FCSTD DOCUMENT  (FreeCAD 0.19R24276 (Git))
Label: bazovina_058
License: All rights reserved
LicenseURL: http://en.wikipedia.org/wiki/All_rights_reserved
objects: Part::Cylinder×904, Part::Compound×379, Part::Cut×288, Part::Box×199, Part::FeaturePython×44, Part::Chamfer×22, Part::Torus×6, Part::Fillet×6, Sketcher::SketchObject×6, Part::Mirroring×5, Part::MultiFuse×4, PartDesign::Pad×3, PartDesign::Body×3, Part::Extrusion×3, Mesh::Feature×2
note: 1875 computed .brp shape members not serialized (recipe doc carries the construction recipe); baked Part::Feature solids carry a one-line shape summary decoded from their .brp

FEATURE [Part::Cylinder] Cylinder074  label="Válec074"
  Angle = 360
  AttacherType = Attacher::AttachEngine3D
  Height = 100
  Placement = pos=(2,3,3) rot=(0,1,0;1.5708rad)
  Radius = 1.5
FEATURE [Part::Cylinder] Cylinder075  label="Válec075"
  Angle = 360
  AttacherType = Attacher::AttachEngine3D
  Height = 100
  Placement = pos=(2,3,3) rot=(0,1,0;1.5708rad)
  Radius = 1.5
FEATURE [Part::Box] Box029  label="Krychle029"
  AttacherType = Attacher::AttachEngine3D
  Height = 6
  Length = 2
  Width = 6
FEATURE [Part::Compound] Compound127
  Links = -> [Box029,Cylinder074]
  Placement = pos=(1536,-22,-8) rot=(0,0,1;0rad)
FEATURE [Part::Box] Box030  label="Krychle030"
  AttacherType = Attacher::AttachEngine3D
  Height = 6
  Length = 2
  Width = 6
FEATURE [Part::Box] Box031  label="Krychle031"
  AttacherType = Attacher::AttachEngine3D
  Height = 6
  Length = 2
  Width = 6
FEATURE [Part::Cylinder] Cylinder076  label="Válec076"
  Angle = 360
  AttacherType = Attacher::AttachEngine3D
  Height = 100
  Placement = pos=(2,3,3) rot=(0,1,0;1.5708rad)
  Radius = 1.5
FEATURE [Part::Compound] Compound125
  Links = -> [Box030,Cylinder076]
  Placement = pos=(1532,-54,4) rot=(0,0,1;0rad)
FEATURE [Part::Cylinder] Cylinder077  label="Válec077"
  Angle = 360
  AttacherType = Attacher::AttachEngine3D
  Height = 100
  Placement = pos=(2,3,3) rot=(0,1,0;1.5708rad)
  Radius = 1.5
FEATURE [Part::Compound] Compound128
  Links = -> [Box031,Cylinder077]
  Placement = pos=(1536,16,-8) rot=(0,0,1;0rad)
FEATURE [Part::Box] Box032  label="Krychle032"
  AttacherType = Attacher::AttachEngine3D
  Height = 6
  Length = 2
  Width = 6
FEATURE [Part::Compound] Compound129
  Links = -> [Box032,Cylinder075]
  Placement = pos=(1532,48,4) rot=(0,0,1;0rad)
FEATURE [Part::Compound] Compound126
  Links = -> [Compound129,Compound128,Compound127,Compound125,Box032,Cylinder075,Box031,Cylinder077,Box029,Cylinder074]
  Placement = pos=(0,-1300,0) rot=(0,0,1;1.5708rad)
FEATURE [Part::Cylinder] Cylinder078  label="Válec078"
  Angle = 360
  AttacherType = Attacher::AttachEngine3D
  Height = 4
  Placement = pos=(-4,3,3) rot=(0,1,0;1.5708rad)
  Radius = 1.5
FEATURE [Part::Compound] Compound130
  Links = -> [Cylinder078]
  Placement = pos=(1532,48,4) rot=(0,0,1;0rad)
FEATURE [Part::Cylinder] Cylinder080  label="Válec080"
  Angle = 360
  AttacherType = Attacher::AttachEngine3D
  Height = 4
  Placement = pos=(-4,3,3) rot=(0,1,0;1.5708rad)
  Radius = 1.5
FEATURE [Part::Compound] Compound133
  Links = -> [Cylinder080]
  Placement = pos=(1532,-54,4) rot=(0,0,1;0rad)
FEATURE [Part::Cylinder] Cylinder081  label="Válec081"
  Angle = 360
  AttacherType = Attacher::AttachEngine3D
  Height = 4
  Placement = pos=(-4,3,3) rot=(0,1,0;1.5708rad)
  Radius = 1.5
FEATURE [Part::Compound] Compound132
  Links = -> [Cylinder081]
  Placement = pos=(1536,16,-8) rot=(0,0,1;0rad)
FEATURE [Part::Cylinder] Cylinder052  label="Válec052"
  Angle = 360
  AttacherType = Attacher::AttachEngine3D
  Height = 50
  Placement = pos=(250,0,-15) rot=(0,0,1;0rad)
  Radius = 1.5
FEATURE [Part::Cylinder] Cylinder053  label="Válec053"
  Angle = 360
  AttacherType = Attacher::AttachEngine3D
  Height = 50
  Placement = pos=(200,50,-15) rot=(0,0,1;1.5708rad)
  Radius = 1.5
FEATURE [Part::Cylinder] Cylinder054  label="Válec054"
  Angle = 360
  AttacherType = Attacher::AttachEngine3D
  Height = 50
  Placement = pos=(235.36,35.36,-16) rot=(0,0,1;0.785398rad)
  Radius = 1.5
FEATURE [Part::Cylinder] Cylinder055  label="Válec055"
  Angle = 360
  AttacherType = Attacher::AttachEngine3D
  Height = 40
  Placement = pos=(202,50,-30) rot=(0,0,1;0rad)
  Radius = 12
FEATURE [Part::Cylinder] Cylinder056  label="Válec056"
  Angle = 360
  AttacherType = Attacher::AttachEngine3D
  Height = 50
  Placement = pos=(235.36,35.36,-40) rot=(0,0,1;0.785398rad)
  Radius = 4
FEATURE [Part::Compound] Compound082
  Links = -> [Cylinder052,Cylinder054,Cylinder053,Cylinder056]
FEATURE [Part::Mirroring] mirror005  label="Compound075 (mirrored)001"
  Base = (0,0,0)
  Normal = (1e-16,-1,0)
  Placement = pos=(500,0,0) rot=(0,0,1;0rad)
  Source = -> Compound082
FEATURE [Part::Cylinder] Cylinder057  label="Válec057"
  Angle = 360
  AttacherType = Attacher::AttachEngine3D
  Height = 40
  Placement = pos=(214,56,-30) rot=(0,0,1;0rad)
  Radius = 12
FEATURE [Part::Box] Box020  label="Krychle020"
  AttacherType = Attacher::AttachEngine3D
  Height = 28
  Length = 46
  Placement = pos=(200,32,-8) rot=(0,0,1;0rad)
  Width = 22
FEATURE [Part::Box] Box021  label="Krychle021"
  AttacherType = Attacher::AttachEngine3D
  Height = 28
  Length = 14
  Placement = pos=(232,0,-8) rot=(0,0,1;0rad)
  Width = 32
FEATURE [Part::Compound] Compound080
  Links = -> [Box021,Box020]
FEATURE [Part::FeaturePython] mirror003_child004  label="Compound075 (mirrored).004"  # WARN: FeaturePython — macro-defined, semantics opaque (R4)
  Base = -> mirror005
  FilterType = 1
  Invert = false
  OverrideMaxVal = 0
  WindowFrom = 80
  WindowTo = 100
  items = 1
FEATURE [Part::FeaturePython] mirror003_child005  label="Compound075 (mirrored).005"  # WARN: FeaturePython — macro-defined, semantics opaque (R4)
  Base = -> mirror005
  FilterType = 1
  Invert = false
  OverrideMaxVal = 0
  WindowFrom = 80
  WindowTo = 100
  items = 0
FEATURE [Part::FeaturePython] mirror003_child006  label="Compound075 (mirrored).006"  # WARN: FeaturePython — macro-defined, semantics opaque (R4)
  Base = -> mirror005
  FilterType = 1
  Invert = false
  OverrideMaxVal = 0
  WindowFrom = 80
  WindowTo = 100
  items = 2
FEATURE [Part::Compound] Compound083
  Links = -> [mirror003_child004,mirror003_child005,mirror003_child006]
FEATURE [Part::FeaturePython] mirror003_child007  label="Compound075 (mirrored).007"  # WARN: FeaturePython — macro-defined, semantics opaque (R4)
  Base = -> mirror005
  FilterType = 1
  Invert = false
  OverrideMaxVal = 0
  WindowFrom = 80
  WindowTo = 100
  items = 3
FEATURE [Part::Cylinder] Cylinder058  label="Válec058"
  Angle = 360
  AttacherType = Attacher::AttachEngine3D
  Height = 40
  Placement = pos=(256,0,-30) rot=(0,0,1;0rad)
  Radius = 10
FEATURE [Part::Compound] Compound081
  Links = -> [Cylinder058,Cylinder057]
FEATURE [Part::Cut] Cut034
  Base = -> Compound080
  Tool = -> Compound081
FEATURE [Part::Cut] Cut035
  Base = -> Cut034
  Tool = -> Cylinder055
FEATURE [Part::Mirroring] mirror004  label="Cut (mirrored)002"
  Base = (40,0,0)
  Normal = (1e-16,-1,0)
  Placement = pos=(500,0,0) rot=(0,0,1;0rad)
  Source = -> Cut035
FEATURE [Part::Cut] Cut036
  Base = -> mirror004
  Tool = -> mirror003_child007
FEATURE [Part::Cut] Cut037
  Base = -> Cut036
  Placement = pos=(800,0,0) rot=(0,0,1;0rad)
  Tool = -> Compound083
FEATURE [Part::Cylinder] Cylinder059  label="Válec059"
  Angle = 360
  AttacherType = Attacher::AttachEngine3D
  Height = 50
  Placement = pos=(235.36,35.36,-16) rot=(0,0,1;0.785398rad)
  Radius = 1.5
FEATURE [Part::Cylinder] Cylinder060  label="Válec060"
  Angle = 360
  AttacherType = Attacher::AttachEngine3D
  Height = 40
  Placement = pos=(202,50,-30) rot=(0,0,1;0rad)
  Radius = 12
FEATURE [Part::Box] Box022  label="Krychle022"
  AttacherType = Attacher::AttachEngine3D
  Height = 28
  Length = 32
  Placement = pos=(200,32,-8) rot=(0,0,1;0rad)
  Width = 22
FEATURE [Part::Box] Box023  label="Krychle023"
  AttacherType = Attacher::AttachEngine3D
  Height = 28
  Length = 14
  Placement = pos=(232,0,-8) rot=(0,0,1;0rad)
  Width = 54
FEATURE [Part::Cylinder] Cylinder061  label="Válec061"
  Angle = 360
  AttacherType = Attacher::AttachEngine3D
  Height = 50
  Placement = pos=(250,0,-15) rot=(0,0,1;0rad)
  Radius = 1.5
FEATURE [Part::Cylinder] Cylinder062  label="Válec062"
  Angle = 360
  AttacherType = Attacher::AttachEngine3D
  Height = 40
  Placement = pos=(256,0,-30) rot=(0,0,1;0rad)
  Radius = 10
FEATURE [Part::Cylinder] Cylinder063  label="Válec063"
  Angle = 360
  AttacherType = Attacher::AttachEngine3D
  Height = 50
  Placement = pos=(200,50,-15) rot=(0,0,1;1.5708rad)
  Radius = 1.5
FEATURE [Part::Cylinder] Cylinder064  label="Válec064"
  Angle = 360
  AttacherType = Attacher::AttachEngine3D
  Height = 50
  Placement = pos=(235.36,35.36,-40) rot=(0,0,1;0.785398rad)
  Radius = 4
FEATURE [Part::Cylinder] Cylinder065  label="Válec065"
  Angle = 360
  AttacherType = Attacher::AttachEngine3D
  Height = 40
  Placement = pos=(214,56,-30) rot=(0,0,1;0rad)
  Radius = 12
FEATURE [Part::Box] Box024  label="Krychle024"
  AttacherType = Attacher::AttachEngine3D
  Height = 2.5
  Length = 8
  Placement = pos=(55,-3,22) rot=(0,0,1;0rad)
  Width = 6
FEATURE [Part::Cylinder] Cylinder066  label="Válec066"
  Angle = 360
  AttacherType = Attacher::AttachEngine3D
  Height = 10
  Radius = 54
FEATURE [Part::Compound] Compound084
  Links = -> [Box023,Box022]
FEATURE [Part::Compound] Compound085
  Links = -> [Cylinder062,Cylinder065]
FEATURE [Part::Cut] Cut038
  Base = -> Compound084
  Tool = -> Compound085
FEATURE [Part::Cut] Cut039
  Base = -> Cut038
  Tool = -> Cylinder060
FEATURE [Part::Mirroring] mirror006  label="Cut (mirrored)003"
  Base = (40,0,0)
  Normal = (1e-16,-1,0)
  Source = -> Cut039
FEATURE [Part::Compound] Compound086
  Links = -> [Cylinder061,Cylinder059,Cylinder063,Cylinder064]
  Placement = pos=(500,0,0) rot=(0,0,1;0rad)
FEATURE [Part::FeaturePython] Compound078_child004  label="Compound078.004"  # WARN: FeaturePython — macro-defined, semantics opaque (R4)
  Base = -> Compound086
  FilterType = 1
  Invert = false
  OverrideMaxVal = 0
  WindowFrom = 80
  WindowTo = 100
  items = 3
FEATURE [Part::FeaturePython] Compound078_child005  label="Compound078.005"  # WARN: FeaturePython — macro-defined, semantics opaque (R4)
  Base = -> Compound086
  FilterType = 1
  Invert = false
  OverrideMaxVal = 0
  WindowFrom = 80
  WindowTo = 100
  items = 1
FEATURE [Part::FeaturePython] Compound078_child006  label="Compound078.006"  # WARN: FeaturePython — macro-defined, semantics opaque (R4)
  Base = -> Compound086
  FilterType = 1
  Invert = false
  OverrideMaxVal = 0
  WindowFrom = 80
  WindowTo = 100
  items = 2
FEATURE [Part::Mirroring] mirror007  label="Cut (mirrored)001 (mirrored)001"
  Base = (0,0,0)
  Normal = (1e-16,-1,0)
  Placement = pos=(500,0,0) rot=(0,0,1;0rad)
  Source = -> mirror006
FEATURE [Part::Cut] Cut040
  Base = -> mirror007
  Tool = -> Compound078_child004
FEATURE [Part::FeaturePython] Compound078_child007  label="Compound078.007"  # WARN: FeaturePython — macro-defined, semantics opaque (R4)
  Base = -> Compound086
  FilterType = 1
  Invert = false
  OverrideMaxVal = 0
  WindowFrom = 80
  WindowTo = 100
  items = 0
FEATURE [Part::FeaturePython] wormgear020  # WARN: FeaturePython — macro-defined, semantics opaque (R4)
  AttacherType = Attacher::AttachEngine3D
  beta = 28.8108
  clearance = 0.25
  diameter = 60
  head = 0
  height = 20
  module = 1
  pressure_angle = 20
  reverse_pitch = false
  teeth = 33
  version = 0.0.3
FEATURE [Part::FeaturePython] Tube007  # WARN: FeaturePython — macro-defined, semantics opaque (R4)
  AttacherType = Attacher::AttachEngine3D
  Height = 8
  InnerRadius = 32
  OuterRadius = 46
  Placement = pos=(200,0,-8) rot=(0,0,1;0rad)
FEATURE [Part::Compound] Compound087
  Links = -> [Compound078_child006,Compound078_child007,Compound078_child005]
FEATURE [Part::Cut] Cut041
  Base = -> Cut040
  Placement = pos=(800,0,0) rot=(0,0,1;0rad)
  Tool = -> Compound087
FEATURE [Part::Cylinder] Cylinder067  label="Válec067"
  Angle = 360
  AttacherType = Attacher::AttachEngine3D
  Height = 23
  Placement = pos=(59,0,0) rot=(0,0,1;0rad)
  Radius = 1.5
FEATURE [Part::Compound] Compound088
  Links = -> [Box024,Cylinder067]
  Placement = pos=(-6.36396,-6.36396,0) rot=(0,0,1;0.785398rad)
FEATURE [Part::Compound] Compound089
  Links = -> [Box024,Cylinder067]
  Placement = pos=(-9,0,0) rot=(0,0,1;0rad)
FEATURE [Part::Compound] Compound090
  Links = -> [Box024,Cylinder067]
  Placement = pos=(6.36396,6.36396,0) rot=(0,0,1;3.92699rad)
FEATURE [Part::Cylinder] Cylinder068  label="Válec068"
  Angle = 360
  AttacherType = Attacher::AttachEngine3D
  Height = 10
  Radius = 46
FEATURE [Part::Box] Box025  label="Krychle025"
  AttacherType = Attacher::AttachEngine3D
  Height = 6
  Length = 2
  Width = 6
FEATURE [Part::Cylinder] Cylinder069  label="Válec069"
  Angle = 360
  AttacherType = Attacher::AttachEngine3D
  Height = 100
  Placement = pos=(2,3,3) rot=(0,1,0;1.5708rad)
  Radius = 1.5
FEATURE [Part::Compound] Compound094
  Links = -> [Box024,Cylinder067]
  Placement = pos=(1e-15,-9,0) rot=(0,0,1;1.5708rad)
FEATURE [Part::Compound] Compound095
  Links = -> [Box024,Cylinder067]
  Placement = pos=(6.36396,-6.36396,0) rot=(0,0,1;2.35619rad)
FEATURE [Part::Compound] Compound096
  Links = -> [Box024,Cylinder067]
  Placement = pos=(-3e-15,9,0) rot=(0,0,-1;1.5708rad)
FEATURE [Part::Compound] Compound097
  Links = -> [Box024,Cylinder067]
  Placement = pos=(-6.36396,6.36396,0) rot=(0,0,-1;0.785398rad)
FEATURE [Part::Compound] Compound098
  Links = -> [Box024,Cylinder067]
  Placement = pos=(9,3e-15,0) rot=(0,0,1;3.14159rad)
FEATURE [Part::Compound] Compound092
  Links = -> [Compound089,Compound088,Compound094,Compound095,Compound098,Compound090,Compound096,Compound097]
  Placement = pos=(200,0,0) rot=(0,0,1;0rad)
FEATURE [Part::Compound] Compound101
  Links = -> [Box025,Cylinder069]
  Placement = pos=(1532,48,4) rot=(0,0,1;0rad)
FEATURE [Part::FeaturePython] wormgear021  # WARN: FeaturePython — macro-defined, semantics opaque (R4)
  AttacherType = Attacher::AttachEngine3D
  beta = 28.8108
  clearance = 0.25
  diameter = 60
  head = 0
  height = 20
  module = 1
  pressure_angle = 20
  reverse_pitch = true
  teeth = 33
  version = 0.0.3
FEATURE [Part::Cut] Cut042
  Base = -> Cylinder066
  Placement = pos=(0,0,10) rot=(0,0,1;0.034907rad)
  Tool = -> wormgear021
FEATURE [Part::Cut] Cut043
  Base = -> Cylinder068
  Tool = -> wormgear020
FEATURE [Part::Compound] Compound091
  Links = -> [Cut042,Cut043]
  Placement = pos=(200,0,0) rot=(0,0,1;0rad)
FEATURE [Part::Cut] Cut044
  Base = -> Compound091
  Tool = -> Compound092
FEATURE [Part::Compound] Compound093
  Links = -> [Cut044,Tube007]
  Placement = pos=(1300,0,0) rot=(0,0,1;0rad)
FEATURE [Part::Compound] Compound099
  Links = -> [Cut037,Cut041,Compound093]
FEATURE [Part::Box] Box026  label="Krychle026"
  AttacherType = Attacher::AttachEngine3D
  Height = 6
  Length = 2
  Width = 6
FEATURE [Part::Cylinder] Cylinder070  label="Válec070"
  Angle = 360
  AttacherType = Attacher::AttachEngine3D
  Height = 100
  Placement = pos=(2,3,3) rot=(0,1,0;1.5708rad)
  Radius = 1.5
FEATURE [Part::Compound] Compound102
  Links = -> [Box026,Cylinder070]
  Placement = pos=(1536,16,-8) rot=(0,0,1;0rad)
FEATURE [Part::Box] Box027  label="Krychle027"
  AttacherType = Attacher::AttachEngine3D
  Height = 6
  Length = 2
  Width = 6
FEATURE [Part::Cylinder] Cylinder071  label="Válec071"
  Angle = 360
  AttacherType = Attacher::AttachEngine3D
  Height = 100
  Placement = pos=(2,3,3) rot=(0,1,0;1.5708rad)
  Radius = 1.5
FEATURE [Part::Compound] Compound103
  Links = -> [Box027,Cylinder071]
  Placement = pos=(1536,-22,-8) rot=(0,0,1;0rad)
FEATURE [Part::Box] Box028  label="Krychle028"
  AttacherType = Attacher::AttachEngine3D
  Height = 6
  Length = 2
  Width = 6
FEATURE [Part::Cylinder] Cylinder072  label="Válec072"
  Angle = 360
  AttacherType = Attacher::AttachEngine3D
  Height = 100
  Placement = pos=(2,3,3) rot=(0,1,0;1.5708rad)
  Radius = 1.5
FEATURE [Part::Compound] Compound104
  Links = -> [Box028,Cylinder072]
  Placement = pos=(1532,-54,4) rot=(0,0,1;0rad)
FEATURE [Part::Box] Box  label="Krychle"
  AttacherType = Attacher::AttachEngine3D
  Height = 2
  Length = 8
  Placement = pos=(1496,-3,0) rot=(0,0,1;0rad)
  Width = 6
FEATURE [Part::Cylinder] Cylinder  label="Válec"
  Angle = 360
  AttacherType = Attacher::AttachEngine3D
  Height = 60
  Placement = pos=(1500,0,2) rot=(0,0,1;0rad)
  Radius = 1.5
FEATURE [Part::Compound] Compound105
  Links = -> [Box,Cylinder]
  Placement = pos=(146.516,-560.631,-2) rot=(0.980785,0.19509,0;3.14159rad)
FEATURE [Part::Compound] Compound106
  Links = -> [Box,Cylinder]
  Placement = pos=(939.369,-1353.48,-2) rot=(0.83147,0.55557,0;3.14159rad)
FEATURE [Part::Compound] Compound107
  Links = -> [Box,Cylinder]
  Placement = pos=(2060.63,-1353.48,-2) rot=(0.55557,0.83147,0;3.14159rad)
FEATURE [Part::Compound] Compound108
  Links = -> [Box,Cylinder]
  Placement = pos=(2853.48,-560.631,-2) rot=(0.19509,0.980785,0;3.14159rad)
FEATURE [Part::Compound] Compound109
  Links = -> [Box,Cylinder]
  Placement = pos=(2853.48,560.631,-2) rot=(-0.19509,0.980785,0;3.14159rad)
FEATURE [Part::Compound] Compound110
  Links = -> [Box,Cylinder]
  Placement = pos=(2060.63,1353.48,-2) rot=(-0.55557,0.83147,0;3.14159rad)
FEATURE [Part::Compound] Compound111
  Links = -> [Box,Cylinder]
  Placement = pos=(939.369,1353.48,-2) rot=(0.83147,-0.55557,0;3.14159rad)
FEATURE [Part::Compound] Compound112
  Links = -> [Box,Cylinder]
  Placement = pos=(146.516,560.631,-2) rot=(0.980785,-0.19509,0;3.14159rad)
FEATURE [Part::Compound] Compound113
  Links = -> [Compound105,Compound106,Compound107,Compound108,Compound109,Compound110,Compound111,Compound112]
  Placement = pos=(300,0,0) rot=(0,0,1;0rad)
FEATURE [Part::Compound] Compound114
  Links = -> [Compound101,Compound102,Compound103,Compound104,Box025,Cylinder069,Box026,Cylinder070,Box027,Cylinder071]
FEATURE [Part::Cut] Cut045
  Base = -> Compound099
  Tool = -> Compound114
FEATURE [Part::MultiFuse] Fusion
  Placement = pos=(200,0,0) rot=(0,0,1;0rad)
  Shapes = -> [Cut045]
FEATURE [Part::Cylinder] Cylinder073  label="Válec073"
  Angle = 360
  AttacherType = Attacher::AttachEngine3D
  Height = 4
  Placement = pos=(1500,0,-4) rot=(0,0,1;0rad)
  Radius = 1.5
FEATURE [Part::Compound] Compound115
  Links = -> [Cylinder073]
  Placement = pos=(939.369,-1353.48,-2) rot=(0.83147,0.55557,0;3.14159rad)
FEATURE [Part::Compound] Compound116
  Links = -> [Cylinder073]
  Placement = pos=(2060.63,-1353.48,-2) rot=(0.55557,0.83147,0;3.14159rad)
FEATURE [Part::Compound] Compound117
  Links = -> [Cylinder073]
  Placement = pos=(146.516,-560.631,-2) rot=(0.980785,0.19509,0;3.14159rad)
FEATURE [Part::Cylinder] Cylinder082  label="Válec082"
  Angle = 360
  AttacherType = Attacher::AttachEngine3D
  Height = 100
  Placement = pos=(2,3,3) rot=(0,1,0;1.5708rad)
  Radius = 1.5
FEATURE [Part::Cylinder] Cylinder083  label="Válec083"
  Angle = 360
  AttacherType = Attacher::AttachEngine3D
  Height = 100
  Placement = pos=(2,3,3) rot=(0,1,0;1.5708rad)
  Radius = 1.5
FEATURE [Part::Box] Box033  label="Krychle033"
  AttacherType = Attacher::AttachEngine3D
  Height = 6
  Length = 2
  Width = 6
FEATURE [Part::Compound] Compound118
  Links = -> [Cylinder073]
  Placement = pos=(2853.48,-560.631,-2) rot=(0.19509,0.980785,0;3.14159rad)
FEATURE [Part::Compound] Compound119
  Links = -> [Cylinder073]
  Placement = pos=(146.516,560.631,-2) rot=(0.980785,-0.19509,0;3.14159rad)
FEATURE [Part::Compound] Compound120
  Links = -> [Cylinder073]
  Placement = pos=(2060.63,1353.48,-2) rot=(-0.55557,0.83147,0;3.14159rad)
FEATURE [Part::Compound] Compound121
  Links = -> [Cylinder073]
  Placement = pos=(939.369,1353.48,-2) rot=(0.83147,-0.55557,0;3.14159rad)
FEATURE [Part::Compound] Compound122
  Links = -> [Cylinder073]
  Placement = pos=(2853.48,560.631,-2) rot=(-0.19509,0.980785,0;3.14159rad)
FEATURE [Part::Compound] Compound123
  Links = -> [Compound117,Compound115,Compound116,Compound118,Compound122,Compound120,Compound121,Compound119]
  Placement = pos=(300,0,0) rot=(0,0,1;0rad)
FEATURE [Part::Compound] Compound124
  Links = -> [Compound123,Compound113]
  Placement = pos=(-100,0,0) rot=(0,0,1;0rad)
FEATURE [Part::Compound] Compound138
  Links = -> [Box033,Cylinder082]
  Placement = pos=(1536,-22,-8) rot=(0,0,1;0rad)
FEATURE [Part::MultiFuse] Fusion001
  Shapes = -> [Compound124]
FEATURE [Part::Cut] Cut046
  Base = -> Fusion
  Tool = -> Fusion001
FEATURE [Part::Box] Box034  label="Krychle034"
  AttacherType = Attacher::AttachEngine3D
  Height = 6
  Length = 2
  Width = 6
FEATURE [Part::Box] Box035  label="Krychle035"
  AttacherType = Attacher::AttachEngine3D
  Height = 6
  Length = 2
  Width = 6
FEATURE [Part::Cylinder] Cylinder084  label="Válec084"
  Angle = 360
  AttacherType = Attacher::AttachEngine3D
  Height = 100
  Placement = pos=(2,3,3) rot=(0,1,0;1.5708rad)
  Radius = 1.5
FEATURE [Part::Compound] Compound136
  Links = -> [Box034,Cylinder084]
  Placement = pos=(1532,-54,4) rot=(0,0,1;0rad)
FEATURE [Part::Cylinder] Cylinder085  label="Válec085"
  Angle = 360
  AttacherType = Attacher::AttachEngine3D
  Height = 100
  Placement = pos=(2,3,3) rot=(0,1,0;1.5708rad)
  Radius = 1.5
FEATURE [Part::Compound] Compound139
  Links = -> [Box035,Cylinder085]
  Placement = pos=(1536,16,-8) rot=(0,0,1;0rad)
FEATURE [Part::Box] Box036  label="Krychle036"
  AttacherType = Attacher::AttachEngine3D
  Height = 6
  Length = 2
  Width = 6
FEATURE [Part::Compound] Compound140
  Links = -> [Box036,Cylinder083]
  Placement = pos=(1532,48,4) rot=(0,0,1;0rad)
FEATURE [Part::Compound] Compound137
  Links = -> [Compound140,Compound139,Compound138,Compound136,Box036,Cylinder083,Box035,Cylinder085,Box033,Cylinder082]
  Placement = pos=(300,0,0) rot=(0,0,1;0rad)
FEATURE [Part::Cylinder] Cylinder086  label="Válec086"
  Angle = 360
  AttacherType = Attacher::AttachEngine3D
  Height = 4
  Placement = pos=(-4,3,3) rot=(0,1,0;1.5708rad)
  Radius = 1.5
FEATURE [Part::Compound] Compound141
  Links = -> [Cylinder086]
  Placement = pos=(1532,48,4) rot=(0,0,1;0rad)
FEATURE [Part::Cylinder] Cylinder087  label="Válec087"
  Angle = 360
  AttacherType = Attacher::AttachEngine3D
  Height = 4
  Placement = pos=(-4,3,3) rot=(0,1,0;1.5708rad)
  Radius = 1.5
FEATURE [Part::Compound] Compound142
  Links = -> [Cylinder087]
  Placement = pos=(1536,-22,-8) rot=(0,0,1;0rad)
FEATURE [Part::Cylinder] Cylinder088  label="Válec088"
  Angle = 360
  AttacherType = Attacher::AttachEngine3D
  Height = 4
  Placement = pos=(-4,3,3) rot=(0,1,0;1.5708rad)
  Radius = 1.5
FEATURE [Part::Compound] Compound144
  Links = -> [Cylinder088]
  Placement = pos=(1532,-54,4) rot=(0,0,1;0rad)
FEATURE [Part::Cylinder] Cylinder089  label="Válec089"
  Angle = 360
  AttacherType = Attacher::AttachEngine3D
  Height = 4
  Placement = pos=(-4,3,3) rot=(0,1,0;1.5708rad)
  Radius = 1.5
FEATURE [Part::Compound] Compound143
  Links = -> [Cylinder089]
  Placement = pos=(1536,16,-8) rot=(0,0,1;0rad)
FEATURE [Part::Compound] Compound145
  Links = -> [Compound141,Compound142,Compound143,Compound144,Cylinder086,Cylinder087,Cylinder089]
  Placement = pos=(300,0,0) rot=(0,0,1;0rad)
FEATURE [Part::Compound] Compound146
  Links = -> [Compound145,Compound137]
  Placement = pos=(-100,0,0) rot=(0,0,1;0rad)
FEATURE [Part::MultiFuse] Fusion003
  Shapes = -> [Compound146]
FEATURE [Part::Cut] Cut047  label="finalo_nefiletovane"
  Base = -> Cut046
  Placement = pos=(0,-1500,0) rot=(0,0,1;1.5708rad)
  Tool = -> Fusion003
FEATURE [Part::FeaturePython] Tube002  # WARN: FeaturePython — macro-defined, semantics opaque (R4)
  AttacherType = Attacher::AttachEngine3D
  Height = 17
  InnerRadius = 47
  OuterRadius = 54
  Placement = pos=(0,0,20) rot=(0,0,1;0rad)
FEATURE [Part::Cylinder] Cylinder006  label="Válec006"
  Angle = 360
  AttacherType = Attacher::AttachEngine3D
  Height = 10
  Placement = pos=(-47,0,30) rot=(0,0,1;0rad)
  Radius = 3.5
FEATURE [Part::Cylinder] Cylinder016  label="Válec016"
  Angle = 360
  AttacherType = Attacher::AttachEngine3D
  Height = 23
  Placement = pos=(59,0,-1) rot=(0,0,1;0rad)
  Radius = 1.5
FEATURE [Part::Box] Box007  label="Krychle007"
  AttacherType = Attacher::AttachEngine3D
  Height = 2
  Length = 8
  Placement = pos=(55,-2.8,22) rot=(0,0,1;0rad)
  Width = 5.6
FEATURE [Part::Cylinder] Cylinder113  label="Válec113"
  Angle = 360
  AttacherType = Attacher::AttachEngine3D
  Height = 17
  Placement = pos=(0,0,20) rot=(0,0,1;0rad)
  Radius = 54
FEATURE [Part::Box] Box037  label="Krychle037"
  AttacherType = Attacher::AttachEngine3D
  Height = 17
  Length = 108
  Placement = pos=(-54,-46,20) rot=(0,0,1;0rad)
  Width = 46
FEATURE [Part::Box] Box038  label="Krychle038"
  AttacherType = Attacher::AttachEngine3D
  Height = 6
  Length = 2
  Width = 6
FEATURE [Part::Cylinder] Cylinder114  label="Válec114"
  Angle = 360
  AttacherType = Attacher::AttachEngine3D
  Height = 4
  Placement = pos=(-4,3,3) rot=(0,1,0;1.5708rad)
  Radius = 1.5
FEATURE [Part::Cylinder] Cylinder115  label="Válec115"
  Angle = 360
  AttacherType = Attacher::AttachEngine3D
  Height = 100
  Placement = pos=(2,3,3) rot=(0,1,0;1.5708rad)
  Radius = 1.5
FEATURE [Part::Cylinder] Cylinder116  label="Válec116"
  Angle = 360
  AttacherType = Attacher::AttachEngine3D
  Height = 100
  Placement = pos=(2,3,3) rot=(0,1,0;1.5708rad)
  Radius = 1.5
FEATURE [Part::Box] Box039  label="Krychle039"
  AttacherType = Attacher::AttachEngine3D
  Height = 6
  Length = 2
  Width = 6
FEATURE [Part::Torus] Torus001  label="Anuloid001"
  Angle1 = -180
  Angle2 = 180
  Angle3 = 360
  AttacherType = Attacher::AttachEngine3D
  Placement = pos=(0,0,29) rot=(0,0,1;0rad)
  Radius1 = 46
  Radius2 = 3.1
FEATURE [Part::Cut] Cut009
  Base = -> Tube002
  Tool = -> Torus001
FEATURE [Part::Cut] Cut010
  Base = -> Cut009
  Placement = pos=(0,200,0) rot=(0,0,1;0rad)
  Tool = -> Cylinder006
FEATURE [Part::Compound] Compound026
  Links = -> [Box007,Cylinder016]
  Placement = pos=(6.36396,-6.36396,0) rot=(0,0,1;2.35619rad)
FEATURE [Part::Compound] Compound023
  Links = -> [Box007,Cylinder016]
  Placement = pos=(-9,0,0) rot=(0,0,1;0rad)
FEATURE [Part::Compound] Compound024
  Links = -> [Box007,Cylinder016]
  Placement = pos=(-6.36396,-6.36396,0) rot=(0,0,1;0.785398rad)
FEATURE [Part::Compound] Compound025
  Links = -> [Box007,Cylinder016]
  Placement = pos=(1e-15,-9,0) rot=(0,0,1;1.5708rad)
FEATURE [Part::Compound] Compound027
  Links = -> [Box007,Cylinder016]
  Placement = pos=(9,3e-15,0) rot=(0,0,1;3.14159rad)
FEATURE [Part::Compound] Compound030
  Links = -> [Box007,Cylinder016]
  Placement = pos=(-6.36396,6.36396,0) rot=(0,0,-1;0.785398rad)
FEATURE [Part::Compound] Compound029
  Links = -> [Box007,Cylinder016]
  Placement = pos=(-3e-15,9,0) rot=(0,0,-1;1.5708rad)
FEATURE [Part::Compound] Compound028
  Links = -> [Box007,Cylinder016]
  Placement = pos=(6.36396,6.36396,0) rot=(0,0,1;3.92699rad)
FEATURE [Part::Compound] Compound031
  Links = -> [Compound023,Compound024,Compound025,Compound026,Compound027,Compound028,Compound029,Compound030]
  Placement = pos=(0,200,0) rot=(0,0,1;0rad)
FEATURE [Part::Cut] Cut015
  Base = -> Cut010
  Tool = -> Compound031
FEATURE [Part::Cut] Cut
  Base = -> Box037
  Placement = pos=(0,200,0) rot=(0,0,1;0rad)
  Tool = -> Cylinder113
FEATURE [Part::Compound] Compound
  Links = -> [Box038,Cylinder114,Cylinder115]
  Placement = pos=(48,166,27) rot=(0,0,-1;1.5708rad)
FEATURE [Part::Cylinder] Cylinder117  label="Válec117"
  Angle = 360
  AttacherType = Attacher::AttachEngine3D
  Height = 4
  Placement = pos=(-4,3,3) rot=(0,1,0;1.5708rad)
  Radius = 1.5
FEATURE [Part::Compound] Compound032
  Links = -> [Box039,Cylinder117,Cylinder116]
  Placement = pos=(-54,166,27) rot=(0,0,-1;1.5708rad)
FEATURE [Part::MultiFuse] Fusion004
  Shapes = -> [Compound,Compound032]
FEATURE [Part::Cut] Cut016
  Base = -> Cut
  Tool = -> Fusion004
FEATURE [Part::Compound] Compound033  label="lozo_harmo"
  Links = -> [Cut016,Cut015]
  Placement = pos=(0,400,0) rot=(0,0,1;3.14159rad)
FEATURE [Part::Compound] Compound147
  Links = -> [Compound033,Cut047]
FEATURE [Part::Cylinder] Cylinder079  label="Válec079"
  Angle = 360
  AttacherType = Attacher::AttachEngine3D
  Height = 4
  Placement = pos=(-4,3,3) rot=(0,1,0;1.5708rad)
  Radius = 1.5
FEATURE [Part::Compound] Compound131
  Links = -> [Cylinder079]
  Placement = pos=(1536,-22,-8) rot=(0,0,1;0rad)
FEATURE [Part::Compound] Compound134
  Links = -> [Compound130,Compound131,Compound132,Compound133,Cylinder078,Cylinder079,Cylinder081]
  Placement = pos=(300,0,0) rot=(0,0,1;0rad)
FEATURE [Part::FeaturePython] Tube  # WARN: FeaturePython — macro-defined, semantics opaque (R4)
  AttacherType = Attacher::AttachEngine3D
  Height = 10
  InnerRadius = 40
  OuterRadius = 59
FEATURE [Part::Compound] Compound148
  Links = -> [Compound126,Compound134,Compound147]
  Placement = pos=(0,14,-246) rot=(1,0,0;1.5708rad)
FEATURE [Part::FeaturePython] Tube008  # WARN: FeaturePython — macro-defined, semantics opaque (R4)
  AttacherType = Attacher::AttachEngine3D
  Height = 3
  InnerRadius = 32
  OuterRadius = 46
  Placement = pos=(0,0,-18) rot=(0,0,1;0rad)
FEATURE [Part::Cylinder] Cylinder134  label="Válec134"
  Angle = 360
  AttacherType = Attacher::AttachEngine3D
  Height = 20
  Placement = pos=(-13.3939,32.3358,-22) rot=(0,0,1;1.96349rad)
  Radius = 1.5
FEATURE [Part::Cylinder] Cylinder135  label="Válec135"
  Angle = 360
  AttacherType = Attacher::AttachEngine3D
  Height = 20
  Placement = pos=(32.3358,-13.3939,-22) rot=(0,0,-1;0.392699rad)
  Radius = 1.5
FEATURE [Part::Cylinder] Cylinder136  label="Válec136"
  Angle = 360
  AttacherType = Attacher::AttachEngine3D
  Height = 20
  Placement = pos=(-32.3358,13.3939,-22) rot=(0,0,1;2.74889rad)
  Radius = 1.5
FEATURE [Part::Cylinder] Cylinder137  label="Válec137"
  Angle = 360
  AttacherType = Attacher::AttachEngine3D
  Height = 20
  Placement = pos=(-13.3939,-32.3358,-22) rot=(0,0,-1;1.96349rad)
  Radius = 1.5
FEATURE [Part::Cylinder] Cylinder138  label="Válec138"
  Angle = 360
  AttacherType = Attacher::AttachEngine3D
  Height = 20
  Placement = pos=(13.3939,-32.3358,-22) rot=(0,0,-1;1.1781rad)
  Radius = 1.5
FEATURE [Part::Cylinder] Cylinder139  label="Válec139"
  Angle = 360
  AttacherType = Attacher::AttachEngine3D
  Height = 20
  Placement = pos=(-32.3358,-13.3939,-22) rot=(0,0,1;3.53429rad)
  Radius = 1.5
FEATURE [Part::Cylinder] Cylinder140  label="Válec140"
  Angle = 360
  AttacherType = Attacher::AttachEngine3D
  Height = 20
  Placement = pos=(32.3358,13.3939,-22) rot=(0,0,1;0.392699rad)
  Radius = 1.5
FEATURE [Part::Cylinder] Cylinder141  label="Válec141"
  Angle = 360
  AttacherType = Attacher::AttachEngine3D
  Height = 20
  Placement = pos=(13.3939,32.3358,-22) rot=(0,0,1;1.1781rad)
  Radius = 1.5
FEATURE [Part::Compound] Compound205
  Links = -> [Cylinder140,Cylinder141,Cylinder134,Cylinder136,Cylinder139,Cylinder137,Cylinder138,Cylinder135]
  Placement = pos=(0,0,2) rot=(0,0,1;0rad)
FEATURE [Part::Cut] Cut065  label="dilatacka_podmotorni"
  Base = -> Tube008
  Placement = pos=(0,7,-46) rot=(0.57735,0.57735,-0.57735;2.0944rad)
  Tool = -> Compound205
FEATURE [Part::Cylinder] Cylinder142  label="Válec142"
  Angle = 360
  AttacherType = Attacher::AttachEngine3D
  Height = 20
  Placement = pos=(32.3358,13.3939,-22) rot=(0,0,1;0.392699rad)
  Radius = 1.5
FEATURE [Part::Cylinder] Cylinder143  label="Válec143"
  Angle = 360
  AttacherType = Attacher::AttachEngine3D
  Height = 20
  Placement = pos=(13.3939,32.3358,-22) rot=(0,0,1;1.1781rad)
  Radius = 1.5
FEATURE [Part::Cylinder] Cylinder144  label="Válec144"
  Angle = 360
  AttacherType = Attacher::AttachEngine3D
  Height = 20
  Placement = pos=(-13.3939,32.3358,-22) rot=(0,0,1;1.96349rad)
  Radius = 1.5
FEATURE [Part::Cylinder] Cylinder145  label="Válec145"
  Angle = 360
  AttacherType = Attacher::AttachEngine3D
  Height = 20
  Placement = pos=(-32.3358,13.3939,-22) rot=(0,0,1;2.74889rad)
  Radius = 1.5
FEATURE [Part::Cylinder] Cylinder118  label="Válec118"
  Angle = 360
  AttacherType = Attacher::AttachEngine3D
  Height = 20
  Placement = pos=(-32.3358,-13.3939,-22) rot=(0,0,1;3.53429rad)
  Radius = 1.5
FEATURE [Part::Cylinder] Cylinder119  label="Válec119"
  Angle = 360
  AttacherType = Attacher::AttachEngine3D
  Height = 20
  Placement = pos=(-13.3939,-32.3358,-22) rot=(0,0,-1;1.96349rad)
  Radius = 1.5
FEATURE [Part::Cylinder] Cylinder120  label="Válec120"
  Angle = 360
  AttacherType = Attacher::AttachEngine3D
  Height = 20
  Placement = pos=(13.3939,-32.3358,-22) rot=(0,0,-1;1.1781rad)
  Radius = 1.5
FEATURE [Part::Cylinder] Cylinder121  label="Válec121"
  Angle = 360
  AttacherType = Attacher::AttachEngine3D
  Height = 20
  Placement = pos=(32.3358,-13.3939,-22) rot=(0,0,-1;0.392699rad)
  Radius = 1.5
FEATURE [Part::Compound] Compound206
  Links = -> [Cylinder142,Cylinder143,Cylinder144,Cylinder145,Cylinder118,Cylinder119,Cylinder120,Cylinder121]
  Placement = pos=(0,0,8) rot=(0,0,1;0rad)
FEATURE [Part::Cylinder] Cylinder122  label="Válec122"
  Angle = 360
  AttacherType = Attacher::AttachEngine3D
  Height = 3
  Placement = pos=(-13.3939,32.3358,-22) rot=(0,0,1;1.96349rad)
  Radius = 3
FEATURE [Part::Cylinder] Cylinder123  label="Válec123"
  Angle = 360
  AttacherType = Attacher::AttachEngine3D
  Height = 3
  Placement = pos=(32.3358,-13.3939,-22) rot=(0,0,-1;0.392699rad)
  Radius = 3
FEATURE [Part::Cylinder] Cylinder124  label="Válec124"
  Angle = 360
  AttacherType = Attacher::AttachEngine3D
  Height = 3
  Placement = pos=(-32.3358,13.3939,-22) rot=(0,0,1;2.74889rad)
  Radius = 3
FEATURE [Part::Cylinder] Cylinder125  label="Válec125"
  Angle = 360
  AttacherType = Attacher::AttachEngine3D
  Height = 3
  Placement = pos=(-13.3939,-32.3358,-22) rot=(0,0,-1;1.96349rad)
  Radius = 3
FEATURE [Part::FeaturePython] Tube009  # WARN: FeaturePython — macro-defined, semantics opaque (R4)
  AttacherType = Attacher::AttachEngine3D
  Height = 5
  InnerRadius = 12
  OuterRadius = 46
FEATURE [Part::FeaturePython] Tube010  # WARN: FeaturePython — macro-defined, semantics opaque (R4)
  AttacherType = Attacher::AttachEngine3D
  Height = 11
  InnerRadius = 12
  OuterRadius = 20
  Placement = pos=(0,0,5) rot=(0,0,1;0rad)
FEATURE [Part::FeaturePython] Tube011  # WARN: FeaturePython — macro-defined, semantics opaque (R4)
  AttacherType = Attacher::AttachEngine3D
  Height = 3
  InnerRadius = 19
  OuterRadius = 24.8
  Placement = pos=(0,0,5) rot=(0,0,1;0rad)
FEATURE [Part::Cylinder] Cylinder126  label="Válec126"
  Angle = 360
  AttacherType = Attacher::AttachEngine3D
  Height = 3
  Placement = pos=(13.3939,-32.3358,-22) rot=(0,0,-1;1.1781rad)
  Radius = 3
FEATURE [Part::Cylinder] Cylinder127  label="Válec127"
  Angle = 360
  AttacherType = Attacher::AttachEngine3D
  Height = 3
  Placement = pos=(-32.3358,-13.3939,-22) rot=(0,0,1;3.53429rad)
  Radius = 3
FEATURE [Part::Cylinder] Cylinder128  label="Válec128"
  Angle = 360
  AttacherType = Attacher::AttachEngine3D
  Height = 3
  Placement = pos=(32.3358,13.3939,-22) rot=(0,0,1;0.392699rad)
  Radius = 3
FEATURE [Part::Cylinder] Cylinder129  label="Válec129"
  Angle = 360
  AttacherType = Attacher::AttachEngine3D
  Height = 3
  Placement = pos=(13.3939,32.3358,-22) rot=(0,0,1;1.1781rad)
  Radius = 3
FEATURE [Part::Compound] Compound200
  Links = -> [Cylinder128,Cylinder129,Cylinder122,Cylinder124,Cylinder127,Cylinder125,Cylinder126,Cylinder123]
  Placement = pos=(0,0,24) rot=(0,0,1;0rad)
FEATURE [Part::Box] Box040  label="Krychle040"
  AttacherType = Attacher::AttachEngine3D
  Height = 2
  Length = 10
  Placement = pos=(11,-3,6) rot=(0,0,1;0rad)
  Width = 6
FEATURE [Part::Box] Box048  label="Krychle048"
  AttacherType = Attacher::AttachEngine3D
  Height = 2
  Length = 10
  Placement = pos=(3,11,6) rot=(0,0,1;1.5708rad)
  Width = 6
FEATURE [Part::Box] Box049  label="Krychle049"
  AttacherType = Attacher::AttachEngine3D
  Height = 2
  Length = 10
  Placement = pos=(-11,3,6) rot=(0,0,1;3.14159rad)
  Width = 6
FEATURE [Part::Box] Box050  label="Krychle050"
  AttacherType = Attacher::AttachEngine3D
  Height = 2
  Length = 10
  Placement = pos=(-3,-11,6) rot=(0,0,-1;1.5708rad)
  Width = 6
FEATURE [Part::Compound] Compound202
  Links = -> [Box040,Box048,Box049,Box050]
  Placement = pos=(0,0,2) rot=(0,0,1;0rad)
FEATURE [Part::Cut] Cut066
  Base = -> Tube010
  Tool = -> Compound202
FEATURE [Part::Compound] Compound204
  Links = -> [Tube009,Cut066]
FEATURE [Part::Cylinder] Cylinder130  label="Válec130"
  Angle = 360
  AttacherType = Attacher::AttachEngine3D
  Height = 16
  Placement = pos=(16,0,2) rot=(0,0,1;3.53429rad)
  Radius = 1.5
FEATURE [Part::Cylinder] Cylinder131  label="Válec131"
  Angle = 360
  AttacherType = Attacher::AttachEngine3D
  Height = 16
  Placement = pos=(2e-15,16,2) rot=(0,0,-1;1.1781rad)
  Radius = 1.5
FEATURE [Part::Cylinder] Cylinder132  label="Válec132"
  Angle = 360
  AttacherType = Attacher::AttachEngine3D
  Height = 16
  Placement = pos=(-16,7e-15,2) rot=(0,0,1;0.392699rad)
  Radius = 1.5
FEATURE [Part::Cylinder] Cylinder133  label="Válec133"
  Angle = 360
  AttacherType = Attacher::AttachEngine3D
  Height = 16
  Placement = pos=(-1.2e-14,-16,2) rot=(0,0,1;1.96349rad)
  Radius = 1.5
FEATURE [Part::Compound] Compound203
  Links = -> [Cylinder130,Cylinder131,Cylinder132,Cylinder133]
FEATURE [Part::Cut] Cut062
  Base = -> Compound204
  Tool = -> Compound203
FEATURE [Part::Cut] Cut063
  Base = -> Cut062
  Tool = -> Compound200
FEATURE [Part::Cut] Cut064
  Base = -> Cut063
  Tool = -> Compound206
FEATURE [Part::Chamfer] Chamfer
  Base = -> Cut064
  Edges = 1 edges r=1: [Edge76]
FEATURE [Part::Compound] Compound207
  Links = -> [Tube011,Chamfer]
FEATURE [Part::Chamfer] Chamfer001  label="podmotoro"
  Base = -> Compound207
  Edges = 1 edges r=1: [Edge93]
  Placement = pos=(0,25,-46) rot=(0,0.707107,0.707107;3.14159rad)
FEATURE [Part::Cylinder] Cylinder146  label="Válec146"
  Angle = 360
  AttacherType = Attacher::AttachEngine3D
  Height = 30
  Placement = pos=(16,0,2) rot=(0,0,1;3.53429rad)
  Radius = 1.5
FEATURE [Part::Cylinder] Cylinder147  label="Válec147"
  Angle = 360
  AttacherType = Attacher::AttachEngine3D
  Height = 30
  Placement = pos=(2e-15,16,2) rot=(0,0,-1;1.1781rad)
  Radius = 1.5
FEATURE [Part::FeaturePython] Tube012  # WARN: FeaturePython — macro-defined, semantics opaque (R4)
  AttacherType = Attacher::AttachEngine3D
  Height = 16
  InnerRadius = 12
  OuterRadius = 20
  Placement = pos=(0,0,16) rot=(0,0,1;0rad)
FEATURE [Part::FeaturePython] Tube015  # WARN: FeaturePython — macro-defined, semantics opaque (R4)
  AttacherType = Attacher::AttachEngine3D
  Height = 9
  InnerRadius = 19.5
  OuterRadius = 24.8
  Placement = pos=(0,0,23) rot=(0,0,1;0rad)
FEATURE [Part::Cylinder] Cylinder148  label="Válec148"
  Angle = 360
  AttacherType = Attacher::AttachEngine3D
  Height = 30
  Placement = pos=(-16,7e-15,2) rot=(0,0,1;0.392699rad)
  Radius = 1.5
FEATURE [Part::Cylinder] Cylinder149  label="Válec149"
  Angle = 360
  AttacherType = Attacher::AttachEngine3D
  Height = 30
  Placement = pos=(-1.2e-14,-16,2) rot=(0,0,1;1.96349rad)
  Radius = 1.5
FEATURE [Part::Compound] Compound208
  Links = -> [Cylinder149,Cylinder148,Cylinder147,Cylinder146]
  Placement = pos=(0,0,-2) rot=(0,0,1;0rad)
FEATURE [Part::Cylinder] Cylinder150  label="Válec150"
  Angle = 360
  AttacherType = Attacher::AttachEngine3D
  Height = 3
  Placement = pos=(-1.2e-14,-16,2) rot=(0,0,1;1.96349rad)
  Radius = 3
FEATURE [Part::Cylinder] Cylinder151  label="Válec151"
  Angle = 360
  AttacherType = Attacher::AttachEngine3D
  Height = 3
  Placement = pos=(16,0,2) rot=(0,0,1;3.53429rad)
  Radius = 3
FEATURE [Part::Cylinder] Cylinder152  label="Válec152"
  Angle = 360
  AttacherType = Attacher::AttachEngine3D
  Height = 3
  Placement = pos=(2e-15,16,2) rot=(0,0,-1;1.1781rad)
  Radius = 3
FEATURE [Part::Cylinder] Cylinder153  label="Válec153"
  Angle = 360
  AttacherType = Attacher::AttachEngine3D
  Height = 3
  Placement = pos=(-16,7e-15,2) rot=(0,0,1;0.392699rad)
  Radius = 3
FEATURE [Part::Compound] Compound209
  Links = -> [Cylinder150,Cylinder153,Cylinder152,Cylinder151]
  Placement = pos=(0,0,27) rot=(0,0,1;0rad)
FEATURE [Part::Cut] Cut067
  Base = -> Tube012
  Tool = -> Compound209
FEATURE [Part::Cut] Cut068
  Base = -> Cut067
  Tool = -> Compound208
FEATURE [Part::Cylinder] Cylinder157  label="Válec157"
  Angle = 360
  AttacherType = Attacher::AttachEngine3D
  Height = 30
  Placement = pos=(-1.2e-14,-16,2) rot=(0,0,1;1.96349rad)
  Radius = 1.5
FEATURE [Part::Cylinder] Cylinder158  label="Válec158"
  Angle = 360
  AttacherType = Attacher::AttachEngine3D
  Height = 30
  Placement = pos=(16,0,2) rot=(0,0,1;3.53429rad)
  Radius = 1.5
FEATURE [Part::Cylinder] Cylinder159  label="Válec159"
  Angle = 360
  AttacherType = Attacher::AttachEngine3D
  Height = 30
  Placement = pos=(2e-15,16,2) rot=(0,0,-1;1.1781rad)
  Radius = 1.5
FEATURE [Part::Cylinder] Cylinder160  label="Válec160"
  Angle = 360
  AttacherType = Attacher::AttachEngine3D
  Height = 30
  Placement = pos=(-16,7e-15,2) rot=(0,0,1;0.392699rad)
  Radius = 1.5
FEATURE [Part::Compound] Compound216
  Links = -> [Cylinder157,Cylinder160,Cylinder159,Cylinder158]
  Placement = pos=(0,0,5) rot=(0,0,1;0.785398rad)
FEATURE [Part::Box] Box068  label="Krychle068"
  AttacherType = Attacher::AttachEngine3D
  Height = 2
  Length = 10
  Placement = pos=(-11,3,6) rot=(0,0,1;3.14159rad)
  Width = 6
FEATURE [Part::Box] Box069  label="Krychle069"
  AttacherType = Attacher::AttachEngine3D
  Height = 2
  Length = 10
  Placement = pos=(3,11,6) rot=(0,0,1;1.5708rad)
  Width = 6
FEATURE [Part::Box] Box070  label="Krychle070"
  AttacherType = Attacher::AttachEngine3D
  Height = 2
  Length = 10
  Placement = pos=(11,-3,6) rot=(0,0,1;0rad)
  Width = 6
FEATURE [Part::Box] Box071  label="Krychle071"
  AttacherType = Attacher::AttachEngine3D
  Height = 2
  Length = 10
  Placement = pos=(-3,-11,6) rot=(0,0,-1;1.5708rad)
  Width = 6
FEATURE [Part::Compound] Compound217
  Links = -> [Box070,Box069,Box068,Box071]
  Placement = pos=(0,0,15) rot=(0,0,1;0.785398rad)
FEATURE [Part::Cut] Cut073
  Base = -> Cut068
  Tool = -> Compound217
FEATURE [Part::Cut] Cut074
  Base = -> Cut073
  Tool = -> Compound216
FEATURE [Part::Compound] Compound219
  Links = -> [Tube015,Cut074]
FEATURE [Part::Chamfer] Chamfer006  label="nadmotor"
  Base = -> Compound219
  Edges = 1 edges r=1: [Edge8]
  Placement = pos=(0,25,-46) rot=(0,0.707107,0.707107;3.14159rad)
FEATURE [Part::Cylinder] Cylinder252  label="Válec252"
  Angle = 360
  AttacherType = Attacher::AttachEngine3D
  Height = 12
  Placement = pos=(0,-32.55,100) rot=(0.57735,-0.57735,-0.57735;4.18879rad)
  Radius = 5
FEATURE [Part::Box] Box113  label="Krychle113"
  AttacherType = Attacher::AttachEngine3D
  Height = 58
  Length = 34
  Placement = pos=(-17,-36,26) rot=(0,0,1;0rad)
  Width = 8
FEATURE [Part::Box] Box114  label="Krychle114"
  AttacherType = Attacher::AttachEngine3D
  Height = 40
  Length = 56.5
  Placement = pos=(-28.25,-28.25,34) rot=(0,0,1;0rad)
  Width = 56.5
FEATURE [Part::Box] Box115  label="Krychle115"
  AttacherType = Attacher::AttachEngine3D
  Height = 8
  Length = 64
  Placement = pos=(-32,-32,26) rot=(0,0,1;0rad)
  Width = 64
FEATURE [Part::Cylinder] Cylinder253  label="Válec253"
  Angle = 360
  AttacherType = Attacher::AttachEngine3D
  Height = 20
  Placement = pos=(0,0,15) rot=(0,0,1;0rad)
  Radius = 12
FEATURE [Part::Cylinder] Cylinder254  label="Válec254"
  Angle = 360
  AttacherType = Attacher::AttachEngine3D
  Height = 3
  Placement = pos=(2e-15,16,2) rot=(0,0,-1;1.1781rad)
  Radius = 3
FEATURE [Part::Cylinder] Cylinder255  label="Válec255"
  Angle = 360
  AttacherType = Attacher::AttachEngine3D
  Height = 3
  Placement = pos=(-1.2e-14,-16,2) rot=(0,0,1;1.96349rad)
  Radius = 3
FEATURE [Part::Cylinder] Cylinder256  label="Válec256"
  Angle = 360
  AttacherType = Attacher::AttachEngine3D
  Height = 3
  Placement = pos=(-16,7e-15,2) rot=(0,0,1;0.392699rad)
  Radius = 3
FEATURE [Part::Cylinder] Cylinder257  label="Válec257"
  Angle = 360
  AttacherType = Attacher::AttachEngine3D
  Height = 3
  Placement = pos=(16,0,2) rot=(0,0,1;3.53429rad)
  Radius = 3
FEATURE [Part::Cylinder] Cylinder258  label="Válec258"
  Angle = 360
  AttacherType = Attacher::AttachEngine3D
  Height = 12
  Placement = pos=(0,-32.55,100) rot=(0,1,0;1.5708rad)
  Radius = 5
FEATURE [Part::Cylinder] Cylinder259  label="Válec259"
  Angle = 360
  AttacherType = Attacher::AttachEngine3D
  Height = 50
  Placement = pos=(0,100,66) rot=(0,1,0;1.5708rad)
  Radius = 2.5
FEATURE [Part::Box] Box116  label="Krychle116"
  AttacherType = Attacher::AttachEngine3D
  Height = 58
  Length = 20
  Placement = pos=(-10,-46.25,26) rot=(0,0,1;0rad)
  Width = 10
FEATURE [Part::Cylinder] Cylinder260  label="Válec260"
  Angle = 360
  AttacherType = Attacher::AttachEngine3D
  Height = 20
  Placement = pos=(23.55,-23.55,20) rot=(0,0,1;0rad)
  Radius = 2.5
FEATURE [Part::Cylinder] Cylinder261  label="Válec261"
  Angle = 360
  AttacherType = Attacher::AttachEngine3D
  Height = 4
  Placement = pos=(-23.55,-23.55,26) rot=(0,0,1;0rad)
  Radius = 5
FEATURE [Part::Cylinder] Cylinder262  label="Válec262"
  Angle = 360
  AttacherType = Attacher::AttachEngine3D
  Height = 4
  Placement = pos=(23.55,-23.55,26) rot=(0,0,1;0rad)
  Radius = 5
FEATURE [Part::Cylinder] Cylinder263  label="Válec263"
  Angle = 360
  AttacherType = Attacher::AttachEngine3D
  Height = 30
  Placement = pos=(-1.2e-14,-16,2) rot=(0,0,1;1.96349rad)
  Radius = 1.5
FEATURE [Part::Cylinder] Cylinder264  label="Válec264"
  Angle = 360
  AttacherType = Attacher::AttachEngine3D
  Height = 30
  Placement = pos=(2e-15,16,2) rot=(0,0,-1;1.1781rad)
  Radius = 1.5
FEATURE [Part::Cylinder] Cylinder265  label="Válec265"
  Angle = 360
  AttacherType = Attacher::AttachEngine3D
  Height = 30
  Placement = pos=(-16,7e-15,2) rot=(0,0,1;0.392699rad)
  Radius = 1.5
FEATURE [Part::Cylinder] Cylinder266  label="Válec266"
  Angle = 360
  AttacherType = Attacher::AttachEngine3D
  Height = 4
  Placement = pos=(23.55,23.55,26) rot=(0,0,1;0rad)
  Radius = 5
FEATURE [Part::Cylinder] Cylinder267  label="Válec267"
  Angle = 360
  AttacherType = Attacher::AttachEngine3D
  Height = 20
  Placement = pos=(23.55,23.55,20) rot=(0,0,1;0rad)
  Radius = 2.5
FEATURE [Part::Compound] Compound263
  Links = -> [Cylinder252,Cylinder258]
FEATURE [Part::Compound] Compound264
  Links = -> [Cylinder255,Cylinder256,Cylinder254,Cylinder257]
  Placement = pos=(0,0,29) rot=(0,0,1;0.785398rad)
FEATURE [Part::Compound] Compound265
  Links = -> [Cylinder259]
  Placement = pos=(0,0,100) rot=(0,0,1;0rad)
FEATURE [Part::Cut] Cut115
  Base = -> Box113
  Tool = -> Compound265
FEATURE [Part::Cut] Cut124
  Base = -> Cut115
  Tool = -> Compound263
FEATURE [Part::Cylinder] Cylinder268  label="Válec268"
  Angle = 360
  AttacherType = Attacher::AttachEngine3D
  Height = 20
  Placement = pos=(-23.55,-23.55,20) rot=(0,0,1;0rad)
  Radius = 2.5
FEATURE [Part::Cylinder] Cylinder269  label="Válec269"
  Angle = 360
  AttacherType = Attacher::AttachEngine3D
  Height = 30
  Placement = pos=(16,0,2) rot=(0,0,1;3.53429rad)
  Radius = 1.5
FEATURE [Part::Compound] Compound268
  Links = -> [Cylinder263,Cylinder265,Cylinder264,Cylinder269]
  Placement = pos=(0,0,14) rot=(0,0,1;0.785398rad)
FEATURE [Part::Cut] Cut121
  Base = -> Box115
  Tool = -> Compound268
FEATURE [Part::Cut] Cut123
  Base = -> Cut121
  Tool = -> Compound264
FEATURE [Part::Cylinder] Cylinder270  label="Válec270"
  Angle = 360
  AttacherType = Attacher::AttachEngine3D
  Height = 4
  Placement = pos=(-23.55,23.55,26) rot=(0,0,1;0rad)
  Radius = 5
FEATURE [Part::Compound] Compound266
  Links = -> [Cylinder261,Cylinder266,Cylinder262,Cylinder270]
FEATURE [Part::Box] Box117  label="Krychle117"
  AttacherType = Attacher::AttachEngine3D
  Height = 16
  Length = 64
  Placement = pos=(-32,-32,34) rot=(0,0,1;0rad)
  Width = 64
FEATURE [Part::Cut] Cut122
  Base = -> Box117
  Tool = -> Box114
FEATURE [Part::Cylinder] Cylinder271  label="Válec271"
  Angle = 360
  AttacherType = Attacher::AttachEngine3D
  Height = 20
  Placement = pos=(-23.55,23.55,20) rot=(0,0,1;0rad)
  Radius = 2.5
FEATURE [Part::Compound] Compound269
  Links = -> [Cylinder267,Cylinder271,Cylinder268,Cylinder260]
FEATURE [Part::Cut] Cut120
  Base = -> Cut123
  Tool = -> Compound269
FEATURE [Part::Cut] Cut114
  Base = -> Cut120
  Tool = -> Compound266
FEATURE [Part::Cut] Cut116
  Base = -> Cut114
  Tool = -> Cylinder253
FEATURE [Part::Compound] Compound261  label="hrubo_holder007"
  Links = -> [Cut116,Cut124,Cut122]
FEATURE [Part::Box] Box118  label="Krychle118"
  AttacherType = Attacher::AttachEngine3D
  Height = 42
  Length = 34
  Placement = pos=(36.25,-17,26) rot=(0,0,1;1.5708rad)
  Width = 8
FEATURE [Part::Box] Box119  label="Krychle119"
  AttacherType = Attacher::AttachEngine3D
  Height = 42
  Length = 34
  Placement = pos=(-36.25,17,26) rot=(0,0,-1;1.5708rad)
  Width = 8
FEATURE [Part::Box] Box120  label="Krychle120"
  AttacherType = Attacher::AttachEngine3D
  Height = 6
  Length = 8
  Placement = pos=(-11,-48,34) rot=(0,0,1;0rad)
  Width = 2
FEATURE [Part::Cylinder] Cylinder272  label="Válec272"
  Angle = 360
  AttacherType = Attacher::AttachEngine3D
  Height = 20
  Placement = pos=(-7,-34,37) rot=(1,0,0;1.5708rad)
  Radius = 1.5
FEATURE [Part::Box] Box121  label="Krychle121"
  AttacherType = Attacher::AttachEngine3D
  Height = 6
  Length = 8
  Placement = pos=(3,-48,34) rot=(0,0,1;0rad)
  Width = 2
FEATURE [Part::Box] Box122  label="Krychle122"
  AttacherType = Attacher::AttachEngine3D
  Height = 6
  Length = 8
  Placement = pos=(3,-48,70) rot=(0,0,1;0rad)
  Width = 2
FEATURE [Part::Box] Box123  label="Krychle123"
  AttacherType = Attacher::AttachEngine3D
  Height = 6
  Length = 8
  Placement = pos=(-11,-48,70) rot=(0,0,1;0rad)
  Width = 2
FEATURE [Part::Compound] Compound262
  Links = -> [Box121,Box120,Box122,Box123]
  Placement = pos=(0,9.75,0) rot=(0,0,1;0rad)
FEATURE [Part::Cylinder] Cylinder273  label="Válec273"
  Angle = 360
  AttacherType = Attacher::AttachEngine3D
  Height = 20
  Placement = pos=(7,-34,37) rot=(1,0,0;1.5708rad)
  Radius = 1.5
FEATURE [Part::Cylinder] Cylinder274  label="Válec274"
  Angle = 360
  AttacherType = Attacher::AttachEngine3D
  Height = 20
  Placement = pos=(7,-34,73) rot=(1,0,0;1.5708rad)
  Radius = 1.5
FEATURE [Part::Cylinder] Cylinder275  label="Válec275"
  Angle = 360
  AttacherType = Attacher::AttachEngine3D
  Height = 20
  Placement = pos=(-7,-34,73) rot=(1,0,0;1.5708rad)
  Radius = 1.5
FEATURE [Part::Compound] Compound273
  Links = -> [Cylinder273,Cylinder272,Cylinder274,Cylinder275]
FEATURE [Part::Box] Box126  label="Krychle126"
  AttacherType = Attacher::AttachEngine3D
  Height = 20
  Length = 28.77
  Placement = pos=(-14.38,-8,34) rot=(0,0,1;0rad)
  Width = 43.38
FEATURE [Part::Compound] Compound275  label="hrubo_holder009"
  Links = -> [Box116,Compound261]
FEATURE [Part::Cut] Cut117
  Base = -> Compound275
  Placement = pos=(-29,18,30) rot=(0,0,1;0rad)
  Tool = -> Box126
FEATURE [Part::Compound] Compound267
  Links = -> [Cut117]
  Placement = pos=(29,-18,-30) rot=(0,0,1;0rad)
FEATURE [Part::Compound] Compound270  label="hrubo_holder_nuovo002"
  Links = -> [Compound267]
FEATURE [Part::Compound] Compound274  label="hrubo_holder008"
  Links = -> [Box118,Box119,Compound270]
FEATURE [Part::Cut] Cut118
  Base = -> Compound274
  Tool = -> Compound273
FEATURE [Part::Cut] Cut119  label="motor_holder"
  Base = -> Cut118
  Tool = -> Compound262
FEATURE [Part::Box] Box130  label="Krychle130"
  AttacherType = Attacher::AttachEngine3D
  Height = 9
  Length = 10
  Placement = pos=(-58,-10,63) rot=(0,0,1;0rad)
  Width = 48
FEATURE [Part::Box] Box131  label="Krychle131"
  AttacherType = Attacher::AttachEngine3D
  Height = 9
  Length = 14.62
  Placement = pos=(-58,38,63) rot=(0,0,1;0rad)
  Width = 10
FEATURE [Part::Cylinder] Cylinder280  label="Válec280"
  Angle = 360
  AttacherType = Attacher::AttachEngine3D
  Height = 50
  Placement = pos=(-23.55,-23.55,20) rot=(0,0,1;0rad)
  Radius = 2.5
FEATURE [Part::Box] Box132  label="Krychle132"
  AttacherType = Attacher::AttachEngine3D
  Height = 9
  Length = 38
  Placement = pos=(-48,-10,63) rot=(0,0,1;0rad)
  Width = 10
FEATURE [Part::Cylinder] Cylinder281  label="Válec281"
  Angle = 360
  AttacherType = Attacher::AttachEngine3D
  Height = 50
  Placement = pos=(23.55,23.55,20) rot=(0,0,1;0rad)
  Radius = 2.5
FEATURE [Part::Box] Box133  label="Krychle133"
  AttacherType = Attacher::AttachEngine3D
  Height = 9
  Length = 14.62
  Placement = pos=(-14.615,38,63) rot=(0,0,1;0rad)
  Width = 10
FEATURE [Part::Cylinder] Cylinder282  label="Válec282"
  Angle = 360
  AttacherType = Attacher::AttachEngine3D
  Height = 50
  Placement = pos=(-23.55,23.55,20) rot=(0,0,1;0rad)
  Radius = 2.5
FEATURE [Part::Box] Box134  label="Krychle134"
  AttacherType = Attacher::AttachEngine3D
  Height = 9
  Length = 10
  Placement = pos=(-10,-10,63) rot=(0,0,1;0rad)
  Width = 48
FEATURE [Part::Compound] Compound277
  Links = -> [Box131,Box134,Box130,Box133,Box132]
  Placement = pos=(29,-19,-4) rot=(0,0,1;0rad)
FEATURE [Part::Cylinder] Cylinder283  label="Válec283"
  Angle = 360
  AttacherType = Attacher::AttachEngine3D
  Height = 50
  Placement = pos=(23.55,-23.55,20) rot=(0,0,1;0rad)
  Radius = 2.5
FEATURE [Part::Compound] Compound276
  Links = -> [Cylinder281,Cylinder283,Cylinder280,Cylinder282]
FEATURE [Part::Cut] Cut125
  Base = -> Compound277
  Placement = pos=(0,0,-25) rot=(0,0,1;0rad)
  Tool = -> Compound276
FEATURE [Part::Chamfer] Chamfer031
  Base = -> Cut125
  Edges = 1 edges r=2: [Edge46]
FEATURE [Part::Chamfer] Chamfer032  label="podlo_AMT"
  Base = -> Chamfer031
  Edges = 1 edges r=2: [Edge24]
FEATURE [Part::Fillet] Fillet
  Base = -> Cut119
  Edges = 2 edges r=8: [Edge25,Edge38]
FEATURE [Part::Chamfer] Chamfer024
  Base = -> Fillet
  Edges = 2 edges r=3: [Edge175,Edge200]
FEATURE [Part::Chamfer] Chamfer025
  Base = -> Chamfer024
  Edges = 2 edges r=3: [Edge1,Edge5]
FEATURE [Part::Chamfer] Chamfer026
  Base = -> Chamfer025
  Edges = 4 edges r=3: [Edge149,Edge154,Edge222,Edge227]
FEATURE [Part::Chamfer] Chamfer027
  Base = -> Chamfer026
  Edges = 4 edges r=3: [Edge4,Edge28,Edge83,Edge111]
FEATURE [Part::Chamfer] Chamfer028
  Base = -> Chamfer027
  Edges = 4 edges r=3: [Edge257,Edge261,Edge269,Edge273]
FEATURE [Part::Chamfer] Chamfer029
  Base = -> Chamfer028
  Edges = 2 edges r=3: [Edge19,Edge23]
FEATURE [Part::Chamfer] Chamfer030  label="motor_holdo_noAMT"
  Base = -> Chamfer029
  Edges = 2 edges r=3: [Edge23,Edge27]
FEATURE [Part::Chamfer] Chamfer033
  Base = -> Chamfer030
  Edges = 2 edges r=2: [Edge130,Edge134]
FEATURE [Part::Chamfer] Chamfer034
  Base = -> Chamfer033
  Edges = 1 edges r=2: [Edge37]
FEATURE [Part::Chamfer] Chamfer035  label="moto_holder_noAMT"
  Base = -> Chamfer034
  Edges = 2 edges r=2: [Edge33,Edge41]
FEATURE [Part::Compound] Compound278  label="moto_holder_AMT"
  Links = -> [Chamfer035,Chamfer032]
  Placement = pos=(0,31,-46) rot=(-1,0,0;1.5708rad)
FEATURE [Part::Cylinder] Cylinder284  label="Válec284"
  Angle = 360
  AttacherType = Attacher::AttachEngine3D
  Height = 10
  Placement = pos=(0,106,0) rot=(0,0,1;0rad)
  Radius = 10
FEATURE [Sketcher::SketchObject] Sketch
  FullyConstrained = false
  MapMode = 5
  Support = -> [XY_Plane]
  sketch-geometry (5):
    g0: LineSegment StartX=-51.8839 StartY=28.0157 StartZ=0 EndX=-8.82571 EndY=110.528 EndZ=0
    g1: LineSegment StartX=-8.82571 StartY=110.528 StartZ=0 EndX=8.88346 EndY=110.528 EndZ=0
    g2: LineSegment StartX=8.88346 StartY=110.528 StartZ=0 EndX=51.7746 EndY=28.1985 EndZ=0
    g3: LineSegment StartX=51.7746 StartY=28.1985 StartZ=0 EndX=0 EndY=55.1408 EndZ=0
    g4: LineSegment StartX=0 StartY=55.1408 StartZ=0 EndX=-51.8839 EndY=28.0157 EndZ=0
  constraints (7):
    c: Coincident(g0,g1)
    c: Horizontal(g1)
    c: Coincident(g1,g2)
    c: Coincident(g2,g3)
    c: PointOnObject(g3,g-2)
    c: Coincident(g3,g4)
    c: Coincident(g4,g0)
FEATURE [PartDesign::Pad] Pad
  Direction = (1,1,1)
  Length = 10
  Length2 = 100
  Profile = -> Sketch
  Type = 0
FEATURE [PartDesign::Body] Body
  Group = -> [Sketch,Pad]
  Origin = -> Origin
  Tip = -> Pad
FEATURE [Part::FeaturePython] Tube016  # WARN: FeaturePython — macro-defined, semantics opaque (R4)
  AttacherType = Attacher::AttachEngine3D
  Height = 19
  InnerRadius = 38
  OuterRadius = 50
  Placement = pos=(0,0,52) rot=(0,0,1;0rad)
FEATURE [Part::FeaturePython] Tube017  # WARN: FeaturePython — macro-defined, semantics opaque (R4)
  AttacherType = Attacher::AttachEngine3D
  Height = 1
  InnerRadius = 35
  OuterRadius = 50
  Placement = pos=(0,0,47) rot=(0,0,1;0rad)
FEATURE [Part::Cylinder] Cylinder285  label="Válec285"
  Angle = 360
  AttacherType = Attacher::AttachEngine3D
  Height = 24
  Placement = pos=(0,-24,-46) rot=(1,0,0;1.5708rad)
  Radius = 54
FEATURE [Part::Cylinder] Cylinder286  label="Válec286"
  Angle = 360
  AttacherType = Attacher::AttachEngine3D
  Height = 4
  Placement = pos=(0,-50,-46) rot=(1,0,0;1.5708rad)
  Radius = 54
FEATURE [Part::Box] Box135  label="Krychle135"
  AttacherType = Attacher::AttachEngine3D
  Height = 32
  Length = 200
  Placement = pos=(-100,-124,0) rot=(0,0,1;0rad)
  Width = 100
FEATURE [Part::FeaturePython] Tube018  # WARN: FeaturePython — macro-defined, semantics opaque (R4)
  AttacherType = Attacher::AttachEngine3D
  Height = 6
  InnerRadius = 40
  OuterRadius = 59
  Placement = pos=(0,0,12) rot=(0,0,1;0rad)
FEATURE [Part::Box] Box136  label="Krychle136"
  AttacherType = Attacher::AttachEngine3D
  Height = 10
  Length = 10
  Placement = pos=(32,-24,0) rot=(0,0,1;0rad)
  Width = 52
FEATURE [Part::Box] Box137  label="Krychle137"
  AttacherType = Attacher::AttachEngine3D
  Height = 10
  Length = 10
  Placement = pos=(-42,-24,0) rot=(0,0,1;0rad)
  Width = 52
FEATURE [Part::Box] Box138  label="Krychle138"
  AttacherType = Attacher::AttachEngine3D
  Height = 10
  Length = 72
  Placement = pos=(-36,10,0) rot=(0,0,1;0rad)
  Width = 34
FEATURE [Part::FeaturePython] Tube019  # WARN: FeaturePython — macro-defined, semantics opaque (R4)
  AttacherType = Attacher::AttachEngine3D
  Height = 13
  InnerRadius = 38
  OuterRadius = 64
  Placement = pos=(0,0,18) rot=(0,0,1;0rad)
FEATURE [Part::Torus] Torus  label="Anuloid"
  Angle1 = -180
  Angle2 = 180
  Angle3 = 360
  AttacherType = Attacher::AttachEngine3D
  Placement = pos=(0,0,24.5) rot=(0,0,1;0rad)
  Radius1 = 64
  Radius2 = 3.5
FEATURE [Part::Torus] Torus002  label="Anuloid002"
  Angle1 = -180
  Angle2 = 180
  Angle3 = 360
  AttacherType = Attacher::AttachEngine3D
  Placement = pos=(0,0,30.5) rot=(0,0,1;0rad)
  Radius1 = 64
  Radius2 = 3.5
FEATURE [Part::Cylinder] Cylinder287  label="Válec287"
  Angle = 360
  AttacherType = Attacher::AttachEngine3D
  Height = 2
  Placement = pos=(0,0,10) rot=(0,0,1;0rad)
  Radius = 59
FEATURE [Part::Cylinder] Cylinder288  label="Válec288"
  Angle = 360
  AttacherType = Attacher::AttachEngine3D
  Height = 20
  Placement = pos=(0,-64,4.5) rot=(0,0,1;0rad)
  Radius = 3.5
FEATURE [Part::FeaturePython] Tube020  # WARN: FeaturePython — macro-defined, semantics opaque (R4)
  AttacherType = Attacher::AttachEngine3D
  Height = 1
  InnerRadius = 38
  OuterRadius = 58
  Placement = pos=(0,0,31) rot=(0,0,1;0rad)
FEATURE [Part::FeaturePython] wormgear022  # WARN: FeaturePython — macro-defined, semantics opaque (R4)
  AttacherType = Attacher::AttachEngine3D
  Placement = pos=(0,0,100) rot=(0,0,1;0rad)
  beta = 33.6901
  clearance = 0.25
  diameter = 120
  head = 0
  height = 5
  module = 1
  pressure_angle = 20
  reverse_pitch = true
  teeth = 80
  version = 0.0.3
FEATURE [Part::FeaturePython] wormgear023  # WARN: FeaturePython — macro-defined, semantics opaque (R4)
  AttacherType = Attacher::AttachEngine3D
  Placement = pos=(0,0,95) rot=(0,0,1;0.032289rad)
  beta = 33.6901
  clearance = 0.25
  diameter = 120
  head = 0
  height = 5
  module = 1
  pressure_angle = 20
  reverse_pitch = false
  teeth = 80
  version = 0.0.3
FEATURE [Part::Cylinder] Cylinder289  label="Válec289"
  Angle = 360
  AttacherType = Attacher::AttachEngine3D
  Height = 20
  Placement = pos=(0,0,91) rot=(0,0,1;0rad)
  Radius = 38
FEATURE [Part::Cylinder] Cylinder290  label="Válec290"
  Angle = 360
  AttacherType = Attacher::AttachEngine3D
  Height = 20
  Placement = pos=(0,0,91) rot=(0,0,1;0rad)
  Radius = 38
FEATURE [Part::Cut] Cut127
  Base = -> wormgear023
  Placement = pos=(0,0,-63) rot=(0,0,1;0rad)
  Tool = -> Cylinder290
FEATURE [Part::Cut] Cut128
  Base = -> wormgear022
  Placement = pos=(0,0,-63) rot=(0,0,1;0rad)
  Tool = -> Cylinder289
FEATURE [Part::FeaturePython] Tube022  # WARN: FeaturePython — macro-defined, semantics opaque (R4)
  AttacherType = Attacher::AttachEngine3D
  Height = 4
  InnerRadius = 30
  OuterRadius = 58
  Placement = pos=(0,0,42) rot=(0,0,1;0rad)
FEATURE [Part::Cut] Cut129
  Base = -> Tube019
  Tool = -> Torus
FEATURE [Part::Cut] Cut130
  Base = -> Cut129
  Tool = -> Cylinder288
FEATURE [Part::Cylinder] Cylinder291  label="Válec291"
  Angle = 360
  AttacherType = Attacher::AttachEngine3D
  Height = 100
  Placement = pos=(-51,-16,0) rot=(0,0,1;0rad)
  Radius = 1.5
FEATURE [Part::Cylinder] Cylinder292  label="Válec292"
  Angle = 360
  AttacherType = Attacher::AttachEngine3D
  Height = 100
  Placement = pos=(51,-16,0) rot=(0,0,1;0rad)
  Radius = 1.5
FEATURE [Part::Cylinder] Cylinder295  label="Válec295"
  Angle = 360
  AttacherType = Attacher::AttachEngine3D
  Height = 4
  Placement = pos=(34,36,-1) rot=(0,0,1;0rad)
  Radius = 3
FEATURE [Part::Cylinder] Cylinder296  label="Válec296"
  Angle = 360
  AttacherType = Attacher::AttachEngine3D
  Height = 4
  Placement = pos=(-34,36,-1) rot=(0,0,1;0rad)
  Radius = 3
FEATURE [Part::Compound] Compound281
  Links = -> [Cylinder295,Cylinder296]
FEATURE [Part::Cylinder] Cylinder299  label="Válec299"
  Angle = 360
  AttacherType = Attacher::AttachEngine3D
  Height = 4
  Placement = pos=(34,36,-1) rot=(0,0,1;0rad)
  Radius = 3
FEATURE [Part::Cylinder] Cylinder300  label="Válec300"
  Angle = 360
  AttacherType = Attacher::AttachEngine3D
  Height = 4
  Placement = pos=(-34,36,-1) rot=(0,0,1;0rad)
  Radius = 3
FEATURE [Part::Compound] Compound283
  Links = -> [Cylinder299,Cylinder300]
FEATURE [Part::Cylinder] Cylinder301  label="Válec301"
  Angle = 360
  AttacherType = Attacher::AttachEngine3D
  Height = 50
  Placement = pos=(34,36,0) rot=(0,0,1;0rad)
  Radius = 1.5
FEATURE [Part::Cylinder] Cylinder302  label="Válec302"
  Angle = 360
  AttacherType = Attacher::AttachEngine3D
  Height = 50
  Placement = pos=(-34,36,0) rot=(0,0,1;0rad)
  Radius = 1.5
FEATURE [Part::Compound] Compound285
  Links = -> [Cylinder302,Cylinder301]
FEATURE [Part::Cylinder] Cylinder303  label="Válec303"
  Angle = 360
  AttacherType = Attacher::AttachEngine3D
  Height = 50
  Placement = pos=(34,36,0) rot=(0,0,1;0rad)
  Radius = 1.5
FEATURE [Part::Cylinder] Cylinder304  label="Válec304"
  Angle = 360
  AttacherType = Attacher::AttachEngine3D
  Height = 50
  Placement = pos=(-34,36,0) rot=(0,0,1;0rad)
  Radius = 1.5
FEATURE [Part::Compound] Compound286
  Links = -> [Cylinder304,Cylinder303]
FEATURE [Part::Cut] Cut133
  Base = -> Tube018
  Tool = -> Compound285
FEATURE [Part::Cylinder] Cylinder305  label="Válec305"
  Angle = 360
  AttacherType = Attacher::AttachEngine3D
  Height = 4
  Placement = pos=(34,36,-1) rot=(0,0,1;0rad)
  Radius = 3
FEATURE [Part::Cylinder] Cylinder306  label="Válec306"
  Angle = 360
  AttacherType = Attacher::AttachEngine3D
  Height = 4
  Placement = pos=(-34,36,-1) rot=(0,0,1;0rad)
  Radius = 3
FEATURE [Part::Compound] Compound287
  Links = -> [Cylinder305,Cylinder306]
FEATURE [Part::Cylinder] Cylinder307  label="Válec307"
  Angle = 360
  AttacherType = Attacher::AttachEngine3D
  Height = 4
  Placement = pos=(-34,36,-1) rot=(0,0,1;0rad)
  Radius = 3
FEATURE [Part::Cylinder] Cylinder308  label="Válec308"
  Angle = 360
  AttacherType = Attacher::AttachEngine3D
  Height = 4
  Placement = pos=(34,36,-1) rot=(0,0,1;0rad)
  Radius = 3
FEATURE [Part::Compound] Compound288
  Links = -> [Cylinder308,Cylinder307]
FEATURE [Part::Cut] Cut134
  Base = -> Body
  Tool = -> Compound288
FEATURE [Part::Cylinder] Cylinder309  label="Válec309"
  Angle = 360
  AttacherType = Attacher::AttachEngine3D
  Height = 50
  Placement = pos=(34,36,0) rot=(0,0,1;0rad)
  Radius = 1.5
FEATURE [Part::Cylinder] Cylinder310  label="Válec310"
  Angle = 360
  AttacherType = Attacher::AttachEngine3D
  Height = 50
  Placement = pos=(-34,36,0) rot=(0,0,1;0rad)
  Radius = 1.5
FEATURE [Part::Compound] Compound289
  Links = -> [Cylinder310,Cylinder309]
FEATURE [Part::Cut] Cut135
  Base = -> Cut134
  Tool = -> Compound289
FEATURE [Part::Cylinder] Cylinder311  label="Válec311"
  Angle = 360
  AttacherType = Attacher::AttachEngine3D
  Height = 4
  Placement = pos=(-34,36,-1) rot=(0,0,1;0rad)
  Radius = 3
FEATURE [Part::Cylinder] Cylinder312  label="Válec312"
  Angle = 360
  AttacherType = Attacher::AttachEngine3D
  Height = 4
  Placement = pos=(34,36,-1) rot=(0,0,1;0rad)
  Radius = 3
FEATURE [Part::Compound] Compound290
  Links = -> [Cylinder312,Cylinder311]
FEATURE [Part::Cut] Cut136
  Base = -> Tube
  Tool = -> Compound290
FEATURE [Part::Cylinder] Cylinder313  label="Válec313"
  Angle = 360
  AttacherType = Attacher::AttachEngine3D
  Height = 50
  Placement = pos=(34,36,0) rot=(0,0,1;0rad)
  Radius = 1.5
FEATURE [Part::Cylinder] Cylinder314  label="Válec314"
  Angle = 360
  AttacherType = Attacher::AttachEngine3D
  Height = 50
  Placement = pos=(-34,36,0) rot=(0,0,1;0rad)
  Radius = 1.5
FEATURE [Part::Compound] Compound291
  Links = -> [Cylinder314,Cylinder313]
FEATURE [Part::Cut] Cut137
  Base = -> Cut136
  Tool = -> Compound291
FEATURE [Part::Compound] Compound292
  Links = -> [Cylinder291,Cylinder292]
FEATURE [Part::Cylinder] Cylinder315  label="Válec315"
  Angle = 360
  AttacherType = Attacher::AttachEngine3D
  Height = 4
  Placement = pos=(-51,-16,0) rot=(0,0,1;0rad)
  Radius = 3
FEATURE [Part::Cylinder] Cylinder316  label="Válec316"
  Angle = 360
  AttacherType = Attacher::AttachEngine3D
  Height = 4
  Placement = pos=(51,-16,0) rot=(0,0,1;0rad)
  Radius = 3
FEATURE [Part::Cylinder] Cylinder317  label="Válec317"
  Angle = 360
  AttacherType = Attacher::AttachEngine3D
  Height = 100
  Placement = pos=(-51,-16,0) rot=(0,0,1;0rad)
  Radius = 1.5
FEATURE [Part::Cylinder] Cylinder318  label="Válec318"
  Angle = 360
  AttacherType = Attacher::AttachEngine3D
  Height = 100
  Placement = pos=(51,-16,0) rot=(0,0,1;0rad)
  Radius = 1.5
FEATURE [Part::Compound] Compound294
  Links = -> [Cylinder317,Cylinder318]
FEATURE [Part::Cylinder] Cylinder319  label="Válec319"
  Angle = 360
  AttacherType = Attacher::AttachEngine3D
  Height = 50
  Placement = pos=(51,6,0) rot=(0,0,1;0rad)
  Radius = 1.5
FEATURE [Part::Cylinder] Cylinder320  label="Válec320"
  Angle = 360
  AttacherType = Attacher::AttachEngine3D
  Height = 50
  Placement = pos=(-51,6,0) rot=(0,0,1;0rad)
  Radius = 1.5
FEATURE [Part::Cylinder] Cylinder321  label="Válec321"
  Angle = 360
  AttacherType = Attacher::AttachEngine3D
  Height = 50
  Placement = pos=(-24,18,0) rot=(0,0,1;0rad)
  Radius = 1.5
FEATURE [Part::Cylinder] Cylinder322  label="Válec322"
  Angle = 360
  AttacherType = Attacher::AttachEngine3D
  Height = 50
  Placement = pos=(24,18,0) rot=(0,0,1;0rad)
  Radius = 1.5
FEATURE [Part::Compound] Compound295
  Links = -> [Cylinder319,Cylinder320,Cylinder321,Cylinder322]
FEATURE [Part::Cylinder] Cylinder323  label="Válec323"
  Angle = 360
  AttacherType = Attacher::AttachEngine3D
  Height = 4
  Placement = pos=(-51,6,0) rot=(0,0,1;0rad)
  Radius = 3
FEATURE [Part::Cylinder] Cylinder324  label="Válec324"
  Angle = 360
  AttacherType = Attacher::AttachEngine3D
  Height = 4
  Placement = pos=(51,6,0) rot=(0,0,1;0rad)
  Radius = 3
FEATURE [Part::Cylinder] Cylinder325  label="Válec325"
  Angle = 360
  AttacherType = Attacher::AttachEngine3D
  Height = 4
  Placement = pos=(-24,18,0) rot=(0,0,1;0rad)
  Radius = 3
FEATURE [Part::Cylinder] Cylinder326  label="Válec326"
  Angle = 360
  AttacherType = Attacher::AttachEngine3D
  Height = 4
  Placement = pos=(24,18,0) rot=(0,0,1;0rad)
  Radius = 3
FEATURE [Part::Compound] Compound296
  Links = -> [Cylinder324,Cylinder323,Cylinder325,Cylinder326]
  Placement = pos=(0,0,8) rot=(0,0,1;0rad)
FEATURE [Part::Cylinder] Cylinder327  label="Válec327"
  Angle = 360
  AttacherType = Attacher::AttachEngine3D
  Height = 4
  Placement = pos=(-19,19,0) rot=(0,0,1;0rad)
  Radius = 3
FEATURE [Part::Cylinder] Cylinder328  label="Válec328"
  Angle = 360
  AttacherType = Attacher::AttachEngine3D
  Height = 50
  Placement = pos=(-51,7,0) rot=(0,0,1;0rad)
  Radius = 1.5
FEATURE [Part::Cylinder] Cylinder329  label="Válec329"
  Angle = 360
  AttacherType = Attacher::AttachEngine3D
  Height = 50
  Placement = pos=(51,7,0) rot=(0,0,1;0rad)
  Radius = 1.5
FEATURE [Part::Cylinder] Cylinder330  label="Válec330"
  Angle = 360
  AttacherType = Attacher::AttachEngine3D
  Height = 50
  Placement = pos=(-19,19,0) rot=(0,0,1;0rad)
  Radius = 1.5
FEATURE [Part::Cylinder] Cylinder331  label="Válec331"
  Angle = 360
  AttacherType = Attacher::AttachEngine3D
  Height = 50
  Placement = pos=(19,19,0) rot=(0,0,1;0rad)
  Radius = 1.5
FEATURE [Part::Cylinder] Cylinder334  label="Válec334"
  Angle = 360
  AttacherType = Attacher::AttachEngine3D
  Height = 4
  Placement = pos=(19,19,0) rot=(0,0,1;0rad)
  Radius = 3
FEATURE [Part::Compound] Compound297
  Links = -> [Cylinder329,Cylinder328,Cylinder330,Cylinder331]
FEATURE [Part::Compound] Compound298
  Links = -> [Cylinder327,Cylinder334]
  Placement = pos=(0,0,7) rot=(0,0,1;0rad)
FEATURE [Part::Cylinder] Cylinder333  label="Válec333"
  Angle = 360
  AttacherType = Attacher::AttachEngine3D
  Height = 4
  Placement = pos=(51,7,17) rot=(0,0,1;0rad)
  Radius = 3
FEATURE [Part::Cylinder] Cylinder332  label="Válec332"
  Angle = 360
  AttacherType = Attacher::AttachEngine3D
  Height = 4
  Placement = pos=(-51,7,17) rot=(0,0,1;0rad)
  Radius = 3
FEATURE [Part::Cylinder] Cylinder335  label="Válec335"
  Angle = 360
  AttacherType = Attacher::AttachEngine3D
  Height = 4
  Placement = pos=(-51,-16,0) rot=(0,0,1;0rad)
  Radius = 3
FEATURE [Part::Cylinder] Cylinder336  label="Válec336"
  Angle = 360
  AttacherType = Attacher::AttachEngine3D
  Height = 4
  Placement = pos=(51,-16,0) rot=(0,0,1;0rad)
  Radius = 3
FEATURE [Part::Compound] Compound299
  Links = -> [Cylinder335,Cylinder336]
  Placement = pos=(0,0,33) rot=(0,0,1;0rad)
FEATURE [Part::Compound] Compound300
  Links = -> [Cylinder333,Cylinder332]
  Placement = pos=(0,0,-2) rot=(0,0,1;0rad)
FEATURE [Part::Cylinder] Cylinder337  label="Válec337"
  Angle = 360
  AttacherType = Attacher::AttachEngine3D
  Height = 100
  Placement = pos=(-51,-16,0) rot=(0,0,1;0rad)
  Radius = 1.5
FEATURE [Part::Cylinder] Cylinder338  label="Válec338"
  Angle = 360
  AttacherType = Attacher::AttachEngine3D
  Height = 100
  Placement = pos=(51,-16,0) rot=(0,0,1;0rad)
  Radius = 1.5
FEATURE [Part::Cylinder] Cylinder339  label="Válec339"
  Angle = 360
  AttacherType = Attacher::AttachEngine3D
  Height = 50
  Placement = pos=(-51,7,0) rot=(0,0,1;0rad)
  Radius = 1.5
FEATURE [Part::Cylinder] Cylinder340  label="Válec340"
  Angle = 360
  AttacherType = Attacher::AttachEngine3D
  Height = 50
  Placement = pos=(51,7,0) rot=(0,0,1;0rad)
  Radius = 1.5
FEATURE [Part::Cylinder] Cylinder343  label="Válec343"
  Angle = 360
  AttacherType = Attacher::AttachEngine3D
  Height = 50
  Placement = pos=(34,36,0) rot=(0,0,1;0rad)
  Radius = 1.5
FEATURE [Part::Cylinder] Cylinder344  label="Válec344"
  Angle = 360
  AttacherType = Attacher::AttachEngine3D
  Height = 50
  Placement = pos=(-34,36,0) rot=(0,0,1;0rad)
  Radius = 1.5
FEATURE [Part::Compound] Compound301
  Links = -> [Cylinder337,Cylinder344,Cylinder343,Cylinder340,Cylinder339,Cylinder338]
FEATURE [Part::Cut] Cut145
  Base = -> Cut133
  Tool = -> Compound301
FEATURE [Part::Cylinder] Cylinder345  label="Válec345"
  Angle = 360
  AttacherType = Attacher::AttachEngine3D
  Height = 100
  Placement = pos=(-51,-16,0) rot=(0,0,1;0rad)
  Radius = 1.5
FEATURE [Part::Cylinder] Cylinder346  label="Válec346"
  Angle = 360
  AttacherType = Attacher::AttachEngine3D
  Height = 100
  Placement = pos=(51,-16,0) rot=(0,0,1;0rad)
  Radius = 1.5
FEATURE [Part::Cylinder] Cylinder347  label="Válec347"
  Angle = 360
  AttacherType = Attacher::AttachEngine3D
  Height = 50
  Placement = pos=(51,7,0) rot=(0,0,1;0rad)
  Radius = 1.5
FEATURE [Part::Cylinder] Cylinder348  label="Válec348"
  Angle = 360
  AttacherType = Attacher::AttachEngine3D
  Height = 50
  Placement = pos=(-51,7,0) rot=(0,0,1;0rad)
  Radius = 1.5
FEATURE [Part::Cylinder] Cylinder349  label="Válec349"
  Angle = 360
  AttacherType = Attacher::AttachEngine3D
  Height = 50
  Placement = pos=(34,36,0) rot=(0,0,1;0rad)
  Radius = 1.5
FEATURE [Part::Cylinder] Cylinder350  label="Válec350"
  Angle = 360
  AttacherType = Attacher::AttachEngine3D
  Height = 50
  Placement = pos=(-34,36,0) rot=(0,0,1;0rad)
  Radius = 1.5
FEATURE [Part::Compound] Compound302
  Links = -> [Cylinder345,Cylinder350,Cylinder349,Cylinder347,Cylinder348,Cylinder346]
FEATURE [Part::Cylinder] Cylinder351  label="Válec351"
  Angle = 360
  AttacherType = Attacher::AttachEngine3D
  Height = 4
  Placement = pos=(-51,-16,0) rot=(0,0,1;0rad)
  Radius = 3
FEATURE [Part::Cylinder] Cylinder352  label="Válec352"
  Angle = 360
  AttacherType = Attacher::AttachEngine3D
  Height = 4
  Placement = pos=(51,-16,0) rot=(0,0,1;0rad)
  Radius = 3
FEATURE [Part::Compound] Compound303
  Links = -> [Cylinder351,Cylinder352]
  Placement = pos=(0,0,15) rot=(0,0,1;0rad)
FEATURE [Part::Cut] Cut146
  Base = -> Cut145
  Tool = -> Compound303
FEATURE [Part::Cut] Cut147
  Base = -> Cut146
  Tool = -> Compound300
FEATURE [Part::Compound] Compound293
  Links = -> [Cylinder315,Cylinder316]
  Placement = pos=(0,0,25) rot=(0,0,1;0rad)
FEATURE [Part::Cut] Cut138
  Base = -> Cut137
  Tool = -> Compound293
FEATURE [Part::Cut] Cut139
  Base = -> Cut138
  Tool = -> Compound292
FEATURE [Part::Cut] Cut142
  Base = -> Cut139
  Tool = -> Compound298
FEATURE [Part::Cut] Cut143
  Base = -> Cut142
  Tool = -> Compound297
FEATURE [Part::Cut] Cut144
  Base = -> Cut143
  Tool = -> Box135
FEATURE [Part::Cut] Cut148
  Base = -> Cylinder287
  Tool = -> Compound302
FEATURE [Part::Cylinder] Cylinder353  label="Válec353"
  Angle = 360
  AttacherType = Attacher::AttachEngine3D
  Height = 4
  Placement = pos=(-19,19,0) rot=(0,0,1;0rad)
  Radius = 3
FEATURE [Part::Cylinder] Cylinder356  label="Válec356"
  Angle = 360
  AttacherType = Attacher::AttachEngine3D
  Height = 4
  Placement = pos=(19,19,0) rot=(0,0,1;0rad)
  Radius = 3
FEATURE [Part::Compound] Compound304
  Links = -> [Cylinder353,Cylinder356]
  Placement = pos=(0,0,10) rot=(0,0,1;0rad)
FEATURE [Part::Cut] Cut149
  Base = -> Cut148
  Tool = -> Compound304
FEATURE [Part::Cylinder] Cylinder357  label="Válec357"
  Angle = 360
  AttacherType = Attacher::AttachEngine3D
  Height = 50
  Placement = pos=(34,-36,0) rot=(0,0,1;0rad)
  Radius = 1.5
FEATURE [Part::Cylinder] Cylinder358  label="Válec358"
  Angle = 360
  AttacherType = Attacher::AttachEngine3D
  Height = 50
  Placement = pos=(-34,-36,0) rot=(0,0,1;0rad)
  Radius = 1.5
FEATURE [Part::Cylinder] Cylinder359  label="Válec359"
  Angle = 360
  AttacherType = Attacher::AttachEngine3D
  Height = 4
  Placement = pos=(34,-36,0) rot=(0,0,1;0rad)
  Radius = 3
FEATURE [Part::Cylinder] Cylinder360  label="Válec360"
  Angle = 360
  AttacherType = Attacher::AttachEngine3D
  Height = 4
  Placement = pos=(-34,-36,0) rot=(0,0,1;0rad)
  Radius = 3
FEATURE [Part::Compound] Compound305
  Links = -> [Cylinder359,Cylinder360]
  Placement = pos=(0,0,9) rot=(0,0,1;0rad)
FEATURE [Part::Compound] Compound306
  Links = -> [Cylinder357,Cylinder358]
FEATURE [Part::Cylinder] Cylinder361  label="Válec361"
  Angle = 360
  AttacherType = Attacher::AttachEngine3D
  Height = 4
  Placement = pos=(-34,-36,0) rot=(0,0,1;0rad)
  Radius = 3
FEATURE [Part::Cylinder] Cylinder362  label="Válec362"
  Angle = 360
  AttacherType = Attacher::AttachEngine3D
  Height = 4
  Placement = pos=(34,-36,0) rot=(0,0,1;0rad)
  Radius = 3
FEATURE [Part::Compound] Compound307
  Links = -> [Cylinder362,Cylinder361]
  Placement = pos=(0,0,9) rot=(0,0,1;0rad)
FEATURE [Part::Cut] Cut150
  Base = -> Cut149
  Tool = -> Compound305
FEATURE [Part::Cut] Cut151
  Base = -> Cut147
  Tool = -> Compound307
FEATURE [Part::Cut] Cut152
  Base = -> Cut151
  Tool = -> Compound306
FEATURE [Part::Cylinder] Cylinder363  label="Válec363"
  Angle = 360
  AttacherType = Attacher::AttachEngine3D
  Height = 4
  Placement = pos=(0,50,-1) rot=(0,0,1;0rad)
  Radius = 3
FEATURE [Part::Cylinder] Cylinder364  label="Válec364"
  Angle = 360
  AttacherType = Attacher::AttachEngine3D
  Height = 50
  Placement = pos=(0,50,0) rot=(0,0,1;0rad)
  Radius = 1.5
FEATURE [Part::Cut] Cut153
  Base = -> Cut144
  Tool = -> Cylinder363
FEATURE [Part::Cylinder] Cylinder365  label="Válec365"
  Angle = 360
  AttacherType = Attacher::AttachEngine3D
  Height = 50
  Placement = pos=(0,50,0) rot=(0,0,1;0rad)
  Radius = 1.5
FEATURE [Part::Cut] Cut154
  Base = -> Cut153
  Tool = -> Cylinder364
FEATURE [Part::Cylinder] Cylinder366  label="Válec366"
  Angle = 360
  AttacherType = Attacher::AttachEngine3D
  Height = 50
  Placement = pos=(0,50,0) rot=(0,0,1;0rad)
  Radius = 1.5
FEATURE [Part::Cut] Cut155
  Base = -> Cut150
  Tool = -> Cylinder365
FEATURE [Part::Cut] Cut156
  Base = -> Cut152
  Tool = -> Cylinder366
FEATURE [Part::Cylinder] Cylinder298  label="Válec298"
  Angle = 360
  AttacherType = Attacher::AttachEngine3D
  Height = 4
  Placement = pos=(-34,36,-1) rot=(0,0,1;0rad)
  Radius = 3
FEATURE [Part::Cylinder] Cylinder297  label="Válec297"
  Angle = 360
  AttacherType = Attacher::AttachEngine3D
  Height = 4
  Placement = pos=(34,36,-1) rot=(0,0,1;0rad)
  Radius = 3
FEATURE [Part::Compound] Compound282
  Links = -> [Cylinder298,Cylinder297]
FEATURE [Part::Cut] Cut131
  Base = -> Box138
  Tool = -> Compound282
FEATURE [Part::Cylinder] Cylinder294  label="Válec294"
  Angle = 360
  AttacherType = Attacher::AttachEngine3D
  Height = 50
  Placement = pos=(-34,36,0) rot=(0,0,1;0rad)
  Radius = 1.5
FEATURE [Part::Cylinder] Cylinder293  label="Válec293"
  Angle = 360
  AttacherType = Attacher::AttachEngine3D
  Height = 50
  Placement = pos=(34,36,0) rot=(0,0,1;0rad)
  Radius = 1.5
FEATURE [Part::Compound] Compound284
  Links = -> [Cylinder294,Cylinder293]
FEATURE [Part::Cut] Cut132
  Base = -> Cut131
  Tool = -> Compound284
FEATURE [Part::Cut] Cut140
  Base = -> Cut132
  Tool = -> Compound296
FEATURE [Part::Cut] Cut141
  Base = -> Cut140
  Tool = -> Compound295
FEATURE [Part::Cylinder] Cylinder367  label="Válec367"
  Angle = 360
  AttacherType = Attacher::AttachEngine3D
  Height = 4
  Placement = pos=(0,-50,9) rot=(0,0,1;0rad)
  Radius = 3
FEATURE [Part::Cylinder] Cylinder368  label="Válec368"
  Angle = 360
  AttacherType = Attacher::AttachEngine3D
  Height = 50
  Placement = pos=(0,-50,0) rot=(0,0,1;0rad)
  Radius = 1.5
FEATURE [Part::Cylinder] Cylinder369  label="Válec369"
  Angle = 360
  AttacherType = Attacher::AttachEngine3D
  Height = 4
  Placement = pos=(0,-50,9) rot=(0,0,1;0rad)
  Radius = 3
FEATURE [Part::Cut] Cut157
  Base = -> Cut155
  Tool = -> Cylinder367
FEATURE [Part::Cut] Cut158
  Base = -> Cut156
  Tool = -> Cylinder369
FEATURE [Part::Cut] Cut159
  Base = -> Cut158
  Tool = -> Cylinder368
FEATURE [Part::Cylinder] Cylinder370  label="Válec370"
  Angle = 360
  AttacherType = Attacher::AttachEngine3D
  Height = 50
  Placement = pos=(-34,36,0) rot=(0,0,1;0rad)
  Radius = 1.5
FEATURE [Part::Cylinder] Cylinder371  label="Válec371"
  Angle = 360
  AttacherType = Attacher::AttachEngine3D
  Height = 50
  Placement = pos=(34,36,0) rot=(0,0,1;0rad)
  Radius = 1.5
FEATURE [Part::Cylinder] Cylinder372  label="Válec372"
  Angle = 360
  AttacherType = Attacher::AttachEngine3D
  Height = 50
  Placement = pos=(-34,-36,0) rot=(0,0,1;0rad)
  Radius = 1.5
FEATURE [Part::Cylinder] Cylinder373  label="Válec373"
  Angle = 360
  AttacherType = Attacher::AttachEngine3D
  Height = 50
  Placement = pos=(34,-36,0) rot=(0,0,1;0rad)
  Radius = 1.5
FEATURE [Part::Cylinder] Cylinder374  label="Válec374"
  Angle = 360
  AttacherType = Attacher::AttachEngine3D
  Height = 50
  Placement = pos=(0,50,0) rot=(0,0,1;0rad)
  Radius = 1.5
FEATURE [Part::Cylinder] Cylinder375  label="Válec375"
  Angle = 360
  AttacherType = Attacher::AttachEngine3D
  Height = 50
  Placement = pos=(0,-50,0) rot=(0,0,1;0rad)
  Radius = 1.5
FEATURE [Part::Cylinder] Cylinder376  label="Válec376"
  Angle = 360
  AttacherType = Attacher::AttachEngine3D
  Height = 100
  Placement = pos=(-51,-12,0) rot=(0,0,1;0rad)
  Radius = 1.5
FEATURE [Part::Cylinder] Cylinder377  label="Válec377"
  Angle = 360
  AttacherType = Attacher::AttachEngine3D
  Height = 50
  Placement = pos=(51,6,0) rot=(0,0,1;0rad)
  Radius = 1.5
FEATURE [Part::Cylinder] Cylinder378  label="Válec378"
  Angle = 360
  AttacherType = Attacher::AttachEngine3D
  Height = 50
  Placement = pos=(-51,6,0) rot=(0,0,1;0rad)
  Radius = 1.5
FEATURE [Part::Cylinder] Cylinder379  label="Válec379"
  Angle = 360
  AttacherType = Attacher::AttachEngine3D
  Height = 100
  Placement = pos=(51,-12,0) rot=(0,0,1;0rad)
  Radius = 1.5
FEATURE [Part::Compound] Compound308
  Links = -> [Cylinder370,Cylinder371,Cylinder372,Cylinder373,Cylinder374,Cylinder375,Cylinder376,Cylinder377,Cylinder378,Cylinder379]
FEATURE [Part::Cylinder] Cylinder380  label="Válec380"
  Angle = 360
  AttacherType = Attacher::AttachEngine3D
  Height = 50
  Placement = pos=(0,-50,0) rot=(0,0,1;0rad)
  Radius = 1.5
FEATURE [Part::Cylinder] Cylinder381  label="Válec381"
  Angle = 360
  AttacherType = Attacher::AttachEngine3D
  Height = 50
  Placement = pos=(-34,-36,0) rot=(0,0,1;0rad)
  Radius = 1.5
FEATURE [Part::Cylinder] Cylinder382  label="Válec382"
  Angle = 360
  AttacherType = Attacher::AttachEngine3D
  Height = 50
  Placement = pos=(-34,36,0) rot=(0,0,1;0rad)
  Radius = 1.5
FEATURE [Part::Cylinder] Cylinder383  label="Válec383"
  Angle = 360
  AttacherType = Attacher::AttachEngine3D
  Height = 50
  Placement = pos=(34,36,0) rot=(0,0,1;0rad)
  Radius = 1.5
FEATURE [Part::Cylinder] Cylinder384  label="Válec384"
  Angle = 360
  AttacherType = Attacher::AttachEngine3D
  Height = 50
  Placement = pos=(51,7,0) rot=(0,0,1;0rad)
  Radius = 1.5
FEATURE [Part::Cylinder] Cylinder385  label="Válec385"
  Angle = 360
  AttacherType = Attacher::AttachEngine3D
  Height = 100
  Placement = pos=(51,-16,0) rot=(0,0,1;0rad)
  Radius = 1.5
FEATURE [Part::Cylinder] Cylinder386  label="Válec386"
  Angle = 360
  AttacherType = Attacher::AttachEngine3D
  Height = 100
  Placement = pos=(-51,-16,0) rot=(0,0,1;0rad)
  Radius = 1.5
FEATURE [Part::Cylinder] Cylinder387  label="Válec387"
  Angle = 360
  AttacherType = Attacher::AttachEngine3D
  Height = 50
  Placement = pos=(0,50,0) rot=(0,0,1;0rad)
  Radius = 1.5
FEATURE [Part::Cylinder] Cylinder388  label="Válec388"
  Angle = 360
  AttacherType = Attacher::AttachEngine3D
  Height = 50
  Placement = pos=(-51,7,0) rot=(0,0,1;0rad)
  Radius = 1.5
FEATURE [Part::Cylinder] Cylinder389  label="Válec389"
  Angle = 360
  AttacherType = Attacher::AttachEngine3D
  Height = 50
  Placement = pos=(34,-36,0) rot=(0,0,1;0rad)
  Radius = 1.5
FEATURE [Part::Compound] Compound309
  Links = -> [Cylinder382,Cylinder383,Cylinder381,Cylinder389,Cylinder387,Cylinder380,Cylinder386,Cylinder384,Cylinder388,Cylinder385]
FEATURE [Part::Cut] Cut160
  Base = -> Cut130
  Tool = -> Compound308
FEATURE [Part::Cylinder] Cylinder394  label="Válec394"
  Angle = 360
  AttacherType = Attacher::AttachEngine3D
  Height = 100
  Placement = pos=(-51,-16,0) rot=(0,0,1;0rad)
  Radius = 1.5
FEATURE [Part::Cylinder] Cylinder395  label="Válec395"
  Angle = 360
  AttacherType = Attacher::AttachEngine3D
  Height = 50
  Placement = pos=(0,-50,0) rot=(0,0,1;0rad)
  Radius = 1.5
FEATURE [Part::Cylinder] Cylinder396  label="Válec396"
  Angle = 360
  AttacherType = Attacher::AttachEngine3D
  Height = 50
  Placement = pos=(-34,-36,0) rot=(0,0,1;0rad)
  Radius = 1.5
FEATURE [Part::Cylinder] Cylinder397  label="Válec397"
  Angle = 360
  AttacherType = Attacher::AttachEngine3D
  Height = 50
  Placement = pos=(-34,36,0) rot=(0,0,1;0rad)
  Radius = 1.5
FEATURE [Part::Cylinder] Cylinder398  label="Válec398"
  Angle = 360
  AttacherType = Attacher::AttachEngine3D
  Height = 50
  Placement = pos=(34,36,0) rot=(0,0,1;0rad)
  Radius = 1.5
FEATURE [Part::Cylinder] Cylinder399  label="Válec399"
  Angle = 360
  AttacherType = Attacher::AttachEngine3D
  Height = 50
  Placement = pos=(51,7,0) rot=(0,0,1;0rad)
  Radius = 1.5
FEATURE [Part::Cylinder] Cylinder400  label="Válec400"
  Angle = 360
  AttacherType = Attacher::AttachEngine3D
  Height = 100
  Placement = pos=(51,-16,0) rot=(0,0,1;0rad)
  Radius = 1.5
FEATURE [Part::Cylinder] Cylinder401  label="Válec401"
  Angle = 360
  AttacherType = Attacher::AttachEngine3D
  Height = 50
  Placement = pos=(-51,7,0) rot=(0,0,1;0rad)
  Radius = 1.5
FEATURE [Part::Cylinder] Cylinder402  label="Válec402"
  Angle = 360
  AttacherType = Attacher::AttachEngine3D
  Height = 50
  Placement = pos=(0,50,0) rot=(0,0,1;0rad)
  Radius = 1.5
FEATURE [Part::Cylinder] Cylinder403  label="Válec403"
  Angle = 360
  AttacherType = Attacher::AttachEngine3D
  Height = 50
  Placement = pos=(34,-36,0) rot=(0,0,1;0rad)
  Radius = 1.5
FEATURE [Part::Compound] Compound311
  Links = -> [Cylinder397,Cylinder398,Cylinder396,Cylinder403,Cylinder402,Cylinder395,Cylinder394,Cylinder399,Cylinder401,Cylinder400]
FEATURE [Part::Cylinder] Cylinder404  label="Válec404"
  Angle = 360
  AttacherType = Attacher::AttachEngine3D
  Height = 7
  Placement = pos=(-51,6,50) rot=(0,0,1;0rad)
  Radius = 3
FEATURE [Part::Cylinder] Cylinder405  label="Válec405"
  Angle = 360
  AttacherType = Attacher::AttachEngine3D
  Height = 7
  Placement = pos=(51,6,50) rot=(0,0,1;0rad)
  Radius = 3
FEATURE [Part::Cylinder] Cylinder406  label="Válec406"
  Angle = 360
  AttacherType = Attacher::AttachEngine3D
  Height = 7
  Placement = pos=(-51,-12,50) rot=(0,0,1;0rad)
  Radius = 3
FEATURE [Part::Cylinder] Cylinder407  label="Válec407"
  Angle = 360
  AttacherType = Attacher::AttachEngine3D
  Height = 7
  Placement = pos=(51,-12,50) rot=(0,0,1;0rad)
  Radius = 3
FEATURE [Part::Compound] Compound312
  Links = -> [Cylinder406,Cylinder407,Cylinder405,Cylinder404]
  Placement = pos=(0,0,-25) rot=(0,0,1;0rad)
FEATURE [Part::Cylinder] Cylinder408  label="Válec408"
  Angle = 360
  AttacherType = Attacher::AttachEngine3D
  Height = 7
  Placement = pos=(-51,-12,50) rot=(0,0,1;0rad)
  Radius = 3
FEATURE [Part::Cylinder] Cylinder409  label="Válec409"
  Angle = 360
  AttacherType = Attacher::AttachEngine3D
  Height = 7
  Placement = pos=(51,6,50) rot=(0,0,1;0rad)
  Radius = 3
FEATURE [Part::Cylinder] Cylinder410  label="Válec410"
  Angle = 360
  AttacherType = Attacher::AttachEngine3D
  Height = 7
  Placement = pos=(-51,6,50) rot=(0,0,1;0rad)
  Radius = 3
FEATURE [Part::Cylinder] Cylinder411  label="Válec411"
  Angle = 360
  AttacherType = Attacher::AttachEngine3D
  Height = 7
  Placement = pos=(51,-12,50) rot=(0,0,1;0rad)
  Radius = 3
FEATURE [Part::Compound] Compound313
  Links = -> [Cylinder408,Cylinder411,Cylinder409,Cylinder410]
  Placement = pos=(0,0,-25) rot=(0,0,1;0rad)
FEATURE [Part::Cut] Cut161
  Base = -> Tube020
  Tool = -> Compound312
FEATURE [Part::Cut] Cut162
  Base = -> Cut160
  Tool = -> Compound313
FEATURE [Part::Box] Box145  label="Krychle145"
  AttacherType = Attacher::AttachEngine3D
  Height = 10
  Length = 6
  Placement = pos=(-3,47,40) rot=(0,0,1;0rad)
  Width = 6
FEATURE [Part::Box] Box146  label="Krychle146"
  AttacherType = Attacher::AttachEngine3D
  Height = 10
  Length = 6
  Placement = pos=(-3,-53,40) rot=(0,0,1;0rad)
  Width = 6
FEATURE [Part::Box] Box147  label="Krychle147"
  AttacherType = Attacher::AttachEngine3D
  Height = 10
  Length = 6
  Placement = pos=(-37,-39,40) rot=(0,0,1;0rad)
  Width = 6
FEATURE [Part::Box] Box148  label="Krychle148"
  AttacherType = Attacher::AttachEngine3D
  Height = 10
  Length = 6
  Placement = pos=(31,33,40) rot=(0,0,1;0rad)
  Width = 6
FEATURE [Part::Box] Box149  label="Krychle149"
  AttacherType = Attacher::AttachEngine3D
  Height = 10
  Length = 6
  Placement = pos=(-37,33,40) rot=(0,0,1;0rad)
  Width = 6
FEATURE [Part::Box] Box150  label="Krychle150"
  AttacherType = Attacher::AttachEngine3D
  Height = 10
  Length = 6
  Placement = pos=(31,-39,40) rot=(0,0,1;0rad)
  Width = 6
FEATURE [Part::Compound] Compound315
  Links = -> [Box145,Box147,Box146,Box148,Box149,Box150]
  Placement = pos=(0,0,-18) rot=(0,0,1;0rad)
FEATURE [Part::Box] Box151  label="Krychle151"
  AttacherType = Attacher::AttachEngine3D
  Height = 10
  Length = 6
  Placement = pos=(-3,-53,40) rot=(0,0,1;0rad)
  Width = 6
FEATURE [Part::Box] Box152  label="Krychle152"
  AttacherType = Attacher::AttachEngine3D
  Height = 10
  Length = 6
  Placement = pos=(-3,47,40) rot=(0,0,1;0rad)
  Width = 6
FEATURE [Part::Box] Box153  label="Krychle153"
  AttacherType = Attacher::AttachEngine3D
  Height = 10
  Length = 6
  Placement = pos=(-37,33,40) rot=(0,0,1;0rad)
  Width = 6
FEATURE [Part::Box] Box154  label="Krychle154"
  AttacherType = Attacher::AttachEngine3D
  Height = 10
  Length = 6
  Placement = pos=(-37,-39,40) rot=(0,0,1;0rad)
  Width = 6
FEATURE [Part::Box] Box155  label="Krychle155"
  AttacherType = Attacher::AttachEngine3D
  Height = 10
  Length = 6
  Placement = pos=(31,33,40) rot=(0,0,1;0rad)
  Width = 6
FEATURE [Part::Box] Box156  label="Krychle156"
  AttacherType = Attacher::AttachEngine3D
  Height = 10
  Length = 6
  Placement = pos=(31,-39,40) rot=(0,0,1;0rad)
  Width = 6
FEATURE [Part::Compound] Compound316
  Links = -> [Box152,Box154,Box151,Box155,Box153,Box156]
  Placement = pos=(0,0,-18) rot=(0,0,1;0rad)
FEATURE [Part::Cut] Cut163
  Base = -> Cut161
  Tool = -> Compound316
FEATURE [Part::Cut] Cut164
  Base = -> Cut162
  Tool = -> Compound315
FEATURE [Part::Cylinder] Cylinder412  label="Válec412"
  Angle = 360
  AttacherType = Attacher::AttachEngine3D
  Height = 20
  Placement = pos=(-7,-34,73) rot=(1,0,0;1.5708rad)
  Radius = 1.5
FEATURE [Part::Cylinder] Cylinder413  label="Válec413"
  Angle = 360
  AttacherType = Attacher::AttachEngine3D
  Height = 20
  Placement = pos=(7,-34,37) rot=(1,0,0;1.5708rad)
  Radius = 1.5
FEATURE [Part::Cylinder] Cylinder414  label="Válec414"
  Angle = 360
  AttacherType = Attacher::AttachEngine3D
  Height = 20
  Placement = pos=(7,-34,73) rot=(1,0,0;1.5708rad)
  Radius = 1.5
FEATURE [Part::Cylinder] Cylinder415  label="Válec415"
  Angle = 360
  AttacherType = Attacher::AttachEngine3D
  Height = 20
  Placement = pos=(-7,-34,37) rot=(1,0,0;1.5708rad)
  Radius = 1.5
FEATURE [Part::Compound] Compound317
  Links = -> [Cylinder413,Cylinder415,Cylinder414,Cylinder412]
  Placement = pos=(0,141,45) rot=(1,0,0;1.5708rad)
FEATURE [Part::Cylinder] Cylinder416  label="Válec416"
  Angle = 360
  AttacherType = Attacher::AttachEngine3D
  Height = 20
  Placement = pos=(-7,-34,73) rot=(1,0,0;1.5708rad)
  Radius = 1.5
FEATURE [Part::Cylinder] Cylinder417  label="Válec417"
  Angle = 360
  AttacherType = Attacher::AttachEngine3D
  Height = 20
  Placement = pos=(7,-34,37) rot=(1,0,0;1.5708rad)
  Radius = 1.5
FEATURE [Part::Cylinder] Cylinder418  label="Válec418"
  Angle = 360
  AttacherType = Attacher::AttachEngine3D
  Height = 20
  Placement = pos=(7,-34,73) rot=(1,0,0;1.5708rad)
  Radius = 1.5
FEATURE [Part::Cylinder] Cylinder419  label="Válec419"
  Angle = 360
  AttacherType = Attacher::AttachEngine3D
  Height = 20
  Placement = pos=(-7,-34,37) rot=(1,0,0;1.5708rad)
  Radius = 1.5
FEATURE [Part::Compound] Compound318
  Links = -> [Cylinder417,Cylinder419,Cylinder418,Cylinder416]
  Placement = pos=(0,141,45) rot=(1,0,0;1.5708rad)
FEATURE [Part::Cut] Cut165
  Base = -> Cut135
  Tool = -> Compound318
FEATURE [Part::Cut] Cut166
  Base = -> Cylinder284
  Tool = -> Compound317
FEATURE [Part::Cylinder] Cylinder420  label="Válec420"
  Angle = 360
  AttacherType = Attacher::AttachEngine3D
  Height = 4
  Placement = pos=(-7,-34,73) rot=(1,0,0;1.5708rad)
  Radius = 3
FEATURE [Part::Cylinder] Cylinder421  label="Válec421"
  Angle = 360
  AttacherType = Attacher::AttachEngine3D
  Height = 4
  Placement = pos=(7,-34,37) rot=(1,0,0;1.5708rad)
  Radius = 3
FEATURE [Part::Cylinder] Cylinder422  label="Válec422"
  Angle = 360
  AttacherType = Attacher::AttachEngine3D
  Height = 4
  Placement = pos=(7,-34,73) rot=(1,0,0;1.5708rad)
  Radius = 3
FEATURE [Part::Cylinder] Cylinder423  label="Válec423"
  Angle = 360
  AttacherType = Attacher::AttachEngine3D
  Height = 4
  Placement = pos=(-7,-34,37) rot=(1,0,0;1.5708rad)
  Radius = 3
FEATURE [Part::Compound] Compound319
  Links = -> [Cylinder421,Cylinder423,Cylinder422,Cylinder420]
  Placement = pos=(0,141,45) rot=(1,0,0;1.5708rad)
FEATURE [Part::Cylinder] Cylinder424  label="Válec424"
  Angle = 360
  AttacherType = Attacher::AttachEngine3D
  Height = 4
  Placement = pos=(-7,-34,73) rot=(1,0,0;1.5708rad)
  Radius = 3
FEATURE [Part::Cylinder] Cylinder425  label="Válec425"
  Angle = 360
  AttacherType = Attacher::AttachEngine3D
  Height = 4
  Placement = pos=(7,-34,37) rot=(1,0,0;1.5708rad)
  Radius = 3
FEATURE [Part::Cylinder] Cylinder426  label="Válec426"
  Angle = 360
  AttacherType = Attacher::AttachEngine3D
  Height = 4
  Placement = pos=(7,-34,73) rot=(1,0,0;1.5708rad)
  Radius = 3
FEATURE [Part::Cylinder] Cylinder427  label="Válec427"
  Angle = 360
  AttacherType = Attacher::AttachEngine3D
  Height = 4
  Placement = pos=(-7,-34,37) rot=(1,0,0;1.5708rad)
  Radius = 3
FEATURE [Part::Compound] Compound320
  Links = -> [Cylinder425,Cylinder427,Cylinder426,Cylinder424]
  Placement = pos=(0,141,45) rot=(1,0,0;1.5708rad)
FEATURE [Part::Cut] Cut167
  Base = -> Cut165
  Tool = -> Compound319
FEATURE [Part::Cut] Cut168
  Base = -> Cut166
  Tool = -> Compound320
FEATURE [Part::FeaturePython] Tube023  # WARN: FeaturePython — macro-defined, semantics opaque (R4)
  AttacherType = Attacher::AttachEngine3D
  Height = 4
  InnerRadius = 30
  OuterRadius = 37
  Placement = pos=(0,0,46) rot=(0,0,1;0rad)
FEATURE [Part::Cylinder] Cylinder428  label="Válec428"
  Angle = 360
  AttacherType = Attacher::AttachEngine3D
  Height = 100
  Placement = pos=(16.0727,-38.8029,0) rot=(0,0,1;0.785398rad)
  Radius = 1.5
FEATURE [Part::Box] Box157  label="Krychle157"
  AttacherType = Attacher::AttachEngine3D
  Height = 2
  Length = 6
  Placement = pos=(14.4491,-42.7226,25) rot=(0,0,1;0.392699rad)
  Width = 8
FEATURE [Part::Cylinder] Cylinder429  label="Válec429"
  Angle = 360
  AttacherType = Attacher::AttachEngine3D
  Height = 4
  Placement = pos=(16.07,-38.8,43) rot=(0,0,1;0.785398rad)
  Radius = 3
FEATURE [Part::Cylinder] Cylinder430  label="Válec430"
  Angle = 360
  AttacherType = Attacher::AttachEngine3D
  Height = 100
  Placement = pos=(38.8029,-16.0727,0) rot=(0,0,1;1.5708rad)
  Radius = 1.5
FEATURE [Part::Box] Box158  label="Krychle158"
  AttacherType = Attacher::AttachEngine3D
  Height = 2
  Length = 6
  Placement = pos=(40.4265,-19.9924,25) rot=(0,0,1;1.1781rad)
  Width = 8
FEATURE [Part::Cylinder] Cylinder431  label="Válec431"
  Angle = 360
  AttacherType = Attacher::AttachEngine3D
  Height = 4
  Placement = pos=(38.7989,-16.0725,43) rot=(0,0,1;1.5708rad)
  Radius = 3
FEATURE [Part::Cylinder] Cylinder432  label="Válec432"
  Angle = 360
  AttacherType = Attacher::AttachEngine3D
  Height = 100
  Placement = pos=(38.8029,16.0727,0) rot=(0,0,1;2.35619rad)
  Radius = 1.5
FEATURE [Part::Box] Box159  label="Krychle159"
  AttacherType = Attacher::AttachEngine3D
  Height = 2
  Length = 6
  Placement = pos=(42.7226,14.4491,25) rot=(0,0,1;1.96349rad)
  Width = 8
FEATURE [Part::Cylinder] Cylinder433  label="Válec433"
  Angle = 360
  AttacherType = Attacher::AttachEngine3D
  Height = 4
  Placement = pos=(38.8,16.07,43) rot=(0,0,1;2.35619rad)
  Radius = 3
FEATURE [Part::Cylinder] Cylinder434  label="Válec434"
  Angle = 360
  AttacherType = Attacher::AttachEngine3D
  Height = 100
  Placement = pos=(16.0727,38.8029,0) rot=(0,0,1;3.14159rad)
  Radius = 1.5
FEATURE [Part::Box] Box160  label="Krychle160"
  AttacherType = Attacher::AttachEngine3D
  Height = 2
  Length = 6
  Placement = pos=(19.9924,40.4265,25) rot=(0,0,1;2.74889rad)
  Width = 8
FEATURE [Part::Cylinder] Cylinder435  label="Válec435"
  Angle = 360
  AttacherType = Attacher::AttachEngine3D
  Height = 4
  Placement = pos=(16.0725,38.7989,43) rot=(0,0,1;3.14159rad)
  Radius = 3
FEATURE [Part::Cylinder] Cylinder436  label="Válec436"
  Angle = 360
  AttacherType = Attacher::AttachEngine3D
  Height = 100
  Placement = pos=(-16.0727,38.8029,0) rot=(0,0,1;3.92699rad)
  Radius = 1.5
FEATURE [Part::Cylinder] Cylinder437  label="Válec437"
  Angle = 360
  AttacherType = Attacher::AttachEngine3D
  Height = 4
  Placement = pos=(-16.07,38.8,43) rot=(0,0,1;3.92699rad)
  Radius = 3
FEATURE [Part::Box] Box161  label="Krychle161"
  AttacherType = Attacher::AttachEngine3D
  Height = 2
  Length = 6
  Placement = pos=(-14.4491,42.7226,25) rot=(0,0,1;3.53429rad)
  Width = 8
FEATURE [Part::Cylinder] Cylinder438  label="Válec438"
  Angle = 360
  AttacherType = Attacher::AttachEngine3D
  Height = 100
  Placement = pos=(-38.8029,16.0727,0) rot=(0,0,-1;1.5708rad)
  Radius = 1.5
FEATURE [Part::Cylinder] Cylinder439  label="Válec439"
  Angle = 360
  AttacherType = Attacher::AttachEngine3D
  Height = 4
  Placement = pos=(-38.7989,16.0725,43) rot=(0,0,-1;1.5708rad)
  Radius = 3
FEATURE [Part::Box] Box162  label="Krychle162"
  AttacherType = Attacher::AttachEngine3D
  Height = 2
  Length = 6
  Placement = pos=(-40.4265,19.9924,25) rot=(0,0,-1;1.96349rad)
  Width = 8
FEATURE [Part::Cylinder] Cylinder440  label="Válec440"
  Angle = 360
  AttacherType = Attacher::AttachEngine3D
  Height = 100
  Placement = pos=(-38.8029,-16.0727,0) rot=(0,0,-1;0.785398rad)
  Radius = 1.5
FEATURE [Part::Cylinder] Cylinder441  label="Válec441"
  Angle = 360
  AttacherType = Attacher::AttachEngine3D
  Height = 4
  Placement = pos=(-38.8,-16.07,43) rot=(0,0,-1;0.785398rad)
  Radius = 3
FEATURE [Part::Box] Box163  label="Krychle163"
  AttacherType = Attacher::AttachEngine3D
  Height = 2
  Length = 6
  Placement = pos=(-42.7226,-14.4491,25) rot=(0,0,-1;1.1781rad)
  Width = 8
FEATURE [Part::Cylinder] Cylinder442  label="Válec442"
  Angle = 360
  AttacherType = Attacher::AttachEngine3D
  Height = 100
  Placement = pos=(-16.0727,-38.8029,0) rot=(0,0,1;0rad)
  Radius = 1.5
FEATURE [Part::Cylinder] Cylinder443  label="Válec443"
  Angle = 360
  AttacherType = Attacher::AttachEngine3D
  Height = 4
  Placement = pos=(-16.0725,-38.7989,43) rot=(0,0,1;0rad)
  Radius = 3
FEATURE [Part::Box] Box164  label="Krychle164"
  AttacherType = Attacher::AttachEngine3D
  Height = 2
  Length = 6
  Placement = pos=(-19.9924,-40.4265,25) rot=(0,0,-1;0.392699rad)
  Width = 8
FEATURE [Part::Compound] Compound321
  Links = -> [Cylinder428,Cylinder430,Cylinder432,Cylinder434,Cylinder436,Cylinder438,Cylinder440,Cylinder442]
FEATURE [Part::Compound] Compound322
  Links = -> [Box157,Box158,Box159,Box160,Box161,Box162,Box163,Box164]
FEATURE [Part::Compound] Compound323
  Links = -> [Cylinder441,Cylinder439,Cylinder437,Cylinder435,Cylinder433,Cylinder431,Cylinder429,Cylinder443]
FEATURE [Part::Cut] Cut169
  Base = -> Tube022
  Tool = -> Compound323
FEATURE [Part::Compound] Compound324
  Links = -> [Tube023,Cut169]
FEATURE [Part::Cylinder] Cylinder444  label="Válec444"
  Angle = 360
  AttacherType = Attacher::AttachEngine3D
  Height = 100
  Placement = pos=(16.0727,-38.8029,0) rot=(0,0,1;0.785398rad)
  Radius = 1.5
FEATURE [Part::Cylinder] Cylinder445  label="Válec445"
  Angle = 360
  AttacherType = Attacher::AttachEngine3D
  Height = 100
  Placement = pos=(41.0011,-9.08831,0) rot=(0,0,1;0.174533rad)
  Radius = 1.5
FEATURE [Part::Cylinder] Cylinder446  label="Válec446"
  Angle = 360
  AttacherType = Attacher::AttachEngine3D
  Height = 100
  Placement = pos=(38.8029,16.0727,0) rot=(0,0,1;2.35619rad)
  Radius = 1.5
FEATURE [Part::Cylinder] Cylinder447  label="Válec447"
  Angle = 360
  AttacherType = Attacher::AttachEngine3D
  Height = 100
  Placement = pos=(16.0727,38.8029,0) rot=(0,0,1;3.14159rad)
  Radius = 1.5
FEATURE [Part::Cylinder] Cylinder448  label="Válec448"
  Angle = 360
  AttacherType = Attacher::AttachEngine3D
  Height = 100
  Placement = pos=(-16.0727,38.8029,0) rot=(0,0,1;3.92699rad)
  Radius = 1.5
FEATURE [Part::Cylinder] Cylinder449  label="Válec449"
  Angle = 360
  AttacherType = Attacher::AttachEngine3D
  Height = 100
  Placement = pos=(-38.8029,16.0727,0) rot=(0,0,-1;1.5708rad)
  Radius = 1.5
FEATURE [Part::Cylinder] Cylinder450  label="Válec450"
  Angle = 360
  AttacherType = Attacher::AttachEngine3D
  Height = 100
  Placement = pos=(-38.8029,-16.0727,0) rot=(0,0,-1;0.785398rad)
  Radius = 1.5
FEATURE [Part::Cylinder] Cylinder451  label="Válec451"
  Angle = 360
  AttacherType = Attacher::AttachEngine3D
  Height = 100
  Placement = pos=(-16.0727,-38.8029,0) rot=(0,0,1;0rad)
  Radius = 1.5
FEATURE [Part::Compound] Compound325
  Links = -> [Cylinder444,Cylinder445,Cylinder446,Cylinder447,Cylinder448,Cylinder449,Cylinder450,Cylinder451]
FEATURE [Part::Cut] Cut170
  Base = -> Compound324
  Tool = -> Compound321
FEATURE [Part::Cylinder] Cylinder452  label="Válec452"
  Angle = 360
  AttacherType = Attacher::AttachEngine3D
  Height = 100
  Placement = pos=(16.0727,-38.8029,0) rot=(0,0,1;0.785398rad)
  Radius = 1.5
FEATURE [Part::Cylinder] Cylinder453  label="Válec453"
  Angle = 360
  AttacherType = Attacher::AttachEngine3D
  Height = 100
  Placement = pos=(38.8029,-16.0727,0) rot=(0,0,1;1.5708rad)
  Radius = 1.5
FEATURE [Part::Cylinder] Cylinder454  label="Válec454"
  Angle = 360
  AttacherType = Attacher::AttachEngine3D
  Height = 100
  Placement = pos=(38.8029,16.0727,0) rot=(0,0,1;2.35619rad)
  Radius = 1.5
FEATURE [Part::Cylinder] Cylinder455  label="Válec455"
  Angle = 360
  AttacherType = Attacher::AttachEngine3D
  Height = 100
  Placement = pos=(16.0727,38.8029,0) rot=(0,0,1;3.14159rad)
  Radius = 1.5
FEATURE [Part::Cylinder] Cylinder456  label="Válec456"
  Angle = 360
  AttacherType = Attacher::AttachEngine3D
  Height = 100
  Placement = pos=(-16.0727,38.8029,0) rot=(0,0,1;3.92699rad)
  Radius = 1.5
FEATURE [Part::Cylinder] Cylinder457  label="Válec457"
  Angle = 360
  AttacherType = Attacher::AttachEngine3D
  Height = 100
  Placement = pos=(-38.8029,16.0727,0) rot=(0,0,-1;1.5708rad)
  Radius = 1.5
FEATURE [Part::Cylinder] Cylinder458  label="Válec458"
  Angle = 360
  AttacherType = Attacher::AttachEngine3D
  Height = 100
  Placement = pos=(-38.8029,-16.0727,0) rot=(0,0,-1;0.785398rad)
  Radius = 1.5
FEATURE [Part::Cylinder] Cylinder459  label="Válec459"
  Angle = 360
  AttacherType = Attacher::AttachEngine3D
  Height = 100
  Placement = pos=(-16.0727,-38.8029,0) rot=(0,0,1;0rad)
  Radius = 1.5
FEATURE [Part::Compound] Compound326
  Links = -> [Cylinder452,Cylinder453,Cylinder454,Cylinder455,Cylinder456,Cylinder457,Cylinder458,Cylinder459]
FEATURE [Part::Cut] Cut171
  Base = -> Cut128
  Tool = -> Compound326
FEATURE [Part::Cylinder] Cylinder460  label="Válec460"
  Angle = 360
  AttacherType = Attacher::AttachEngine3D
  Height = 100
  Placement = pos=(16.0727,-38.8029,0) rot=(0,0,1;0.785398rad)
  Radius = 1.5
FEATURE [Part::Cylinder] Cylinder461  label="Válec461"
  Angle = 360
  AttacherType = Attacher::AttachEngine3D
  Height = 100
  Placement = pos=(38.8029,-16.0727,0) rot=(0,0,1;1.5708rad)
  Radius = 1.5
FEATURE [Part::Cylinder] Cylinder462  label="Válec462"
  Angle = 360
  AttacherType = Attacher::AttachEngine3D
  Height = 100
  Placement = pos=(38.8029,16.0727,0) rot=(0,0,1;2.35619rad)
  Radius = 1.5
FEATURE [Part::Cylinder] Cylinder463  label="Válec463"
  Angle = 360
  AttacherType = Attacher::AttachEngine3D
  Height = 100
  Placement = pos=(16.0727,38.8029,0) rot=(0,0,1;3.14159rad)
  Radius = 1.5
FEATURE [Part::Cylinder] Cylinder464  label="Válec464"
  Angle = 360
  AttacherType = Attacher::AttachEngine3D
  Height = 100
  Placement = pos=(-16.0727,38.8029,0) rot=(0,0,1;3.92699rad)
  Radius = 1.5
FEATURE [Part::Cylinder] Cylinder465  label="Válec465"
  Angle = 360
  AttacherType = Attacher::AttachEngine3D
  Height = 100
  Placement = pos=(-38.8029,16.0727,0) rot=(0,0,-1;1.5708rad)
  Radius = 1.5
FEATURE [Part::Cylinder] Cylinder466  label="Válec466"
  Angle = 360
  AttacherType = Attacher::AttachEngine3D
  Height = 100
  Placement = pos=(-38.8029,-16.0727,0) rot=(0,0,-1;0.785398rad)
  Radius = 1.5
FEATURE [Part::Cylinder] Cylinder467  label="Válec467"
  Angle = 360
  AttacherType = Attacher::AttachEngine3D
  Height = 100
  Placement = pos=(-16.0727,-38.8029,0) rot=(0,0,1;0rad)
  Radius = 1.5
FEATURE [Part::Compound] Compound327
  Links = -> [Cylinder460,Cylinder461,Cylinder462,Cylinder463,Cylinder464,Cylinder465,Cylinder466,Cylinder467]
FEATURE [Part::Cut] Cut172
  Base = -> Cut127
  Tool = -> Compound327
FEATURE [Part::Cylinder] Cylinder468  label="Válec468"
  Angle = 360
  AttacherType = Attacher::AttachEngine3D
  Height = 100
  Placement = pos=(16.0727,-38.8029,0) rot=(0,0,1;0.785398rad)
  Radius = 1.5
FEATURE [Part::Cylinder] Cylinder469  label="Válec469"
  Angle = 360
  AttacherType = Attacher::AttachEngine3D
  Height = 100
  Placement = pos=(38.8029,-16.0727,0) rot=(0,0,1;1.5708rad)
  Radius = 1.5
FEATURE [Part::Cylinder] Cylinder470  label="Válec470"
  Angle = 360
  AttacherType = Attacher::AttachEngine3D
  Height = 100
  Placement = pos=(38.8029,16.0727,0) rot=(0,0,1;2.35619rad)
  Radius = 1.5
FEATURE [Part::Cylinder] Cylinder471  label="Válec471"
  Angle = 360
  AttacherType = Attacher::AttachEngine3D
  Height = 100
  Placement = pos=(16.0727,38.8029,0) rot=(0,0,1;3.14159rad)
  Radius = 1.5
FEATURE [Part::Cylinder] Cylinder472  label="Válec472"
  Angle = 360
  AttacherType = Attacher::AttachEngine3D
  Height = 100
  Placement = pos=(-16.0727,38.8029,0) rot=(0,0,1;3.92699rad)
  Radius = 1.5
FEATURE [Part::Cylinder] Cylinder473  label="Válec473"
  Angle = 360
  AttacherType = Attacher::AttachEngine3D
  Height = 100
  Placement = pos=(-38.8029,16.0727,0) rot=(0,0,-1;1.5708rad)
  Radius = 1.5
FEATURE [Part::Cylinder] Cylinder474  label="Válec474"
  Angle = 360
  AttacherType = Attacher::AttachEngine3D
  Height = 100
  Placement = pos=(-38.8029,-16.0727,0) rot=(0,0,-1;0.785398rad)
  Radius = 1.5
FEATURE [Part::Cylinder] Cylinder475  label="Válec475"
  Angle = 360
  AttacherType = Attacher::AttachEngine3D
  Height = 100
  Placement = pos=(-16.0727,-38.8029,0) rot=(0,0,1;0rad)
  Radius = 1.5
FEATURE [Part::Compound] Compound328
  Links = -> [Cylinder468,Cylinder469,Cylinder470,Cylinder471,Cylinder472,Cylinder473,Cylinder474,Cylinder475]
  Placement = pos=(0,0,20) rot=(0,0,-1;0.20944rad)
FEATURE [Part::Cut] Cut173
  Base = -> Cut163
  Tool = -> Compound325
FEATURE [Part::Cut] Cut174
  Base = -> Cut164
  Tool = -> Compound328
FEATURE [Part::Cut] Cut175  label="bazovina-loziskovina_stara"
  Base = -> Cut174
  Placement = pos=(0,0,0) rot=(0,0,-1;1.5708rad)
  Tool = -> Compound322
FEATURE [Part::FeaturePython] Tube024  # WARN: FeaturePython — macro-defined, semantics opaque (R4)
  AttacherType = Attacher::AttachEngine3D
  Height = 17
  InnerRadius = 53
  OuterRadius = 60
  Placement = pos=(0,0,20) rot=(0,0,1;0rad)
FEATURE [Part::Cylinder] Cylinder476  label="Válec476"
  Angle = 360
  AttacherType = Attacher::AttachEngine3D
  Height = 10
  Placement = pos=(-47,0,30) rot=(0,0,1;0rad)
  Radius = 3.5
FEATURE [Part::Cylinder] Cylinder197  label="Válec197"
  Angle = 360
  AttacherType = Attacher::AttachEngine3D
  Height = 20
  Placement = pos=(39.598,-39.598,2) rot=(0,0,1;0.785398rad)
  Radius = 1.5
FEATURE [Part::Cylinder] Cylinder187  label="Válec187"
  Angle = 360
  AttacherType = Attacher::AttachEngine3D
  Height = 20
  Placement = pos=(-52.3,0,29) rot=(0,0,1;0rad)
  Radius = 3.5
FEATURE [Part::Cylinder] Cylinder196  label="Válec196"
  Angle = 360
  AttacherType = Attacher::AttachEngine3D
  Height = 20
  Placement = pos=(0,-56,2) rot=(0,0,1;0rad)
  Radius = 1.5
FEATURE [Part::Cylinder] Cylinder198  label="Válec198"
  Angle = 360
  AttacherType = Attacher::AttachEngine3D
  Height = 20
  Placement = pos=(56,0,2) rot=(0,0,1;1.5708rad)
  Radius = 1.5
FEATURE [Part::Cylinder] Cylinder200  label="Válec200"
  Angle = 360
  AttacherType = Attacher::AttachEngine3D
  Height = 20
  Placement = pos=(-1.2e-14,56,2) rot=(0,0,1;3.14159rad)
  Radius = 1.5
FEATURE [Part::Cylinder] Cylinder202  label="Válec202"
  Angle = 360
  AttacherType = Attacher::AttachEngine3D
  Height = 20
  Placement = pos=(-56,-1.3e-14,2) rot=(0,0,-1;1.5708rad)
  Radius = 1.5
FEATURE [Part::Cylinder] Cylinder201  label="Válec201"
  Angle = 360
  AttacherType = Attacher::AttachEngine3D
  Height = 20
  Placement = pos=(-39.598,39.598,2) rot=(0,0,1;3.92699rad)
  Radius = 1.5
FEATURE [Part::Cylinder] Cylinder203  label="Válec203"
  Angle = 360
  AttacherType = Attacher::AttachEngine3D
  Height = 20
  Placement = pos=(-39.598,-39.598,2) rot=(0,0,-1;0.785398rad)
  Radius = 1.5
FEATURE [Part::Box] Box079  label="Krychle079"
  AttacherType = Attacher::AttachEngine3D
  Height = 2
  Length = 6
  Placement = pos=(60,-3,23) rot=(0,0,1;1.5708rad)
  Width = 8
FEATURE [Part::Box] Box078  label="Krychle078"
  AttacherType = Attacher::AttachEngine3D
  Height = 2
  Length = 6
  Placement = pos=(40.3051,-44.5477,23) rot=(0,0,1;0.785398rad)
  Width = 8
FEATURE [Part::Box] Box080  label="Krychle080"
  AttacherType = Attacher::AttachEngine3D
  Height = 2
  Length = 6
  Placement = pos=(44.5477,40.3051,23) rot=(0,0,1;2.35619rad)
  Width = 8
FEATURE [Part::Box] Box081  label="Krychle081"
  AttacherType = Attacher::AttachEngine3D
  Height = 2
  Length = 6
  Placement = pos=(3,60,23) rot=(0,0,1;3.14159rad)
  Width = 8
FEATURE [Part::Box] Box082  label="Krychle082"
  AttacherType = Attacher::AttachEngine3D
  Height = 2
  Length = 6
  Placement = pos=(-40.3051,44.5477,23) rot=(0,0,1;3.92699rad)
  Width = 8
FEATURE [Part::Cylinder] Cylinder199  label="Válec199"
  Angle = 360
  AttacherType = Attacher::AttachEngine3D
  Height = 20
  Placement = pos=(39.598,39.598,2) rot=(0,0,1;2.35619rad)
  Radius = 1.5
FEATURE [Part::Compound] Compound186
  Links = -> [Cylinder196,Cylinder197,Cylinder198,Cylinder199,Cylinder200,Cylinder201,Cylinder202,Cylinder203]
  Placement = pos=(0,0,5) rot=(0,0,1;0rad)
FEATURE [Part::Box] Box077  label="Krychle077"
  AttacherType = Attacher::AttachEngine3D
  Height = 2
  Length = 6
  Placement = pos=(-3,-60,23) rot=(0,0,1;0rad)
  Width = 8
FEATURE [Part::Cylinder] Cylinder207  label="Válec207"
  Angle = 360
  AttacherType = Attacher::AttachEngine3D
  Height = 20
  Placement = pos=(-39,-40,34) rot=(1,0,0;1.5708rad)
  Radius = 1.5
FEATURE [Part::Box] Box085  label="Krychle085"
  AttacherType = Attacher::AttachEngine3D
  Height = 17
  Length = 108
  Placement = pos=(-54,-53,20) rot=(0,0,1;0rad)
  Width = 46
FEATURE [Part::Box] Box090  label="Krychle090"
  AttacherType = Attacher::AttachEngine3D
  Height = 6
  Length = 6
  Placement = pos=(36,-45,31) rot=(0,0,1;0rad)
  Width = 2
FEATURE [Part::Box] Box089  label="Krychle089"
  AttacherType = Attacher::AttachEngine3D
  Height = 6
  Length = 6
  Placement = pos=(-42,-45,31) rot=(0,0,1;0rad)
  Width = 2
FEATURE [Part::Box] Box091  label="Krychle091"
  AttacherType = Attacher::AttachEngine3D
  Height = 6
  Length = 6
  Placement = pos=(-42,-45,31) rot=(0,0,1;0rad)
  Width = 2
FEATURE [Part::Compound] Compound192
  Links = -> [Box090,Box091]
FEATURE [Part::Cylinder] Cylinder210  label="Válec210"
  Angle = 360
  AttacherType = Attacher::AttachEngine3D
  Height = 20
  Placement = pos=(39,-40,34) rot=(1,0,0;1.5708rad)
  Radius = 1.5
FEATURE [Part::Box] Box084  label="Krychle084"
  AttacherType = Attacher::AttachEngine3D
  Height = 2
  Length = 6
  Placement = pos=(-44.5477,-40.3051,23) rot=(0,0,-1;0.785398rad)
  Width = 8
FEATURE [Part::Cylinder] Cylinder204  label="Válec204"
  Angle = 360
  AttacherType = Attacher::AttachEngine3D
  Height = 17
  Placement = pos=(0,0,20) rot=(0,0,1;0rad)
  Radius = 60
FEATURE [Part::Cut] Cut089
  Base = -> Box085
  Tool = -> Cylinder204
FEATURE [Part::Box] Box087  label="Krychle087"
  AttacherType = Attacher::AttachEngine3D
  Height = 6
  Length = 6
  Placement = pos=(-54,-45,22) rot=(0,0,1;0rad)
  Width = 2
FEATURE [Part::Box] Box083  label="Krychle083"
  AttacherType = Attacher::AttachEngine3D
  Height = 2
  Length = 6
  Placement = pos=(-60,3,23) rot=(0,0,-1;1.5708rad)
  Width = 8
FEATURE [Part::Compound] Compound187
  Links = -> [Box077,Box078,Box079,Box080,Box081,Box082,Box083,Box084]
FEATURE [Part::Cylinder] Cylinder205  label="Válec205"
  Angle = 360
  AttacherType = Attacher::AttachEngine3D
  Height = 20
  Placement = pos=(-51,-40,25) rot=(1,0,0;1.5708rad)
  Radius = 1.5
FEATURE [Part::Cylinder] Cylinder206  label="Válec206"
  Angle = 360
  AttacherType = Attacher::AttachEngine3D
  Height = 20
  Placement = pos=(51,-40,25) rot=(1,0,0;1.5708rad)
  Radius = 1.5
FEATURE [Part::Compound] Compound190
  Links = -> [Cylinder205,Cylinder206]
  Placement = pos=(0,2,0) rot=(0,0,1;0rad)
FEATURE [Part::Box] Box088  label="Krychle088"
  AttacherType = Attacher::AttachEngine3D
  Height = 6
  Length = 6
  Placement = pos=(36,-45,31) rot=(0,0,1;0rad)
  Width = 2
FEATURE [Part::Compound] Compound191
  Links = -> [Box088,Box089]
FEATURE [Part::Box] Box086  label="Krychle086"
  AttacherType = Attacher::AttachEngine3D
  Height = 6
  Length = 6
  Placement = pos=(48,-45,22) rot=(0,0,1;0rad)
  Width = 2
FEATURE [Part::Compound] Compound189
  Links = -> [Box086,Box087]
FEATURE [Part::Cut] Cut090
  Base = -> Cut089
  Tool = -> Compound189
FEATURE [Part::Cut] Cut091
  Base = -> Cut090
  Tool = -> Compound190
FEATURE [Part::Cut] Cut094
  Base = -> Cut091
  Tool = -> Compound192
FEATURE [Part::Cylinder] Cylinder208  label="Válec208"
  Angle = 360
  AttacherType = Attacher::AttachEngine3D
  Height = 20
  Placement = pos=(39,-40,34) rot=(1,0,0;1.5708rad)
  Radius = 1.5
FEATURE [Part::Compound] Compound193
  Links = -> [Cylinder207,Cylinder208]
FEATURE [Part::Cylinder] Cylinder209  label="Válec209"
  Angle = 360
  AttacherType = Attacher::AttachEngine3D
  Height = 20
  Placement = pos=(-39,-40,34) rot=(1,0,0;1.5708rad)
  Radius = 1.5
FEATURE [Part::Compound] Compound194
  Links = -> [Cylinder209,Cylinder210]
FEATURE [Part::Cut] Cut095
  Base = -> Cut094
  Tool = -> Compound194
FEATURE [Part::Cylinder] Cylinder477  label="Válec477"
  Angle = 360
  AttacherType = Attacher::AttachEngine3D
  Height = 17
  Placement = pos=(-60,-43,10) rot=(0,0,1;0rad)
  Radius = 6
FEATURE [Part::Box] Box111  label="Krychle111"
  AttacherType = Attacher::AttachEngine3D
  Height = 2
  Length = 6
  Placement = pos=(-41.7193,45.9619,23) rot=(0,0,1;3.92699rad)
  Width = 10
FEATURE [Part::Box] Box112  label="Krychle112"
  AttacherType = Attacher::AttachEngine3D
  Height = 2
  Length = 6
  Placement = pos=(-62,3,23) rot=(0,0,-1;1.5708rad)
  Width = 10
FEATURE [Part::Box] Box165  label="Krychle165"
  AttacherType = Attacher::AttachEngine3D
  Height = 2
  Length = 6
  Placement = pos=(-45.9619,-41.7193,23) rot=(0,0,-1;0.785398rad)
  Width = 10
FEATURE [Part::Box] Box166  label="Krychle166"
  AttacherType = Attacher::AttachEngine3D
  Height = 2
  Length = 6
  Placement = pos=(41.7193,-45.9619,23) rot=(0,0,1;0.785398rad)
  Width = 10
FEATURE [Part::Box] Box167  label="Krychle167"
  AttacherType = Attacher::AttachEngine3D
  Height = 2
  Length = 6
  Placement = pos=(-3,-62,23) rot=(0,0,1;0rad)
  Width = 10
FEATURE [Part::Box] Box168  label="Krychle168"
  AttacherType = Attacher::AttachEngine3D
  Height = 2
  Length = 6
  Placement = pos=(62,-3,23) rot=(0,0,1;1.5708rad)
  Width = 10
FEATURE [Part::Box] Box169  label="Krychle169"
  AttacherType = Attacher::AttachEngine3D
  Height = 2
  Length = 6
  Placement = pos=(45.9619,41.7193,23) rot=(0,0,1;2.35619rad)
  Width = 10
FEATURE [Part::Box] Box170  label="Krychle170"
  AttacherType = Attacher::AttachEngine3D
  Height = 17
  Length = 10
  Placement = pos=(50,-43,10) rot=(0,0,1;0rad)
  Width = 43
FEATURE [Part::Box] Box110  label="Krychle110"
  AttacherType = Attacher::AttachEngine3D
  Height = 2
  Length = 6
  Placement = pos=(3,62,23) rot=(0,0,1;3.14159rad)
  Width = 10
FEATURE [Part::Cylinder] Cylinder478  label="Válec478"
  Angle = 360
  AttacherType = Attacher::AttachEngine3D
  Height = 17
  Placement = pos=(60,-43,10) rot=(0,0,1;0rad)
  Radius = 6
FEATURE [Part::Box] Box171  label="Krychle171"
  AttacherType = Attacher::AttachEngine3D
  Height = 17
  Length = 10
  Placement = pos=(-60,-43,10) rot=(0,0,1;0rad)
  Width = 43
FEATURE [Part::Cylinder] Cylinder479  label="Válec479"
  Angle = 360
  AttacherType = Attacher::AttachEngine3D
  Height = 20
  Placement = pos=(39.598,39.598,2) rot=(0,0,1;2.35619rad)
  Radius = 1.5
FEATURE [Part::Cylinder] Cylinder480  label="Válec480"
  Angle = 360
  AttacherType = Attacher::AttachEngine3D
  Height = 20
  Placement = pos=(56,0,2) rot=(0,0,1;1.5708rad)
  Radius = 1.5
FEATURE [Part::Cylinder] Cylinder481  label="Válec481"
  Angle = 360
  AttacherType = Attacher::AttachEngine3D
  Height = 20
  Placement = pos=(-1.2e-14,56,2) rot=(0,0,1;3.14159rad)
  Radius = 1.5
FEATURE [Part::Cylinder] Cylinder482  label="Válec482"
  Angle = 360
  AttacherType = Attacher::AttachEngine3D
  Height = 20
  Placement = pos=(-39.598,39.598,2) rot=(0,0,1;3.92699rad)
  Radius = 1.5
FEATURE [Part::Cylinder] Cylinder483  label="Válec483"
  Angle = 360
  AttacherType = Attacher::AttachEngine3D
  Height = 20
  Placement = pos=(-56,-1.3e-14,2) rot=(0,0,-1;1.5708rad)
  Radius = 1.5
FEATURE [Part::Cylinder] Cylinder484  label="Válec484"
  Angle = 360
  AttacherType = Attacher::AttachEngine3D
  Height = 20
  Placement = pos=(0,-56,2) rot=(0,0,1;0rad)
  Radius = 1.5
FEATURE [Part::Cylinder] Cylinder485  label="Válec485"
  Angle = 360
  AttacherType = Attacher::AttachEngine3D
  Height = 20
  Placement = pos=(39.598,-39.598,2) rot=(0,0,1;0.785398rad)
  Radius = 1.5
FEATURE [Part::Cylinder] Cylinder486  label="Válec486"
  Angle = 360
  AttacherType = Attacher::AttachEngine3D
  Height = 20
  Placement = pos=(-39.598,-39.598,2) rot=(0,0,-1;0.785398rad)
  Radius = 1.5
FEATURE [Part::Cylinder] Cylinder487  label="Válec487"
  Angle = 360
  AttacherType = Attacher::AttachEngine3D
  Height = 17
  Placement = pos=(0,0,20) rot=(0,0,1;0rad)
  Radius = 60
FEATURE [Part::Cylinder] Cylinder488  label="Válec488"
  Angle = 360
  AttacherType = Attacher::AttachEngine3D
  Height = 22
  Placement = pos=(-51,-40,25) rot=(1,0,0;1.5708rad)
  Radius = 1.5
FEATURE [Part::Cylinder] Cylinder489  label="Válec489"
  Angle = 360
  AttacherType = Attacher::AttachEngine3D
  Height = 20
  Placement = pos=(51,-40,25) rot=(1,0,0;1.5708rad)
  Radius = 1.5
FEATURE [Part::Compound] Compound247
  Links = -> [Cylinder488,Cylinder489]
  Placement = pos=(0,2,0) rot=(0,0,1;0rad)
FEATURE [Part::Compound] Compound243
  Links = -> [Box110,Box111,Box112,Box165,Box167,Box166,Box168,Box169]
FEATURE [Part::Compound] Compound244
  Links = -> [Box171,Box170]
FEATURE [Part::Compound] Compound245
  Links = -> [Cylinder484,Cylinder485,Cylinder480,Cylinder479,Cylinder481,Cylinder482,Cylinder483,Cylinder486]
FEATURE [Part::Cut] Cut179
  Base = -> Compound244
  Tool = -> Compound245
FEATURE [Part::Compound] Compound246
  Links = -> [Cylinder478,Cylinder477]
FEATURE [Part::Cut] Cut178
  Base = -> Cut179
  Placement = pos=(0,0,10) rot=(0,0,1;0rad)
  Tool = -> Compound246
FEATURE [Part::Cut] Cut180
  Base = -> Cut178
  Tool = -> Cylinder487
FEATURE [Part::Cut] Cut176
  Base = -> Cut180
  Tool = -> Compound243
FEATURE [Part::Cut] Cut177
  Base = -> Cut176
  Tool = -> Compound247
FEATURE [Part::Fillet] Fillet003
  Base = -> Cut177
  Edges = 2 edges r=4: [Edge8,Edge61]
FEATURE [Part::Torus] Torus003  label="Anuloid003"
  Angle1 = -180
  Angle2 = 180
  Angle3 = 360
  AttacherType = Attacher::AttachEngine3D
  Placement = pos=(0,0,29) rot=(0,0,1;0rad)
  Radius1 = 51.9
  Radius2 = 3.1
FEATURE [Part::Cut] Cut054
  Base = -> Tube024
  Tool = -> Torus003
FEATURE [Part::Cut] Cut055
  Base = -> Cut054
  Tool = -> Cylinder476
FEATURE [Part::Cut] Cut084  label="J-max_lozo-harmo1"
  Base = -> Cut055
  Tool = -> Cylinder187
FEATURE [Part::Cut] Cut087
  Base = -> Cut084
  Tool = -> Compound186
FEATURE [Part::Cut] Cut088  label="J-max_lozo-harmo2"
  Base = -> Cut087
  Tool = -> Compound187
FEATURE [Part::Cut] Cut092
  Base = -> Cut088
  Tool = -> Compound193
FEATURE [Part::Cut] Cut093
  Base = -> Cut092
  Tool = -> Compound191
FEATURE [Part::Compound] Compound195  label="J-max_lozo-harmo4"
  Links = -> [Cut093,Cut095]
FEATURE [Part::Compound] Compound248  label="J-max_lozo-harmo"
  Links = -> [Compound195,Fillet003]
  Placement = pos=(52,13,-89) rot=(0,0.707107,-0.707107;3.14159rad)
FEATURE [Part::Cylinder] Cylinder490  label="Válec490"
  Angle = 360
  AttacherType = Attacher::AttachEngine3D
  Height = 10
  Radius = 60
FEATURE [Part::Cylinder] Cylinder491  label="Válec491"
  Angle = 360
  AttacherType = Attacher::AttachEngine3D
  Height = 10
  Radius = 52
FEATURE [Part::FeaturePython] wormgear027  # WARN: FeaturePython — macro-defined, semantics opaque (R4)
  AttacherType = Attacher::AttachEngine3D
  Placement = pos=(0,0,0) rot=(0,0,1;0.009355rad)
  beta = 29.4806
  clearance = 0.25
  diameter = 79.6
  head = 0
  height = 20
  module = 1
  pressure_angle = 20
  reverse_pitch = false
  teeth = 45
  version = 0.0.3
FEATURE [Part::Cut] Cut056
  Base = -> Cylinder491
  Tool = -> wormgear027
FEATURE [Part::FeaturePython] wormgear026  # WARN: FeaturePython — macro-defined, semantics opaque (R4)
  AttacherType = Attacher::AttachEngine3D
  beta = 29.4806
  clearance = 0.25
  diameter = 79.6
  head = 0
  height = 20
  module = 1
  pressure_angle = 20
  reverse_pitch = true
  teeth = 45
  version = 0.0.3
FEATURE [Part::Cut] Cut057
  Base = -> Cylinder490
  Placement = pos=(0,0,10) rot=(0,0,1;0.034907rad)
  Tool = -> wormgear026
FEATURE [Part::Compound] Compound157
  Links = -> [Cut057,Cut056]
FEATURE [Part::Cylinder] Cylinder492  label="Válec492"
  Angle = 360
  AttacherType = Attacher::AttachEngine3D
  Height = 20
  Placement = pos=(24,-40,-5) rot=(1,0,0;1.5708rad)
  Radius = 1.5
FEATURE [Part::Box] Box047  label="Krychle047"
  AttacherType = Attacher::AttachEngine3D
  Height = 6
  Length = 6
  Placement = pos=(-27,-47,-8) rot=(0,0,1;0rad)
  Width = 2
FEATURE [Part::Box] Box172  label="Krychle172"
  AttacherType = Attacher::AttachEngine3D
  Height = 6
  Length = 6
  Placement = pos=(48,-45,4) rot=(0,0,1;0rad)
  Width = 2
FEATURE [Part::Cylinder] Cylinder493  label="Válec493"
  Angle = 360
  AttacherType = Attacher::AttachEngine3D
  Height = 10
  Placement = pos=(0,0,20) rot=(0,0,1;0rad)
  Radius = 52
FEATURE [Part::Cylinder] Cylinder494  label="Válec494"
  Angle = 360
  AttacherType = Attacher::AttachEngine3D
  Height = 40
  Placement = pos=(59,-17,0) rot=(0,0,1;0rad)
  Radius = 10
FEATURE [Part::Box] Box173  label="Krychle173"
  AttacherType = Attacher::AttachEngine3D
  Height = 6
  Length = 6
  Placement = pos=(21,-47,-8) rot=(0,0,1;0rad)
  Width = 2
FEATURE [Part::Box] Box045  label="Krychle045"
  AttacherType = Attacher::AttachEngine3D
  Height = 10
  Length = 108
  Placement = pos=(-54,-53,20) rot=(0,0,1;0rad)
  Width = 36
FEATURE [Part::Cut] Cut184
  Base = -> Box045
  Placement = pos=(0,0,-20) rot=(0,0,1;0rad)
  Tool = -> Cylinder493
FEATURE [Part::Cylinder] Cylinder495  label="Válec495"
  Angle = 360
  AttacherType = Attacher::AttachEngine3D
  Height = 40
  Placement = pos=(-59,-17,0) rot=(0,0,1;0rad)
  Radius = 10
FEATURE [Part::Compound] Compound163
  Links = -> [Cylinder494,Cylinder495]
FEATURE [Part::Cylinder] Cylinder496  label="Válec496"
  Angle = 360
  AttacherType = Attacher::AttachEngine3D
  Height = 8
  Placement = pos=(0,0,20) rot=(0,0,1;0rad)
  Radius = 52
FEATURE [Part::Box] Box174  label="Krychle174"
  AttacherType = Attacher::AttachEngine3D
  Height = 8
  Length = 108
  Placement = pos=(-54,-53,20) rot=(0,0,1;0rad)
  Width = 36
FEATURE [Part::Cut] Cut183
  Base = -> Box174
  Placement = pos=(0,0,-20) rot=(0,0,1;0rad)
  Tool = -> Cylinder496
FEATURE [Part::Cut] Cut185
  Base = -> Cut183
  Placement = pos=(0,0,-8) rot=(0,0,1;0rad)
  Tool = -> Compound163
FEATURE [Part::Cylinder] Cylinder497  label="Válec497"
  Angle = 360
  AttacherType = Attacher::AttachEngine3D
  Height = 40
  Placement = pos=(-59,-17,0) rot=(0,0,1;0rad)
  Radius = 10
FEATURE [Part::Box] Box046  label="Krychle046"
  AttacherType = Attacher::AttachEngine3D
  Height = 10
  Length = 108
  Placement = pos=(-54,-53,20) rot=(0,0,1;0rad)
  Width = 36
FEATURE [Part::Cylinder] Cylinder498  label="Válec498"
  Angle = 360
  AttacherType = Attacher::AttachEngine3D
  Height = 20
  Placement = pos=(-24,-40,-5) rot=(1,0,0;1.5708rad)
  Radius = 1.5
FEATURE [Part::Cylinder] Cylinder499  label="Válec499"
  Angle = 360
  AttacherType = Attacher::AttachEngine3D
  Height = 40
  Placement = pos=(59,-17,0) rot=(0,0,1;0rad)
  Radius = 10
FEATURE [Part::Compound] Compound162
  Links = -> [Cylinder499,Cylinder497]
FEATURE [Part::Cut] Cut188
  Base = -> Cut184
  Tool = -> Compound162
FEATURE [Part::Cylinder] Cylinder500  label="Válec500"
  Angle = 360
  AttacherType = Attacher::AttachEngine3D
  Height = 10
  Placement = pos=(0,0,20) rot=(0,0,1;0rad)
  Radius = 52
FEATURE [Part::Cut] Cut189
  Base = -> Box046
  Placement = pos=(0,0,-10) rot=(0,0,1;0rad)
  Tool = -> Cylinder500
FEATURE [Part::FeaturePython] Tube025  # WARN: FeaturePython — macro-defined, semantics opaque (R4)
  AttacherType = Attacher::AttachEngine3D
  Height = 8
  InnerRadius = 42
  OuterRadius = 52
  Placement = pos=(0,0,-8) rot=(0,0,1;0rad)
FEATURE [Part::Cylinder] Cylinder501  label="Válec501"
  Angle = 360
  AttacherType = Attacher::AttachEngine3D
  Height = 20
  Placement = pos=(-51,-40,7) rot=(1,0,0;1.5708rad)
  Radius = 1.5
FEATURE [Part::Cylinder] Cylinder502  label="Válec502"
  Angle = 360
  AttacherType = Attacher::AttachEngine3D
  Height = 20
  Placement = pos=(-39.598,39.598,2) rot=(0,0,1;3.92699rad)
  Radius = 1.5
FEATURE [Part::Cylinder] Cylinder503  label="Válec503"
  Angle = 360
  AttacherType = Attacher::AttachEngine3D
  Height = 20
  Placement = pos=(-39.598,-39.598,2) rot=(0,0,-1;0.785398rad)
  Radius = 1.5
FEATURE [Part::Box] Box051  label="Krychle051"
  AttacherType = Attacher::AttachEngine3D
  Height = 6
  Length = 6
  Placement = pos=(-54,-45,4) rot=(0,0,1;0rad)
  Width = 2
FEATURE [Part::Compound] Compound169
  Links = -> [Box047,Box173,Box172,Box051]
FEATURE [Part::Cylinder] Cylinder504  label="Válec504"
  Angle = 360
  AttacherType = Attacher::AttachEngine3D
  Height = 20
  Placement = pos=(39.598,39.598,2) rot=(0,0,1;2.35619rad)
  Radius = 1.5
FEATURE [Part::Cylinder] Cylinder505  label="Válec505"
  Angle = 360
  AttacherType = Attacher::AttachEngine3D
  Height = 20
  Placement = pos=(56,0,2) rot=(0,0,1;1.5708rad)
  Radius = 1.5
FEATURE [Part::Cylinder] Cylinder154  label="Válec154"
  Angle = 360
  AttacherType = Attacher::AttachEngine3D
  Height = 20
  Placement = pos=(-1.2e-14,56,2) rot=(0,0,1;3.14159rad)
  Radius = 1.5
FEATURE [Part::Cylinder] Cylinder155  label="Válec155"
  Angle = 360
  AttacherType = Attacher::AttachEngine3D
  Height = 20
  Placement = pos=(0,-56,2) rot=(0,0,1;0rad)
  Radius = 1.5
FEATURE [Part::Cylinder] Cylinder506  label="Válec506"
  Angle = 360
  AttacherType = Attacher::AttachEngine3D
  Height = 20
  Placement = pos=(56,0,2) rot=(0,0,1;1.5708rad)
  Radius = 1.5
FEATURE [Part::Cylinder] Cylinder507  label="Válec507"
  Angle = 360
  AttacherType = Attacher::AttachEngine3D
  Height = 20
  Placement = pos=(51,-40,7) rot=(1,0,0;1.5708rad)
  Radius = 1.5
FEATURE [Part::Compound] Compound172
  Links = -> [Cylinder498,Cylinder492,Cylinder507,Cylinder501]
FEATURE [Part::Cylinder] Cylinder508  label="Válec508"
  Angle = 360
  AttacherType = Attacher::AttachEngine3D
  Height = 20
  Placement = pos=(0,-56,2) rot=(0,0,1;0rad)
  Radius = 1.5
FEATURE [Part::Cylinder] Cylinder509  label="Válec509"
  Angle = 360
  AttacherType = Attacher::AttachEngine3D
  Height = 20
  Placement = pos=(-56,-1.3e-14,2) rot=(0,0,-1;1.5708rad)
  Radius = 1.5
FEATURE [Part::Cylinder] Cylinder510  label="Válec510"
  Angle = 360
  AttacherType = Attacher::AttachEngine3D
  Height = 20
  Placement = pos=(-1.2e-14,56,2) rot=(0,0,1;3.14159rad)
  Radius = 1.5
FEATURE [Part::Cylinder] Cylinder511  label="Válec511"
  Angle = 360
  AttacherType = Attacher::AttachEngine3D
  Height = 20
  Placement = pos=(-39.598,39.598,2) rot=(0,0,1;3.92699rad)
  Radius = 1.5
FEATURE [Part::Cylinder] Cylinder512  label="Válec512"
  Angle = 360
  AttacherType = Attacher::AttachEngine3D
  Height = 20
  Placement = pos=(39.598,-39.598,2) rot=(0,0,1;0.785398rad)
  Radius = 1.5
FEATURE [Part::Cylinder] Cylinder513  label="Válec513"
  Angle = 360
  AttacherType = Attacher::AttachEngine3D
  Height = 20
  Placement = pos=(-39.598,-39.598,2) rot=(0,0,-1;0.785398rad)
  Radius = 1.5
FEATURE [Part::Compound] Compound164
  Links = -> [Cylinder508,Cylinder512,Cylinder506,Cylinder504,Cylinder510,Cylinder502,Cylinder509,Cylinder513]
FEATURE [Part::Cut] Cut187
  Base = -> Compound157
  Tool = -> Compound164
FEATURE [Part::Cylinder] Cylinder514  label="Válec514"
  Angle = 360
  AttacherType = Attacher::AttachEngine3D
  Height = 20
  Placement = pos=(-39.6,-39.6,-10) rot=(0,0,-1;0.785398rad)
  Radius = 4
FEATURE [Part::Box] Box057  label="Krychle057"
  AttacherType = Attacher::AttachEngine3D
  Height = 6
  Length = 6
  Placement = pos=(21,-47,-8) rot=(0,0,1;0rad)
  Width = 2
FEATURE [Part::Box] Box058  label="Krychle058"
  AttacherType = Attacher::AttachEngine3D
  Height = 6
  Length = 6
  Placement = pos=(-27,-47,-8) rot=(0,0,1;0rad)
  Width = 2
FEATURE [Part::Cylinder] Cylinder156  label="Válec156"
  Angle = 360
  AttacherType = Attacher::AttachEngine3D
  Height = 20
  Placement = pos=(39.598,39.598,2) rot=(0,0,1;2.35619rad)
  Radius = 1.5
FEATURE [Part::Cylinder] Cylinder515  label="Válec515"
  Angle = 360
  AttacherType = Attacher::AttachEngine3D
  Height = 20
  Placement = pos=(39.6,-39.6,-10) rot=(0,0,1;0.785398rad)
  Radius = 4
FEATURE [Part::Compound] Compound166
  Links = -> [Cylinder514,Cylinder515]
FEATURE [Part::Cut] Cut069
  Base = -> Cut187
  Tool = -> Compound166
FEATURE [Part::Cylinder] Cylinder164  label="Válec164"
  Angle = 360
  AttacherType = Attacher::AttachEngine3D
  Height = 20
  Placement = pos=(-39.6,-39.6,-10) rot=(0,0,-1;0.785398rad)
  Radius = 4
FEATURE [Part::Cylinder] Cylinder162  label="Válec162"
  Angle = 360
  AttacherType = Attacher::AttachEngine3D
  Height = 20
  Placement = pos=(-39.6,-39.6,-10) rot=(0,0,-1;0.785398rad)
  Radius = 4
FEATURE [Part::Cylinder] Cylinder163  label="Válec163"
  Angle = 360
  AttacherType = Attacher::AttachEngine3D
  Height = 20
  Placement = pos=(39.6,-39.6,-10) rot=(0,0,1;0.785398rad)
  Radius = 4
FEATURE [Part::Compound] Compound168
  Links = -> [Cylinder164,Cylinder163]
FEATURE [Part::Cut] Cut071
  Base = -> Cut188
  Tool = -> Compound168
FEATURE [Part::Box] Box052  label="Krychle052"
  AttacherType = Attacher::AttachEngine3D
  Height = 6
  Length = 6
  Placement = pos=(48,-45,4) rot=(0,0,1;0rad)
  Width = 2
FEATURE [Part::Box] Box053  label="Krychle053"
  AttacherType = Attacher::AttachEngine3D
  Height = 6
  Length = 6
  Placement = pos=(17,-47,-8) rot=(0,0,1;0rad)
  Width = 2
FEATURE [Part::Box] Box054  label="Krychle054"
  AttacherType = Attacher::AttachEngine3D
  Height = 6
  Length = 6
  Placement = pos=(-23,-47,-8) rot=(0,0,1;0rad)
  Width = 2
FEATURE [Part::Cylinder] Cylinder161  label="Válec161"
  Angle = 360
  AttacherType = Attacher::AttachEngine3D
  Height = 20
  Placement = pos=(39.6,-39.6,-10) rot=(0,0,1;0.785398rad)
  Radius = 4
FEATURE [Part::Compound] Compound167
  Links = -> [Cylinder162,Cylinder161]
FEATURE [Part::Cut] Cut070
  Base = -> Cut185
  Tool = -> Compound167
FEATURE [Part::Cut] Cut072
  Base = -> Cut070
  Tool = -> Compound169
FEATURE [Part::Box] Box055  label="Krychle055"
  AttacherType = Attacher::AttachEngine3D
  Height = 6
  Length = 6
  Placement = pos=(-54,-45,4) rot=(0,0,1;0rad)
  Width = 2
FEATURE [Part::Compound] Compound170
  Links = -> [Box054,Box053,Box052,Box055]
FEATURE [Part::Cut] Cut186
  Base = -> Cut071
  Tool = -> Compound170
FEATURE [Part::Box] Box056  label="Krychle056"
  AttacherType = Attacher::AttachEngine3D
  Height = 6
  Length = 6
  Placement = pos=(48,-45,4) rot=(0,0,1;0rad)
  Width = 2
FEATURE [Part::Cylinder] Cylinder516  label="Válec516"
  Angle = 360
  AttacherType = Attacher::AttachEngine3D
  Height = 20
  Placement = pos=(-56,-1.3e-14,2) rot=(0,0,-1;1.5708rad)
  Radius = 1.5
FEATURE [Part::Cylinder] Cylinder517  label="Válec517"
  Angle = 360
  AttacherType = Attacher::AttachEngine3D
  Height = 20
  Placement = pos=(39.598,-39.598,2) rot=(0,0,1;0.785398rad)
  Radius = 1.5
FEATURE [Part::Compound] Compound165
  Links = -> [Cylinder155,Cylinder517,Cylinder505,Cylinder156,Cylinder154,Cylinder511,Cylinder516,Cylinder503]
FEATURE [Part::Cut] Cut181
  Base = -> Cut189
  Tool = -> Compound165
FEATURE [Part::Box] Box062  label="Krychle062"
  AttacherType = Attacher::AttachEngine3D
  Height = 2
  Length = 6
  Placement = pos=(-41,-3,-4) rot=(0,0,1;1.5708rad)
  Width = 8
FEATURE [Part::Cylinder] Cylinder166  label="Válec166"
  Angle = 360
  AttacherType = Attacher::AttachEngine3D
  Height = 20
  Placement = pos=(24,-40,-5) rot=(1,0,0;1.5708rad)
  Radius = 1.5
FEATURE [Part::Cylinder] Cylinder167  label="Válec167"
  Angle = 360
  AttacherType = Attacher::AttachEngine3D
  Height = 20
  Placement = pos=(51,-40,7) rot=(1,0,0;1.5708rad)
  Radius = 1.5
FEATURE [Part::Box] Box061  label="Krychle061"
  AttacherType = Attacher::AttachEngine3D
  Height = 2
  Length = 6
  Placement = pos=(-31.1127,26.8701,-4) rot=(0,0,1;0.785398rad)
  Width = 8
FEATURE [Part::Box] Box067  label="Krychle067"
  AttacherType = Attacher::AttachEngine3D
  Height = 2
  Length = 6
  Placement = pos=(26.8701,31.1127,-4) rot=(0,0,-1;0.785398rad)
  Width = 8
FEATURE [Part::Cylinder] Cylinder175  label="Válec175"
  Angle = 360
  AttacherType = Attacher::AttachEngine3D
  Height = 20
  Placement = pos=(-45,-6e-15,-18) rot=(0,0,1;1.5708rad)
  Radius = 1.5
FEATURE [Part::Cylinder] Cylinder177  label="Válec177"
  Angle = 360
  AttacherType = Attacher::AttachEngine3D
  Height = 20
  Placement = pos=(1.4e-14,-45,-18) rot=(0,0,1;3.14159rad)
  Radius = 1.5
FEATURE [Part::Box] Box059  label="Krychle059"
  AttacherType = Attacher::AttachEngine3D
  Height = 6
  Length = 6
  Placement = pos=(-54,-45,4) rot=(0,0,1;0rad)
  Width = 2
FEATURE [Part::Compound] Compound171
  Links = -> [Box058,Box057,Box056,Box059]
FEATURE [Part::Cut] Cut182
  Base = -> Tube025
  Tool = -> Compound171
FEATURE [Part::Cut] Cut075
  Base = -> Cut182
  Tool = -> Compound172
FEATURE [Part::Cylinder] Cylinder170  label="Válec170"
  Angle = 360
  AttacherType = Attacher::AttachEngine3D
  Height = 20
  Placement = pos=(20,-40,-5) rot=(1,0,0;1.5708rad)
  Radius = 1.5
FEATURE [Part::Cylinder] Cylinder172  label="Válec172"
  Angle = 360
  AttacherType = Attacher::AttachEngine3D
  Height = 20
  Placement = pos=(-51,-40,7) rot=(1,0,0;1.5708rad)
  Radius = 1.5
FEATURE [Part::Cylinder] Cylinder169  label="Válec169"
  Angle = 360
  AttacherType = Attacher::AttachEngine3D
  Height = 20
  Placement = pos=(-20,-40,-5) rot=(1,0,0;1.5708rad)
  Radius = 1.5
FEATURE [Part::Cylinder] Cylinder168  label="Válec168"
  Angle = 360
  AttacherType = Attacher::AttachEngine3D
  Height = 20
  Placement = pos=(-51,-40,7) rot=(1,0,0;1.5708rad)
  Radius = 1.5
FEATURE [Part::Cylinder] Cylinder171  label="Válec171"
  Angle = 360
  AttacherType = Attacher::AttachEngine3D
  Height = 20
  Placement = pos=(51,-40,7) rot=(1,0,0;1.5708rad)
  Radius = 1.5
FEATURE [Part::Compound] Compound174
  Links = -> [Cylinder169,Cylinder170,Cylinder171,Cylinder172]
FEATURE [Part::Cut] Cut077
  Base = -> Cut186
  Tool = -> Compound174
FEATURE [Part::Box] Box060  label="Krychle060"
  AttacherType = Attacher::AttachEngine3D
  Height = 2
  Length = 6
  Placement = pos=(-3,41,-4) rot=(0,0,1;0rad)
  Width = 8
FEATURE [Part::Cylinder] Cylinder173  label="Válec173"
  Angle = 360
  AttacherType = Attacher::AttachEngine3D
  Height = 20
  Placement = pos=(0,45,-18) rot=(0,0,1;0rad)
  Radius = 1.5
FEATURE [Part::Cylinder] Cylinder165  label="Válec165"
  Angle = 360
  AttacherType = Attacher::AttachEngine3D
  Height = 20
  Placement = pos=(-24,-40,-5) rot=(1,0,0;1.5708rad)
  Radius = 1.5
FEATURE [Part::Compound] Compound173
  Links = -> [Cylinder165,Cylinder166,Cylinder167,Cylinder168]
FEATURE [Part::Cut] Cut076
  Base = -> Cut072
  Tool = -> Compound173
FEATURE [Part::Box] Box063  label="Krychle063"
  AttacherType = Attacher::AttachEngine3D
  Height = 2
  Length = 6
  Placement = pos=(-26.8701,-31.1127,-4) rot=(0,0,1;2.35619rad)
  Width = 8
FEATURE [Part::Box] Box064  label="Krychle064"
  AttacherType = Attacher::AttachEngine3D
  Height = 2
  Length = 6
  Placement = pos=(3,-41,-4) rot=(0,0,1;3.14159rad)
  Width = 8
FEATURE [Part::Box] Box065  label="Krychle065"
  AttacherType = Attacher::AttachEngine3D
  Height = 2
  Length = 6
  Placement = pos=(31.1127,-26.8701,-4) rot=(0,0,1;3.92699rad)
  Width = 8
FEATURE [Part::Box] Box066  label="Krychle066"
  AttacherType = Attacher::AttachEngine3D
  Height = 2
  Length = 6
  Placement = pos=(41,3,-4) rot=(0,0,-1;1.5708rad)
  Width = 8
FEATURE [Part::Cylinder] Cylinder174  label="Válec174"
  Angle = 360
  AttacherType = Attacher::AttachEngine3D
  Height = 20
  Placement = pos=(-31.8198,31.8198,-18) rot=(0,0,1;0.785398rad)
  Radius = 1.5
FEATURE [Part::Cylinder] Cylinder176  label="Válec176"
  Angle = 360
  AttacherType = Attacher::AttachEngine3D
  Height = 20
  Placement = pos=(-31.8198,-31.8198,-18) rot=(0,0,1;2.35619rad)
  Radius = 1.5
FEATURE [Part::Cylinder] Cylinder178  label="Válec178"
  Angle = 360
  AttacherType = Attacher::AttachEngine3D
  Height = 20
  Placement = pos=(31.8198,-31.8198,-18) rot=(0,0,1;3.92699rad)
  Radius = 1.5
FEATURE [Part::Cylinder] Cylinder179  label="Válec179"
  Angle = 360
  AttacherType = Attacher::AttachEngine3D
  Height = 20
  Placement = pos=(45,1.9e-14,-18) rot=(0,0,-1;1.5708rad)
  Radius = 1.5
FEATURE [Part::Cylinder] Cylinder180  label="Válec180"
  Angle = 360
  AttacherType = Attacher::AttachEngine3D
  Height = 20
  Placement = pos=(31.8198,31.8198,-18) rot=(0,0,-1;0.785398rad)
  Radius = 1.5
FEATURE [Part::Compound] Compound175
  Links = -> [Box060,Box061,Box062,Box063,Box064,Box065,Box066,Box067]
  Placement = pos=(0,0,0) rot=(0,0,1;0.392699rad)
FEATURE [Part::Cut] Cut078
  Base = -> Cut075
  Tool = -> Compound175
FEATURE [Part::Compound] Compound176
  Links = -> [Cylinder173,Cylinder174,Cylinder175,Cylinder176,Cylinder177,Cylinder178,Cylinder179,Cylinder180]
  Placement = pos=(0,0,0) rot=(0,0,1;0.392699rad)
FEATURE [Part::Cut] Cut079
  Base = -> Cut078
  Tool = -> Compound176
FEATURE [Part::Compound] Compound177  label="joint_max_monoblok1"
  Links = -> [Cut077,Cut079,Cut076,Cut069,Cut181]
FEATURE [Part::Fillet] Fillet004
  Base = -> Compound177
  Edges = 2 edges r=9: [Edge42,Edge278]
FEATURE [Part::Fillet] Fillet001  label="J-max_monoblok2"
  Base = -> Fillet004
  Edges = 2 edges r=8: [Edge30,Edge90]
FEATURE [Part::Box] Box108  label="Krychle108"
  AttacherType = Attacher::AttachEngine3D
  Height = 10
  Length = 10
  Placement = pos=(50,-43,10) rot=(0,0,1;0rad)
  Width = 43
FEATURE [Part::Cylinder] Cylinder518  label="Válec518"
  Angle = 360
  AttacherType = Attacher::AttachEngine3D
  Height = 20
  Placement = pos=(-39.598,-39.598,2) rot=(0,0,-1;0.785398rad)
  Radius = 1.5
FEATURE [Part::Cylinder] Cylinder519  label="Válec519"
  Angle = 360
  AttacherType = Attacher::AttachEngine3D
  Height = 20
  Placement = pos=(0,-56,2) rot=(0,0,1;0rad)
  Radius = 1.5
FEATURE [Part::Cylinder] Cylinder520  label="Válec520"
  Angle = 360
  AttacherType = Attacher::AttachEngine3D
  Height = 20
  Placement = pos=(-39.598,39.598,2) rot=(0,0,1;3.92699rad)
  Radius = 1.5
FEATURE [Part::Cylinder] Cylinder521  label="Válec521"
  Angle = 360
  AttacherType = Attacher::AttachEngine3D
  Height = 20
  Placement = pos=(56,0,2) rot=(0,0,1;1.5708rad)
  Radius = 1.5
FEATURE [Part::Cylinder] Cylinder522  label="Válec522"
  Angle = 360
  AttacherType = Attacher::AttachEngine3D
  Height = 10
  Placement = pos=(60,-43,10) rot=(0,0,1;0rad)
  Radius = 6
FEATURE [Part::Box] Box109  label="Krychle109"
  AttacherType = Attacher::AttachEngine3D
  Height = 10
  Length = 10
  Placement = pos=(-60,-43,10) rot=(0,0,1;0rad)
  Width = 43
FEATURE [Part::Cylinder] Cylinder523  label="Válec523"
  Angle = 360
  AttacherType = Attacher::AttachEngine3D
  Height = 20
  Placement = pos=(39.598,39.598,2) rot=(0,0,1;2.35619rad)
  Radius = 1.5
FEATURE [Part::Cylinder] Cylinder524  label="Válec524"
  Angle = 360
  AttacherType = Attacher::AttachEngine3D
  Height = 20
  Placement = pos=(39.598,-39.598,2) rot=(0,0,1;0.785398rad)
  Radius = 1.5
FEATURE [Part::Cylinder] Cylinder525  label="Válec525"
  Angle = 360
  AttacherType = Attacher::AttachEngine3D
  Height = 20
  Placement = pos=(-56,-1.3e-14,2) rot=(0,0,-1;1.5708rad)
  Radius = 1.5
FEATURE [Part::Cylinder] Cylinder526  label="Válec526"
  Angle = 360
  AttacherType = Attacher::AttachEngine3D
  Height = 10
  Placement = pos=(-60,-43,10) rot=(0,0,1;0rad)
  Radius = 6
FEATURE [Part::Cylinder] Cylinder527  label="Válec527"
  Angle = 360
  AttacherType = Attacher::AttachEngine3D
  Height = 20
  Placement = pos=(-1.2e-14,56,2) rot=(0,0,1;3.14159rad)
  Radius = 1.5
FEATURE [Part::Compound] Compound240
  Links = -> [Cylinder519,Cylinder524,Cylinder521,Cylinder523,Cylinder527,Cylinder520,Cylinder525,Cylinder518]
FEATURE [Part::Compound] Compound239
  Links = -> [Box109,Box108]
FEATURE [Part::Cut] Cut190
  Base = -> Compound239
  Tool = -> Compound240
FEATURE [Part::Compound] Compound241
  Links = -> [Cylinder522,Cylinder526]
FEATURE [Part::Cut] Cut191
  Base = -> Cut190
  Tool = -> Compound241
FEATURE [Part::Fillet] Fillet002
  Base = -> Cut191
  Edges = 2 edges r=4: [Edge4,Edge43]
FEATURE [Part::Compound] Compound242  label="J-max_monoblok"
  Links = -> [Fillet002,Fillet001]
  Placement = pos=(52,13,-89) rot=(0,0.707107,-0.707107;3.14159rad)
FEATURE [Part::Cylinder] Cylinder528  label="Válec528"
  Angle = 360
  AttacherType = Attacher::AttachEngine3D
  Height = 100
  Placement = pos=(-39,-21,0) rot=(0,0,1;0rad)
  Radius = 1.5
FEATURE [Part::Cylinder] Cylinder529  label="Válec529"
  Angle = 360
  AttacherType = Attacher::AttachEngine3D
  Height = 100
  Placement = pos=(39,-21,0) rot=(0,0,1;0rad)
  Radius = 1.5
FEATURE [Part::Cylinder] Cylinder530  label="Válec530"
  Angle = 360
  AttacherType = Attacher::AttachEngine3D
  Height = 100
  Placement = pos=(38.8029,-16.0727,0) rot=(0,0,1;1.5708rad)
  Radius = 1.5
FEATURE [Part::Cylinder] Cylinder531  label="Válec531"
  Angle = 360
  AttacherType = Attacher::AttachEngine3D
  Height = 20
  Placement = pos=(0,0,91) rot=(0,0,1;0rad)
  Radius = 38
FEATURE [Part::Cylinder] Cylinder532  label="Válec532"
  Angle = 360
  AttacherType = Attacher::AttachEngine3D
  Height = 20
  Placement = pos=(0,0,91) rot=(0,0,1;0rad)
  Radius = 38
FEATURE [Part::FeaturePython] wormgear028  # WARN: FeaturePython — macro-defined, semantics opaque (R4)
  AttacherType = Attacher::AttachEngine3D
  Placement = pos=(0,0,100) rot=(0,0,1;0rad)
  beta = 33.6901
  clearance = 0.25
  diameter = 120
  head = 0
  height = 5
  module = 1
  pressure_angle = 20
  reverse_pitch = true
  teeth = 80
  version = 0.0.3
FEATURE [Part::Cut] Cut194
  Base = -> wormgear028
  Placement = pos=(0,0,-63) rot=(0,0,1;0rad)
  Tool = -> Cylinder531
FEATURE [Part::FeaturePython] wormgear029  # WARN: FeaturePython — macro-defined, semantics opaque (R4)
  AttacherType = Attacher::AttachEngine3D
  Placement = pos=(0,0,95) rot=(0,0,1;0.032289rad)
  beta = 33.6901
  clearance = 0.25
  diameter = 120
  head = 0
  height = 5
  module = 1
  pressure_angle = 20
  reverse_pitch = false
  teeth = 80
  version = 0.0.3
FEATURE [Part::Cut] Cut195
  Base = -> wormgear029
  Placement = pos=(0,0,-63) rot=(0,0,1;0rad)
  Tool = -> Cylinder532
FEATURE [Part::Cylinder] Cylinder533  label="Válec533"
  Angle = 360
  AttacherType = Attacher::AttachEngine3D
  Height = 100
  Placement = pos=(-16.0727,38.8029,0) rot=(0,0,1;3.92699rad)
  Radius = 1.5
FEATURE [Part::Cylinder] Cylinder534  label="Válec534"
  Angle = 360
  AttacherType = Attacher::AttachEngine3D
  Height = 100
  Placement = pos=(38.8029,-16.0727,0) rot=(0,0,1;1.5708rad)
  Radius = 1.5
FEATURE [Part::Cylinder] Cylinder535  label="Válec535"
  Angle = 360
  AttacherType = Attacher::AttachEngine3D
  Height = 100
  Placement = pos=(-38.8029,-16.0727,0) rot=(0,0,-1;0.785398rad)
  Radius = 1.5
FEATURE [Part::Cylinder] Cylinder536  label="Válec536"
  Angle = 360
  AttacherType = Attacher::AttachEngine3D
  Height = 100
  Placement = pos=(9.09046,-41.0044,0) rot=(0,0,1;0.610865rad)
  Radius = 1.5
FEATURE [Part::Cylinder] Cylinder537  label="Válec537"
  Angle = 360
  AttacherType = Attacher::AttachEngine3D
  Height = 100
  Placement = pos=(-38.8029,16.0727,0) rot=(0,0,-1;1.5708rad)
  Radius = 1.5
FEATURE [Part::Cylinder] Cylinder538  label="Válec538"
  Angle = 360
  AttacherType = Attacher::AttachEngine3D
  Height = 100
  Placement = pos=(38.8029,16.0727,0) rot=(0,0,1;2.35619rad)
  Radius = 1.5
FEATURE [Part::Cylinder] Cylinder539  label="Válec539"
  Angle = 360
  AttacherType = Attacher::AttachEngine3D
  Height = 100
  Placement = pos=(-16.0727,-38.8029,0) rot=(0,0,1;0rad)
  Radius = 1.5
FEATURE [Part::Cylinder] Cylinder540  label="Válec540"
  Angle = 360
  AttacherType = Attacher::AttachEngine3D
  Height = 100
  Placement = pos=(9.09046,41.0044,0) rot=(0,0,1;3.31613rad)
  Radius = 1.5
FEATURE [Part::Compound] Compound336
  Links = -> [Cylinder536,Cylinder534,Cylinder538,Cylinder540,Cylinder533,Cylinder537,Cylinder535,Cylinder539]
FEATURE [Part::Cut] Cut192
  Base = -> Cut194
  Tool = -> Compound336
FEATURE [Part::Cylinder] Cylinder541  label="Válec541"
  Angle = 360
  AttacherType = Attacher::AttachEngine3D
  Height = 100
  Placement = pos=(9.09046,-41.0044,0) rot=(0,0,1;0.610865rad)
  Radius = 1.5
FEATURE [Part::Cylinder] Cylinder542  label="Válec542"
  Angle = 360
  AttacherType = Attacher::AttachEngine3D
  Height = 100
  Placement = pos=(9.09046,41.0044,0) rot=(0,0,1;3.31613rad)
  Radius = 1.5
FEATURE [Part::Cylinder] Cylinder543  label="Válec543"
  Angle = 360
  AttacherType = Attacher::AttachEngine3D
  Height = 100
  Placement = pos=(-16.0727,38.8029,0) rot=(0,0,1;3.92699rad)
  Radius = 1.5
FEATURE [Part::Cylinder] Cylinder544  label="Válec544"
  Angle = 360
  AttacherType = Attacher::AttachEngine3D
  Height = 100
  Placement = pos=(-38.8029,16.0727,0) rot=(0,0,-1;1.5708rad)
  Radius = 1.5
FEATURE [Part::Cylinder] Cylinder545  label="Válec545"
  Angle = 360
  AttacherType = Attacher::AttachEngine3D
  Height = 100
  Placement = pos=(-38.8029,-16.0727,0) rot=(0,0,-1;0.785398rad)
  Radius = 1.5
FEATURE [Part::Cylinder] Cylinder546  label="Válec546"
  Angle = 360
  AttacherType = Attacher::AttachEngine3D
  Height = 100
  Placement = pos=(38.8029,16.0727,0) rot=(0,0,1;2.35619rad)
  Radius = 1.5
FEATURE [Part::Cylinder] Cylinder547  label="Válec547"
  Angle = 360
  AttacherType = Attacher::AttachEngine3D
  Height = 100
  Placement = pos=(-16.0727,-38.8029,0) rot=(0,0,1;0rad)
  Radius = 1.5
FEATURE [Part::Compound] Compound337
  Links = -> [Cylinder541,Cylinder530,Cylinder546,Cylinder542,Cylinder543,Cylinder544,Cylinder545,Cylinder547]
FEATURE [Part::Cut] Cut193
  Base = -> Cut195
  Tool = -> Compound337
FEATURE [Part::Compound] Compound335  label="bazovina-part-D_ozubo"
  Links = -> [Cut192,Cut193]
FEATURE [Mesh::Feature] Mesh  label="bazovina-prevod-B (Meshed)"
FEATURE [Part::Cylinder] Cylinder548  label="Válec548"
  Angle = 360
  AttacherType = Attacher::AttachEngine3D
  Height = 20
  Placement = pos=(0,-63.8,4.5) rot=(0,0,1;0rad)
  Radius = 3.5
FEATURE [Part::Box] Box176  label="Krychle176"
  AttacherType = Attacher::AttachEngine3D
  Height = 15
  Length = 148
  Placement = pos=(-74,0,16) rot=(0,0,1;0rad)
  Width = 48
FEATURE [Part::Cylinder] Cylinder549  label="Válec549"
  Angle = 360
  AttacherType = Attacher::AttachEngine3D
  Height = 15
  Placement = pos=(0,0,16) rot=(0,0,1;0rad)
  Radius = 74
FEATURE [Part::FeaturePython] Tube026  # WARN: FeaturePython — macro-defined, semantics opaque (R4)
  AttacherType = Attacher::AttachEngine3D
  Height = 15
  InnerRadius = 64.5
  OuterRadius = 74
  Placement = pos=(0,0,16) rot=(0,0,1;0rad)
FEATURE [Part::Torus] Torus004  label="Anuloid004"
  Angle1 = -180
  Angle2 = 180
  Angle3 = 360
  AttacherType = Attacher::AttachEngine3D
  Placement = pos=(0,0,24.5) rot=(0,0,1;0rad)
  Radius1 = 64.2
  Radius2 = 3.1
FEATURE [Part::Cut] Cut196
  Base = -> Box176
  Tool = -> Cylinder549
FEATURE [Part::Cut] Cut206
  Base = -> Tube026
  Tool = -> Torus004
FEATURE [Part::Cut] Cut202
  Base = -> Cut206
  Tool = -> Cylinder548
FEATURE [Part::Box] Box209  label="Krychle209"
  AttacherType = Attacher::AttachEngine3D
  Height = 6
  Length = 8
  Placement = pos=(-75,38,21) rot=(0,0,1;0rad)
  Width = 2
FEATURE [Part::Box] Box208  label="Krychle208"
  AttacherType = Attacher::AttachEngine3D
  Height = 6
  Length = 8
  Placement = pos=(67,38,21) rot=(0,0,1;0rad)
  Width = 2
FEATURE [Part::Compound] Compound338
  Links = -> [Box208,Box209]
FEATURE [Part::Cylinder] Cylinder550  label="Válec550"
  Angle = 360
  AttacherType = Attacher::AttachEngine3D
  Height = 15
  Placement = pos=(0,0,16) rot=(0,0,1;0rad)
  Radius = 74
FEATURE [Part::Cut] Cut207
  Base = -> Cut196
  Tool = -> Cylinder550
FEATURE [Part::Compound] Compound340
  Links = -> [Cut207,Cut202]
FEATURE [Part::Cut] Cut201
  Base = -> Compound340
  Tool = -> Compound338
FEATURE [Part::Cylinder] Cylinder551  label="Válec551"
  Angle = 360
  AttacherType = Attacher::AttachEngine3D
  Height = 50
  Placement = pos=(-71,80,24) rot=(1,0,0;1.5708rad)
  Radius = 1.5
FEATURE [Part::Cylinder] Cylinder552  label="Válec552"
  Angle = 360
  AttacherType = Attacher::AttachEngine3D
  Height = 50
  Placement = pos=(71,80,24) rot=(1,0,0;1.5708rad)
  Radius = 1.5
FEATURE [Part::Compound] Compound339
  Links = -> [Cylinder552,Cylinder551]
FEATURE [Part::Cut] Cut205
  Base = -> Cut201
  Tool = -> Compound339
FEATURE [Part::Box] Box179  label="Krychle179"
  AttacherType = Attacher::AttachEngine3D
  Height = 47
  Length = 56
  Placement = pos=(-28,0,29) rot=(0,0,1;0rad)
  Width = 200
FEATURE [Part::Cut] Cut203
  Base = -> Cut205
  Tool = -> Box179
FEATURE [Part::Cylinder] Cylinder976  label="Válec976"
  Angle = 360
  AttacherType = Attacher::AttachEngine3D
  Height = 60
  Placement = pos=(71,-1.8e-14,0) rot=(0,0,1;1.5708rad)
  Radius = 1.5
FEATURE [Part::Cylinder] Cylinder973  label="Válec973"
  Angle = 360
  AttacherType = Attacher::AttachEngine3D
  Height = 60
  Placement = pos=(0,-71,0) rot=(0,0,1;0rad)
  Radius = 1.5
FEATURE [Part::Cylinder] Cylinder975  label="Válec975"
  Angle = 360
  AttacherType = Attacher::AttachEngine3D
  Height = 60
  Placement = pos=(61.4878,-35.5,0) rot=(0,0,1;1.0472rad)
  Radius = 1.5
FEATURE [Part::Cylinder] Cylinder974  label="Válec974"
  Angle = 360
  AttacherType = Attacher::AttachEngine3D
  Height = 60
  Placement = pos=(35.5,-61.4878,0) rot=(0,0,1;0.523599rad)
  Radius = 1.5
FEATURE [Part::Cylinder] Cylinder977  label="Válec977"
  Angle = 360
  AttacherType = Attacher::AttachEngine3D
  Height = 60
  Placement = pos=(61.4878,35.5,0) rot=(0,0,1;2.0944rad)
  Radius = 1.5
FEATURE [Part::Cylinder] Cylinder978  label="Válec978"
  Angle = 360
  AttacherType = Attacher::AttachEngine3D
  Height = 60
  Placement = pos=(35.5,61.4878,0) rot=(0,0,1;2.61799rad)
  Radius = 1.5
FEATURE [Part::Cylinder] Cylinder982  label="Válec982"
  Angle = 360
  AttacherType = Attacher::AttachEngine3D
  Height = 60
  Placement = pos=(-71,2.7e-14,0) rot=(0,0,-1;1.5708rad)
  Radius = 1.5
FEATURE [Part::Cylinder] Cylinder980  label="Válec980"
  Angle = 360
  AttacherType = Attacher::AttachEngine3D
  Height = 60
  Placement = pos=(-35.5,61.4878,0) rot=(0,0,1;3.66519rad)
  Radius = 1.5
FEATURE [Part::Cylinder] Cylinder984  label="Válec984"
  Angle = 360
  AttacherType = Attacher::AttachEngine3D
  Height = 60
  Placement = pos=(-35.5,-61.4878,0) rot=(0,0,-1;0.523599rad)
  Radius = 1.5
FEATURE [Part::Cylinder] Cylinder983  label="Válec983"
  Angle = 360
  AttacherType = Attacher::AttachEngine3D
  Height = 60
  Placement = pos=(-61.4878,-35.5,0) rot=(0,0,-1;1.0472rad)
  Radius = 1.5
FEATURE [Part::Cylinder] Cylinder981  label="Válec981"
  Angle = 360
  AttacherType = Attacher::AttachEngine3D
  Height = 60
  Placement = pos=(-61.4878,35.5,0) rot=(0,0,1;4.18879rad)
  Radius = 1.5
FEATURE [Part::Compound] Compound525
  Links = -> [Cylinder973,Cylinder974,Cylinder975,Cylinder976,Cylinder977,Cylinder978,Cylinder980,Cylinder981,Cylinder982,Cylinder983,Cylinder984]
FEATURE [Part::Cut] Cut204  label="bazovina_part-E_lozo-okruh-novo"
  Base = -> Cut203
  Placement = pos=(0,0,0) rot=(0,0,1;1.5708rad)
  Tool = -> Compound525
FEATURE [Sketcher::SketchObject] Sketch001
  FullyConstrained = false
  MapMode = 5
  Support = -> [XY_Plane001]
  sketch-geometry (5):
    g0: LineSegment StartX=-51.8839 StartY=28.0157 StartZ=0 EndX=-8.82571 EndY=110.528 EndZ=0
    g1: LineSegment StartX=-8.82571 StartY=110.528 StartZ=0 EndX=8.88346 EndY=110.528 EndZ=0
    g2: LineSegment StartX=8.88346 StartY=110.528 StartZ=0 EndX=51.7746 EndY=28.1985 EndZ=0
    g3: LineSegment StartX=51.7746 StartY=28.1985 StartZ=0 EndX=0 EndY=55.1408 EndZ=0
    g4: LineSegment StartX=0 StartY=55.1408 StartZ=0 EndX=-51.8839 EndY=28.0157 EndZ=0
  constraints (7):
    c: Coincident(g0,g1)
    c: Horizontal(g1)
    c: Coincident(g1,g2)
    c: Coincident(g2,g3)
    c: PointOnObject(g3,g-2)
    c: Coincident(g3,g4)
    c: Coincident(g4,g0)
FEATURE [PartDesign::Pad] Pad001
  Direction = (1,1,1)
  Length = 10
  Length2 = 100
  Profile = -> Sketch001
  Type = 0
FEATURE [PartDesign::Body] Body001
  Group = -> [Sketch001,Pad001]
  Origin = -> Origin001
  Tip = -> Pad001
FEATURE [Part::Cylinder] Cylinder985  label="Válec985"
  Angle = 360
  AttacherType = Attacher::AttachEngine3D
  Height = 4
  Placement = pos=(-34,36,-1) rot=(0,0,1;0rad)
  Radius = 3
FEATURE [Part::Box] Box210  label="Krychle210"
  AttacherType = Attacher::AttachEngine3D
  Height = 10
  Length = 10
  Placement = pos=(-42,-24,0) rot=(0,0,1;0rad)
  Width = 52
FEATURE [Part::Cylinder] Cylinder986  label="Válec986"
  Angle = 360
  AttacherType = Attacher::AttachEngine3D
  Height = 4
  Placement = pos=(34,36,-1) rot=(0,0,1;0rad)
  Radius = 3
FEATURE [Part::Compound] Compound530
  Links = -> [Cylinder986,Cylinder985]
FEATURE [Part::Box] Box211  label="Krychle211"
  AttacherType = Attacher::AttachEngine3D
  Height = 32
  Length = 200
  Placement = pos=(-100,-124,0) rot=(0,0,1;0rad)
  Width = 100
FEATURE [Part::Cylinder] Cylinder987  label="Válec987"
  Angle = 360
  AttacherType = Attacher::AttachEngine3D
  Height = 10
  Placement = pos=(0,106,0) rot=(0,0,1;0rad)
  Radius = 10
FEATURE [Part::Box] Box212  label="Krychle212"
  AttacherType = Attacher::AttachEngine3D
  Height = 10
  Length = 10
  Placement = pos=(32,-24,0) rot=(0,0,1;0rad)
  Width = 52
FEATURE [Part::Cylinder] Cylinder988  label="Válec988"
  Angle = 360
  AttacherType = Attacher::AttachEngine3D
  Height = 100
  Placement = pos=(51,-12,0) rot=(0,0,1;0rad)
  Radius = 1.5
FEATURE [Part::Compound] Compound539
  Links = -> [Box212,Box210]
FEATURE [Part::FeaturePython] Tube027  # WARN: FeaturePython — macro-defined, semantics opaque (R4)
  AttacherType = Attacher::AttachEngine3D
  Height = 10
  InnerRadius = 40
  OuterRadius = 59
FEATURE [Part::Cut] Cut211
  Base = -> Tube027
  Tool = -> Compound530
FEATURE [Part::Cylinder] Cylinder989  label="Válec989"
  Angle = 360
  AttacherType = Attacher::AttachEngine3D
  Height = 50
  Placement = pos=(51,6,0) rot=(0,0,1;0rad)
  Radius = 1.5
FEATURE [Part::Cylinder] Cylinder990  label="Válec990"
  Angle = 360
  AttacherType = Attacher::AttachEngine3D
  Height = 50
  Placement = pos=(-34,36,0) rot=(0,0,1;0rad)
  Radius = 1.5
FEATURE [Part::Cylinder] Cylinder991  label="Válec991"
  Angle = 360
  AttacherType = Attacher::AttachEngine3D
  Height = 50
  Placement = pos=(-51,6,0) rot=(0,0,1;0rad)
  Radius = 1.5
FEATURE [Part::Cylinder] Cylinder992  label="Válec992"
  Angle = 360
  AttacherType = Attacher::AttachEngine3D
  Height = 4
  Placement = pos=(-24,18,0) rot=(0,0,1;0rad)
  Radius = 3
FEATURE [Part::Cylinder] Cylinder993  label="Válec993"
  Angle = 360
  AttacherType = Attacher::AttachEngine3D
  Height = 50
  Placement = pos=(51,6,0) rot=(0,0,1;0rad)
  Radius = 1.5
FEATURE [Part::Cylinder] Cylinder994  label="Válec994"
  Angle = 360
  AttacherType = Attacher::AttachEngine3D
  Height = 50
  Placement = pos=(34,36,0) rot=(0,0,1;0rad)
  Radius = 1.5
FEATURE [Part::Compound] Compound526
  Links = -> [Cylinder990,Cylinder994]
FEATURE [Part::Cut] Cut215
  Base = -> Cut211
  Tool = -> Compound526
FEATURE [Part::Cylinder] Cylinder995  label="Válec995"
  Angle = 360
  AttacherType = Attacher::AttachEngine3D
  Height = 4
  Placement = pos=(-51,7,0) rot=(0,0,1;0rad)
  Radius = 3
FEATURE [Part::Cylinder] Cylinder996  label="Válec996"
  Angle = 360
  AttacherType = Attacher::AttachEngine3D
  Height = 50
  Placement = pos=(-24,18,0) rot=(0,0,1;0rad)
  Radius = 1.5
FEATURE [Part::Cylinder] Cylinder997  label="Válec997"
  Angle = 360
  AttacherType = Attacher::AttachEngine3D
  Height = 4
  Placement = pos=(51,-16,0) rot=(0,0,1;0rad)
  Radius = 3
FEATURE [Part::Cylinder] Cylinder998  label="Válec998"
  Angle = 360
  AttacherType = Attacher::AttachEngine3D
  Height = 50
  Placement = pos=(-51,6,0) rot=(0,0,1;0rad)
  Radius = 1.5
FEATURE [Part::Box] Box213  label="Krychle213"
  AttacherType = Attacher::AttachEngine3D
  Height = 10
  Length = 72
  Placement = pos=(-36,10,0) rot=(0,0,1;0rad)
  Width = 34
FEATURE [Part::Cylinder] Cylinder999  label="Válec999"
  Angle = 360
  AttacherType = Attacher::AttachEngine3D
  Height = 4
  Placement = pos=(51,7,0) rot=(0,0,1;0rad)
  Radius = 3
FEATURE [Part::Cylinder] Cylinder1000  label="Válec1000"
  Angle = 360
  AttacherType = Attacher::AttachEngine3D
  Height = 4
  Placement = pos=(24,18,0) rot=(0,0,1;0rad)
  Radius = 3
FEATURE [Part::Cylinder] Cylinder1001  label="Válec1001"
  Angle = 360
  AttacherType = Attacher::AttachEngine3D
  Height = 100
  Placement = pos=(-51,-12,0) rot=(0,0,1;0rad)
  Radius = 1.5
FEATURE [Part::Compound] Compound528
  Links = -> [Cylinder1001,Cylinder988]
FEATURE [Part::Cylinder] Cylinder1002  label="Válec1002"
  Angle = 360
  AttacherType = Attacher::AttachEngine3D
  Height = 4
  Placement = pos=(-24,18,0) rot=(0,0,1;0rad)
  Radius = 3
FEATURE [Part::Compound] Compound531
  Links = -> [Cylinder999,Cylinder995,Cylinder1002,Cylinder1000]
  Placement = pos=(0,0,8) rot=(0,0,1;0rad)
FEATURE [Part::Cylinder] Cylinder1003  label="Válec1003"
  Angle = 360
  AttacherType = Attacher::AttachEngine3D
  Height = 4
  Placement = pos=(-51,-16,0) rot=(0,0,1;0rad)
  Radius = 3
FEATURE [Part::Compound] Compound529
  Links = -> [Cylinder1003,Cylinder997]
  Placement = pos=(0,0,25) rot=(0,0,1;0rad)
FEATURE [Part::Cylinder] Cylinder1004  label="Válec1004"
  Angle = 360
  AttacherType = Attacher::AttachEngine3D
  Height = 4
  Placement = pos=(0,50,-1) rot=(0,0,1;0rad)
  Radius = 3
FEATURE [Part::Cylinder] Cylinder1005  label="Válec1005"
  Angle = 360
  AttacherType = Attacher::AttachEngine3D
  Height = 4
  Placement = pos=(34,36,-1) rot=(0,0,1;0rad)
  Radius = 3
FEATURE [Part::Cylinder] Cylinder1006  label="Válec1006"
  Angle = 360
  AttacherType = Attacher::AttachEngine3D
  Height = 4
  Placement = pos=(-34,36,-1) rot=(0,0,1;0rad)
  Radius = 3
FEATURE [Part::Compound] Compound543
  Links = -> [Cylinder1006,Cylinder1005]
FEATURE [Part::Cut] Cut210
  Base = -> Box213
  Tool = -> Compound543
FEATURE [Part::Cylinder] Cylinder1007  label="Válec1007"
  Angle = 360
  AttacherType = Attacher::AttachEngine3D
  Height = 4
  Placement = pos=(24,18,0) rot=(0,0,1;0rad)
  Radius = 3
FEATURE [Part::Compound] Compound534
  Links = -> [Cylinder992,Cylinder1007]
  Placement = pos=(0,0,7) rot=(0,0,1;0rad)
FEATURE [Part::Cylinder] Cylinder1008  label="Válec1008"
  Angle = 360
  AttacherType = Attacher::AttachEngine3D
  Height = 50
  Placement = pos=(-34,36,0) rot=(0,0,1;0rad)
  Radius = 1.5
FEATURE [Part::Cylinder] Cylinder1009  label="Válec1009"
  Angle = 360
  AttacherType = Attacher::AttachEngine3D
  Height = 50
  Placement = pos=(34,36,0) rot=(0,0,1;0rad)
  Radius = 1.5
FEATURE [Part::Compound] Compound542
  Links = -> [Cylinder1008,Cylinder1009]
FEATURE [Part::Cut] Cut213
  Base = -> Cut210
  Tool = -> Compound542
FEATURE [Part::Cut] Cut212
  Base = -> Cut213
  Tool = -> Compound531
FEATURE [Part::Cylinder] Cylinder1010  label="Válec1010"
  Angle = 360
  AttacherType = Attacher::AttachEngine3D
  Height = 4
  Placement = pos=(-7,-34,73) rot=(1,0,0;1.5708rad)
  Radius = 3
FEATURE [Part::Cylinder] Cylinder1011  label="Válec1011"
  Angle = 360
  AttacherType = Attacher::AttachEngine3D
  Height = 20
  Placement = pos=(7,-34,37) rot=(1,0,0;1.5708rad)
  Radius = 1.5
FEATURE [Part::Cylinder] Cylinder1012  label="Válec1012"
  Angle = 360
  AttacherType = Attacher::AttachEngine3D
  Height = 20
  Placement = pos=(-7,-34,37) rot=(1,0,0;1.5708rad)
  Radius = 1.5
FEATURE [Part::Cylinder] Cylinder1013  label="Válec1013"
  Angle = 360
  AttacherType = Attacher::AttachEngine3D
  Height = 20
  Placement = pos=(-7,-34,73) rot=(1,0,0;1.5708rad)
  Radius = 1.5
FEATURE [Part::Cylinder] Cylinder1014  label="Válec1014"
  Angle = 360
  AttacherType = Attacher::AttachEngine3D
  Height = 4
  Placement = pos=(-7,-34,37) rot=(1,0,0;1.5708rad)
  Radius = 3
FEATURE [Part::Cylinder] Cylinder1015  label="Válec1015"
  Angle = 360
  AttacherType = Attacher::AttachEngine3D
  Height = 20
  Placement = pos=(7,-34,73) rot=(1,0,0;1.5708rad)
  Radius = 1.5
FEATURE [Part::Compound] Compound544
  Links = -> [Cylinder1011,Cylinder1012,Cylinder1015,Cylinder1013]
  Placement = pos=(0,141,45) rot=(1,0,0;1.5708rad)
FEATURE [Part::Cylinder] Cylinder1016  label="Válec1016"
  Angle = 360
  AttacherType = Attacher::AttachEngine3D
  Height = 50
  Placement = pos=(24,18,0) rot=(0,0,1;0rad)
  Radius = 1.5
FEATURE [Part::Cylinder] Cylinder1017  label="Válec1017"
  Angle = 360
  AttacherType = Attacher::AttachEngine3D
  Height = 50
  Placement = pos=(-24,18,0) rot=(0,0,1;0rad)
  Radius = 1.5
FEATURE [Part::Compound] Compound532
  Links = -> [Cylinder993,Cylinder998,Cylinder1017,Cylinder1016]
FEATURE [Part::Cut] Cut217
  Base = -> Cut212
  Tool = -> Compound532
FEATURE [Part::Cylinder] Cylinder1018  label="Válec1018"
  Angle = 360
  AttacherType = Attacher::AttachEngine3D
  Height = 50
  Placement = pos=(0,50,0) rot=(0,0,1;0rad)
  Radius = 1.5
FEATURE [Part::Cylinder] Cylinder1019  label="Válec1019"
  Angle = 360
  AttacherType = Attacher::AttachEngine3D
  Height = 50
  Placement = pos=(24,18,0) rot=(0,0,1;0rad)
  Radius = 1.5
FEATURE [Part::Compound] Compound527
  Links = -> [Cylinder989,Cylinder991,Cylinder996,Cylinder1019]
FEATURE [Part::Cut] Cut224
  Base = -> Cut215
  Tool = -> Compound529
FEATURE [Part::Cut] Cut225
  Base = -> Cylinder987
  Tool = -> Compound544
FEATURE [Part::Cut] Cut227
  Base = -> Cut224
  Tool = -> Compound528
FEATURE [Part::Cut] Cut218
  Base = -> Cut227
  Tool = -> Compound534
FEATURE [Part::Cut] Cut214
  Base = -> Cut218
  Tool = -> Compound527
FEATURE [Part::Cut] Cut209
  Base = -> Cut214
  Tool = -> Box211
FEATURE [Part::Cut] Cut208
  Base = -> Cut209
  Tool = -> Cylinder1004
FEATURE [Part::Cut] Cut216
  Base = -> Cut208
  Tool = -> Cylinder1018
FEATURE [Part::Cylinder] Cylinder1020  label="Válec1020"
  Angle = 360
  AttacherType = Attacher::AttachEngine3D
  Height = 4
  Placement = pos=(-7,-34,37) rot=(1,0,0;1.5708rad)
  Radius = 3
FEATURE [Part::Cylinder] Cylinder1021  label="Válec1021"
  Angle = 360
  AttacherType = Attacher::AttachEngine3D
  Height = 20
  Placement = pos=(7,-34,37) rot=(1,0,0;1.5708rad)
  Radius = 1.5
FEATURE [Part::Cylinder] Cylinder1022  label="Válec1022"
  Angle = 360
  AttacherType = Attacher::AttachEngine3D
  Height = 50
  Placement = pos=(34,36,0) rot=(0,0,1;0rad)
  Radius = 1.5
FEATURE [Part::Cylinder] Cylinder1023  label="Válec1023"
  Angle = 360
  AttacherType = Attacher::AttachEngine3D
  Height = 20
  Placement = pos=(-7,-34,73) rot=(1,0,0;1.5708rad)
  Radius = 1.5
FEATURE [Part::Cylinder] Cylinder1024  label="Válec1024"
  Angle = 360
  AttacherType = Attacher::AttachEngine3D
  Height = 4
  Placement = pos=(7,-34,73) rot=(1,0,0;1.5708rad)
  Radius = 3
FEATURE [Part::Cylinder] Cylinder1025  label="Válec1025"
  Angle = 360
  AttacherType = Attacher::AttachEngine3D
  Height = 20
  Placement = pos=(-7,-34,37) rot=(1,0,0;1.5708rad)
  Radius = 1.5
FEATURE [Part::Cylinder] Cylinder1026  label="Válec1026"
  Angle = 360
  AttacherType = Attacher::AttachEngine3D
  Height = 4
  Placement = pos=(7,-34,73) rot=(1,0,0;1.5708rad)
  Radius = 3
FEATURE [Part::Cylinder] Cylinder1027  label="Válec1027"
  Angle = 360
  AttacherType = Attacher::AttachEngine3D
  Height = 100
  Placement = pos=(39,-21,0) rot=(0,0,1;0rad)
  Radius = 1.5
FEATURE [Part::Cylinder] Cylinder1028  label="Válec1028"
  Angle = 360
  AttacherType = Attacher::AttachEngine3D
  Height = 100
  Placement = pos=(-39,-21,0) rot=(0,0,1;0rad)
  Radius = 1.5
FEATURE [Part::Compound] Compound535
  Links = -> [Cylinder1028,Cylinder1027]
FEATURE [Part::Cut] Cut226
  Base = -> Cut216
  Tool = -> Compound535
FEATURE [Part::Cylinder] Cylinder1029  label="Válec1029"
  Angle = 360
  AttacherType = Attacher::AttachEngine3D
  Height = 50
  Placement = pos=(-34,36,0) rot=(0,0,1;0rad)
  Radius = 1.5
FEATURE [Part::Compound] Compound533
  Links = -> [Cylinder1029,Cylinder1022]
FEATURE [Part::Cylinder] Cylinder1030  label="Válec1030"
  Angle = 360
  AttacherType = Attacher::AttachEngine3D
  Height = 4
  Placement = pos=(7,-34,37) rot=(1,0,0;1.5708rad)
  Radius = 3
FEATURE [Part::Compound] Compound545
  Links = -> [Cylinder1030,Cylinder1014,Cylinder1026,Cylinder1010]
  Placement = pos=(0,141,45) rot=(1,0,0;1.5708rad)
FEATURE [Part::Cut] Cut222
  Base = -> Cut225
  Tool = -> Compound545
FEATURE [Part::Cylinder] Cylinder1031  label="Válec1031"
  Angle = 360
  AttacherType = Attacher::AttachEngine3D
  Height = 4
  Placement = pos=(-34,36,-1) rot=(0,0,1;0rad)
  Radius = 3
FEATURE [Part::Cylinder] Cylinder1032  label="Válec1032"
  Angle = 360
  AttacherType = Attacher::AttachEngine3D
  Height = 4
  Placement = pos=(34,36,-1) rot=(0,0,1;0rad)
  Radius = 3
FEATURE [Part::Compound] Compound538
  Links = -> [Cylinder1032,Cylinder1031]
FEATURE [Part::Cut] Cut221
  Base = -> Body001
  Tool = -> Compound538
FEATURE [Part::Cut] Cut223
  Base = -> Cut221
  Tool = -> Compound533
FEATURE [Part::Cylinder] Cylinder1033  label="Válec1033"
  Angle = 360
  AttacherType = Attacher::AttachEngine3D
  Height = 4
  Placement = pos=(7,-34,37) rot=(1,0,0;1.5708rad)
  Radius = 3
FEATURE [Part::Cylinder] Cylinder1034  label="Válec1034"
  Angle = 360
  AttacherType = Attacher::AttachEngine3D
  Height = 20
  Placement = pos=(7,-34,73) rot=(1,0,0;1.5708rad)
  Radius = 1.5
FEATURE [Part::Compound] Compound540
  Links = -> [Cylinder1021,Cylinder1025,Cylinder1034,Cylinder1023]
  Placement = pos=(0,141,45) rot=(1,0,0;1.5708rad)
FEATURE [Part::Cut] Cut228
  Base = -> Cut223
  Tool = -> Compound540
FEATURE [Part::Cylinder] Cylinder1035  label="Válec1035"
  Angle = 360
  AttacherType = Attacher::AttachEngine3D
  Height = 4
  Placement = pos=(-7,-34,73) rot=(1,0,0;1.5708rad)
  Radius = 3
FEATURE [Part::Compound] Compound537
  Links = -> [Cylinder1033,Cylinder1020,Cylinder1024,Cylinder1035]
  Placement = pos=(0,141,45) rot=(1,0,0;1.5708rad)
FEATURE [Part::Cut] Cut220
  Base = -> Cut228
  Tool = -> Compound537
FEATURE [Part::Cylinder] Cylinder1036  label="Válec1036"
  Angle = 360
  AttacherType = Attacher::AttachEngine3D
  Height = 100
  Placement = pos=(-39,-21,0) rot=(0,0,1;0rad)
  Radius = 1.5
FEATURE [Part::Cylinder] Cylinder1037  label="Válec1037"
  Angle = 360
  AttacherType = Attacher::AttachEngine3D
  Height = 100
  Placement = pos=(39,-21,0) rot=(0,0,1;0rad)
  Radius = 1.5
FEATURE [Part::Compound] Compound536
  Links = -> [Cylinder1036,Cylinder1037]
FEATURE [Part::Cut] Cut219
  Base = -> Compound539
  Tool = -> Compound536
FEATURE [Part::Compound] Compound541  label="bazovina_part-A_trojuhelnikovina"
  Links = -> [Cut217,Cut222,Cut220,Cut219,Cut226]
  Placement = pos=(52,0,-36) rot=(0,0,1;0rad)
FEATURE [Part::FeaturePython] Tube028  # WARN: FeaturePython — macro-defined, semantics opaque (R4)
  AttacherType = Attacher::AttachEngine3D
  Height = 6
  InnerRadius = 40
  OuterRadius = 59
  Placement = pos=(0,0,12) rot=(0,0,1;0rad)
FEATURE [Part::Cylinder] Cylinder1038  label="Válec1038"
  Angle = 360
  AttacherType = Attacher::AttachEngine3D
  Height = 100
  Placement = pos=(51,-12,0) rot=(0,0,1;0rad)
  Radius = 1.5
FEATURE [Part::Cylinder] Cylinder1039  label="Válec1039"
  Angle = 360
  AttacherType = Attacher::AttachEngine3D
  Height = 50
  Placement = pos=(0,50,0) rot=(0,0,1;0rad)
  Radius = 1.5
FEATURE [Part::Cylinder] Cylinder1040  label="Válec1040"
  Angle = 360
  AttacherType = Attacher::AttachEngine3D
  Height = 50
  Placement = pos=(-34,36,0) rot=(0,0,1;0rad)
  Radius = 1.5
FEATURE [Part::Cylinder] Cylinder1041  label="Válec1041"
  Angle = 360
  AttacherType = Attacher::AttachEngine3D
  Height = 50
  Placement = pos=(-34,36,0) rot=(0,0,1;0rad)
  Radius = 1.5
FEATURE [Part::Cylinder] Cylinder1042  label="Válec1042"
  Angle = 360
  AttacherType = Attacher::AttachEngine3D
  Height = 4
  Placement = pos=(51,-12,0) rot=(0,0,1;0rad)
  Radius = 3
FEATURE [Part::Cylinder] Cylinder1043  label="Válec1043"
  Angle = 360
  AttacherType = Attacher::AttachEngine3D
  Height = 4
  Placement = pos=(51,6,17) rot=(0,0,1;0rad)
  Radius = 3
FEATURE [Part::Cylinder] Cylinder1044  label="Válec1044"
  Angle = 360
  AttacherType = Attacher::AttachEngine3D
  Height = 50
  Placement = pos=(34,36,0) rot=(0,0,1;0rad)
  Radius = 1.5
FEATURE [Part::Cylinder] Cylinder1045  label="Válec1045"
  Angle = 360
  AttacherType = Attacher::AttachEngine3D
  Height = 100
  Placement = pos=(51,-12,0) rot=(0,0,1;0rad)
  Radius = 1.5
FEATURE [Part::Cylinder] Cylinder1046  label="Válec1046"
  Angle = 360
  AttacherType = Attacher::AttachEngine3D
  Height = 100
  Placement = pos=(-51,-12,0) rot=(0,0,1;0rad)
  Radius = 1.5
FEATURE [Part::Cylinder] Cylinder1047  label="Válec1047"
  Angle = 360
  AttacherType = Attacher::AttachEngine3D
  Height = 50
  Placement = pos=(51,6,0) rot=(0,0,1;0rad)
  Radius = 1.5
FEATURE [Part::Cylinder] Cylinder1048  label="Válec1048"
  Angle = 360
  AttacherType = Attacher::AttachEngine3D
  Height = 50
  Placement = pos=(-51,6,0) rot=(0,0,1;0rad)
  Radius = 1.5
FEATURE [Part::Cylinder] Cylinder1049  label="Válec1049"
  Angle = 360
  AttacherType = Attacher::AttachEngine3D
  Height = 50
  Placement = pos=(51,6,0) rot=(0,0,1;0rad)
  Radius = 1.5
FEATURE [Part::Cylinder] Cylinder1050  label="Válec1050"
  Angle = 360
  AttacherType = Attacher::AttachEngine3D
  Height = 100
  Placement = pos=(-51,-12,0) rot=(0,0,1;0rad)
  Radius = 1.5
FEATURE [Part::Cylinder] Cylinder1051  label="Válec1051"
  Angle = 360
  AttacherType = Attacher::AttachEngine3D
  Height = 4
  Placement = pos=(34,-36,0) rot=(0,0,1;0rad)
  Radius = 3
FEATURE [Part::Cylinder] Cylinder1052  label="Válec1052"
  Angle = 360
  AttacherType = Attacher::AttachEngine3D
  Height = 4
  Placement = pos=(-51,6,17) rot=(0,0,1;0rad)
  Radius = 3
FEATURE [Part::Compound] Compound551
  Links = -> [Cylinder1043,Cylinder1052]
  Placement = pos=(0,0,-2) rot=(0,0,1;0rad)
FEATURE [Part::Cylinder] Cylinder1053  label="Válec1053"
  Angle = 360
  AttacherType = Attacher::AttachEngine3D
  Height = 50
  Placement = pos=(34,36,0) rot=(0,0,1;0rad)
  Radius = 1.5
FEATURE [Part::Compound] Compound556
  Links = -> [Cylinder1046,Cylinder1041,Cylinder1053,Cylinder1049,Cylinder1048,Cylinder1045]
FEATURE [Part::Cylinder] Cylinder1054  label="Válec1054"
  Angle = 360
  AttacherType = Attacher::AttachEngine3D
  Height = 50
  Placement = pos=(-34,-36,0) rot=(0,0,1;0rad)
  Radius = 1.5
FEATURE [Part::Cylinder] Cylinder1055  label="Válec1055"
  Angle = 360
  AttacherType = Attacher::AttachEngine3D
  Height = 50
  Placement = pos=(-51,6,0) rot=(0,0,1;0rad)
  Radius = 1.5
FEATURE [Part::Cylinder] Cylinder1056  label="Válec1056"
  Angle = 360
  AttacherType = Attacher::AttachEngine3D
  Height = 4
  Placement = pos=(34,-36,0) rot=(0,0,1;0rad)
  Radius = 3
FEATURE [Part::Cylinder] Cylinder1057  label="Válec1057"
  Angle = 360
  AttacherType = Attacher::AttachEngine3D
  Height = 4
  Placement = pos=(-34,-36,0) rot=(0,0,1;0rad)
  Radius = 3
FEATURE [Part::Compound] Compound553
  Links = -> [Cylinder1056,Cylinder1057]
  Placement = pos=(0,0,9) rot=(0,0,1;0rad)
FEATURE [Part::Cylinder] Cylinder1058  label="Válec1058"
  Angle = 360
  AttacherType = Attacher::AttachEngine3D
  Height = 4
  Placement = pos=(-24,18,0) rot=(0,0,1;0rad)
  Radius = 3
FEATURE [Part::Cylinder] Cylinder1059  label="Válec1059"
  Angle = 360
  AttacherType = Attacher::AttachEngine3D
  Height = 4
  Placement = pos=(-34,-36,0) rot=(0,0,1;0rad)
  Radius = 3
FEATURE [Part::Compound] Compound557
  Links = -> [Cylinder1051,Cylinder1059]
  Placement = pos=(0,0,9) rot=(0,0,1;0rad)
FEATURE [Part::Cylinder] Cylinder1060  label="Válec1060"
  Angle = 360
  AttacherType = Attacher::AttachEngine3D
  Height = 4
  Placement = pos=(-51,-12,0) rot=(0,0,1;0rad)
  Radius = 3
FEATURE [Part::Compound] Compound546
  Links = -> [Cylinder1060,Cylinder1042]
  Placement = pos=(0,0,15) rot=(0,0,1;0rad)
FEATURE [Part::Cylinder] Cylinder1061  label="Válec1061"
  Angle = 360
  AttacherType = Attacher::AttachEngine3D
  Height = 4
  Placement = pos=(24,18,0) rot=(0,0,1;0rad)
  Radius = 3
FEATURE [Part::Compound] Compound552
  Links = -> [Cylinder1058,Cylinder1061]
  Placement = pos=(0,0,10) rot=(0,0,1;0rad)
FEATURE [Part::Cylinder] Cylinder1062  label="Válec1062"
  Angle = 360
  AttacherType = Attacher::AttachEngine3D
  Height = 100
  Placement = pos=(39,-21,0) rot=(0,0,1;0rad)
  Radius = 1.5
FEATURE [Part::Cylinder] Cylinder1063  label="Válec1063"
  Angle = 360
  AttacherType = Attacher::AttachEngine3D
  Height = 50
  Placement = pos=(34,-36,0) rot=(0,0,1;0rad)
  Radius = 1.5
FEATURE [Part::Compound] Compound550
  Links = -> [Cylinder1063,Cylinder1054]
FEATURE [Part::Cylinder] Cylinder1064  label="Válec1064"
  Angle = 360
  AttacherType = Attacher::AttachEngine3D
  Height = 50
  Placement = pos=(34,36,0) rot=(0,0,1;0rad)
  Radius = 1.5
FEATURE [Part::Compound] Compound555
  Links = -> [Cylinder1050,Cylinder1040,Cylinder1064,Cylinder1047,Cylinder1055,Cylinder1038]
FEATURE [Part::Cylinder] Cylinder1065  label="Válec1065"
  Angle = 360
  AttacherType = Attacher::AttachEngine3D
  Height = 50
  Placement = pos=(0,50,0) rot=(0,0,1;0rad)
  Radius = 1.5
FEATURE [Part::Cylinder] Cylinder1066  label="Válec1066"
  Angle = 360
  AttacherType = Attacher::AttachEngine3D
  Height = 4
  Placement = pos=(0,-50,9) rot=(0,0,1;0rad)
  Radius = 3
FEATURE [Part::Cylinder] Cylinder1067  label="Válec1067"
  Angle = 360
  AttacherType = Attacher::AttachEngine3D
  Height = 50
  Placement = pos=(0,-50,0) rot=(0,0,1;0rad)
  Radius = 1.5
FEATURE [Part::Cylinder] Cylinder1068  label="Válec1068"
  Angle = 360
  AttacherType = Attacher::AttachEngine3D
  Height = 100
  Placement = pos=(-39,-21,0) rot=(0,0,1;0rad)
  Radius = 1.5
FEATURE [Part::Compound] Compound549
  Links = -> [Cylinder1068,Cylinder1062]
FEATURE [Part::Cylinder] Cylinder1069  label="Válec1069"
  Angle = 360
  AttacherType = Attacher::AttachEngine3D
  Height = 4
  Placement = pos=(0,-50,9) rot=(0,0,1;0rad)
  Radius = 3
FEATURE [Part::Cylinder] Cylinder1070  label="Válec1070"
  Angle = 360
  AttacherType = Attacher::AttachEngine3D
  Height = 100
  Placement = pos=(39,-21,0) rot=(0,0,1;0rad)
  Radius = 1.5
FEATURE [Part::Cylinder] Cylinder1071  label="Válec1071"
  Angle = 360
  AttacherType = Attacher::AttachEngine3D
  Height = 100
  Placement = pos=(-39,-21,0) rot=(0,0,1;0rad)
  Radius = 1.5
FEATURE [Part::Compound] Compound548
  Links = -> [Cylinder1071,Cylinder1070]
FEATURE [Part::Cylinder] Cylinder1072  label="Válec1072"
  Angle = 360
  AttacherType = Attacher::AttachEngine3D
  Height = 50
  Placement = pos=(-34,36,0) rot=(0,0,1;0rad)
  Radius = 1.5
FEATURE [Part::Compound] Compound547
  Links = -> [Cylinder1072,Cylinder1044]
FEATURE [Part::Cut] Cut243
  Base = -> Tube028
  Tool = -> Compound547
FEATURE [Part::Cut] Cut240
  Base = -> Cut243
  Tool = -> Compound556
FEATURE [Part::Cut] Cut237
  Base = -> Cut240
  Tool = -> Compound546
FEATURE [Part::Cut] Cut238
  Base = -> Cut237
  Tool = -> Compound551
FEATURE [Part::Cut] Cut231
  Base = -> Cut238
  Tool = -> Compound557
FEATURE [Part::Cut] Cut234
  Base = -> Cut231
  Tool = -> Compound550
FEATURE [Part::Cut] Cut235
  Base = -> Cut234
  Tool = -> Cylinder1065
FEATURE [Part::Cut] Cut230
  Base = -> Cut235
  Tool = -> Cylinder1066
FEATURE [Part::Cut] Cut244
  Base = -> Cut230
  Tool = -> Cylinder1067
FEATURE [Part::Cut] Cut239
  Base = -> Cut244
  Tool = -> Compound548
FEATURE [Part::Cylinder] Cylinder1073  label="Válec1073"
  Angle = 360
  AttacherType = Attacher::AttachEngine3D
  Height = 2
  Placement = pos=(0,0,10) rot=(0,0,1;0rad)
  Radius = 59
FEATURE [Part::Cut] Cut236
  Base = -> Cylinder1073
  Tool = -> Compound555
FEATURE [Part::Cut] Cut232
  Base = -> Cut236
  Tool = -> Compound552
FEATURE [Part::Cut] Cut229
  Base = -> Cut232
  Tool = -> Compound553
FEATURE [Part::Cut] Cut242
  Base = -> Cut229
  Tool = -> Cylinder1039
FEATURE [Part::Cut] Cut233
  Base = -> Cut242
  Tool = -> Cylinder1069
FEATURE [Part::Cut] Cut241
  Base = -> Cut233
  Tool = -> Compound549
FEATURE [Part::Compound] Compound554  label="bazovina_part-B_vicko"
  Links = -> [Cut239,Cut241]
  Placement = pos=(0,0,0) rot=(0,0,-1;1.5708rad)
FEATURE [Sketcher::SketchObject] Sketch002
  FullyConstrained = false
  sketch-geometry (1):
    g0: Circle CenterX=-186.411 CenterY=73.9277 CenterZ=0 NormalX=0 NormalY=0 NormalZ=1 AngleXU=0 Radius=59
FEATURE [Part::Extrusion] Extrude
  Base = -> Sketch002
  Dir = (52,0,32)
  DirMode = 0
  FaceMakerClass = Part::FaceMakerBullseye
  LengthFwd = 61
  LengthRev = 0
  Placement = pos=(-134,74,-22) rot=(0,0,1;3.14159rad)
  Solid = true
  Symmetric = false
FEATURE [Part::Cylinder] Cylinder1074  label="Válec1074"
  Angle = 360
  AttacherType = Attacher::AttachEngine3D
  Height = 40
  Placement = pos=(90,0,-20) rot=(0,0,1;0rad)
  Radius = 4
FEATURE [Part::Cylinder] Cylinder1075  label="Válec1075"
  Angle = 360
  AttacherType = Attacher::AttachEngine3D
  Height = 80
  Placement = pos=(90,0,-60) rot=(0,0,1;0rad)
  Radius = 1.5
FEATURE [Part::Cut] Cut245
  Base = -> Extrude
  Tool = -> Cylinder1074
FEATURE [Part::Cut] Cut246
  Base = -> Cut245
  Tool = -> Cylinder1075
FEATURE [Sketcher::SketchObject] Sketch003
  FullyConstrained = false
  sketch-geometry (1):
    g0: Circle CenterX=-186.411 CenterY=73.9277 CenterZ=0 NormalX=0 NormalY=0 NormalZ=1 AngleXU=0 Radius=59
FEATURE [Part::Extrusion] Extrude001
  Base = -> Sketch003
  Dir = (52,0,32)
  DirMode = 0
  FaceMakerClass = Part::FaceMakerBullseye
  LengthFwd = 61
  LengthRev = 0
  Placement = pos=(-134,74,-22) rot=(0,0,1;3.14159rad)
  Solid = true
  Symmetric = false
FEATURE [Part::Cylinder] Cylinder1076  label="Válec1076"
  Angle = 360
  AttacherType = Attacher::AttachEngine3D
  Height = 100
  Placement = pos=(103,-12,-60) rot=(0,0,1;0rad)
  Radius = 1.5
FEATURE [Part::Cylinder] Cylinder1077  label="Válec1077"
  Angle = 360
  AttacherType = Attacher::AttachEngine3D
  Height = 100
  Placement = pos=(103,6,-60) rot=(0,0,1;0rad)
  Radius = 1.5
FEATURE [Part::Cylinder] Cylinder1078  label="Válec1078"
  Angle = 360
  AttacherType = Attacher::AttachEngine3D
  Height = 100
  Placement = pos=(76,18,-60) rot=(0,0,1;0rad)
  Radius = 1.5
FEATURE [Part::Cylinder] Cylinder1079  label="Válec1079"
  Angle = 360
  AttacherType = Attacher::AttachEngine3D
  Height = 100
  Placement = pos=(91,-21,-60) rot=(0,0,1;0rad)
  Radius = 1.5
FEATURE [Part::Cylinder] Cylinder1080  label="Válec1080"
  Angle = 360
  AttacherType = Attacher::AttachEngine3D
  Height = 100
  Placement = pos=(13,-21,-60) rot=(0,0,1;0rad)
  Radius = 1.5
FEATURE [Part::Cylinder] Cylinder1081  label="Válec1081"
  Angle = 360
  AttacherType = Attacher::AttachEngine3D
  Height = 100
  Placement = pos=(28,18,-60) rot=(0,0,1;0rad)
  Radius = 1.5
FEATURE [Part::Cylinder] Cylinder1083  label="Válec1083"
  Angle = 360
  AttacherType = Attacher::AttachEngine3D
  Height = 100
  Placement = pos=(1,-12,-60) rot=(0,0,1;0rad)
  Radius = 1.5
FEATURE [Part::Cylinder] Cylinder1084  label="Válec1084"
  Angle = 360
  AttacherType = Attacher::AttachEngine3D
  Height = 100
  Placement = pos=(1,6,-60) rot=(0,0,1;0rad)
  Radius = 1.5
FEATURE [Part::Compound] Compound559  label="srouby_monoblok"
  Links = -> [Cylinder1076,Cylinder1077,Cylinder1078,Cylinder1079,Cylinder1080,Cylinder1081,Cylinder1083,Cylinder1084]
FEATURE [Part::Cylinder] Cylinder1085  label="Válec1085"
  Angle = 360
  AttacherType = Attacher::AttachEngine3D
  Height = 100
  Placement = pos=(-50,0,-60) rot=(0,0,1;0rad)
  Radius = 1.5
FEATURE [Part::Cylinder] Cylinder1086  label="Válec1086"
  Angle = 360
  AttacherType = Attacher::AttachEngine3D
  Height = 100
  Placement = pos=(-36,34,-60) rot=(0,0,1;0rad)
  Radius = 1.5
FEATURE [Part::Cylinder] Cylinder1087  label="Válec1087"
  Angle = 360
  AttacherType = Attacher::AttachEngine3D
  Height = 100
  Placement = pos=(-36,-34,-60) rot=(0,0,1;0rad)
  Radius = 1.5
FEATURE [Part::Cylinder] Cylinder1088  label="Válec1088"
  Angle = 360
  AttacherType = Attacher::AttachEngine3D
  Height = 100
  Placement = pos=(50,0,-60) rot=(0,0,1;0rad)
  Radius = 1.5
FEATURE [Part::Cylinder] Cylinder1089  label="Válec1089"
  Angle = 360
  AttacherType = Attacher::AttachEngine3D
  Height = 100
  Placement = pos=(36,34,-60) rot=(0,0,1;0rad)
  Radius = 1.5
FEATURE [Part::Cylinder] Cylinder1090  label="Válec1090"
  Angle = 360
  AttacherType = Attacher::AttachEngine3D
  Height = 100
  Placement = pos=(36,-34,-60) rot=(0,0,1;0rad)
  Radius = 1.5
FEATURE [Part::Cylinder] Cylinder1091  label="Válec1091"
  Angle = 360
  AttacherType = Attacher::AttachEngine3D
  Height = 16
  Placement = pos=(0,0,2) rot=(0,0,1;0rad)
  Radius = 59
FEATURE [Part::Cylinder] Cylinder1092  label="Válec1092"
  Angle = 360
  AttacherType = Attacher::AttachEngine3D
  Height = 4
  Placement = pos=(52,0,-26) rot=(0,0,1;0rad)
  Radius = 59
FEATURE [Part::Compound] Compound560  label="sbouby_baze"
  Links = -> [Cylinder1085,Cylinder1086,Cylinder1087,Cylinder1088,Cylinder1089,Cylinder1090]
FEATURE [Part::Cylinder] Cylinder1093  label="Válec1093"
  Angle = 360
  AttacherType = Attacher::AttachEngine3D
  Height = 20
  Placement = pos=(103,-12,-20) rot=(0,0,1;0rad)
  Radius = 4
FEATURE [Part::Cylinder] Cylinder1094  label="Válec1094"
  Angle = 360
  AttacherType = Attacher::AttachEngine3D
  Height = 20
  Placement = pos=(103,6,-20) rot=(0,0,1;0rad)
  Radius = 4
FEATURE [Part::Cylinder] Cylinder1095  label="Válec1095"
  Angle = 360
  AttacherType = Attacher::AttachEngine3D
  Height = 20
  Placement = pos=(76,18,-18) rot=(0,0,1;0rad)
  Radius = 4
FEATURE [Part::Cylinder] Cylinder1096  label="Válec1096"
  Angle = 360
  AttacherType = Attacher::AttachEngine3D
  Height = 20
  Placement = pos=(91,-21,-18) rot=(0,0,1;0rad)
  Radius = 4
FEATURE [Part::Cylinder] Cylinder1097  label="Válec1097"
  Angle = 360
  AttacherType = Attacher::AttachEngine3D
  Height = 40
  Placement = pos=(13,-21,-18) rot=(0,0,1;0rad)
  Radius = 4
FEATURE [Part::Cylinder] Cylinder1098  label="Válec1098"
  Angle = 360
  AttacherType = Attacher::AttachEngine3D
  Height = 40
  Placement = pos=(28,18,-18) rot=(0,0,1;0rad)
  Radius = 4
FEATURE [Part::Cylinder] Cylinder1099  label="Válec1099"
  Angle = 360
  AttacherType = Attacher::AttachEngine3D
  Height = 40
  Placement = pos=(1,-12,-18) rot=(0,0,1;0rad)
  Radius = 4
FEATURE [Part::Cylinder] Cylinder1100  label="Válec1100"
  Angle = 360
  AttacherType = Attacher::AttachEngine3D
  Height = 40
  Placement = pos=(1,6,-18) rot=(0,0,1;0rad)
  Radius = 4
FEATURE [Part::Compound] Compound561  label="srouby_monoblok_silne"
  Links = -> [Cylinder1093,Cylinder1094,Cylinder1095,Cylinder1096,Cylinder1097,Cylinder1098,Cylinder1099,Cylinder1100]
FEATURE [Part::Cylinder] Cylinder1101  label="Válec1101"
  Angle = 360
  AttacherType = Attacher::AttachEngine3D
  Height = 100
  Placement = pos=(103,-12,-60) rot=(0,0,1;0rad)
  Radius = 1.5
FEATURE [Part::Cylinder] Cylinder1102  label="Válec1102"
  Angle = 360
  AttacherType = Attacher::AttachEngine3D
  Height = 100
  Placement = pos=(103,6,-60) rot=(0,0,1;0rad)
  Radius = 1.5
FEATURE [Part::Cylinder] Cylinder1103  label="Válec1103"
  Angle = 360
  AttacherType = Attacher::AttachEngine3D
  Height = 100
  Placement = pos=(76,18,-60) rot=(0,0,1;0rad)
  Radius = 1.5
FEATURE [Part::Cylinder] Cylinder1104  label="Válec1104"
  Angle = 360
  AttacherType = Attacher::AttachEngine3D
  Height = 100
  Placement = pos=(91,-21,-60) rot=(0,0,1;0rad)
  Radius = 1.5
FEATURE [Part::Cylinder] Cylinder1105  label="Válec1105"
  Angle = 360
  AttacherType = Attacher::AttachEngine3D
  Height = 100
  Placement = pos=(13,-21,-60) rot=(0,0,1;0rad)
  Radius = 1.5
FEATURE [Part::Cylinder] Cylinder1106  label="Válec1106"
  Angle = 360
  AttacherType = Attacher::AttachEngine3D
  Height = 100
  Placement = pos=(28,18,-60) rot=(0,0,1;0rad)
  Radius = 1.5
FEATURE [Part::Cylinder] Cylinder1107  label="Válec1107"
  Angle = 360
  AttacherType = Attacher::AttachEngine3D
  Height = 100
  Placement = pos=(1,-12,-60) rot=(0,0,1;0rad)
  Radius = 1.5
FEATURE [Part::Cylinder] Cylinder1108  label="Válec1108"
  Angle = 360
  AttacherType = Attacher::AttachEngine3D
  Height = 100
  Placement = pos=(1,6,-60) rot=(0,0,1;0rad)
  Radius = 1.5
FEATURE [Part::Compound] Compound562  label="srouby_monoblok001"
  Links = -> [Cylinder1101,Cylinder1102,Cylinder1103,Cylinder1104,Cylinder1105,Cylinder1106,Cylinder1107,Cylinder1108]
FEATURE [Part::Cylinder] Cylinder1109  label="Válec1109"
  Angle = 360
  AttacherType = Attacher::AttachEngine3D
  Height = 20
  Placement = pos=(103,-12,-20) rot=(0,0,1;0rad)
  Radius = 4
FEATURE [Part::Cylinder] Cylinder1110  label="Válec1110"
  Angle = 360
  AttacherType = Attacher::AttachEngine3D
  Height = 20
  Placement = pos=(103,6,-20) rot=(0,0,1;0rad)
  Radius = 4
FEATURE [Part::Cylinder] Cylinder1111  label="Válec1111"
  Angle = 360
  AttacherType = Attacher::AttachEngine3D
  Height = 20
  Placement = pos=(76,18,-18) rot=(0,0,1;0rad)
  Radius = 4
FEATURE [Part::Cylinder] Cylinder1112  label="Válec1112"
  Angle = 360
  AttacherType = Attacher::AttachEngine3D
  Height = 20
  Placement = pos=(91,-21,-18) rot=(0,0,1;0rad)
  Radius = 4
FEATURE [Part::Cylinder] Cylinder1113  label="Válec1113"
  Angle = 360
  AttacherType = Attacher::AttachEngine3D
  Height = 40
  Placement = pos=(13,-21,-18) rot=(0,0,1;0rad)
  Radius = 4
FEATURE [Part::Cylinder] Cylinder1114  label="Válec1114"
  Angle = 360
  AttacherType = Attacher::AttachEngine3D
  Height = 40
  Placement = pos=(28,18,-18) rot=(0,0,1;0rad)
  Radius = 4
FEATURE [Part::Cylinder] Cylinder1115  label="Válec1115"
  Angle = 360
  AttacherType = Attacher::AttachEngine3D
  Height = 40
  Placement = pos=(1,-12,-18) rot=(0,0,1;0rad)
  Radius = 4
FEATURE [Part::Cylinder] Cylinder1116  label="Válec1116"
  Angle = 360
  AttacherType = Attacher::AttachEngine3D
  Height = 40
  Placement = pos=(1,6,-18) rot=(0,0,1;0rad)
  Radius = 4
FEATURE [Part::Compound] Compound563  label="srouby_monoblok_silne001"
  Links = -> [Cylinder1109,Cylinder1110,Cylinder1111,Cylinder1112,Cylinder1113,Cylinder1114,Cylinder1115,Cylinder1116]
FEATURE [Part::Cut] Cut247
  Base = -> Extrude001
  Tool = -> Compound559
FEATURE [Part::Cut] Cut248
  Base = -> Cut247
  Tool = -> Compound563
FEATURE [Part::Cylinder] Cylinder1117  label="Válec1117"
  Angle = 360
  AttacherType = Attacher::AttachEngine3D
  Height = 20
  Placement = pos=(103,-12,-20) rot=(0,0,1;0rad)
  Radius = 4
FEATURE [Part::Cylinder] Cylinder1118  label="Válec1118"
  Angle = 360
  AttacherType = Attacher::AttachEngine3D
  Height = 20
  Placement = pos=(103,6,-20) rot=(0,0,1;0rad)
  Radius = 4
FEATURE [Part::Cylinder] Cylinder1119  label="Válec1119"
  Angle = 360
  AttacherType = Attacher::AttachEngine3D
  Height = 20
  Placement = pos=(76,18,-18) rot=(0,0,1;0rad)
  Radius = 4
FEATURE [Part::Cylinder] Cylinder1120  label="Válec1120"
  Angle = 360
  AttacherType = Attacher::AttachEngine3D
  Height = 20
  Placement = pos=(91,-21,-18) rot=(0,0,1;0rad)
  Radius = 4
FEATURE [Part::Cylinder] Cylinder1121  label="Válec1121"
  Angle = 360
  AttacherType = Attacher::AttachEngine3D
  Height = 40
  Placement = pos=(13,-21,-18) rot=(0,0,1;0rad)
  Radius = 4
FEATURE [Part::Cylinder] Cylinder1122  label="Válec1122"
  Angle = 360
  AttacherType = Attacher::AttachEngine3D
  Height = 40
  Placement = pos=(28,18,-18) rot=(0,0,1;0rad)
  Radius = 4
FEATURE [Part::Cylinder] Cylinder1123  label="Válec1123"
  Angle = 360
  AttacherType = Attacher::AttachEngine3D
  Height = 40
  Placement = pos=(1,-12,-18) rot=(0,0,1;0rad)
  Radius = 4
FEATURE [Part::Cylinder] Cylinder1124  label="Válec1124"
  Angle = 360
  AttacherType = Attacher::AttachEngine3D
  Height = 40
  Placement = pos=(1,6,-18) rot=(0,0,1;0rad)
  Radius = 4
FEATURE [Part::Compound] Compound564  label="srouby_monoblok_silne002"
  Links = -> [Cylinder1117,Cylinder1118,Cylinder1119,Cylinder1120,Cylinder1121,Cylinder1122,Cylinder1123,Cylinder1124]
FEATURE [Part::Cut] Cut249
  Base = -> Cylinder1091
  Tool = -> Compound564
FEATURE [Part::Cut] Cut250
  Base = -> Cylinder1092
  Tool = -> Compound562
FEATURE [Part::Cylinder] Cylinder1125  label="Válec1125"
  Angle = 360
  AttacherType = Attacher::AttachEngine3D
  Height = 100
  Placement = pos=(36,34,-90) rot=(0,0,1;0rad)
  Radius = 4
FEATURE [Part::Cylinder] Cylinder1126  label="Válec1126"
  Angle = 360
  AttacherType = Attacher::AttachEngine3D
  Height = 100
  Placement = pos=(-50,0,-90) rot=(0,0,1;0rad)
  Radius = 4
FEATURE [Part::Cylinder] Cylinder1127  label="Válec1127"
  Angle = 360
  AttacherType = Attacher::AttachEngine3D
  Height = 100
  Placement = pos=(-36,34,-90) rot=(0,0,1;0rad)
  Radius = 4
FEATURE [Part::Cylinder] Cylinder1128  label="Válec1128"
  Angle = 360
  AttacherType = Attacher::AttachEngine3D
  Height = 100
  Placement = pos=(-36,-34,-90) rot=(0,0,1;0rad)
  Radius = 4
FEATURE [Part::Cylinder] Cylinder1129  label="Válec1129"
  Angle = 360
  AttacherType = Attacher::AttachEngine3D
  Height = 100
  Placement = pos=(50,0,-90) rot=(0,0,1;0rad)
  Radius = 4
FEATURE [Part::Cylinder] Cylinder1130  label="Válec1130"
  Angle = 360
  AttacherType = Attacher::AttachEngine3D
  Height = 100
  Placement = pos=(36,-34,-90) rot=(0,0,1;0rad)
  Radius = 4
FEATURE [Part::Compound] Compound565  label="sbouby_baze_silne"
  Links = -> [Cylinder1126,Cylinder1127,Cylinder1128,Cylinder1129,Cylinder1125,Cylinder1130]
FEATURE [Part::Cylinder] Cylinder1131  label="Válec1131"
  Angle = 360
  AttacherType = Attacher::AttachEngine3D
  Height = 100
  Placement = pos=(36,34,-90) rot=(0,0,1;0rad)
  Radius = 4
FEATURE [Part::Cylinder] Cylinder1132  label="Válec1132"
  Angle = 360
  AttacherType = Attacher::AttachEngine3D
  Height = 100
  Placement = pos=(-50,0,-90) rot=(0,0,1;0rad)
  Radius = 4
FEATURE [Part::Cylinder] Cylinder1133  label="Válec1133"
  Angle = 360
  AttacherType = Attacher::AttachEngine3D
  Height = 100
  Placement = pos=(-36,34,-90) rot=(0,0,1;0rad)
  Radius = 4
FEATURE [Part::Cylinder] Cylinder1134  label="Válec1134"
  Angle = 360
  AttacherType = Attacher::AttachEngine3D
  Height = 100
  Placement = pos=(-36,-34,-90) rot=(0,0,1;0rad)
  Radius = 4
FEATURE [Part::Cylinder] Cylinder1135  label="Válec1135"
  Angle = 360
  AttacherType = Attacher::AttachEngine3D
  Height = 100
  Placement = pos=(50,0,-90) rot=(0,0,1;0rad)
  Radius = 4
FEATURE [Part::Cylinder] Cylinder1136  label="Válec1136"
  Angle = 360
  AttacherType = Attacher::AttachEngine3D
  Height = 100
  Placement = pos=(36,-34,-90) rot=(0,0,1;0rad)
  Radius = 4
FEATURE [Part::Compound] Compound566  label="sbouby_baze_silne001"
  Links = -> [Cylinder1132,Cylinder1133,Cylinder1134,Cylinder1135,Cylinder1131,Cylinder1136]
FEATURE [Part::Cut] Cut251
  Base = -> Cut250
  Tool = -> Compound565
FEATURE [Part::Cylinder] Cylinder1137  label="Válec1137"
  Angle = 360
  AttacherType = Attacher::AttachEngine3D
  Height = 100
  Placement = pos=(36,34,-90) rot=(0,0,1;0rad)
  Radius = 4
FEATURE [Part::Cylinder] Cylinder1138  label="Válec1138"
  Angle = 360
  AttacherType = Attacher::AttachEngine3D
  Height = 100
  Placement = pos=(-50,0,-90) rot=(0,0,1;0rad)
  Radius = 4
FEATURE [Part::Cylinder] Cylinder1139  label="Válec1139"
  Angle = 360
  AttacherType = Attacher::AttachEngine3D
  Height = 100
  Placement = pos=(-36,34,-90) rot=(0,0,1;0rad)
  Radius = 4
FEATURE [Part::Cylinder] Cylinder1140  label="Válec1140"
  Angle = 360
  AttacherType = Attacher::AttachEngine3D
  Height = 100
  Placement = pos=(-36,-34,-90) rot=(0,0,1;0rad)
  Radius = 4
FEATURE [Part::Cylinder] Cylinder1141  label="Válec1141"
  Angle = 360
  AttacherType = Attacher::AttachEngine3D
  Height = 100
  Placement = pos=(50,0,-90) rot=(0,0,1;0rad)
  Radius = 4
FEATURE [Part::Cylinder] Cylinder1142  label="Válec1142"
  Angle = 360
  AttacherType = Attacher::AttachEngine3D
  Height = 100
  Placement = pos=(36,-34,-90) rot=(0,0,1;0rad)
  Radius = 4
FEATURE [Part::Compound] Compound567  label="sbouby_baze_silne002"
  Links = -> [Cylinder1138,Cylinder1139,Cylinder1140,Cylinder1141,Cylinder1137,Cylinder1142]
FEATURE [Part::Cut] Cut252
  Base = -> Cut248
  Tool = -> Compound567
FEATURE [Part::Cut] Cut253
  Base = -> Cut249
  Tool = -> Compound566
FEATURE [Part::Cylinder] Cylinder1143  label="Válec1143"
  Angle = 360
  AttacherType = Attacher::AttachEngine3D
  Height = 100
  Placement = pos=(36,34,-60) rot=(0,0,1;0rad)
  Radius = 1.5
FEATURE [Part::Cylinder] Cylinder1144  label="Válec1144"
  Angle = 360
  AttacherType = Attacher::AttachEngine3D
  Height = 100
  Placement = pos=(-50,0,-60) rot=(0,0,1;0rad)
  Radius = 1.5
FEATURE [Part::Cylinder] Cylinder1145  label="Válec1145"
  Angle = 360
  AttacherType = Attacher::AttachEngine3D
  Height = 100
  Placement = pos=(-36,34,-60) rot=(0,0,1;0rad)
  Radius = 1.5
FEATURE [Part::Cylinder] Cylinder1146  label="Válec1146"
  Angle = 360
  AttacherType = Attacher::AttachEngine3D
  Height = 100
  Placement = pos=(-36,-34,-60) rot=(0,0,1;0rad)
  Radius = 1.5
FEATURE [Part::Cylinder] Cylinder1147  label="Válec1147"
  Angle = 360
  AttacherType = Attacher::AttachEngine3D
  Height = 100
  Placement = pos=(50,0,-60) rot=(0,0,1;0rad)
  Radius = 1.5
FEATURE [Part::Cylinder] Cylinder1148  label="Válec1148"
  Angle = 360
  AttacherType = Attacher::AttachEngine3D
  Height = 100
  Placement = pos=(36,-34,-60) rot=(0,0,1;0rad)
  Radius = 1.5
FEATURE [Part::Compound] Compound568  label="sbouby_baze001"
  Links = -> [Cylinder1144,Cylinder1145,Cylinder1146,Cylinder1147,Cylinder1143,Cylinder1148]
FEATURE [Part::Cut] Cut254
  Base = -> Cut252
  Tool = -> Compound568
FEATURE [Part::Cut] Cut255
  Base = -> Cut253
  Tool = -> Compound560
FEATURE [Part::Box] Box214  label="Krychle214"
  AttacherType = Attacher::AttachEngine3D
  Height = 100
  Length = 200
  Placement = pos=(-60,-130,-90) rot=(0,0,1;0rad)
  Width = 100
FEATURE [Part::Cut] Cut256
  Base = -> Cut254
  Tool = -> Box214
FEATURE [Part::Box] Box204  label="Krychle204"
  AttacherType = Attacher::AttachEngine3D
  Height = 23
  Length = 3
  Placement = pos=(-58,48,37) rot=(0,0,1;0rad)
  Width = 24
FEATURE [Part::Box] Box205  label="Krychle205"
  AttacherType = Attacher::AttachEngine3D
  Height = 23
  Length = 22
  Placement = pos=(-56,0,37) rot=(0,0,1;0rad)
  Width = 72
FEATURE [Part::FeaturePython] Tube034  # WARN: FeaturePython — macro-defined, semantics opaque (R4)
  AttacherType = Attacher::AttachEngine3D
  Height = 23
  InnerRadius = 42
  OuterRadius = 56
  Placement = pos=(0,0,37) rot=(0,0,1;0rad)
FEATURE [Part::Box] Box201  label="Krychle201"
  AttacherType = Attacher::AttachEngine3D
  Height = 2
  Length = 16
  Placement = pos=(18,62,55) rot=(0,0,1;0rad)
  Width = 6
FEATURE [Part::Box] Box200  label="Krychle200"
  AttacherType = Attacher::AttachEngine3D
  Height = 23
  Length = 22
  Placement = pos=(34,0,37) rot=(0,0,1;0rad)
  Width = 72
FEATURE [Part::Compound] Compound439
  Links = -> [Box200,Box205]
FEATURE [Part::Box] Box202  label="Krychle202"
  AttacherType = Attacher::AttachEngine3D
  Height = 23
  Length = 28
  Placement = pos=(-36,42,37) rot=(0,0,1;0rad)
  Width = 28
FEATURE [Part::Box] Box203  label="Krychle203"
  AttacherType = Attacher::AttachEngine3D
  Height = 2
  Length = 10
  Placement = pos=(-57,-3,54) rot=(0,0,1;0rad)
  Width = 6
FEATURE [Part::Cylinder] Cylinder1149  label="Válec1149"
  Angle = 360
  AttacherType = Attacher::AttachEngine3D
  Height = 23
  Placement = pos=(-9,73,37) rot=(0,0,1;0rad)
  Radius = 20
FEATURE [Part::Cut] Cut257
  Base = -> Box202
  Placement = pos=(2,2,0) rot=(0,0,1;0rad)
  Tool = -> Cylinder1149
FEATURE [Part::Cylinder] Cylinder1150  label="Válec1150"
  Angle = 360
  AttacherType = Attacher::AttachEngine3D
  Height = 30
  Placement = pos=(-55,65,42.5) rot=(0,0,1;0rad)
  Radius = 1.5
FEATURE [Part::Cylinder] Cylinder1151  label="Válec1151"
  Angle = 360
  AttacherType = Attacher::AttachEngine3D
  Height = 30
  Placement = pos=(-52,0,35.5) rot=(0,0,1;0rad)
  Radius = 1.5
FEATURE [Part::Cylinder] Cylinder1152  label="Válec1152"
  Angle = 360
  AttacherType = Attacher::AttachEngine3D
  Height = 150
  Placement = pos=(-57,56,18) rot=(0,1,0;1.5708rad)
  Radius = 2.5
FEATURE [Part::Box] Box206  label="Krychle206"
  AttacherType = Attacher::AttachEngine3D
  Height = 23
  Length = 3
  Placement = pos=(55,48,37) rot=(0,0,1;0rad)
  Width = 24
FEATURE [Part::Compound] Compound444
  Links = -> [Box204,Box206]
FEATURE [Part::Cylinder] Cylinder1153  label="Válec1153"
  Angle = 360
  AttacherType = Attacher::AttachEngine3D
  Height = 160
  Placement = pos=(-62,58,18) rot=(0,1,0;1.5708rad)
  Radius = 2.5
FEATURE [Part::Cylinder] Cylinder1154  label="Válec1154"
  Angle = 360
  AttacherType = Attacher::AttachEngine3D
  Height = 30
  Placement = pos=(55,65,42.5) rot=(0,0,1;0rad)
  Radius = 1.5
FEATURE [Part::Compound] Compound429
  Links = -> [Cylinder1154,Cylinder1150]
FEATURE [Part::Cylinder] Cylinder1155  label="Válec1155"
  Angle = 360
  AttacherType = Attacher::AttachEngine3D
  Height = 20
  Placement = pos=(8,56,49) rot=(0,1,0;1.5708rad)
  Radius = 5
FEATURE [Part::Box] Box207  label="Krychle207"
  AttacherType = Attacher::AttachEngine3D
  Height = 20
  Length = 20
  Placement = pos=(-52,30,40) rot=(0,0,1;0rad)
  Width = 200
FEATURE [Part::Cylinder] Cylinder1156  label="Válec1156"
  Angle = 360
  AttacherType = Attacher::AttachEngine3D
  Height = 30
  Placement = pos=(0,-42,35.5) rot=(0,0,1;0rad)
  Radius = 1.5
FEATURE [Part::Cylinder] Cylinder354  label="Válec354"
  Angle = 360
  AttacherType = Attacher::AttachEngine3D
  Height = 2
  Placement = pos=(-80,38,18) rot=(0,1,0;1.5708rad)
  Radius = 2.5
FEATURE [Part::Box] Box215  label="Krychle215"
  AttacherType = Attacher::AttachEngine3D
  Height = 2
  Length = 16
  Placement = pos=(-34,62,55) rot=(0,0,1;0rad)
  Width = 6
FEATURE [Part::Compound] Compound432
  Links = -> [Box215,Box201]
FEATURE [Part::Cylinder] Cylinder355  label="Válec355"
  Angle = 360
  AttacherType = Attacher::AttachEngine3D
  Height = 30
  Placement = pos=(29,65,51) rot=(0,0,1;0rad)
  Radius = 1.5
FEATURE [Part::Cylinder] Cylinder1157  label="Válec1157"
  Angle = 360
  AttacherType = Attacher::AttachEngine3D
  Height = 40
  Placement = pos=(-80,38,18) rot=(0,1,0;1.5708rad)
  Radius = 2.5
FEATURE [Part::Box] Box216  label="Krychle216"
  AttacherType = Attacher::AttachEngine3D
  Height = 23
  Length = 28
  Placement = pos=(8,42,37) rot=(0,0,1;0rad)
  Width = 28
FEATURE [Part::Box] Box217  label="Krychle217"
  AttacherType = Attacher::AttachEngine3D
  Height = 20
  Length = 20
  Placement = pos=(32,30,40) rot=(0,0,1;0rad)
  Width = 200
FEATURE [Part::Cylinder] Cylinder1158  label="Válec1158"
  Angle = 360
  AttacherType = Attacher::AttachEngine3D
  Height = 23
  Placement = pos=(9,73,37) rot=(0,0,1;0rad)
  Radius = 20
FEATURE [Part::Cylinder] Cylinder1159  label="Válec1159"
  Angle = 360
  AttacherType = Attacher::AttachEngine3D
  Height = 30
  Placement = pos=(-29,65,51) rot=(0,0,1;0rad)
  Radius = 1.5
FEATURE [Part::Compound] Compound442
  Links = -> [Cylinder1159,Cylinder355]
FEATURE [Part::Cylinder] Cylinder1160  label="Válec1160"
  Angle = 360
  AttacherType = Attacher::AttachEngine3D
  Height = 20
  Placement = pos=(-28,56,49) rot=(0,1,0;1.5708rad)
  Radius = 5
FEATURE [Part::Compound] Compound441
  Links = -> [Cylinder1160,Cylinder1155]
  Placement = pos=(0,4,0) rot=(0,0,1;0rad)
FEATURE [Part::Cylinder] Cylinder1161  label="Válec1161"
  Angle = 360
  AttacherType = Attacher::AttachEngine3D
  Height = 30
  Placement = pos=(-55,65,41.5) rot=(0,0,1;0rad)
  Radius = 1.5
FEATURE [Part::Box] Box218  label="Krychle218"
  AttacherType = Attacher::AttachEngine3D
  Height = 2
  Length = 10
  Placement = pos=(-3,57,54) rot=(0,0,-1;1.5708rad)
  Width = 6
FEATURE [Part::Cylinder] Cylinder1162  label="Válec1162"
  Angle = 360
  AttacherType = Attacher::AttachEngine3D
  Height = 30
  Placement = pos=(0,-52,35.5) rot=(0,0,1;1.5708rad)
  Radius = 1.5
FEATURE [Part::Box] Box219  label="Krychle219"
  AttacherType = Attacher::AttachEngine3D
  Height = 2
  Length = 10
  Placement = pos=(-57,-3,54) rot=(0,0,1;0rad)
  Width = 6
FEATURE [Part::Box] Box220  label="Krychle220"
  AttacherType = Attacher::AttachEngine3D
  Height = 2
  Length = 10
  Placement = pos=(-3,57,54) rot=(0,0,-1;1.5708rad)
  Width = 6
FEATURE [Part::Box] Box221  label="Krychle221"
  AttacherType = Attacher::AttachEngine3D
  Height = 2
  Length = 22
  Placement = pos=(-73,62,54) rot=(0,0,1;0rad)
  Width = 6
FEATURE [Part::Cylinder] Cylinder1163  label="Válec1163"
  Angle = 360
  AttacherType = Attacher::AttachEngine3D
  Height = 150
  Placement = pos=(-69,58,18) rot=(0,1,0;1.5708rad)
  Radius = 2.5
FEATURE [Part::Cylinder] Cylinder1164  label="Válec1164"
  Angle = 360
  AttacherType = Attacher::AttachEngine3D
  Height = 30
  Placement = pos=(0,-52,35.5) rot=(0,0,1;1.5708rad)
  Radius = 1.5
FEATURE [Part::Cylinder] Cylinder1165  label="Válec1165"
  Angle = 360
  AttacherType = Attacher::AttachEngine3D
  Height = 30
  Placement = pos=(-57,38,18) rot=(0,1,0;1.5708rad)
  Radius = 2.5
FEATURE [Part::Cylinder] Cylinder1166  label="Válec1166"
  Angle = 360
  AttacherType = Attacher::AttachEngine3D
  Height = 30
  Placement = pos=(28,38,18) rot=(0,1,0;1.5708rad)
  Radius = 2.5
FEATURE [Part::Compound] Compound436
  Links = -> [Cylinder1163,Cylinder1165,Cylinder1166]
  Placement = pos=(-1,2,31) rot=(0,0,1;0rad)
FEATURE [Part::Cut] Cut263
  Base = -> Box216
  Placement = pos=(-2,2,0) rot=(0,0,1;0rad)
  Tool = -> Cylinder1158
FEATURE [Part::Compound] Compound437
  Links = -> [Cut263,Cut257]
FEATURE [Part::Cut] Cut276
  Base = -> Compound444
  Tool = -> Compound436
FEATURE [Part::Compound] Compound475
  Links = -> [Box217,Box207]
FEATURE [Part::Box] Box222  label="Krychle222"
  AttacherType = Attacher::AttachEngine3D
  Height = 2
  Length = 22
  Placement = pos=(51,62,54) rot=(0,0,1;0rad)
  Width = 6
FEATURE [Part::Compound] Compound431
  Links = -> [Box221,Box222]
FEATURE [Part::Cylinder] Cylinder1167  label="Válec1167"
  Angle = 360
  AttacherType = Attacher::AttachEngine3D
  Height = 30
  Placement = pos=(52,0,35.5) rot=(0,0,1;3.14159rad)
  Radius = 1.5
FEATURE [Part::Cylinder] Cylinder1168  label="Válec1168"
  Angle = 360
  AttacherType = Attacher::AttachEngine3D
  Height = 30
  Placement = pos=(41,38,18) rot=(0,1,0;1.5708rad)
  Radius = 2.5
FEATURE [Part::Compound] Compound445
  Links = -> [Cylinder1153,Cylinder1157,Cylinder1168]
  Placement = pos=(-1,2,31) rot=(0,0,1;0rad)
FEATURE [Part::Cut] Cut268
  Base = -> Compound439
  Tool = -> Compound445
FEATURE [Part::Cut] Cut264
  Base = -> Cut268
  Tool = -> Compound429
FEATURE [Part::Cut] Cut270
  Base = -> Cut264
  Tool = -> Compound431
FEATURE [Part::Cylinder] Cylinder1169  label="Válec1169"
  Angle = 360
  AttacherType = Attacher::AttachEngine3D
  Height = 30
  Placement = pos=(1.7e-14,52,35.5) rot=(0,0,-1;1.5708rad)
  Radius = 1.5
FEATURE [Part::Cylinder] Cylinder1170  label="Válec1170"
  Angle = 360
  AttacherType = Attacher::AttachEngine3D
  Height = 30
  Placement = pos=(55,65,42.5) rot=(0,0,1;0rad)
  Radius = 1.5
FEATURE [Part::Compound] Compound443
  Links = -> [Cylinder1161,Cylinder1170]
FEATURE [Part::Cylinder] Cylinder1171  label="Válec1171"
  Angle = 360
  AttacherType = Attacher::AttachEngine3D
  Height = 2
  Placement = pos=(80,38,18) rot=(0,1,0;1.5708rad)
  Radius = 2.5
FEATURE [Part::Compound] Compound430
  Links = -> [Cylinder1152,Cylinder354,Cylinder1171]
  Placement = pos=(-1,4,31) rot=(0,0,1;0rad)
FEATURE [Part::Cut] Cut259
  Base = -> Compound437
  Tool = -> Compound430
FEATURE [Part::Cut] Cut271
  Base = -> Cut259
  Tool = -> Compound441
FEATURE [Part::Cut] Cut260
  Base = -> Cut271
  Tool = -> Compound432
FEATURE [Part::Cut] Cut261
  Base = -> Cut260
  Tool = -> Compound442
FEATURE [Part::Box] Box223  label="Krychle223"
  AttacherType = Attacher::AttachEngine3D
  Height = 2
  Length = 10
  Placement = pos=(3,-57,54) rot=(0,0,1;1.5708rad)
  Width = 6
FEATURE [Part::Box] Box224  label="Krychle224"
  AttacherType = Attacher::AttachEngine3D
  Height = 2
  Length = 22
  Placement = pos=(-73,62,54) rot=(0,0,1;0rad)
  Width = 6
FEATURE [Part::Cut] Cut267
  Base = -> Cut276
  Tool = -> Box224
FEATURE [Part::Cylinder] Cylinder1172  label="Válec1172"
  Angle = 360
  AttacherType = Attacher::AttachEngine3D
  Height = 30
  Placement = pos=(1.7e-14,52,35.5) rot=(0,0,-1;1.5708rad)
  Radius = 1.5
FEATURE [Part::Compound] Compound467
  Links = -> [Cylinder1172,Cylinder1167,Cylinder1162,Cylinder1151]
FEATURE [Part::Cylinder] Cylinder1173  label="Válec1173"
  Angle = 360
  AttacherType = Attacher::AttachEngine3D
  Height = 30
  Placement = pos=(-52,0,35.5) rot=(0,0,1;0rad)
  Radius = 1.5
FEATURE [Part::Box] Box225  label="Krychle225"
  AttacherType = Attacher::AttachEngine3D
  Height = 20
  Length = 20
  Placement = pos=(-52,30,40) rot=(0,0,1;0rad)
  Width = 200
FEATURE [Part::Box] Box226  label="Krychle226"
  AttacherType = Attacher::AttachEngine3D
  Height = 2
  Length = 22
  Placement = pos=(51,62,54) rot=(0,0,1;0rad)
  Width = 6
FEATURE [Part::Cut] Cut258
  Base = -> Cut267
  Tool = -> Box226
FEATURE [Part::Cut] Cut269
  Base = -> Cut258
  Tool = -> Compound443
FEATURE [Part::Box] Box227  label="Krychle227"
  AttacherType = Attacher::AttachEngine3D
  Height = 20
  Length = 20
  Placement = pos=(-52,30,40) rot=(0,0,1;0rad)
  Width = 200
FEATURE [Part::Cylinder] Cylinder1174  label="Válec1174"
  Angle = 360
  AttacherType = Attacher::AttachEngine3D
  Height = 30
  Placement = pos=(0,-42,35.5) rot=(0,0,1;0rad)
  Radius = 1.5
FEATURE [Part::Compound] Compound435
  Links = -> [Cylinder1174]
  Placement = pos=(0,0,0) rot=(0,0,-1;0.392699rad)
FEATURE [Part::Compound] Compound433
  Links = -> [Cylinder1174]
  Placement = pos=(0,0,0) rot=(0,0,1;1.1781rad)
FEATURE [Part::Compound] Compound448
  Links = -> [Cylinder1174]
  Placement = pos=(0,0,0) rot=(0,0,1;2.74889rad)
FEATURE [Part::Compound] Compound449
  Links = -> [Cylinder1174]
  Placement = pos=(0,0,0) rot=(0,0,-1;1.96349rad)
FEATURE [Part::Compound] Compound440
  Links = -> [Cylinder1174]
  Placement = pos=(0,0,0) rot=(0,0,-1;1.1781rad)
FEATURE [Part::Compound] Compound452
  Links = -> [Cylinder1174]
  Placement = pos=(0,0,0) rot=(0,0,1;0.392699rad)
FEATURE [Part::Compound] Compound476
  Links = -> [Cylinder1174]
  Placement = pos=(0,0,0) rot=(0,0,1;1.96349rad)
FEATURE [Part::Box] Box228  label="Krychle228"
  AttacherType = Attacher::AttachEngine3D
  Height = 2
  Length = 10
  Placement = pos=(57,3,54) rot=(0,0,1;3.14159rad)
  Width = 6
FEATURE [Part::Box] Box229  label="Krychle229"
  AttacherType = Attacher::AttachEngine3D
  Height = 20
  Length = 20
  Placement = pos=(32,30,40) rot=(0,0,1;0rad)
  Width = 200
FEATURE [Part::Compound] Compound459
  Links = -> [Box229,Box225]
FEATURE [Part::Box] Box230  label="Krychle230"
  AttacherType = Attacher::AttachEngine3D
  Height = 2
  Length = 10
  Placement = pos=(3,-57,54) rot=(0,0,1;1.5708rad)
  Width = 6
FEATURE [Part::Box] Box231  label="Krychle231"
  AttacherType = Attacher::AttachEngine3D
  Height = 2
  Length = 10
  Placement = pos=(57,3,54) rot=(0,0,1;3.14159rad)
  Width = 6
FEATURE [Part::Compound] Compound468
  Links = -> [Box220,Box231,Box230,Box203]
FEATURE [Part::Cylinder] Cylinder1175  label="Válec1175"
  Angle = 360
  AttacherType = Attacher::AttachEngine3D
  Height = 30
  Placement = pos=(0,-42,35.5) rot=(0,0,1;0rad)
  Radius = 1.5
FEATURE [Part::Compound] Compound453
  Links = -> [Cylinder1175]
  Placement = pos=(0,0,0) rot=(0,0,1;1.96349rad)
FEATURE [Part::Compound] Compound457
  Links = -> [Cylinder1175]
  Placement = pos=(0,0,0) rot=(0,0,-1;1.96349rad)
FEATURE [Part::Compound] Compound469
  Links = -> [Cylinder1175]
  Placement = pos=(0,0,0) rot=(0,0,1;2.74889rad)
FEATURE [Part::Compound] Compound463
  Links = -> [Cylinder1175]
  Placement = pos=(0,0,0) rot=(0,0,-1;1.1781rad)
FEATURE [Part::Compound] Compound473
  Links = -> [Cylinder1175]
  Placement = pos=(0,0,0) rot=(0,0,-1;0.392699rad)
FEATURE [Part::Compound] Compound471
  Links = -> [Cylinder1175]
  Placement = pos=(0,0,0) rot=(0,0,1;1.1781rad)
FEATURE [Part::Compound] Compound472
  Links = -> [Cylinder1175]
  Placement = pos=(0,0,0) rot=(0,0,1;3.53429rad)
FEATURE [Part::Compound] Compound466
  Links = -> [Cylinder1175]
  Placement = pos=(0,0,0) rot=(0,0,1;0.392699rad)
FEATURE [Part::Compound] Compound460
  Links = -> [Compound473,Compound463,Compound457,Compound472,Compound469,Compound466,Compound471,Compound453]
  Placement = pos=(0,0,1000) rot=(0,0,1;0rad)
FEATURE [Part::Cut] Cut265
  Base = -> Cut270
  Tool = -> Compound460
FEATURE [Part::Cylinder] Cylinder1176  label="Válec1176"
  Angle = 360
  AttacherType = Attacher::AttachEngine3D
  Height = 30
  Placement = pos=(52,0,35.5) rot=(0,0,1;3.14159rad)
  Radius = 1.5
FEATURE [Part::Compound] Compound455
  Links = -> [Cylinder1169,Cylinder1176,Cylinder1164,Cylinder1173]
FEATURE [Part::Cut] Cut277
  Base = -> Cut265
  Tool = -> Compound455
FEATURE [Part::Cylinder] Cylinder1177  label="Válec1177"
  Angle = 360
  AttacherType = Attacher::AttachEngine3D
  Height = 3
  Placement = pos=(0,-42,35.5) rot=(0,0,1;0rad)
  Radius = 3
FEATURE [Part::Compound] Compound458
  Links = -> [Cylinder1177]
  Placement = pos=(0,0,0) rot=(0,0,1;1.96349rad)
FEATURE [Part::Compound] Compound477
  Links = -> [Cylinder1177]
  Placement = pos=(0,0,0) rot=(0,0,1;2.74889rad)
FEATURE [Part::Compound] Compound479
  Links = -> [Cylinder1177]
  Placement = pos=(0,0,0) rot=(0,0,1;0.392699rad)
FEATURE [Part::Compound] Compound480
  Links = -> [Cylinder1177]
  Placement = pos=(0,0,0) rot=(0,0,1;1.1781rad)
FEATURE [Part::Compound] Compound461
  Links = -> [Cylinder1177]
  Placement = pos=(0,0,0) rot=(0,0,-1;1.1781rad)
FEATURE [Part::Compound] Compound462
  Links = -> [Cylinder1177]
  Placement = pos=(0,0,0) rot=(0,0,-1;0.392699rad)
FEATURE [Part::Box] Box232  label="Krychle232"
  AttacherType = Attacher::AttachEngine3D
  Height = 20
  Length = 20
  Placement = pos=(32,30,40) rot=(0,0,1;0rad)
  Width = 200
FEATURE [Part::Compound] Compound456
  Links = -> [Box232,Box227]
FEATURE [Part::Compound] Compound474
  Links = -> [Box218,Box228,Box223,Box219]
FEATURE [Part::Cut] Cut274
  Base = -> Cut277
  Tool = -> Compound474
FEATURE [Part::Cut] Cut278
  Base = -> Cut274
  Tool = -> Compound459
FEATURE [Part::Compound] Compound470
  Links = -> [Cylinder1174]
  Placement = pos=(0,0,0) rot=(0,0,1;3.53429rad)
FEATURE [Part::Compound] Compound450
  Links = -> [Compound435,Compound440,Compound449,Compound470,Compound448,Compound452,Compound433,Compound476]
  Placement = pos=(0,0,1000) rot=(0,0,1;0rad)
FEATURE [Part::Cut] Cut262
  Base = -> Cut261
  Tool = -> Compound450
FEATURE [Part::Cut] Cut280
  Base = -> Cut262
  Tool = -> Compound456
FEATURE [Part::Compound] Compound478
  Links = -> [Cylinder1177]
  Placement = pos=(0,0,0) rot=(0,0,-1;1.96349rad)
FEATURE [Part::Compound] Compound481
  Links = -> [Cylinder1177]
  Placement = pos=(0,0,0) rot=(0,0,1;3.53429rad)
FEATURE [Part::Compound] Compound454
  Links = -> [Compound462,Compound461,Compound478,Compound481,Compound477,Compound479,Compound480,Compound458]
  Placement = pos=(0,0,1000) rot=(0,0,1;0rad)
FEATURE [Part::Cut] Cut272
  Base = -> Cut280
  Tool = -> Compound454
FEATURE [Part::Compound] Compound426
  Links = -> [Cylinder1156]
  Placement = pos=(0,0,0) rot=(0,0,-1;0.392699rad)
FEATURE [Part::Compound] Compound451
  Links = -> [Cylinder1156]
  Placement = pos=(0,0,0) rot=(0,0,-1;1.1781rad)
FEATURE [Part::Compound] Compound434
  Links = -> [Cylinder1156]
  Placement = pos=(0,0,0) rot=(0,0,-1;1.96349rad)
FEATURE [Part::Compound] Compound427
  Links = -> [Cylinder1156]
  Placement = pos=(0,0,0) rot=(0,0,1;3.53429rad)
FEATURE [Part::Compound] Compound428
  Links = -> [Cylinder1156]
  Placement = pos=(0,0,0) rot=(0,0,1;2.74889rad)
FEATURE [Part::Compound] Compound447
  Links = -> [Cylinder1156]
  Placement = pos=(0,0,0) rot=(0,0,1;0.392699rad)
FEATURE [Part::Compound] Compound438
  Links = -> [Cylinder1156]
  Placement = pos=(0,0,0) rot=(0,0,1;1.1781rad)
FEATURE [Part::Compound] Compound446
  Links = -> [Cylinder1156]
  Placement = pos=(0,0,0) rot=(0,0,1;1.96349rad)
FEATURE [Part::Compound] Compound425
  Links = -> [Compound426,Compound451,Compound434,Compound427,Compound428,Compound447,Compound438,Compound446]
  Placement = pos=(0,0,1000) rot=(0,0,1;0rad)
FEATURE [Part::Cut] Cut266
  Base = -> Tube034
  Tool = -> Compound425
FEATURE [Part::Cut] Cut279
  Base = -> Cut266
  Tool = -> Compound467
FEATURE [Part::Cut] Cut273
  Base = -> Cut279
  Tool = -> Compound468
FEATURE [Part::Cut] Cut275
  Base = -> Cut273
  Tool = -> Compound475
FEATURE [Part::Cylinder] Cylinder1178  label="Válec1178"
  Angle = 360
  AttacherType = Attacher::AttachEngine3D
  Height = 50
  Placement = pos=(18.3688,-44.3462,35.5) rot=(0,0,1;0.392699rad)
  Radius = 1.5
FEATURE [Part::Cylinder] Cylinder1179  label="Válec1179"
  Angle = 360
  AttacherType = Attacher::AttachEngine3D
  Height = 50
  Placement = pos=(-18.3688,44.3462,35.5) rot=(0,0,1;3.53429rad)
  Radius = 1.5
FEATURE [Part::Cylinder] Cylinder1180  label="Válec1180"
  Angle = 360
  AttacherType = Attacher::AttachEngine3D
  Height = 50
  Placement = pos=(44.3462,-18.3688,35.5) rot=(0,0,1;1.1781rad)
  Radius = 1.5
FEATURE [Part::Cylinder] Cylinder1181  label="Válec1181"
  Angle = 360
  AttacherType = Attacher::AttachEngine3D
  Height = 50
  Placement = pos=(-44.3462,-18.3688,35.5) rot=(0,0,-1;1.1781rad)
  Radius = 1.5
FEATURE [Part::Cylinder] Cylinder1182  label="Válec1182"
  Angle = 360
  AttacherType = Attacher::AttachEngine3D
  Height = 50
  Placement = pos=(-18.3688,-44.3462,35.5) rot=(0,0,-1;0.392699rad)
  Radius = 1.5
FEATURE [Part::Cylinder] Cylinder1183  label="Válec1183"
  Angle = 360
  AttacherType = Attacher::AttachEngine3D
  Height = 50
  Placement = pos=(18.3688,44.3462,35.5) rot=(0,0,1;2.74889rad)
  Radius = 1.5
FEATURE [Part::Cylinder] Cylinder1184  label="Válec1184"
  Angle = 360
  AttacherType = Attacher::AttachEngine3D
  Height = 50
  Placement = pos=(-44.3462,18.3688,35.5) rot=(0,0,-1;1.96349rad)
  Radius = 1.5
FEATURE [Part::Cylinder] Cylinder1185  label="Válec1185"
  Angle = 360
  AttacherType = Attacher::AttachEngine3D
  Height = 50
  Placement = pos=(44.3462,18.3688,35.5) rot=(0,0,1;1.96349rad)
  Radius = 1.5
FEATURE [Part::Compound] Compound501
  Links = -> [Cylinder1178,Cylinder1180,Cylinder1185,Cylinder1183,Cylinder1179,Cylinder1184,Cylinder1181,Cylinder1182]
FEATURE [Part::Cut] Cut197
  Base = -> Cut272
  Tool = -> Compound501
FEATURE [Part::Cylinder] Cylinder1186  label="Válec1186"
  Angle = 360
  AttacherType = Attacher::AttachEngine3D
  Height = 4
  Placement = pos=(-44.3462,18.3688,35.5) rot=(0,0,-1;1.96349rad)
  Radius = 3
FEATURE [Part::Cylinder] Cylinder1187  label="Válec1187"
  Angle = 360
  AttacherType = Attacher::AttachEngine3D
  Height = 4
  Placement = pos=(-18.3688,-44.3462,35.5) rot=(0,0,-1;0.392699rad)
  Radius = 3
FEATURE [Part::Cylinder] Cylinder1188  label="Válec1188"
  Angle = 360
  AttacherType = Attacher::AttachEngine3D
  Height = 4
  Placement = pos=(18.3688,-44.3462,35.5) rot=(0,0,1;0.392699rad)
  Radius = 3
FEATURE [Part::Cylinder] Cylinder1189  label="Válec1189"
  Angle = 360
  AttacherType = Attacher::AttachEngine3D
  Height = 4
  Placement = pos=(-18.3688,44.3462,35.5) rot=(0,0,1;3.53429rad)
  Radius = 3
FEATURE [Part::Cylinder] Cylinder1190  label="Válec1190"
  Angle = 360
  AttacherType = Attacher::AttachEngine3D
  Height = 4
  Placement = pos=(18.3688,44.3462,35.5) rot=(0,0,1;2.74889rad)
  Radius = 3
FEATURE [Part::Cylinder] Cylinder1191  label="Válec1191"
  Angle = 360
  AttacherType = Attacher::AttachEngine3D
  Height = 4
  Placement = pos=(44.3462,-18.3688,35.5) rot=(0,0,1;1.1781rad)
  Radius = 3
FEATURE [Part::Cylinder] Cylinder1192  label="Válec1192"
  Angle = 360
  AttacherType = Attacher::AttachEngine3D
  Height = 4
  Placement = pos=(-44.3462,-18.3688,35.5) rot=(0,0,-1;1.1781rad)
  Radius = 3
FEATURE [Part::Cylinder] Cylinder1193  label="Válec1193"
  Angle = 360
  AttacherType = Attacher::AttachEngine3D
  Height = 4
  Placement = pos=(44.3462,18.3688,35.5) rot=(0,0,1;1.96349rad)
  Radius = 3
FEATURE [Part::Compound] Compound502
  Links = -> [Cylinder1188,Cylinder1191,Cylinder1193,Cylinder1190,Cylinder1189,Cylinder1186,Cylinder1192,Cylinder1187]
  Placement = pos=(0,0,21) rot=(0,0,1;0rad)
FEATURE [Part::Cut] Cut198
  Base = -> Cut197
  Tool = -> Compound502
FEATURE [Part::Cylinder] Cylinder1194  label="Válec1194"
  Angle = 360
  AttacherType = Attacher::AttachEngine3D
  Height = 23
  Placement = pos=(0,0,37) rot=(0,0,1;0rad)
  Radius = 42
FEATURE [Part::Cut] Cut199
  Base = -> Cut198
  Tool = -> Cylinder1194
FEATURE [Part::Cylinder] Cylinder1195  label="Válec1195"
  Angle = 360
  AttacherType = Attacher::AttachEngine3D
  Height = 23
  Placement = pos=(0,0,37) rot=(0,0,1;0rad)
  Radius = 42
FEATURE [Part::Cylinder] Cylinder1196  label="Válec1196"
  Angle = 360
  AttacherType = Attacher::AttachEngine3D
  Height = 4
  Placement = pos=(-18.3688,44.3462,35.5) rot=(0,0,1;3.53429rad)
  Radius = 3
FEATURE [Part::Cylinder] Cylinder1197  label="Válec1197"
  Angle = 360
  AttacherType = Attacher::AttachEngine3D
  Height = 4
  Placement = pos=(-18.3688,-44.3462,35.5) rot=(0,0,-1;0.392699rad)
  Radius = 3
FEATURE [Part::Cylinder] Cylinder1198  label="Válec1198"
  Angle = 360
  AttacherType = Attacher::AttachEngine3D
  Height = 4
  Placement = pos=(-44.3462,18.3688,35.5) rot=(0,0,-1;1.96349rad)
  Radius = 3
FEATURE [Part::Cylinder] Cylinder1199  label="Válec1199"
  Angle = 360
  AttacherType = Attacher::AttachEngine3D
  Height = 4
  Placement = pos=(18.3688,-44.3462,35.5) rot=(0,0,1;0.392699rad)
  Radius = 3
FEATURE [Part::Cylinder] Cylinder1200  label="Válec1200"
  Angle = 360
  AttacherType = Attacher::AttachEngine3D
  Height = 4
  Placement = pos=(18.3688,44.3462,35.5) rot=(0,0,1;2.74889rad)
  Radius = 3
FEATURE [Part::Cylinder] Cylinder1201  label="Válec1201"
  Angle = 360
  AttacherType = Attacher::AttachEngine3D
  Height = 4
  Placement = pos=(44.3462,-18.3688,35.5) rot=(0,0,1;1.1781rad)
  Radius = 3
FEATURE [Part::Cylinder] Cylinder1202  label="Válec1202"
  Angle = 360
  AttacherType = Attacher::AttachEngine3D
  Height = 4
  Placement = pos=(-44.3462,-18.3688,35.5) rot=(0,0,-1;1.1781rad)
  Radius = 3
FEATURE [Part::Cylinder] Cylinder1203  label="Válec1203"
  Angle = 360
  AttacherType = Attacher::AttachEngine3D
  Height = 4
  Placement = pos=(44.3462,18.3688,35.5) rot=(0,0,1;1.96349rad)
  Radius = 3
FEATURE [Part::Compound] Compound503
  Links = -> [Cylinder1199,Cylinder1201,Cylinder1203,Cylinder1200,Cylinder1196,Cylinder1198,Cylinder1202,Cylinder1197]
  Placement = pos=(0,0,21) rot=(0,0,1;0rad)
FEATURE [Part::Cylinder] Cylinder1204  label="Válec1204"
  Angle = 360
  AttacherType = Attacher::AttachEngine3D
  Height = 50
  Placement = pos=(44.3462,-18.3688,35.5) rot=(0,0,1;1.1781rad)
  Radius = 1.5
FEATURE [Part::Cut] Cut200
  Base = -> Cut278
  Tool = -> Cylinder1195
FEATURE [Part::Cut] Cut281
  Base = -> Cut200
  Tool = -> Compound503
FEATURE [Part::Cylinder] Cylinder1205  label="Válec1205"
  Angle = 360
  AttacherType = Attacher::AttachEngine3D
  Height = 50
  Placement = pos=(18.3688,-44.3462,35.5) rot=(0,0,1;0.392699rad)
  Radius = 1.5
FEATURE [Part::Cylinder] Cylinder1206  label="Válec1206"
  Angle = 360
  AttacherType = Attacher::AttachEngine3D
  Height = 50
  Placement = pos=(-18.3688,44.3462,35.5) rot=(0,0,1;3.53429rad)
  Radius = 1.5
FEATURE [Part::Cylinder] Cylinder1207  label="Válec1207"
  Angle = 360
  AttacherType = Attacher::AttachEngine3D
  Height = 50
  Placement = pos=(-44.3462,18.3688,35.5) rot=(0,0,-1;1.96349rad)
  Radius = 1.5
FEATURE [Part::Cylinder] Cylinder1208  label="Válec1208"
  Angle = 360
  AttacherType = Attacher::AttachEngine3D
  Height = 50
  Placement = pos=(18.3688,44.3462,35.5) rot=(0,0,1;2.74889rad)
  Radius = 1.5
FEATURE [Part::Cylinder] Cylinder1209  label="Válec1209"
  Angle = 360
  AttacherType = Attacher::AttachEngine3D
  Height = 50
  Placement = pos=(-44.3462,-18.3688,35.5) rot=(0,0,-1;1.1781rad)
  Radius = 1.5
FEATURE [Part::Cylinder] Cylinder1210  label="Válec1210"
  Angle = 360
  AttacherType = Attacher::AttachEngine3D
  Height = 50
  Placement = pos=(-18.3688,-44.3462,35.5) rot=(0,0,-1;0.392699rad)
  Radius = 1.5
FEATURE [Part::Cylinder] Cylinder1211  label="Válec1211"
  Angle = 360
  AttacherType = Attacher::AttachEngine3D
  Height = 50
  Placement = pos=(44.3462,18.3688,35.5) rot=(0,0,1;1.96349rad)
  Radius = 1.5
FEATURE [Part::Compound] Compound504
  Links = -> [Cylinder1205,Cylinder1204,Cylinder1211,Cylinder1208,Cylinder1206,Cylinder1207,Cylinder1209,Cylinder1210]
FEATURE [Part::Cut] Cut283
  Base = -> Cut275
  Tool = -> Compound504
FEATURE [Part::Cylinder] Cylinder1212  label="Válec1212"
  Angle = 360
  AttacherType = Attacher::AttachEngine3D
  Height = 4
  Placement = pos=(18.3688,-44.3462,35.5) rot=(0,0,1;0.392699rad)
  Radius = 3
FEATURE [Part::Cylinder] Cylinder1213  label="Válec1213"
  Angle = 360
  AttacherType = Attacher::AttachEngine3D
  Height = 50
  Placement = pos=(44.3462,-18.3688,35.5) rot=(0,0,1;1.1781rad)
  Radius = 1.5
FEATURE [Part::Cylinder] Cylinder1214  label="Válec1214"
  Angle = 360
  AttacherType = Attacher::AttachEngine3D
  Height = 4
  Placement = pos=(-44.3462,-18.3688,35.5) rot=(0,0,-1;1.1781rad)
  Radius = 3
FEATURE [Part::Cylinder] Cylinder1215  label="Válec1215"
  Angle = 360
  AttacherType = Attacher::AttachEngine3D
  Height = 50
  Placement = pos=(18.3688,-44.3462,35.5) rot=(0,0,1;0.392699rad)
  Radius = 1.5
FEATURE [Part::Cylinder] Cylinder1216  label="Válec1216"
  Angle = 360
  AttacherType = Attacher::AttachEngine3D
  Height = 50
  Placement = pos=(-44.3462,-18.3688,35.5) rot=(0,0,-1;1.1781rad)
  Radius = 1.5
FEATURE [Part::Cylinder] Cylinder1217  label="Válec1217"
  Angle = 360
  AttacherType = Attacher::AttachEngine3D
  Height = 50
  Placement = pos=(44.3462,18.3688,35.5) rot=(0,0,1;1.96349rad)
  Radius = 1.5
FEATURE [Part::Cylinder] Cylinder1218  label="Válec1218"
  Angle = 360
  AttacherType = Attacher::AttachEngine3D
  Height = 4
  Placement = pos=(44.3462,-18.3688,35.5) rot=(0,0,1;1.1781rad)
  Radius = 3
FEATURE [Part::Cylinder] Cylinder1219  label="Válec1219"
  Angle = 360
  AttacherType = Attacher::AttachEngine3D
  Height = 4
  Placement = pos=(-44.3462,18.3688,35.5) rot=(0,0,-1;1.96349rad)
  Radius = 3
FEATURE [Part::Cylinder] Cylinder1220  label="Válec1220"
  Angle = 360
  AttacherType = Attacher::AttachEngine3D
  Height = 4
  Placement = pos=(-18.3688,44.3462,35.5) rot=(0,0,1;3.53429rad)
  Radius = 3
FEATURE [Part::Cylinder] Cylinder1221  label="Válec1221"
  Angle = 360
  AttacherType = Attacher::AttachEngine3D
  Height = 4
  Placement = pos=(-18.3688,-44.3462,35.5) rot=(0,0,-1;0.392699rad)
  Radius = 3
FEATURE [Part::Cylinder] Cylinder1222  label="Válec1222"
  Angle = 360
  AttacherType = Attacher::AttachEngine3D
  Height = 4
  Placement = pos=(18.3688,44.3462,35.5) rot=(0,0,1;2.74889rad)
  Radius = 3
FEATURE [Part::Cylinder] Cylinder1223  label="Válec1223"
  Angle = 360
  AttacherType = Attacher::AttachEngine3D
  Height = 4
  Placement = pos=(44.3462,18.3688,35.5) rot=(0,0,1;1.96349rad)
  Radius = 3
FEATURE [Part::Compound] Compound506
  Links = -> [Cylinder1212,Cylinder1218,Cylinder1223,Cylinder1222,Cylinder1220,Cylinder1219,Cylinder1214,Cylinder1221]
  Placement = pos=(0,0,21) rot=(0,0,1;0rad)
FEATURE [Part::Cut] Cut284
  Base = -> Cut283
  Tool = -> Compound506
FEATURE [Part::Cylinder] Cylinder1224  label="Válec1224"
  Angle = 360
  AttacherType = Attacher::AttachEngine3D
  Height = 50
  Placement = pos=(-18.3688,44.3462,35.5) rot=(0,0,1;3.53429rad)
  Radius = 1.5
FEATURE [Part::Cylinder] Cylinder1225  label="Válec1225"
  Angle = 360
  AttacherType = Attacher::AttachEngine3D
  Height = 50
  Placement = pos=(-44.3462,18.3688,35.5) rot=(0,0,-1;1.96349rad)
  Radius = 1.5
FEATURE [Part::Cylinder] Cylinder1226  label="Válec1226"
  Angle = 360
  AttacherType = Attacher::AttachEngine3D
  Height = 50
  Placement = pos=(18.3688,44.3462,35.5) rot=(0,0,1;2.74889rad)
  Radius = 1.5
FEATURE [Part::Cylinder] Cylinder1227  label="Válec1227"
  Angle = 360
  AttacherType = Attacher::AttachEngine3D
  Height = 50
  Placement = pos=(-18.3688,-44.3462,35.5) rot=(0,0,-1;0.392699rad)
  Radius = 1.5
FEATURE [Part::Compound] Compound505
  Links = -> [Cylinder1215,Cylinder1213,Cylinder1217,Cylinder1226,Cylinder1224,Cylinder1225,Cylinder1216,Cylinder1227]
FEATURE [Part::Cut] Cut282
  Base = -> Cut281
  Tool = -> Compound505
FEATURE [Part::Fillet] Fillet006
  Base = -> Cut199
  Edges = 2 edges r=3: [Edge13,Edge87]
FEATURE [Part::Chamfer] Chamfer011
  Base = -> Cut269
  Edges = 2 edges r=2: [Edge4,Edge79]
FEATURE [Part::Chamfer] Chamfer012
  Base = -> Chamfer011
  Edges = 2 edges r=2: [Edge2,Edge70]
FEATURE [Part::Compound] Compound618  label="J-max_arm-rotator"
  Links = -> [Cut284,Cut282,Fillet006,Chamfer012]
  Placement = pos=(52,12,-88) rot=(0,0.707107,-0.707107;3.14159rad)
FEATURE [Part::Box] Box233  label="Krychle233"
  AttacherType = Attacher::AttachEngine3D
  Height = 100
  Length = 200
  Placement = pos=(-60,-124,-90) rot=(0,0,1;0rad)
  Width = 100
FEATURE [Part::Cut] Cut285
  Base = -> Cut251
  Tool = -> Box233
FEATURE [Part::Chamfer] Chamfer036
  Base = -> Cut255
  Edges = 1 edges r=4: [Edge3]
FEATURE [Part::Box] Box234  label="Krychle234"
  AttacherType = Attacher::AttachEngine3D
  Height = 100
  Length = 200
  Placement = pos=(-60,44,-90) rot=(0,0,1;0rad)
  Width = 100
FEATURE [Part::Cut] Cut286
  Base = -> Cut256
  Tool = -> Box234
FEATURE [Part::Box] Box235  label="Krychle235"
  AttacherType = Attacher::AttachEngine3D
  Height = 100
  Length = 200
  Placement = pos=(-60,44,-90) rot=(0,0,1;0rad)
  Width = 100
FEATURE [Part::Cut] Cut287
  Base = -> Cut285
  Tool = -> Box235
FEATURE [Part::Cylinder] Cylinder1228  label="Válec1228"
  Angle = 360
  AttacherType = Attacher::AttachEngine3D
  Height = 100
  Placement = pos=(90,0,-60) rot=(0,0,1;0rad)
  Radius = 1.5
FEATURE [Part::Cylinder] Cylinder1229  label="Válec1229"
  Angle = 360
  AttacherType = Attacher::AttachEngine3D
  Height = 100
  Placement = pos=(14,0,-60) rot=(0,0,1;0rad)
  Radius = 1.5
FEATURE [Part::Box] Box236  label="Krychle236"
  AttacherType = Attacher::AttachEngine3D
  Height = 64
  Length = 6
  Placement = pos=(11,-3,-93) rot=(0,0,1;0rad)
  Width = 6
FEATURE [Part::Box] Box237  label="Krychle237"
  AttacherType = Attacher::AttachEngine3D
  Height = 64
  Length = 6
  Placement = pos=(87,-3,-93) rot=(0,0,1;0rad)
  Width = 6
FEATURE [Part::Cylinder] Cylinder1230  label="Válec1230"
  Angle = 360
  AttacherType = Attacher::AttachEngine3D
  Height = 100
  Placement = pos=(90,0,-18) rot=(0,0,1;0rad)
  Radius = 4
FEATURE [Part::Cylinder] Cylinder1231  label="Válec1231"
  Angle = 360
  AttacherType = Attacher::AttachEngine3D
  Height = 100
  Placement = pos=(14,0,-18) rot=(0,0,1;0rad)
  Radius = 4
FEATURE [Part::Box] Box238  label="Krychle238"
  AttacherType = Attacher::AttachEngine3D
  Height = 2
  Length = 6
  Placement = pos=(75,38,-22) rot=(0,0,1;0rad)
  Width = 6
FEATURE [Part::Box] Box239  label="Krychle239"
  AttacherType = Attacher::AttachEngine3D
  Height = 2
  Length = 6
  Placement = pos=(23,38,-22) rot=(0,0,1;0rad)
  Width = 6
FEATURE [Part::Cylinder] Cylinder1232  label="Válec1232"
  Angle = 360
  AttacherType = Attacher::AttachEngine3D
  Height = 32
  Placement = pos=(26,41,-42) rot=(0,0,1;0rad)
  Radius = 1.5
FEATURE [Part::Cylinder] Cylinder1233  label="Válec1233"
  Angle = 360
  AttacherType = Attacher::AttachEngine3D
  Height = 32
  Placement = pos=(78,41,-42) rot=(0,0,1;0rad)
  Radius = 1.5
FEATURE [Part::Compound] Compound619
  Links = -> [Box238,Box239]
FEATURE [Part::Compound] Compound620
  Links = -> [Cylinder1232,Cylinder1233]
FEATURE [Part::Cylinder] Cylinder1234  label="Válec1234"
  Angle = 360
  AttacherType = Attacher::AttachEngine3D
  Height = 32
  Placement = pos=(26,41,-46) rot=(0,0,1;0rad)
  Radius = 1.5
FEATURE [Part::Cylinder] Cylinder1235  label="Válec1235"
  Angle = 360
  AttacherType = Attacher::AttachEngine3D
  Height = 32
  Placement = pos=(78,41,-46) rot=(0,0,1;0rad)
  Radius = 1.5
FEATURE [Part::Compound] Compound621
  Links = -> [Cylinder1234,Cylinder1235]
FEATURE [Part::Cut] Cut288
  Base = -> Cut287
  Tool = -> Compound620
FEATURE [Part::Cut] Cut289
  Base = -> Cut286
  Tool = -> Compound619
FEATURE [Part::Cut] Cut290
  Base = -> Cut289
  Tool = -> Compound621
FEATURE [Part::Compound] Compound622  label="srouby_troj_silne"
  Links = -> [Cylinder1230,Cylinder1231]
FEATURE [Part::Compound] Compound623  label="srouby_troj"
  Links = -> [Cylinder1228,Cylinder1229]
FEATURE [Part::Cylinder] Cylinder1236  label="Válec1236"
  Angle = 360
  AttacherType = Attacher::AttachEngine3D
  Height = 100
  Placement = pos=(90,0,-18) rot=(0,0,1;0rad)
  Radius = 4
FEATURE [Part::Cylinder] Cylinder1237  label="Válec1237"
  Angle = 360
  AttacherType = Attacher::AttachEngine3D
  Height = 100
  Placement = pos=(14,0,-18) rot=(0,0,1;0rad)
  Radius = 4
FEATURE [Part::Compound] Compound624  label="srouby_troj_silne001"
  Links = -> [Cylinder1236,Cylinder1237]
FEATURE [Part::Cylinder] Cylinder1238  label="Válec1238"
  Angle = 360
  AttacherType = Attacher::AttachEngine3D
  Height = 100
  Placement = pos=(90,0,-60) rot=(0,0,1;0rad)
  Radius = 1.5
FEATURE [Part::Cylinder] Cylinder1239  label="Válec1239"
  Angle = 360
  AttacherType = Attacher::AttachEngine3D
  Height = 100
  Placement = pos=(14,0,-60) rot=(0,0,1;0rad)
  Radius = 1.5
FEATURE [Part::Compound] Compound625  label="srouby_troj001"
  Links = -> [Cylinder1238,Cylinder1239]
FEATURE [Part::Cut] Cut291
  Base = -> Cut288
  Tool = -> Compound625
FEATURE [Part::Cylinder] Cylinder1240  label="Válec1240"
  Angle = 360
  AttacherType = Attacher::AttachEngine3D
  Height = 100
  Placement = pos=(90,0,-18) rot=(0,0,1;0rad)
  Radius = 4
FEATURE [Part::Cylinder] Cylinder1241  label="Válec1241"
  Angle = 360
  AttacherType = Attacher::AttachEngine3D
  Height = 100
  Placement = pos=(14,0,-18) rot=(0,0,1;0rad)
  Radius = 4
FEATURE [Part::Compound] Compound626  label="srouby_troj_silne002"
  Links = -> [Cylinder1240,Cylinder1241]
FEATURE [Part::Cut] Cut292
  Base = -> Cut290
  Tool = -> Compound623
FEATURE [Part::Cut] Cut293
  Base = -> Cut292
  Tool = -> Compound622
FEATURE [Part::Cut] Cut294
  Base = -> Chamfer036
  Placement = pos=(0,0,4) rot=(0,0,1;0rad)
  Tool = -> Compound624
FEATURE [Part::Compound] Compound627
  Links = -> [Box236,Box237]
FEATURE [Part::Chamfer] Chamfer037
  Base = -> Cut293
  Edges = 2 edges r=6: [Edge40,Edge42]
FEATURE [Sketcher::SketchObject] Sketch004
  FullyConstrained = false
  MapMode = 5
  Support = -> [XY_Plane002]
  sketch-geometry (5):
    g0: LineSegment StartX=-51.8839 StartY=28.0157 StartZ=0 EndX=-8.82571 EndY=110.528 EndZ=0
    g1: LineSegment StartX=-8.82571 StartY=110.528 StartZ=0 EndX=8.88346 EndY=110.528 EndZ=0
    g2: LineSegment StartX=8.88346 StartY=110.528 StartZ=0 EndX=51.7746 EndY=28.1985 EndZ=0
    g3: LineSegment StartX=51.7746 StartY=28.1985 StartZ=0 EndX=0 EndY=55.1408 EndZ=0
    g4: LineSegment StartX=0 StartY=55.1408 StartZ=0 EndX=-51.8839 EndY=28.0157 EndZ=0
  constraints (7):
    c: Coincident(g0,g1)
    c: Horizontal(g1)
    c: Coincident(g1,g2)
    c: Coincident(g2,g3)
    c: PointOnObject(g3,g-2)
    c: Coincident(g3,g4)
    c: Coincident(g4,g0)
FEATURE [PartDesign::Pad] Pad002
  Direction = (1,1,1)
  Length = 10
  Length2 = 100
  Profile = -> Sketch004
  Type = 0
FEATURE [Part::Box] Box139  label="Krychle139"
  AttacherType = Attacher::AttachEngine3D
  Height = 32
  Length = 200
  Placement = pos=(-100,-124,0) rot=(0,0,1;0rad)
  Width = 100
FEATURE [Part::Cylinder] Cylinder1242  label="Válec1242"
  Angle = 360
  AttacherType = Attacher::AttachEngine3D
  Height = 10
  Placement = pos=(0,106,0) rot=(0,0,1;0rad)
  Radius = 10
FEATURE [Part::Box] Box140  label="Krychle140"
  AttacherType = Attacher::AttachEngine3D
  Height = 10
  Length = 10
  Placement = pos=(32,-24,0) rot=(0,0,1;0rad)
  Width = 52
FEATURE [Part::Cylinder] Cylinder1243  label="Válec1243"
  Angle = 360
  AttacherType = Attacher::AttachEngine3D
  Height = 100
  Placement = pos=(51,-12,0) rot=(0,0,1;0rad)
  Radius = 1.5
FEATURE [Part::Cylinder] Cylinder1261  label="Válec1261"
  Angle = 360
  AttacherType = Attacher::AttachEngine3D
  Height = 100
  Placement = pos=(14,0,-60) rot=(0,0,1;0rad)
  Radius = 1.5
FEATURE [Part::Cylinder] Cylinder1260  label="Válec1260"
  Angle = 360
  AttacherType = Attacher::AttachEngine3D
  Height = 100
  Placement = pos=(90,0,-60) rot=(0,0,1;0rad)
  Radius = 1.5
FEATURE [Part::Box] Box141  label="Krychle141"
  AttacherType = Attacher::AttachEngine3D
  Height = 10
  Length = 10
  Placement = pos=(-42,-24,0) rot=(0,0,1;0rad)
  Width = 52
FEATURE [Part::Box] Box142  label="Krychle142"
  AttacherType = Attacher::AttachEngine3D
  Height = 10
  Length = 72
  Placement = pos=(-36,-24,0) rot=(0,0,1;0rad)
  Width = 70
FEATURE [Part::Cylinder] Cylinder1262  label="Válec1262"
  Angle = 360
  AttacherType = Attacher::AttachEngine3D
  Height = 100
  Placement = pos=(-51,-12,0) rot=(0,0,1;0rad)
  Radius = 1.5
FEATURE [Part::Compound] Compound651
  Links = -> [Cylinder1262,Cylinder1243]
FEATURE [Part::Cylinder] Cylinder1263  label="Válec1263"
  Angle = 360
  AttacherType = Attacher::AttachEngine3D
  Height = 32
  Placement = pos=(26,41,-42) rot=(0,0,1;0rad)
  Radius = 1.5
FEATURE [Part::FeaturePython] Tube001  # WARN: FeaturePython — macro-defined, semantics opaque (R4)
  AttacherType = Attacher::AttachEngine3D
  Height = 10
  InnerRadius = 40
  OuterRadius = 59
FEATURE [Part::Cylinder] Cylinder1258  label="Válec1258"
  Angle = 360
  AttacherType = Attacher::AttachEngine3D
  Height = 3
  Placement = pos=(26,41,-42) rot=(0,0,1;0rad)
  Radius = 3
FEATURE [Part::Cylinder] Cylinder1257  label="Válec1257"
  Angle = 360
  AttacherType = Attacher::AttachEngine3D
  Height = 32
  Placement = pos=(78,41,-42) rot=(0,0,1;0rad)
  Radius = 1.5
FEATURE [Part::Cylinder] Cylinder1264  label="Válec1264"
  Angle = 360
  AttacherType = Attacher::AttachEngine3D
  Height = 50
  Placement = pos=(-51,6,0) rot=(0,0,1;0rad)
  Radius = 1.5
FEATURE [Part::Cylinder] Cylinder1256  label="Válec1256"
  Angle = 360
  AttacherType = Attacher::AttachEngine3D
  Height = 32
  Placement = pos=(26,41,-42) rot=(0,0,1;0rad)
  Radius = 1.5
FEATURE [Part::Compound] Compound641
  Links = -> [Cylinder1256,Cylinder1257]
  Placement = pos=(-52,0,36) rot=(0,0,1;0rad)
FEATURE [Part::Cylinder] Cylinder1259  label="Válec1259"
  Angle = 360
  AttacherType = Attacher::AttachEngine3D
  Height = 3
  Placement = pos=(78,41,-42) rot=(0,0,1;0rad)
  Radius = 3
FEATURE [Part::Cut] Cut296
  Base = -> Tube001
  Tool = -> Box139
FEATURE [PartDesign::Body] Body002
  Group = -> [Sketch004,Pad002]
  Origin = -> Origin002
  Tip = -> Pad002
FEATURE [Part::Cylinder] Cylinder1255  label="Válec1255"
  Angle = 360
  AttacherType = Attacher::AttachEngine3D
  Height = 100
  Placement = pos=(14,0,-60) rot=(0,0,1;0rad)
  Radius = 1.5
FEATURE [Part::Cylinder] Cylinder1265  label="Válec1265"
  Angle = 360
  AttacherType = Attacher::AttachEngine3D
  Height = 50
  Placement = pos=(51,6,0) rot=(0,0,1;0rad)
  Radius = 1.5
FEATURE [Part::Cylinder] Cylinder1266  label="Válec1266"
  Angle = 360
  AttacherType = Attacher::AttachEngine3D
  Height = 50
  Placement = pos=(-24,18,0) rot=(0,0,1;0rad)
  Radius = 1.5
FEATURE [Part::Cylinder] Cylinder1248  label="Válec1248"
  Angle = 360
  AttacherType = Attacher::AttachEngine3D
  Height = 50
  Placement = pos=(-51,6,0) rot=(0,0,1;0rad)
  Radius = 1.5
FEATURE [Part::Cylinder] Cylinder1247  label="Válec1247"
  Angle = 360
  AttacherType = Attacher::AttachEngine3D
  Height = 100
  Placement = pos=(-51,-12,0) rot=(0,0,1;0rad)
  Radius = 1.5
FEATURE [Part::Cylinder] Cylinder1246  label="Válec1246"
  Angle = 360
  AttacherType = Attacher::AttachEngine3D
  Height = 100
  Placement = pos=(51,-12,0) rot=(0,0,1;0rad)
  Radius = 1.5
FEATURE [Part::Cylinder] Cylinder1254  label="Válec1254"
  Angle = 360
  AttacherType = Attacher::AttachEngine3D
  Height = 100
  Placement = pos=(90,0,-60) rot=(0,0,1;0rad)
  Radius = 1.5
FEATURE [Part::Compound] Compound640  label="srouby_troj002"
  Links = -> [Cylinder1254,Cylinder1255]
  Placement = pos=(-52,0,0) rot=(0,0,1;0rad)
FEATURE [Part::Compound] Compound639
  Links = -> [Compound640,Compound641]
FEATURE [Part::Cylinder] Cylinder556  label="Válec556"
  Angle = 360
  AttacherType = Attacher::AttachEngine3D
  Height = 50
  Placement = pos=(24,18,0) rot=(0,0,1;0rad)
  Radius = 1.5
FEATURE [Part::Compound] Compound652
  Links = -> [Cylinder1265,Cylinder1264,Cylinder1266,Cylinder556]
FEATURE [Part::Cylinder] Cylinder563  label="Válec563"
  Angle = 360
  AttacherType = Attacher::AttachEngine3D
  Height = 4
  Placement = pos=(-7,-34,73) rot=(1,0,0;1.5708rad)
  Radius = 3
FEATURE [Part::Cylinder] Cylinder564  label="Válec564"
  Angle = 360
  AttacherType = Attacher::AttachEngine3D
  Height = 20
  Placement = pos=(7,-34,37) rot=(1,0,0;1.5708rad)
  Radius = 1.5
FEATURE [Part::Cylinder] Cylinder565  label="Válec565"
  Angle = 360
  AttacherType = Attacher::AttachEngine3D
  Height = 20
  Placement = pos=(7,-34,73) rot=(1,0,0;1.5708rad)
  Radius = 1.5
FEATURE [Part::Cylinder] Cylinder566  label="Válec566"
  Angle = 360
  AttacherType = Attacher::AttachEngine3D
  Height = 20
  Placement = pos=(-7,-34,37) rot=(1,0,0;1.5708rad)
  Radius = 1.5
FEATURE [Part::Cylinder] Cylinder567  label="Válec567"
  Angle = 360
  AttacherType = Attacher::AttachEngine3D
  Height = 20
  Placement = pos=(-7,-34,73) rot=(1,0,0;1.5708rad)
  Radius = 1.5
FEATURE [Part::Compound] Compound333
  Links = -> [Cylinder564,Cylinder566,Cylinder565,Cylinder567]
  Placement = pos=(0,141,45) rot=(1,0,0;1.5708rad)
FEATURE [Part::Cut] Cut297
  Base = -> Cylinder1242
  Tool = -> Compound333
FEATURE [Part::Cylinder] Cylinder568  label="Válec568"
  Angle = 360
  AttacherType = Attacher::AttachEngine3D
  Height = 4
  Placement = pos=(-7,-34,37) rot=(1,0,0;1.5708rad)
  Radius = 3
FEATURE [Part::Cylinder] Cylinder569  label="Válec569"
  Angle = 360
  AttacherType = Attacher::AttachEngine3D
  Height = 4
  Placement = pos=(7,-34,73) rot=(1,0,0;1.5708rad)
  Radius = 3
FEATURE [Part::Cylinder] Cylinder570  label="Válec570"
  Angle = 360
  AttacherType = Attacher::AttachEngine3D
  Height = 4
  Placement = pos=(7,-34,37) rot=(1,0,0;1.5708rad)
  Radius = 3
FEATURE [Part::Compound] Compound332
  Links = -> [Cylinder570,Cylinder568,Cylinder569,Cylinder563]
  Placement = pos=(0,141,45) rot=(1,0,0;1.5708rad)
FEATURE [Part::Cut] Cut298
  Base = -> Cut297
  Tool = -> Compound332
FEATURE [Part::Cylinder] Cylinder575  label="Válec575"
  Angle = 360
  AttacherType = Attacher::AttachEngine3D
  Height = 4
  Placement = pos=(7,-34,37) rot=(1,0,0;1.5708rad)
  Radius = 3
FEATURE [Part::Cylinder] Cylinder576  label="Válec576"
  Angle = 360
  AttacherType = Attacher::AttachEngine3D
  Height = 20
  Placement = pos=(-7,-34,37) rot=(1,0,0;1.5708rad)
  Radius = 1.5
FEATURE [Part::Cylinder] Cylinder577  label="Válec577"
  Angle = 360
  AttacherType = Attacher::AttachEngine3D
  Height = 20
  Placement = pos=(7,-34,37) rot=(1,0,0;1.5708rad)
  Radius = 1.5
FEATURE [Part::Cylinder] Cylinder578  label="Válec578"
  Angle = 360
  AttacherType = Attacher::AttachEngine3D
  Height = 20
  Placement = pos=(7,-34,73) rot=(1,0,0;1.5708rad)
  Radius = 1.5
FEATURE [Part::Cylinder] Cylinder579  label="Válec579"
  Angle = 360
  AttacherType = Attacher::AttachEngine3D
  Height = 20
  Placement = pos=(-7,-34,73) rot=(1,0,0;1.5708rad)
  Radius = 1.5
FEATURE [Part::Compound] Compound653
  Links = -> [Cylinder577,Cylinder576,Cylinder578,Cylinder579]
  Placement = pos=(0,141,45) rot=(1,0,0;1.5708rad)
FEATURE [Part::Compound] Compound341
  Links = -> [Box140,Box141]
FEATURE [Part::Compound] Compound642
  Links = -> [Cylinder1258,Cylinder1259]
  Placement = pos=(-52,0,42) rot=(0,0,1;0rad)
FEATURE [Part::Cylinder] Cylinder580  label="Válec580"
  Angle = 360
  AttacherType = Attacher::AttachEngine3D
  Height = 4
  Placement = pos=(-7,-34,73) rot=(1,0,0;1.5708rad)
  Radius = 3
FEATURE [Part::Cylinder] Cylinder581  label="Válec581"
  Angle = 360
  AttacherType = Attacher::AttachEngine3D
  Height = 4
  Placement = pos=(-7,-34,37) rot=(1,0,0;1.5708rad)
  Radius = 3
FEATURE [Part::Cylinder] Cylinder582  label="Válec582"
  Angle = 360
  AttacherType = Attacher::AttachEngine3D
  Height = 4
  Placement = pos=(7,-34,73) rot=(1,0,0;1.5708rad)
  Radius = 3
FEATURE [Part::Compound] Compound654
  Links = -> [Cylinder575,Cylinder581,Cylinder582,Cylinder580]
  Placement = pos=(0,141,45) rot=(1,0,0;1.5708rad)
FEATURE [Part::Cylinder] Cylinder583  label="Válec583"
  Angle = 360
  AttacherType = Attacher::AttachEngine3D
  Height = 100
  Placement = pos=(39,-21,0) rot=(0,0,1;0rad)
  Radius = 1.5
FEATURE [Part::Cylinder] Cylinder584  label="Válec584"
  Angle = 360
  AttacherType = Attacher::AttachEngine3D
  Height = 100
  Placement = pos=(-39,-21,0) rot=(0,0,1;0rad)
  Radius = 1.5
FEATURE [Part::Compound] Compound655
  Links = -> [Cylinder584,Cylinder583]
FEATURE [Part::Compound] Compound650
  Links = -> [Compound655,Compound652,Compound651]
  Placement = pos=(0,0,-10) rot=(0,0,1;0rad)
FEATURE [Part::Cylinder] Cylinder585  label="Válec585"
  Angle = 360
  AttacherType = Attacher::AttachEngine3D
  Height = 100
  Placement = pos=(-39,-21,0) rot=(0,0,1;0rad)
  Radius = 1.5
FEATURE [Part::Cylinder] Cylinder586  label="Válec586"
  Angle = 360
  AttacherType = Attacher::AttachEngine3D
  Height = 100
  Placement = pos=(39,-21,0) rot=(0,0,1;0rad)
  Radius = 1.5
FEATURE [Part::Compound] Compound656
  Links = -> [Cylinder585,Cylinder586]
FEATURE [Part::Cut] Cut295
  Base = -> Compound341
  Tool = -> Compound656
FEATURE [Part::Compound] Compound636
  Links = -> [Cylinder1247,Cylinder1246]
FEATURE [Part::Box] Box240  label="Krychle240"
  AttacherType = Attacher::AttachEngine3D
  Height = 64
  Length = 6
  Placement = pos=(11,-3,-93) rot=(0,0,1;0rad)
  Width = 6
FEATURE [Part::Box] Box241  label="Krychle241"
  AttacherType = Attacher::AttachEngine3D
  Height = 64
  Length = 6
  Placement = pos=(87,-3,-93) rot=(0,0,1;0rad)
  Width = 6
FEATURE [Part::Compound] Compound657
  Links = -> [Box240,Box241]
  Placement = pos=(-52,0,36) rot=(0,0,1;0rad)
FEATURE [Part::Cylinder] Cylinder1267  label="Válec1267"
  Angle = 360
  AttacherType = Attacher::AttachEngine3D
  Height = 100
  Placement = pos=(90,0,-60) rot=(0,0,1;0rad)
  Radius = 1.5
FEATURE [Part::Cylinder] Cylinder1268  label="Válec1268"
  Angle = 360
  AttacherType = Attacher::AttachEngine3D
  Height = 100
  Placement = pos=(14,0,-60) rot=(0,0,1;0rad)
  Radius = 1.5
FEATURE [Part::Compound] Compound658  label="srouby_troj005"
  Links = -> [Cylinder1267,Cylinder1268]
  Placement = pos=(-52,0,0) rot=(0,0,1;0rad)
FEATURE [Part::Cylinder] Cylinder1269  label="Válec1269"
  Angle = 360
  AttacherType = Attacher::AttachEngine3D
  Height = 32
  Placement = pos=(26,41,-42) rot=(0,0,1;0rad)
  Radius = 1.5
FEATURE [Part::Cylinder] Cylinder1270  label="Válec1270"
  Angle = 360
  AttacherType = Attacher::AttachEngine3D
  Height = 32
  Placement = pos=(78,41,-42) rot=(0,0,1;0rad)
  Radius = 1.5
FEATURE [Part::Compound] Compound659
  Links = -> [Cylinder1269,Cylinder1270]
  Placement = pos=(-52,0,36) rot=(0,0,1;0rad)
FEATURE [Part::Compound] Compound630
  Links = -> [Compound658,Compound659]
FEATURE [Part::Cylinder] Cylinder1271  label="Válec1271"
  Angle = 360
  AttacherType = Attacher::AttachEngine3D
  Height = 100
  Placement = pos=(90,0,-60) rot=(0,0,1;0rad)
  Radius = 1.5
FEATURE [Part::Cylinder] Cylinder1272  label="Válec1272"
  Angle = 360
  AttacherType = Attacher::AttachEngine3D
  Height = 100
  Placement = pos=(14,0,-60) rot=(0,0,1;0rad)
  Radius = 1.5
FEATURE [Part::Compound] Compound648  label="srouby_troj004"
  Links = -> [Cylinder1271,Cylinder1272]
  Placement = pos=(-52,0,0) rot=(0,0,1;0rad)
FEATURE [Part::Cylinder] Cylinder1273  label="Válec1273"
  Angle = 360
  AttacherType = Attacher::AttachEngine3D
  Height = 3
  Placement = pos=(26,41,-42) rot=(0,0,1;0rad)
  Radius = 3
FEATURE [Part::Cylinder] Cylinder1274  label="Válec1274"
  Angle = 360
  AttacherType = Attacher::AttachEngine3D
  Height = 3
  Placement = pos=(78,41,-42) rot=(0,0,1;0rad)
  Radius = 3
FEATURE [Part::Compound] Compound633
  Links = -> [Cylinder1273,Cylinder1274]
  Placement = pos=(-52,0,42) rot=(0,0,1;0rad)
FEATURE [Part::Compound] Compound644  label="srouby_troj003"
  Links = -> [Cylinder1260,Cylinder1261]
  Placement = pos=(-52,0,0) rot=(0,0,1;0rad)
FEATURE [Part::Cut] Cut299
  Base = -> Body002
  Tool = -> Compound653
FEATURE [Part::Cut] Cut300
  Base = -> Cut299
  Tool = -> Compound654
FEATURE [Part::Cut] Cut304
  Base = -> Cut300
  Tool = -> Compound642
FEATURE [Part::Cut] Cut308
  Base = -> Box142
  Tool = -> Compound650
FEATURE [Part::Cylinder] Cylinder1244  label="Válec1244"
  Angle = 360
  AttacherType = Attacher::AttachEngine3D
  Height = 3
  Placement = pos=(26,41,-42) rot=(0,0,1;0rad)
  Radius = 3
FEATURE [Part::Cylinder] Cylinder1245  label="Válec1245"
  Angle = 360
  AttacherType = Attacher::AttachEngine3D
  Height = 3
  Placement = pos=(78,41,-42) rot=(0,0,1;0rad)
  Radius = 3
FEATURE [Part::Compound] Compound634
  Links = -> [Cylinder1244,Cylinder1245]
  Placement = pos=(-52,0,42) rot=(0,0,1;0rad)
FEATURE [Part::Cylinder] Cylinder1249  label="Válec1249"
  Angle = 360
  AttacherType = Attacher::AttachEngine3D
  Height = 50
  Placement = pos=(51,6,0) rot=(0,0,1;0rad)
  Radius = 1.5
FEATURE [Part::Cylinder] Cylinder1250  label="Válec1250"
  Angle = 360
  AttacherType = Attacher::AttachEngine3D
  Height = 50
  Placement = pos=(-24,18,0) rot=(0,0,1;0rad)
  Radius = 1.5
FEATURE [Part::Cylinder] Cylinder1251  label="Válec1251"
  Angle = 360
  AttacherType = Attacher::AttachEngine3D
  Height = 50
  Placement = pos=(24,18,0) rot=(0,0,1;0rad)
  Radius = 1.5
FEATURE [Part::Compound] Compound637
  Links = -> [Cylinder1249,Cylinder1248,Cylinder1250,Cylinder1251]
FEATURE [Part::Cylinder] Cylinder1252  label="Válec1252"
  Angle = 360
  AttacherType = Attacher::AttachEngine3D
  Height = 100
  Placement = pos=(39,-21,0) rot=(0,0,1;0rad)
  Radius = 1.5
FEATURE [Part::Cylinder] Cylinder1253  label="Válec1253"
  Angle = 360
  AttacherType = Attacher::AttachEngine3D
  Height = 100
  Placement = pos=(-39,-21,0) rot=(0,0,1;0rad)
  Radius = 1.5
FEATURE [Part::Compound] Compound638
  Links = -> [Cylinder1253,Cylinder1252]
FEATURE [Part::Compound] Compound635
  Links = -> [Compound638,Compound637,Compound636]
  Placement = pos=(0,0,-10) rot=(0,0,1;0rad)
FEATURE [Part::Cut] Cut301
  Base = -> Cut296
  Tool = -> Compound635
FEATURE [Part::Cut] Cut302
  Base = -> Cut301
  Tool = -> Compound639
FEATURE [Part::Cut] Cut303
  Base = -> Cut302
  Tool = -> Compound633
FEATURE [Part::Cut] Cut305
  Base = -> Cut303
  Tool = -> Compound657
FEATURE [Part::Cut] Cut309
  Base = -> Cut308
  Tool = -> Compound634
FEATURE [Part::Cut] Cut310
  Base = -> Cut309
  Tool = -> Compound630
FEATURE [Part::Cylinder] Cylinder1275  label="Válec1275"
  Angle = 360
  AttacherType = Attacher::AttachEngine3D
  Height = 32
  Placement = pos=(78,41,-42) rot=(0,0,1;0rad)
  Radius = 1.5
FEATURE [Part::Compound] Compound645
  Links = -> [Cylinder1263,Cylinder1275]
  Placement = pos=(-52,0,36) rot=(0,0,1;0rad)
FEATURE [Part::Compound] Compound643
  Links = -> [Compound644,Compound645]
FEATURE [Part::Cut] Cut306
  Base = -> Cut295
  Tool = -> Compound643
FEATURE [Part::Box] Box242  label="Krychle242"
  AttacherType = Attacher::AttachEngine3D
  Height = 64
  Length = 6
  Placement = pos=(11,-3,-93) rot=(0,0,1;0rad)
  Width = 6
FEATURE [Part::Box] Box243  label="Krychle243"
  AttacherType = Attacher::AttachEngine3D
  Height = 64
  Length = 6
  Placement = pos=(87,-3,-93) rot=(0,0,1;0rad)
  Width = 6
FEATURE [Part::Compound] Compound646
  Links = -> [Box242,Box243]
  Placement = pos=(-52,0,36) rot=(0,0,1;0rad)
FEATURE [Part::Cut] Cut307
  Base = -> Cut306
  Tool = -> Compound646
FEATURE [Part::Cylinder] Cylinder1276  label="Válec1276"
  Angle = 360
  AttacherType = Attacher::AttachEngine3D
  Height = 32
  Placement = pos=(26,41,-42) rot=(0,0,1;0rad)
  Radius = 1.5
FEATURE [Part::Cylinder] Cylinder1277  label="Válec1277"
  Angle = 360
  AttacherType = Attacher::AttachEngine3D
  Height = 32
  Placement = pos=(78,41,-42) rot=(0,0,1;0rad)
  Radius = 1.5
FEATURE [Part::Compound] Compound649
  Links = -> [Cylinder1276,Cylinder1277]
  Placement = pos=(-52,0,36) rot=(0,0,1;0rad)
FEATURE [Part::Compound] Compound647
  Links = -> [Compound648,Compound649]
FEATURE [Part::Cut] Cut311
  Base = -> Cut304
  Tool = -> Compound647
FEATURE [Part::Cylinder] Cylinder1278  label="Válec1278"
  Angle = 360
  AttacherType = Attacher::AttachEngine3D
  Height = 52
  Placement = pos=(0,13,-53) rot=(1,0,0;1.5708rad)
  Radius = 60
FEATURE [Part::Box] Box244  label="Krychle244"
  AttacherType = Attacher::AttachEngine3D
  Height = 64
  Length = 6
  Placement = pos=(11,-3,-93) rot=(0,0,1;0rad)
  Width = 6
FEATURE [Part::Box] Box245  label="Krychle245"
  AttacherType = Attacher::AttachEngine3D
  Height = 64
  Length = 6
  Placement = pos=(87,-3,-93) rot=(0,0,1;0rad)
  Width = 6
FEATURE [Part::Compound] Compound660
  Links = -> [Box244,Box245]
  Placement = pos=(-52,0,36) rot=(0,0,1;0rad)
FEATURE [Part::Cut] Cut312
  Base = -> Cut310
  Tool = -> Cylinder1278
FEATURE [Part::Cut] Cut313
  Base = -> Cut312
  Tool = -> Compound660
FEATURE [Part::Compound] Compound661  label="bazovina_part-A_triangle-support"
  Links = -> [Cut313,Cut298,Cut305,Cut307,Cut311]
  Placement = pos=(52,0,-36) rot=(0,0,1;0rad)
FEATURE [Part::Compound] Compound662  label="bazovina_neck_foreshift"
  Links = -> [Cut291,Cut294,Chamfer037]
FEATURE [Sketcher::SketchObject] Sketch005
  FullyConstrained = false
  sketch-geometry (1):
    g0: Circle CenterX=-186.411 CenterY=73.9277 CenterZ=0 NormalX=0 NormalY=0 NormalZ=1 AngleXU=0 Radius=59
FEATURE [Part::Extrusion] Extrude002
  Base = -> Sketch005
  Dir = (52,0,32)
  DirMode = 0
  FaceMakerClass = Part::FaceMakerBullseye
  LengthFwd = 61
  LengthRev = 0
  Placement = pos=(-134,74,-22) rot=(0,0,1;3.14159rad)
  Solid = true
  Symmetric = false
FEATURE [Part::Cylinder] Cylinder1279  label="Válec1279"
  Angle = 360
  AttacherType = Attacher::AttachEngine3D
  Height = 100
  Placement = pos=(1,6,-60) rot=(0,0,1;0rad)
  Radius = 1.5
FEATURE [Part::Cylinder] Cylinder1280  label="Válec1280"
  Angle = 360
  AttacherType = Attacher::AttachEngine3D
  Height = 40
  Placement = pos=(1,-12,-18) rot=(0,0,1;0rad)
  Radius = 4
FEATURE [Part::Cylinder] Cylinder1281  label="Válec1281"
  Angle = 360
  AttacherType = Attacher::AttachEngine3D
  Height = 100
  Placement = pos=(1,-12,-60) rot=(0,0,1;0rad)
  Radius = 1.5
FEATURE [Part::Cylinder] Cylinder1282  label="Válec1282"
  Angle = 360
  AttacherType = Attacher::AttachEngine3D
  Height = 20
  Placement = pos=(103,6,-20) rot=(0,0,1;0rad)
  Radius = 4
FEATURE [Part::Cylinder] Cylinder1283  label="Válec1283"
  Angle = 360
  AttacherType = Attacher::AttachEngine3D
  Height = 100
  Placement = pos=(36,34,-60) rot=(0,0,1;0rad)
  Radius = 1.5
FEATURE [Part::Cylinder] Cylinder1284  label="Válec1284"
  Angle = 360
  AttacherType = Attacher::AttachEngine3D
  Height = 100
  Placement = pos=(-36,-34,-90) rot=(0,0,1;0rad)
  Radius = 4
FEATURE [Part::Cylinder] Cylinder1285  label="Válec1285"
  Angle = 360
  AttacherType = Attacher::AttachEngine3D
  Height = 100
  Placement = pos=(13,-21,-60) rot=(0,0,1;0rad)
  Radius = 1.5
FEATURE [Part::Cylinder] Cylinder1286  label="Válec1286"
  Angle = 360
  AttacherType = Attacher::AttachEngine3D
  Height = 100
  Placement = pos=(28,18,-60) rot=(0,0,1;0rad)
  Radius = 1.5
FEATURE [Part::Cylinder] Cylinder1287  label="Válec1287"
  Angle = 360
  AttacherType = Attacher::AttachEngine3D
  Height = 100
  Placement = pos=(-36,-34,-90) rot=(0,0,1;0rad)
  Radius = 4
FEATURE [Part::Cylinder] Cylinder1288  label="Válec1288"
  Angle = 360
  AttacherType = Attacher::AttachEngine3D
  Height = 40
  Placement = pos=(28,18,-18) rot=(0,0,1;0rad)
  Radius = 4
FEATURE [Part::Cylinder] Cylinder1289  label="Válec1289"
  Angle = 360
  AttacherType = Attacher::AttachEngine3D
  Height = 20
  Placement = pos=(76,18,-18) rot=(0,0,1;0rad)
  Radius = 4
FEATURE [Part::Cylinder] Cylinder1290  label="Válec1290"
  Angle = 360
  AttacherType = Attacher::AttachEngine3D
  Height = 100
  Placement = pos=(103,-12,-60) rot=(0,0,1;0rad)
  Radius = 1.5
FEATURE [Part::Cylinder] Cylinder1291  label="Válec1291"
  Angle = 360
  AttacherType = Attacher::AttachEngine3D
  Height = 40
  Placement = pos=(13,-21,-18) rot=(0,0,1;0rad)
  Radius = 4
FEATURE [Part::Cylinder] Cylinder1292  label="Válec1292"
  Angle = 360
  AttacherType = Attacher::AttachEngine3D
  Height = 20
  Placement = pos=(103,6,-20) rot=(0,0,1;0rad)
  Radius = 4
FEATURE [Part::Cylinder] Cylinder1293  label="Válec1293"
  Angle = 360
  AttacherType = Attacher::AttachEngine3D
  Height = 20
  Placement = pos=(91,-21,-18) rot=(0,0,1;0rad)
  Radius = 4
FEATURE [Part::Cylinder] Cylinder1294  label="Válec1294"
  Angle = 360
  AttacherType = Attacher::AttachEngine3D
  Height = 100
  Placement = pos=(36,-34,-90) rot=(0,0,1;0rad)
  Radius = 4
FEATURE [Part::Cylinder] Cylinder1295  label="Válec1295"
  Angle = 360
  AttacherType = Attacher::AttachEngine3D
  Height = 40
  Placement = pos=(1,6,-18) rot=(0,0,1;0rad)
  Radius = 4
FEATURE [Part::Cylinder] Cylinder1296  label="Válec1296"
  Angle = 360
  AttacherType = Attacher::AttachEngine3D
  Height = 20
  Placement = pos=(103,-12,-20) rot=(0,0,1;0rad)
  Radius = 4
FEATURE [Part::Cylinder] Cylinder1297  label="Válec1297"
  Angle = 360
  AttacherType = Attacher::AttachEngine3D
  Height = 40
  Placement = pos=(1,6,-18) rot=(0,0,1;0rad)
  Radius = 4
FEATURE [Part::Cylinder] Cylinder1298  label="Válec1298"
  Angle = 360
  AttacherType = Attacher::AttachEngine3D
  Height = 100
  Placement = pos=(36,34,-90) rot=(0,0,1;0rad)
  Radius = 4
FEATURE [Part::Box] Box246  label="Krychle246"
  AttacherType = Attacher::AttachEngine3D
  Height = 100
  Length = 200
  Placement = pos=(-60,-130,-90) rot=(0,0,1;0rad)
  Width = 100
FEATURE [Part::Cylinder] Cylinder1299  label="Válec1299"
  Angle = 360
  AttacherType = Attacher::AttachEngine3D
  Height = 100
  Placement = pos=(50,0,-90) rot=(0,0,1;0rad)
  Radius = 4
FEATURE [Part::Cylinder] Cylinder1300  label="Válec1300"
  Angle = 360
  AttacherType = Attacher::AttachEngine3D
  Height = 100
  Placement = pos=(-36,34,-90) rot=(0,0,1;0rad)
  Radius = 4
FEATURE [Part::Cylinder] Cylinder1301  label="Válec1301"
  Angle = 360
  AttacherType = Attacher::AttachEngine3D
  Height = 100
  Placement = pos=(50,0,-90) rot=(0,0,1;0rad)
  Radius = 4
FEATURE [Part::Cylinder] Cylinder1302  label="Válec1302"
  Angle = 360
  AttacherType = Attacher::AttachEngine3D
  Height = 100
  Placement = pos=(14,0,-60) rot=(0,0,1;0rad)
  Radius = 1.5
FEATURE [Part::Cylinder] Cylinder1303  label="Válec1303"
  Angle = 360
  AttacherType = Attacher::AttachEngine3D
  Height = 20
  Placement = pos=(103,-12,-20) rot=(0,0,1;0rad)
  Radius = 4
FEATURE [Part::Compound] Compound663  label="srouby_monoblok_silne003"
  Links = -> [Cylinder1303,Cylinder1292,Cylinder1289,Cylinder1293,Cylinder1291,Cylinder1288,Cylinder1280,Cylinder1295]
FEATURE [Part::Cylinder] Cylinder1304  label="Válec1304"
  Angle = 360
  AttacherType = Attacher::AttachEngine3D
  Height = 100
  Placement = pos=(36,-34,-90) rot=(0,0,1;0rad)
  Radius = 4
FEATURE [Part::Cylinder] Cylinder1305  label="Válec1305"
  Angle = 360
  AttacherType = Attacher::AttachEngine3D
  Height = 100
  Placement = pos=(14,0,-18) rot=(0,0,1;0rad)
  Radius = 4
FEATURE [Part::Cylinder] Cylinder1306  label="Válec1306"
  Angle = 360
  AttacherType = Attacher::AttachEngine3D
  Height = 40
  Placement = pos=(13,-21,-18) rot=(0,0,1;0rad)
  Radius = 4
FEATURE [Part::Cylinder] Cylinder1307  label="Válec1307"
  Angle = 360
  AttacherType = Attacher::AttachEngine3D
  Height = 40
  Placement = pos=(1,-12,-18) rot=(0,0,1;0rad)
  Radius = 4
FEATURE [Part::Cylinder] Cylinder1308  label="Válec1308"
  Angle = 360
  AttacherType = Attacher::AttachEngine3D
  Height = 20
  Placement = pos=(76,18,-18) rot=(0,0,1;0rad)
  Radius = 4
FEATURE [Part::Cylinder] Cylinder1309  label="Válec1309"
  Angle = 360
  AttacherType = Attacher::AttachEngine3D
  Height = 100
  Placement = pos=(50,0,-60) rot=(0,0,1;0rad)
  Radius = 1.5
FEATURE [Part::Cylinder] Cylinder1310  label="Válec1310"
  Angle = 360
  AttacherType = Attacher::AttachEngine3D
  Height = 100
  Placement = pos=(-50,0,-90) rot=(0,0,1;0rad)
  Radius = 4
FEATURE [Part::Cylinder] Cylinder1311  label="Válec1311"
  Angle = 360
  AttacherType = Attacher::AttachEngine3D
  Height = 100
  Placement = pos=(36,34,-90) rot=(0,0,1;0rad)
  Radius = 4
FEATURE [Part::Cylinder] Cylinder1312  label="Válec1312"
  Angle = 360
  AttacherType = Attacher::AttachEngine3D
  Height = 100
  Placement = pos=(-36,34,-90) rot=(0,0,1;0rad)
  Radius = 4
FEATURE [Part::Cylinder] Cylinder1313  label="Válec1313"
  Angle = 360
  AttacherType = Attacher::AttachEngine3D
  Height = 40
  Placement = pos=(28,18,-18) rot=(0,0,1;0rad)
  Radius = 4
FEATURE [Part::Cylinder] Cylinder1314  label="Válec1314"
  Angle = 360
  AttacherType = Attacher::AttachEngine3D
  Height = 100
  Placement = pos=(-50,0,-90) rot=(0,0,1;0rad)
  Radius = 4
FEATURE [Part::Compound] Compound677  label="sbouby_baze_silne005"
  Links = -> [Cylinder1314,Cylinder1312,Cylinder1287,Cylinder1299,Cylinder1298,Cylinder1294]
FEATURE [Part::Cylinder] Cylinder1315  label="Válec1315"
  Angle = 360
  AttacherType = Attacher::AttachEngine3D
  Height = 100
  Placement = pos=(-36,34,-90) rot=(0,0,1;0rad)
  Radius = 4
FEATURE [Part::Cylinder] Cylinder1316  label="Válec1316"
  Angle = 360
  AttacherType = Attacher::AttachEngine3D
  Height = 100
  Placement = pos=(-36,34,-60) rot=(0,0,1;0rad)
  Radius = 1.5
FEATURE [Part::Cylinder] Cylinder1317  label="Válec1317"
  Angle = 360
  AttacherType = Attacher::AttachEngine3D
  Height = 100
  Placement = pos=(36,-34,-90) rot=(0,0,1;0rad)
  Radius = 4
FEATURE [Part::Box] Box247  label="Krychle247"
  AttacherType = Attacher::AttachEngine3D
  Height = 100
  Length = 200
  Placement = pos=(-60,44,-90) rot=(0,0,1;0rad)
  Width = 100
FEATURE [Part::Box] Box248  label="Krychle248"
  AttacherType = Attacher::AttachEngine3D
  Height = 100
  Length = 200
  Placement = pos=(-60,44,-90) rot=(0,0,1;0rad)
  Width = 100
FEATURE [Part::Box] Box249  label="Krychle249"
  AttacherType = Attacher::AttachEngine3D
  Height = 2
  Length = 6
  Placement = pos=(75,38,-22) rot=(0,0,1;0rad)
  Width = 6
FEATURE [Part::Box] Box250  label="Krychle250"
  AttacherType = Attacher::AttachEngine3D
  Height = 100
  Length = 200
  Placement = pos=(-60,-124,-90) rot=(0,0,1;0rad)
  Width = 100
FEATURE [Part::Cylinder] Cylinder1318  label="Válec1318"
  Angle = 360
  AttacherType = Attacher::AttachEngine3D
  Height = 32
  Placement = pos=(78,41,-42) rot=(0,0,1;0rad)
  Radius = 1.5
FEATURE [Part::Cylinder] Cylinder1319  label="Válec1319"
  Angle = 360
  AttacherType = Attacher::AttachEngine3D
  Height = 100
  Placement = pos=(14,0,-60) rot=(0,0,1;0rad)
  Radius = 1.5
FEATURE [Part::Cylinder] Cylinder1320  label="Válec1320"
  Angle = 360
  AttacherType = Attacher::AttachEngine3D
  Height = 32
  Placement = pos=(26,41,-42) rot=(0,0,1;0rad)
  Radius = 1.5
FEATURE [Part::Compound] Compound666
  Links = -> [Cylinder1320,Cylinder1318]
FEATURE [Part::Cylinder] Cylinder1321  label="Válec1321"
  Angle = 360
  AttacherType = Attacher::AttachEngine3D
  Height = 100
  Placement = pos=(-50,0,-60) rot=(0,0,1;0rad)
  Radius = 1.5
FEATURE [Part::Cylinder] Cylinder1322  label="Válec1322"
  Angle = 360
  AttacherType = Attacher::AttachEngine3D
  Height = 100
  Placement = pos=(90,0,-60) rot=(0,0,1;0rad)
  Radius = 1.5
FEATURE [Part::Cylinder] Cylinder1323  label="Válec1323"
  Angle = 360
  AttacherType = Attacher::AttachEngine3D
  Height = 100
  Placement = pos=(36,-34,-60) rot=(0,0,1;0rad)
  Radius = 1.5
FEATURE [Part::Cylinder] Cylinder1324  label="Válec1324"
  Angle = 360
  AttacherType = Attacher::AttachEngine3D
  Height = 100
  Placement = pos=(-36,-34,-60) rot=(0,0,1;0rad)
  Radius = 1.5
FEATURE [Part::Compound] Compound674  label="sbouby_baze003"
  Links = -> [Cylinder1321,Cylinder1316,Cylinder1324,Cylinder1309,Cylinder1283,Cylinder1323]
FEATURE [Part::Cylinder] Cylinder1325  label="Válec1325"
  Angle = 360
  AttacherType = Attacher::AttachEngine3D
  Height = 100
  Placement = pos=(50,0,-90) rot=(0,0,1;0rad)
  Radius = 4
FEATURE [Part::Cylinder] Cylinder1326  label="Válec1326"
  Angle = 360
  AttacherType = Attacher::AttachEngine3D
  Height = 100
  Placement = pos=(-50,0,-90) rot=(0,0,1;0rad)
  Radius = 4
FEATURE [Part::Cylinder] Cylinder1327  label="Válec1327"
  Angle = 360
  AttacherType = Attacher::AttachEngine3D
  Height = 100
  Placement = pos=(90,0,-18) rot=(0,0,1;0rad)
  Radius = 4
FEATURE [Part::Compound] Compound669  label="srouby_troj_silne004"
  Links = -> [Cylinder1327,Cylinder1305]
FEATURE [Part::Box] Box251  label="Krychle251"
  AttacherType = Attacher::AttachEngine3D
  Height = 2
  Length = 6
  Placement = pos=(23,38,-22) rot=(0,0,1;0rad)
  Width = 6
FEATURE [Part::Compound] Compound676
  Links = -> [Box249,Box251]
FEATURE [Part::Cylinder] Cylinder1328  label="Válec1328"
  Angle = 360
  AttacherType = Attacher::AttachEngine3D
  Height = 100
  Placement = pos=(36,34,-90) rot=(0,0,1;0rad)
  Radius = 4
FEATURE [Part::Compound] Compound668  label="sbouby_baze_silne003"
  Links = -> [Cylinder1326,Cylinder1315,Cylinder1284,Cylinder1301,Cylinder1328,Cylinder1317]
FEATURE [Part::Cylinder] Cylinder1329  label="Válec1329"
  Angle = 360
  AttacherType = Attacher::AttachEngine3D
  Height = 100
  Placement = pos=(-36,-34,-90) rot=(0,0,1;0rad)
  Radius = 4
FEATURE [Part::Compound] Compound675  label="sbouby_baze_silne004"
  Links = -> [Cylinder1310,Cylinder1300,Cylinder1329,Cylinder1325,Cylinder1311,Cylinder1304]
FEATURE [Part::Cylinder] Cylinder1330  label="Válec1330"
  Angle = 360
  AttacherType = Attacher::AttachEngine3D
  Height = 100
  Placement = pos=(90,0,-60) rot=(0,0,1;0rad)
  Radius = 1.5
FEATURE [Part::Compound] Compound670  label="srouby_troj006"
  Links = -> [Cylinder1330,Cylinder1302]
FEATURE [Part::Cylinder] Cylinder1331  label="Válec1331"
  Angle = 360
  AttacherType = Attacher::AttachEngine3D
  Height = 32
  Placement = pos=(26,41,-46) rot=(0,0,1;0rad)
  Radius = 1.5
FEATURE [Part::Cylinder] Cylinder1332  label="Válec1332"
  Angle = 360
  AttacherType = Attacher::AttachEngine3D
  Height = 100
  Placement = pos=(14,0,-18) rot=(0,0,1;0rad)
  Radius = 4
FEATURE [Part::Cylinder] Cylinder1333  label="Válec1333"
  Angle = 360
  AttacherType = Attacher::AttachEngine3D
  Height = 32
  Placement = pos=(78,41,-46) rot=(0,0,1;0rad)
  Radius = 1.5
FEATURE [Part::Compound] Compound678
  Links = -> [Cylinder1331,Cylinder1333]
FEATURE [Part::Cylinder] Cylinder1334  label="Válec1334"
  Angle = 360
  AttacherType = Attacher::AttachEngine3D
  Height = 100
  Placement = pos=(90,0,-18) rot=(0,0,1;0rad)
  Radius = 4
FEATURE [Part::Compound] Compound672  label="srouby_troj_silne003"
  Links = -> [Cylinder1334,Cylinder1332]
FEATURE [Part::Cylinder] Cylinder1335  label="Válec1335"
  Angle = 360
  AttacherType = Attacher::AttachEngine3D
  Height = 4
  Placement = pos=(52,0,-26) rot=(0,0,1;0rad)
  Radius = 59
FEATURE [Part::Cylinder] Cylinder1336  label="Válec1336"
  Angle = 360
  AttacherType = Attacher::AttachEngine3D
  Height = 100
  Placement = pos=(1,-12,-60) rot=(0,0,1;0rad)
  Radius = 1.5
FEATURE [Part::Cylinder] Cylinder1337  label="Válec1337"
  Angle = 360
  AttacherType = Attacher::AttachEngine3D
  Height = 100
  Placement = pos=(103,6,-60) rot=(0,0,1;0rad)
  Radius = 1.5
FEATURE [Part::Cylinder] Cylinder1338  label="Válec1338"
  Angle = 360
  AttacherType = Attacher::AttachEngine3D
  Height = 100
  Placement = pos=(-36,-34,-60) rot=(0,0,1;0rad)
  Radius = 1.5
FEATURE [Part::Cylinder] Cylinder1339  label="Válec1339"
  Angle = 360
  AttacherType = Attacher::AttachEngine3D
  Height = 20
  Placement = pos=(91,-21,-18) rot=(0,0,1;0rad)
  Radius = 4
FEATURE [Part::Compound] Compound664  label="srouby_monoblok_silne004"
  Links = -> [Cylinder1296,Cylinder1282,Cylinder1308,Cylinder1339,Cylinder1306,Cylinder1313,Cylinder1307,Cylinder1297]
FEATURE [Part::Cylinder] Cylinder1340  label="Válec1340"
  Angle = 360
  AttacherType = Attacher::AttachEngine3D
  Height = 100
  Placement = pos=(91,-21,-60) rot=(0,0,1;0rad)
  Radius = 1.5
FEATURE [Part::Cylinder] Cylinder1341  label="Válec1341"
  Angle = 360
  AttacherType = Attacher::AttachEngine3D
  Height = 100
  Placement = pos=(91,-21,-60) rot=(0,0,1;0rad)
  Radius = 1.5
FEATURE [Part::Cylinder] Cylinder1342  label="Válec1342"
  Angle = 360
  AttacherType = Attacher::AttachEngine3D
  Height = 16
  Placement = pos=(0,0,2) rot=(0,0,1;0rad)
  Radius = 59
FEATURE [Part::Cylinder] Cylinder1343  label="Válec1343"
  Angle = 360
  AttacherType = Attacher::AttachEngine3D
  Height = 100
  Placement = pos=(103,-12,-60) rot=(0,0,1;0rad)
  Radius = 1.5
FEATURE [Part::Cylinder] Cylinder1344  label="Válec1344"
  Angle = 360
  AttacherType = Attacher::AttachEngine3D
  Height = 100
  Placement = pos=(-50,0,-60) rot=(0,0,1;0rad)
  Radius = 1.5
FEATURE [Part::Cylinder] Cylinder1345  label="Válec1345"
  Angle = 360
  AttacherType = Attacher::AttachEngine3D
  Height = 100
  Placement = pos=(13,-21,-60) rot=(0,0,1;0rad)
  Radius = 1.5
FEATURE [Part::Cylinder] Cylinder1346  label="Válec1346"
  Angle = 360
  AttacherType = Attacher::AttachEngine3D
  Height = 100
  Placement = pos=(76,18,-60) rot=(0,0,1;0rad)
  Radius = 1.5
FEATURE [Part::Cylinder] Cylinder1347  label="Válec1347"
  Angle = 360
  AttacherType = Attacher::AttachEngine3D
  Height = 100
  Placement = pos=(28,18,-60) rot=(0,0,1;0rad)
  Radius = 1.5
FEATURE [Part::Cylinder] Cylinder1348  label="Válec1348"
  Angle = 360
  AttacherType = Attacher::AttachEngine3D
  Height = 100
  Placement = pos=(1,6,-60) rot=(0,0,1;0rad)
  Radius = 1.5
FEATURE [Part::Compound] Compound673  label="srouby_monoblok003"
  Links = -> [Cylinder1343,Cylinder1337,Cylinder1346,Cylinder1341,Cylinder1345,Cylinder1347,Cylinder1336,Cylinder1348]
FEATURE [Part::Cylinder] Cylinder1349  label="Válec1349"
  Angle = 360
  AttacherType = Attacher::AttachEngine3D
  Height = 100
  Placement = pos=(-36,34,-60) rot=(0,0,1;0rad)
  Radius = 1.5
FEATURE [Part::Cylinder] Cylinder1350  label="Válec1350"
  Angle = 360
  AttacherType = Attacher::AttachEngine3D
  Height = 100
  Placement = pos=(36,34,-60) rot=(0,0,1;0rad)
  Radius = 1.5
FEATURE [Part::Cylinder] Cylinder1351  label="Válec1351"
  Angle = 360
  AttacherType = Attacher::AttachEngine3D
  Height = 100
  Placement = pos=(103,6,-60) rot=(0,0,1;0rad)
  Radius = 1.5
FEATURE [Part::Cylinder] Cylinder1352  label="Válec1352"
  Angle = 360
  AttacherType = Attacher::AttachEngine3D
  Height = 100
  Placement = pos=(50,0,-60) rot=(0,0,1;0rad)
  Radius = 1.5
FEATURE [Part::Cylinder] Cylinder1353  label="Válec1353"
  Angle = 360
  AttacherType = Attacher::AttachEngine3D
  Height = 100
  Placement = pos=(36,-34,-60) rot=(0,0,1;0rad)
  Radius = 1.5
FEATURE [Part::Compound] Compound671  label="sbouby_baze002"
  Links = -> [Cylinder1344,Cylinder1349,Cylinder1338,Cylinder1352,Cylinder1350,Cylinder1353]
FEATURE [Part::Cylinder] Cylinder1354  label="Válec1354"
  Angle = 360
  AttacherType = Attacher::AttachEngine3D
  Height = 100
  Placement = pos=(76,18,-60) rot=(0,0,1;0rad)
  Radius = 1.5
FEATURE [Part::Compound] Compound665  label="srouby_monoblok002"
  Links = -> [Cylinder1290,Cylinder1351,Cylinder1354,Cylinder1340,Cylinder1285,Cylinder1286,Cylinder1281,Cylinder1279]
FEATURE [Part::Cut] Cut315
  Base = -> Extrude002
  Tool = -> Compound673
FEATURE [Part::Compound] Compound679  label="srouby_troj007"
  Links = -> [Cylinder1322,Cylinder1319]
FEATURE [Part::Cut] Cut317
  Base = -> Cylinder1342
  Tool = -> Compound664
FEATURE [Part::Cut] Cut320
  Base = -> Cylinder1335
  Tool = -> Compound665
FEATURE [Part::Cut] Cut318
  Base = -> Cut320
  Tool = -> Compound677
FEATURE [Part::Cut] Cut322
  Base = -> Cut318
  Tool = -> Box250
FEATURE [Part::Cut] Cut321
  Base = -> Cut322
  Tool = -> Box248
FEATURE [Part::Cut] Cut327
  Base = -> Cut315
  Tool = -> Compound663
FEATURE [Part::Cut] Cut316
  Base = -> Cut327
  Tool = -> Compound668
FEATURE [Part::Cut] Cut323
  Base = -> Cut316
  Tool = -> Compound674
FEATURE [Part::Cut] Cut329
  Base = -> Cut323
  Tool = -> Box246
FEATURE [Part::Cut] Cut326
  Base = -> Cut329
  Tool = -> Box247
FEATURE [Part::Cut] Cut330
  Base = -> Cut326
  Tool = -> Compound676
FEATURE [Part::Cut] Cut328
  Base = -> Cut330
  Tool = -> Compound678
FEATURE [Part::Cut] Cut314
  Base = -> Cut328
  Tool = -> Compound670
FEATURE [Part::Cut] Cut325
  Base = -> Cut314
  Tool = -> Compound669
FEATURE [Part::Chamfer] Chamfer039
  Base = -> Cut325
  Edges = 2 edges r=6: [Edge40,Edge42]
FEATURE [Part::Cut] Cut332
  Base = -> Cut317
  Tool = -> Compound675
FEATURE [Part::Cut] Cut319
  Base = -> Cut332
  Tool = -> Compound671
FEATURE [Part::Chamfer] Chamfer038
  Base = -> Cut319
  Edges = 1 edges r=4: [Edge3]
FEATURE [Part::Cut] Cut331
  Base = -> Chamfer038
  Placement = pos=(0,0,4) rot=(0,0,1;0rad)
  Tool = -> Compound672
FEATURE [Part::Cut] Cut333
  Base = -> Cut321
  Tool = -> Compound666
FEATURE [Part::Cut] Cut324
  Base = -> Cut333
  Tool = -> Compound679
FEATURE [Part::Compound] Compound667  label="bazovina_neck_foreshift001"
  Links = -> [Cut324,Cut331,Chamfer039]
FEATURE [Part::Mirroring] mirror  label="bazovina_neck_foreshift_mirror"
  Base = (200,0,0)
  Normal = (1e-16,-1,0)
  Placement = pos=(0,150,0) rot=(0,0,1;0rad)
  Source = -> Compound667
FEATURE [Mesh::Feature] Mesh001  label="bazovina_neck_foreshift_mirror (Meshed)"
FEATURE [Part::Cylinder] Cylinder1355  label="Válec1355"
  Angle = 360
  AttacherType = Attacher::AttachEngine3D
  Height = 60
  Placement = pos=(35.5,61.4878,0) rot=(0,0,1;2.61799rad)
  Radius = 1.5
FEATURE [Part::Cylinder] Cylinder1356  label="Válec1356"
  Angle = 360
  AttacherType = Attacher::AttachEngine3D
  Height = 60
  Placement = pos=(-61.4878,35.5,0) rot=(0,0,1;4.18879rad)
  Radius = 1.5
FEATURE [Part::Cylinder] Cylinder1357  label="Válec1357"
  Angle = 360
  AttacherType = Attacher::AttachEngine3D
  Height = 60
  Placement = pos=(-61.4878,-35.5,0) rot=(0,0,-1;1.0472rad)
  Radius = 1.5
FEATURE [Part::Cylinder] Cylinder1358  label="Válec1358"
  Angle = 360
  AttacherType = Attacher::AttachEngine3D
  Height = 60
  Placement = pos=(71,-1.8e-14,0) rot=(0,0,1;1.5708rad)
  Radius = 1.5
FEATURE [Part::Cylinder] Cylinder1359  label="Válec1359"
  Angle = 360
  AttacherType = Attacher::AttachEngine3D
  Height = 60
  Placement = pos=(61.4878,35.5,0) rot=(0,0,1;2.0944rad)
  Radius = 1.5
FEATURE [Part::Cylinder] Cylinder979  label="Válec979"
  Angle = 360
  AttacherType = Attacher::AttachEngine3D
  Height = 60
  Placement = pos=(3.1e-14,71,0) rot=(0,0,1;3.14159rad)
  Radius = 1.5
FEATURE [Part::Cylinder] Cylinder1360  label="Válec1360"
  Angle = 360
  AttacherType = Attacher::AttachEngine3D
  Height = 60
  Placement = pos=(-71,2.7e-14,0) rot=(0,0,-1;1.5708rad)
  Radius = 1.5
FEATURE [Part::Cylinder] Cylinder1361  label="Válec1361"
  Angle = 360
  AttacherType = Attacher::AttachEngine3D
  Height = 60
  Placement = pos=(61.4878,-35.5,0) rot=(0,0,1;1.0472rad)
  Radius = 1.5
FEATURE [Part::Cylinder] Cylinder1362  label="Válec1362"
  Angle = 360
  AttacherType = Attacher::AttachEngine3D
  Height = 60
  Placement = pos=(0,-71,0) rot=(0,0,1;0rad)
  Radius = 1.5
FEATURE [Part::Cylinder] Cylinder1363  label="Válec1363"
  Angle = 360
  AttacherType = Attacher::AttachEngine3D
  Height = 60
  Placement = pos=(35.5,-61.4878,0) rot=(0,0,1;0.523599rad)
  Radius = 1.5
FEATURE [Part::Cylinder] Cylinder1364  label="Válec1364"
  Angle = 360
  AttacherType = Attacher::AttachEngine3D
  Height = 60
  Placement = pos=(-35.5,61.4878,0) rot=(0,0,1;3.66519rad)
  Radius = 1.5
FEATURE [Part::Compound] Compound680
  Links = -> [Cylinder1362,Cylinder1363,Cylinder1361,Cylinder1358,Cylinder1359,Cylinder1355,Cylinder979,Cylinder1364,Cylinder1356,Cylinder1360,Cylinder1357]
FEATURE [Part::Cylinder] Cylinder1365  label="Válec1365"
  Angle = 360
  AttacherType = Attacher::AttachEngine3D
  Height = 3
  Placement = pos=(35.5,61.4878,0) rot=(0,0,1;2.61799rad)
  Radius = 3
FEATURE [Part::Cylinder] Cylinder1366  label="Válec1366"
  Angle = 360
  AttacherType = Attacher::AttachEngine3D
  Height = 3
  Placement = pos=(-61.4878,35.5,0) rot=(0,0,1;4.18879rad)
  Radius = 3
FEATURE [Part::Cylinder] Cylinder1367  label="Válec1367"
  Angle = 360
  AttacherType = Attacher::AttachEngine3D
  Height = 3
  Placement = pos=(-71,2.7e-14,0) rot=(0,0,-1;1.5708rad)
  Radius = 3
FEATURE [Part::FeaturePython] Tube031  # WARN: FeaturePython — macro-defined, semantics opaque (R4)
  AttacherType = Attacher::AttachEngine3D
  Height = 6
  InnerRadius = 61
  OuterRadius = 74
  Placement = pos=(0,0,14) rot=(0,0,1;0rad)
FEATURE [Part::Cylinder] Cylinder1368  label="Válec1368"
  Angle = 360
  AttacherType = Attacher::AttachEngine3D
  Height = 3
  Placement = pos=(71,-1.8e-14,0) rot=(0,0,1;1.5708rad)
  Radius = 3
FEATURE [Part::Cylinder] Cylinder1369  label="Válec1369"
  Angle = 360
  AttacherType = Attacher::AttachEngine3D
  Height = 3
  Placement = pos=(61.4878,35.5,0) rot=(0,0,1;2.0944rad)
  Radius = 3
FEATURE [Part::Cylinder] Cylinder1370  label="Válec1370"
  Angle = 360
  AttacherType = Attacher::AttachEngine3D
  Height = 3
  Placement = pos=(3.1e-14,71,0) rot=(0,0,1;3.14159rad)
  Radius = 3
FEATURE [Part::Cylinder] Cylinder1371  label="Válec1371"
  Angle = 360
  AttacherType = Attacher::AttachEngine3D
  Height = 3
  Placement = pos=(35.5,-61.4878,0) rot=(0,0,1;0.523599rad)
  Radius = 3
FEATURE [Part::Cylinder] Cylinder1372  label="Válec1372"
  Angle = 360
  AttacherType = Attacher::AttachEngine3D
  Height = 3
  Placement = pos=(61.4878,-35.5,0) rot=(0,0,1;1.0472rad)
  Radius = 3
FEATURE [Part::Cylinder] Cylinder1373  label="Válec1373"
  Angle = 360
  AttacherType = Attacher::AttachEngine3D
  Height = 3
  Placement = pos=(-61.4878,-35.5,0) rot=(0,0,-1;1.0472rad)
  Radius = 3
FEATURE [Part::Cylinder] Cylinder1374  label="Válec1374"
  Angle = 360
  AttacherType = Attacher::AttachEngine3D
  Height = 3
  Placement = pos=(0,-71,0) rot=(0,0,1;0rad)
  Radius = 3
FEATURE [Part::Cylinder] Cylinder1375  label="Válec1375"
  Angle = 360
  AttacherType = Attacher::AttachEngine3D
  Height = 3
  Placement = pos=(-35.5,61.4878,0) rot=(0,0,1;3.66519rad)
  Radius = 3
FEATURE [Part::Compound] Compound681
  Links = -> [Cylinder1374,Cylinder1371,Cylinder1372,Cylinder1368,Cylinder1369,Cylinder1365,Cylinder1370,Cylinder1375,Cylinder1366,Cylinder1367,Cylinder1373]
  Placement = pos=(0,0,17) rot=(0,0,1;0rad)
FEATURE [Part::Chamfer] Chamfer040
  Base = -> Tube031
  Edges = 1 edges r=3: [Edge1]
FEATURE [Part::Cut] Cut334
  Base = -> Chamfer040
  Tool = -> Compound681
FEATURE [Part::Cut] Cut335  label="bazovina_part-G_seal"
  Base = -> Cut334
  Placement = pos=(0,0,30) rot=(0.866025,0.5,0;3.14159rad)
  Tool = -> Compound680
FEATURE [Part::Cylinder] Cylinder1376  label="Válec1376"
  Angle = 360
  AttacherType = Attacher::AttachEngine3D
  Height = 18
  Placement = pos=(34.6278,22.6371,43.6023) rot=(-0.009819,-0.0017,0.99995;2.52972rad)
  Radius = 8
FEATURE [Part::Cylinder] Cylinder1377  label="Válec1377"
  Angle = 360
  AttacherType = Attacher::AttachEngine3D
  Height = 100
  Placement = pos=(16.0727,38.8029,0) rot=(0,0,1;3.14159rad)
  Radius = 1.5
FEATURE [Part::Cylinder] Cylinder1378  label="Válec1378"
  Angle = 360
  AttacherType = Attacher::AttachEngine3D
  Height = 18
  Placement = pos=(16.0725,38.7989,43) rot=(0,0,1;3.14159rad)
  Radius = 8
FEATURE [Part::Cylinder] Cylinder1379  label="Válec1379"
  Angle = 360
  AttacherType = Attacher::AttachEngine3D
  Height = 100
  Placement = pos=(38.8029,-16.0727,0) rot=(0,0,1;1.5708rad)
  Radius = 1.5
FEATURE [Part::Cylinder] Cylinder1380  label="Válec1380"
  Angle = 360
  AttacherType = Attacher::AttachEngine3D
  Height = 100
  Placement = pos=(16.0727,-38.8029,0) rot=(0,0,1;0.785398rad)
  Radius = 1.5
FEATURE [Part::Cylinder] Cylinder1381  label="Válec1381"
  Angle = 360
  AttacherType = Attacher::AttachEngine3D
  Height = 18
  Placement = pos=(16.07,-38.8,43) rot=(0,0,1;0.785398rad)
  Radius = 8
FEATURE [Part::Cylinder] Cylinder1382  label="Válec1382"
  Angle = 360
  AttacherType = Attacher::AttachEngine3D
  Height = 100
  Placement = pos=(35.44,22.5307,0.610113) rot=(-0.009819,-0.0017,0.99995;2.52972rad)
  Radius = 1.5
FEATURE [Part::Cylinder] Cylinder1383  label="Válec1383"
  Angle = 360
  AttacherType = Attacher::AttachEngine3D
  Height = 100
  Placement = pos=(-16.0727,38.8029,0) rot=(0,0,1;3.92699rad)
  Radius = 1.5
FEATURE [Part::Cylinder] Cylinder1384  label="Válec1384"
  Angle = 360
  AttacherType = Attacher::AttachEngine3D
  Height = 18
  Placement = pos=(38.7989,-16.0725,43) rot=(0,0,1;1.5708rad)
  Radius = 8
FEATURE [Part::Cylinder] Cylinder1385  label="Válec1385"
  Angle = 360
  AttacherType = Attacher::AttachEngine3D
  Height = 18
  Placement = pos=(-21.7485,-35.6902,43.196) rot=(0.02393,0.106372,-0.994038;0.174533rad)
  Radius = 8
FEATURE [Part::Cylinder] Cylinder1386  label="Válec1386"
  Angle = 360
  AttacherType = Attacher::AttachEngine3D
  Height = 100
  Placement = pos=(-38.8029,16.0727,0) rot=(0,0,-1;1.5708rad)
  Radius = 1.5
FEATURE [Part::FeaturePython] Tube035  # WARN: FeaturePython — macro-defined, semantics opaque (R4)
  AttacherType = Attacher::AttachEngine3D
  Height = 19
  InnerRadius = 30
  OuterRadius = 58
  Placement = pos=(0,0,42) rot=(0,0,1;0rad)
FEATURE [Part::Cylinder] Cylinder1387  label="Válec1387"
  Angle = 360
  AttacherType = Attacher::AttachEngine3D
  Height = 18
  Placement = pos=(-38.8,-16.07,43) rot=(0,0,-1;0.785398rad)
  Radius = 8
FEATURE [Part::Cylinder] Cylinder1388  label="Válec1388"
  Angle = 360
  AttacherType = Attacher::AttachEngine3D
  Height = 100
  Placement = pos=(-38.8029,-16.0727,0) rot=(0,0,-1;0.785398rad)
  Radius = 1.5
FEATURE [Part::Cylinder] Cylinder1389  label="Válec1389"
  Angle = 360
  AttacherType = Attacher::AttachEngine3D
  Height = 18
  Placement = pos=(-38.7989,16.0725,43) rot=(0,0,-1;1.5708rad)
  Radius = 8
FEATURE [Part::Cylinder] Cylinder1390  label="Válec1390"
  Angle = 360
  AttacherType = Attacher::AttachEngine3D
  Height = 100
  Placement = pos=(-22.5281,-35.4464,0.203785) rot=(0.02393,0.106372,-0.994038;0.174533rad)
  Radius = 1.5
FEATURE [Part::Compound] Compound684
  Links = -> [Cylinder1380,Cylinder1379,Cylinder1382,Cylinder1377,Cylinder1383,Cylinder1386,Cylinder1388,Cylinder1390]
FEATURE [Part::Cylinder] Cylinder1391  label="Válec1391"
  Angle = 360
  AttacherType = Attacher::AttachEngine3D
  Height = 18
  Placement = pos=(-16.07,38.8,43) rot=(0,0,1;3.92699rad)
  Radius = 8
FEATURE [Part::Compound] Compound682
  Links = -> [Cylinder1387,Cylinder1389,Cylinder1391,Cylinder1378,Cylinder1376,Cylinder1384,Cylinder1381,Cylinder1385]
  Placement = pos=(0,0,3) rot=(0,0,1;0rad)
FEATURE [Part::Cut] Cut336
  Base = -> Tube035
  Tool = -> Compound682
FEATURE [Part::Compound] Compound683
  Links = -> [Cut336]
FEATURE [Part::Cut] Cut337  label="bazovina-part-F_dirovina1"
  Base = -> Compound683
  Tool = -> Compound684
FEATURE [Part::Cylinder] Cylinder1392  label="Válec1392"
  Angle = 360
  AttacherType = Attacher::AttachEngine3D
  Height = 25
  Placement = pos=(-21.7485,-35.6902,43.196) rot=(0.02393,0.106372,-0.994038;0.174533rad)
  Radius = 8
FEATURE [Part::Cylinder] Cylinder1393  label="Válec1393"
  Angle = 360
  AttacherType = Attacher::AttachEngine3D
  Height = 25
  Placement = pos=(-38.8,-16.07,43) rot=(0,0,-1;0.785398rad)
  Radius = 8
FEATURE [Part::Cylinder] Cylinder1394  label="Válec1394"
  Angle = 360
  AttacherType = Attacher::AttachEngine3D
  Height = 25
  Placement = pos=(-38.7989,16.0725,43) rot=(0,0,-1;1.5708rad)
  Radius = 8
FEATURE [Part::Cylinder] Cylinder1395  label="Válec1395"
  Angle = 360
  AttacherType = Attacher::AttachEngine3D
  Height = 25
  Placement = pos=(-16.07,38.8,43) rot=(0,0,1;3.92699rad)
  Radius = 8
FEATURE [Part::Cylinder] Cylinder1396  label="Válec1396"
  Angle = 360
  AttacherType = Attacher::AttachEngine3D
  Height = 25
  Placement = pos=(16.0725,38.7989,43) rot=(0,0,1;3.14159rad)
  Radius = 8
FEATURE [Part::Cylinder] Cylinder1397  label="Válec1397"
  Angle = 360
  AttacherType = Attacher::AttachEngine3D
  Height = 25
  Placement = pos=(34.6278,22.6371,43.6023) rot=(-0.009819,-0.0017,0.99995;2.52972rad)
  Radius = 8
FEATURE [Part::Cylinder] Cylinder1398  label="Válec1398"
  Angle = 360
  AttacherType = Attacher::AttachEngine3D
  Height = 25
  Placement = pos=(38.7989,-16.0725,43) rot=(0,0,1;1.5708rad)
  Radius = 8
FEATURE [Part::Cylinder] Cylinder1399  label="Válec1399"
  Angle = 360
  AttacherType = Attacher::AttachEngine3D
  Height = 25
  Placement = pos=(16.07,-38.8,43) rot=(0,0,1;0.785398rad)
  Radius = 8
FEATURE [Part::Compound] Compound685
  Links = -> [Cylinder1393,Cylinder1394,Cylinder1395,Cylinder1396,Cylinder1397,Cylinder1398,Cylinder1399,Cylinder1392]
  Placement = pos=(0,0,3) rot=(0,0,1;0rad)
FEATURE [Part::FeaturePython] Tube036  # WARN: FeaturePython — macro-defined, semantics opaque (R4)
  AttacherType = Attacher::AttachEngine3D
  Height = 17
  InnerRadius = 30
  OuterRadius = 37
  Placement = pos=(0,0,48) rot=(0,0,1;0rad)
FEATURE [Part::Cut] Cut338
  Base = -> Tube036
  Tool = -> Compound685
FEATURE [Part::Compound] Compound686  label="bazovina-part-F_dirovina"
  Links = -> [Cut337,Cut338]
  Placement = pos=(0,0,0) rot=(0,0,1;0.785398rad)
FEATURE [Part::Cylinder] Cylinder1400  label="Válec1400"
  Angle = 360
  AttacherType = Attacher::AttachEngine3D
  Height = 50
  Placement = pos=(34,36,0) rot=(0,0,1;0rad)
  Radius = 1.5
FEATURE [Part::Cylinder] Cylinder1401  label="Válec1401"
  Angle = 360
  AttacherType = Attacher::AttachEngine3D
  Height = 20
  Placement = pos=(0,-64.5,4.5) rot=(0,0,1;0rad)
  Radius = 3.5
FEATURE [Part::Cylinder] Cylinder1402  label="Válec1402"
  Angle = 360
  AttacherType = Attacher::AttachEngine3D
  Height = 50
  Placement = pos=(-34,-36,0) rot=(0,0,1;0rad)
  Radius = 1.5
FEATURE [Part::Cylinder] Cylinder1403  label="Válec1403"
  Angle = 360
  AttacherType = Attacher::AttachEngine3D
  Height = 50
  Placement = pos=(34,-36,0) rot=(0,0,1;0rad)
  Radius = 1.5
FEATURE [Part::Cylinder] Cylinder1404  label="Válec1404"
  Angle = 360
  AttacherType = Attacher::AttachEngine3D
  Height = 50
  Placement = pos=(-34,36,0) rot=(0,0,1;0rad)
  Radius = 1.5
FEATURE [Part::Cylinder] Cylinder1405  label="Válec1405"
  Angle = 360
  AttacherType = Attacher::AttachEngine3D
  Height = 50
  Placement = pos=(0,50,0) rot=(0,0,1;0rad)
  Radius = 1.5
FEATURE [Part::Cylinder] Cylinder1406  label="Válec1406"
  Angle = 360
  AttacherType = Attacher::AttachEngine3D
  Height = 50
  Placement = pos=(0,-50,0) rot=(0,0,1;0rad)
  Radius = 1.5
FEATURE [Part::Cylinder] Cylinder1407  label="Válec1407"
  Angle = 360
  AttacherType = Attacher::AttachEngine3D
  Height = 100
  Placement = pos=(-51,-12,0) rot=(0,0,1;0rad)
  Radius = 1.5
FEATURE [Part::Cylinder] Cylinder1408  label="Válec1408"
  Angle = 360
  AttacherType = Attacher::AttachEngine3D
  Height = 50
  Placement = pos=(51,6,0) rot=(0,0,1;0rad)
  Radius = 1.5
FEATURE [Part::Cylinder] Cylinder1409  label="Válec1409"
  Angle = 360
  AttacherType = Attacher::AttachEngine3D
  Height = 7
  Placement = pos=(51,6,50) rot=(0,0,1;0rad)
  Radius = 3
FEATURE [Part::Cylinder] Cylinder1410  label="Válec1410"
  Angle = 360
  AttacherType = Attacher::AttachEngine3D
  Height = 7
  Placement = pos=(-51,6,50) rot=(0,0,1;0rad)
  Radius = 3
FEATURE [Part::FeaturePython] Tube037  # WARN: FeaturePython — macro-defined, semantics opaque (R4)
  AttacherType = Attacher::AttachEngine3D
  Height = 13
  InnerRadius = 38
  OuterRadius = 64
  Placement = pos=(0,0,18) rot=(0,0,1;0rad)
FEATURE [Part::FeaturePython] Tube038  # WARN: FeaturePython — macro-defined, semantics opaque (R4)
  AttacherType = Attacher::AttachEngine3D
  Height = 1
  InnerRadius = 38
  OuterRadius = 58
  Placement = pos=(0,0,31) rot=(0,0,1;0rad)
FEATURE [Part::Torus] Torus005  label="Anuloid005"
  Angle1 = -180
  Angle2 = 180
  Angle3 = 360
  AttacherType = Attacher::AttachEngine3D
  Placement = pos=(0,0,24.5) rot=(0,0,1;0rad)
  Radius1 = 64.2
  Radius2 = 3.1
FEATURE [Part::Cut] Cut340
  Base = -> Tube037
  Tool = -> Torus005
FEATURE [Part::Cut] Cut339
  Base = -> Cut340
  Tool = -> Cylinder1401
FEATURE [Part::Box] Box252  label="Krychle252"
  AttacherType = Attacher::AttachEngine3D
  Height = 10
  Length = 6
  Placement = pos=(-37,33,40) rot=(0,0,1;0rad)
  Width = 6
FEATURE [Part::Box] Box253  label="Krychle253"
  AttacherType = Attacher::AttachEngine3D
  Height = 10
  Length = 6
  Placement = pos=(31,-39,40) rot=(0,0,1;0rad)
  Width = 6
FEATURE [Part::Cylinder] Cylinder1411  label="Válec1411"
  Angle = 360
  AttacherType = Attacher::AttachEngine3D
  Height = 50
  Placement = pos=(-51,6,0) rot=(0,0,1;0rad)
  Radius = 1.5
FEATURE [Part::Cylinder] Cylinder1412  label="Válec1412"
  Angle = 360
  AttacherType = Attacher::AttachEngine3D
  Height = 100
  Placement = pos=(51,-12,0) rot=(0,0,1;0rad)
  Radius = 1.5
FEATURE [Part::Compound] Compound691
  Links = -> [Cylinder1404,Cylinder1400,Cylinder1402,Cylinder1403,Cylinder1405,Cylinder1406,Cylinder1407,Cylinder1408,Cylinder1411,Cylinder1412]
FEATURE [Part::Cut] Cut341
  Base = -> Cut339
  Tool = -> Compound691
FEATURE [Part::Cylinder] Cylinder1413  label="Válec1413"
  Angle = 360
  AttacherType = Attacher::AttachEngine3D
  Height = 7
  Placement = pos=(51,-12,50) rot=(0,0,1;0rad)
  Radius = 3
FEATURE [Part::Cylinder] Cylinder1414  label="Válec1414"
  Angle = 360
  AttacherType = Attacher::AttachEngine3D
  Height = 7
  Placement = pos=(-51,-12,50) rot=(0,0,1;0rad)
  Radius = 3
FEATURE [Part::Cylinder] Cylinder1415  label="Válec1415"
  Angle = 360
  AttacherType = Attacher::AttachEngine3D
  Height = 7
  Placement = pos=(51,6,50) rot=(0,0,1;0rad)
  Radius = 3
FEATURE [Part::Cylinder] Cylinder1416  label="Válec1416"
  Angle = 360
  AttacherType = Attacher::AttachEngine3D
  Height = 7
  Placement = pos=(-51,-12,50) rot=(0,0,1;0rad)
  Radius = 3
FEATURE [Part::Cylinder] Cylinder1417  label="Válec1417"
  Angle = 360
  AttacherType = Attacher::AttachEngine3D
  Height = 7
  Placement = pos=(-51,6,50) rot=(0,0,1;0rad)
  Radius = 3
FEATURE [Part::Compound] Compound692
  Links = -> [Cylinder1416,Cylinder1413,Cylinder1409,Cylinder1417]
  Placement = pos=(0,0,-25) rot=(0,0,1;0rad)
FEATURE [Part::Cut] Cut343
  Base = -> Cut341
  Tool = -> Compound692
FEATURE [Part::Box] Box254  label="Krychle254"
  AttacherType = Attacher::AttachEngine3D
  Height = 10
  Length = 6
  Placement = pos=(-3,47,40) rot=(0,0,1;0rad)
  Width = 6
FEATURE [Part::Box] Box255  label="Krychle255"
  AttacherType = Attacher::AttachEngine3D
  Height = 10
  Length = 6
  Placement = pos=(-3,-53,40) rot=(0,0,1;0rad)
  Width = 6
FEATURE [Part::Box] Box256  label="Krychle256"
  AttacherType = Attacher::AttachEngine3D
  Height = 10
  Length = 6
  Placement = pos=(-37,-39,40) rot=(0,0,1;0rad)
  Width = 6
FEATURE [Part::Box] Box257  label="Krychle257"
  AttacherType = Attacher::AttachEngine3D
  Height = 10
  Length = 6
  Placement = pos=(31,33,40) rot=(0,0,1;0rad)
  Width = 6
FEATURE [Part::Compound] Compound693
  Links = -> [Box254,Box256,Box255,Box257,Box252,Box253]
  Placement = pos=(0,0,-18) rot=(0,0,1;0rad)
FEATURE [Part::Cut] Cut344
  Base = -> Cut343
  Tool = -> Compound693
FEATURE [Part::Cylinder] Cylinder1418  label="Válec1418"
  Angle = 360
  AttacherType = Attacher::AttachEngine3D
  Height = 7
  Placement = pos=(51,-12,50) rot=(0,0,1;0rad)
  Radius = 3
FEATURE [Part::Compound] Compound689
  Links = -> [Cylinder1414,Cylinder1418,Cylinder1415,Cylinder1410]
  Placement = pos=(0,0,-25) rot=(0,0,1;0rad)
FEATURE [Part::Cut] Cut342
  Base = -> Tube038
  Tool = -> Compound689
FEATURE [Part::Box] Box258  label="Krychle258"
  AttacherType = Attacher::AttachEngine3D
  Height = 10
  Length = 6
  Placement = pos=(-3,-53,40) rot=(0,0,1;0rad)
  Width = 6
FEATURE [Part::Box] Box259  label="Krychle259"
  AttacherType = Attacher::AttachEngine3D
  Height = 10
  Length = 6
  Placement = pos=(-37,33,40) rot=(0,0,1;0rad)
  Width = 6
FEATURE [Part::Box] Box260  label="Krychle260"
  AttacherType = Attacher::AttachEngine3D
  Height = 10
  Length = 6
  Placement = pos=(-3,47,40) rot=(0,0,1;0rad)
  Width = 6
FEATURE [Part::Box] Box261  label="Krychle261"
  AttacherType = Attacher::AttachEngine3D
  Height = 10
  Length = 6
  Placement = pos=(31,-39,40) rot=(0,0,1;0rad)
  Width = 6
FEATURE [Part::Box] Box262  label="Krychle262"
  AttacherType = Attacher::AttachEngine3D
  Height = 10
  Length = 6
  Placement = pos=(-37,-39,40) rot=(0,0,1;0rad)
  Width = 6
FEATURE [Part::Box] Box263  label="Krychle263"
  AttacherType = Attacher::AttachEngine3D
  Height = 10
  Length = 6
  Placement = pos=(31,33,40) rot=(0,0,1;0rad)
  Width = 6
FEATURE [Part::Compound] Compound694
  Links = -> [Box260,Box262,Box258,Box263,Box259,Box261]
  Placement = pos=(0,0,-18) rot=(0,0,1;0rad)
FEATURE [Part::Cut] Cut347
  Base = -> Cut342
  Tool = -> Compound694
FEATURE [Part::Box] Box264  label="Krychle264"
  AttacherType = Attacher::AttachEngine3D
  Height = 2
  Length = 6
  Placement = pos=(43.284,-12.6687,25) rot=(0,0,1;1.35263rad)
  Width = 8
FEATURE [Part::Box] Box265  label="Krychle265"
  AttacherType = Attacher::AttachEngine3D
  Height = 2
  Length = 6
  Placement = pos=(42.7226,14.4491,25) rot=(0,0,1;1.96349rad)
  Width = 8
FEATURE [Part::Box] Box266  label="Krychle266"
  AttacherType = Attacher::AttachEngine3D
  Height = 2
  Length = 6
  Placement = pos=(14.4491,-42.7226,25) rot=(0,0,1;0.392699rad)
  Width = 8
FEATURE [Part::Box] Box267  label="Krychle267"
  AttacherType = Attacher::AttachEngine3D
  Height = 2
  Length = 6
  Placement = pos=(-40.4265,19.9924,25) rot=(0,0,-1;1.96349rad)
  Width = 8
FEATURE [Part::Box] Box268  label="Krychle268"
  AttacherType = Attacher::AttachEngine3D
  Height = 2
  Length = 6
  Placement = pos=(19.9924,40.4265,25) rot=(0,0,1;2.74889rad)
  Width = 8
FEATURE [Part::Box] Box269  label="Krychle269"
  AttacherType = Attacher::AttachEngine3D
  Height = 2
  Length = 6
  Placement = pos=(-19.9924,-40.4265,25) rot=(0,0,-1;0.392699rad)
  Width = 8
FEATURE [Part::Box] Box270  label="Krychle270"
  AttacherType = Attacher::AttachEngine3D
  Height = 2
  Length = 6
  Placement = pos=(-44.5826,-6.81089,25) rot=(0,0,-1;1.35263rad)
  Width = 8
FEATURE [Part::Cylinder] Cylinder1419  label="Válec1419"
  Angle = 360
  AttacherType = Attacher::AttachEngine3D
  Height = 100
  Placement = pos=(16.0727,-38.8029,0) rot=(0,0,1;0.785398rad)
  Radius = 1.5
FEATURE [Part::Box] Box271  label="Krychle271"
  AttacherType = Attacher::AttachEngine3D
  Height = 2
  Length = 6
  Placement = pos=(-14.4491,42.7226,25) rot=(0,0,1;3.53429rad)
  Width = 8
FEATURE [Part::Compound] Compound690
  Links = -> [Box266,Box264,Box265,Box268,Box271,Box267,Box270,Box269]
FEATURE [Part::Cylinder] Cylinder1420  label="Válec1420"
  Angle = 360
  AttacherType = Attacher::AttachEngine3D
  Height = 100
  Placement = pos=(41.0044,-9.09046,0) rot=(0,0,1;1.74533rad)
  Radius = 1.5
FEATURE [Part::Cylinder] Cylinder1421  label="Válec1421"
  Angle = 360
  AttacherType = Attacher::AttachEngine3D
  Height = 100
  Placement = pos=(38.8029,16.0727,0) rot=(0,0,1;2.35619rad)
  Radius = 1.5
FEATURE [Part::Cylinder] Cylinder1422  label="Válec1422"
  Angle = 360
  AttacherType = Attacher::AttachEngine3D
  Height = 100
  Placement = pos=(-41.0044,-9.09046,0) rot=(0,0,-1;0.959931rad)
  Radius = 1.5
FEATURE [Part::Cylinder] Cylinder1423  label="Válec1423"
  Angle = 360
  AttacherType = Attacher::AttachEngine3D
  Height = 100
  Placement = pos=(-16.0727,38.8029,0) rot=(0,0,1;3.92699rad)
  Radius = 1.5
FEATURE [Part::Cylinder] Cylinder1424  label="Válec1424"
  Angle = 360
  AttacherType = Attacher::AttachEngine3D
  Height = 100
  Placement = pos=(16.0727,38.8029,0) rot=(0,0,1;3.14159rad)
  Radius = 1.5
FEATURE [Part::Cylinder] Cylinder1425  label="Válec1425"
  Angle = 360
  AttacherType = Attacher::AttachEngine3D
  Height = 100
  Placement = pos=(-38.8029,16.0727,0) rot=(0,0,-1;1.5708rad)
  Radius = 1.5
FEATURE [Part::Cylinder] Cylinder1426  label="Válec1426"
  Angle = 360
  AttacherType = Attacher::AttachEngine3D
  Height = 100
  Placement = pos=(-16.0727,-38.8029,0) rot=(0,0,1;0rad)
  Radius = 1.5
FEATURE [Part::Compound] Compound687
  Links = -> [Cylinder1419,Cylinder1420,Cylinder1421,Cylinder1424,Cylinder1423,Cylinder1425,Cylinder1422,Cylinder1426]
FEATURE [Part::Cut] Cut348
  Base = -> Cut347
  Tool = -> Compound687
FEATURE [Part::Cylinder] Cylinder1427  label="Válec1427"
  Angle = 360
  AttacherType = Attacher::AttachEngine3D
  Height = 100
  Placement = pos=(16.0727,38.8029,0) rot=(0,0,1;3.14159rad)
  Radius = 1.5
FEATURE [Part::Cylinder] Cylinder1428  label="Válec1428"
  Angle = 360
  AttacherType = Attacher::AttachEngine3D
  Height = 100
  Placement = pos=(16.0727,-38.8029,0) rot=(0,0,1;0.785398rad)
  Radius = 1.5
FEATURE [Part::Cylinder] Cylinder1429  label="Válec1429"
  Angle = 360
  AttacherType = Attacher::AttachEngine3D
  Height = 100
  Placement = pos=(-38.8029,16.0727,0) rot=(0,0,-1;1.5708rad)
  Radius = 1.5
FEATURE [Part::Cylinder] Cylinder1430  label="Válec1430"
  Angle = 360
  AttacherType = Attacher::AttachEngine3D
  Height = 100
  Placement = pos=(-41.0044,-9.09046,0) rot=(0,0,-1;0.959931rad)
  Radius = 1.5
FEATURE [Part::Cylinder] Cylinder1431  label="Válec1431"
  Angle = 360
  AttacherType = Attacher::AttachEngine3D
  Height = 100
  Placement = pos=(-16.0727,-38.8029,0) rot=(0,0,1;0rad)
  Radius = 1.5
FEATURE [Part::Cylinder] Cylinder1432  label="Válec1432"
  Angle = 360
  AttacherType = Attacher::AttachEngine3D
  Height = 100
  Placement = pos=(38.8029,16.0727,0) rot=(0,0,1;2.35619rad)
  Radius = 1.5
FEATURE [Part::Cylinder] Cylinder1433  label="Válec1433"
  Angle = 360
  AttacherType = Attacher::AttachEngine3D
  Height = 100
  Placement = pos=(41.0044,-9.09046,0) rot=(0,0,1;1.74533rad)
  Radius = 1.5
FEATURE [Part::Cylinder] Cylinder1434  label="Válec1434"
  Angle = 360
  AttacherType = Attacher::AttachEngine3D
  Height = 100
  Placement = pos=(-16.0727,38.8029,0) rot=(0,0,1;3.92699rad)
  Radius = 1.5
FEATURE [Part::Compound] Compound688
  Links = -> [Cylinder1428,Cylinder1433,Cylinder1432,Cylinder1427,Cylinder1434,Cylinder1429,Cylinder1430,Cylinder1431]
  Placement = pos=(0,0,20) rot=(0,0,1;0rad)
FEATURE [Part::Cut] Cut345
  Base = -> Cut344
  Tool = -> Compound688
FEATURE [Part::Cut] Cut346
  Base = -> Cut345
  Tool = -> Compound690
FEATURE [Part::Cylinder] Cylinder1435  label="Válec1435"
  Angle = 360
  AttacherType = Attacher::AttachEngine3D
  Height = 100
  Placement = pos=(-39,-21,0) rot=(0,0,1;0rad)
  Radius = 1.5
FEATURE [Part::Cylinder] Cylinder1436  label="Válec1436"
  Angle = 360
  AttacherType = Attacher::AttachEngine3D
  Height = 100
  Placement = pos=(39,-21,0) rot=(0,0,1;0rad)
  Radius = 1.5
FEATURE [Part::Compound] Compound695
  Links = -> [Cylinder1435,Cylinder1436]
FEATURE [Part::Cylinder] Cylinder1437  label="Válec1437"
  Angle = 360
  AttacherType = Attacher::AttachEngine3D
  Height = 7
  Placement = pos=(-39,-21,50) rot=(0,0,1;0rad)
  Radius = 3
FEATURE [Part::Cylinder] Cylinder1438  label="Válec1438"
  Angle = 360
  AttacherType = Attacher::AttachEngine3D
  Height = 7
  Placement = pos=(39,-21,50) rot=(0,0,1;0rad)
  Radius = 3
FEATURE [Part::Compound] Compound696
  Links = -> [Cylinder1437,Cylinder1438]
  Placement = pos=(0,0,-25) rot=(0,0,1;0rad)
FEATURE [Part::Cut] Cut349
  Base = -> Cut348
  Tool = -> Compound696
FEATURE [Part::Cylinder] Cylinder1439  label="Válec1439"
  Angle = 360
  AttacherType = Attacher::AttachEngine3D
  Height = 7
  Placement = pos=(-39,-21,50) rot=(0,0,1;0rad)
  Radius = 3
FEATURE [Part::Cylinder] Cylinder1440  label="Válec1440"
  Angle = 360
  AttacherType = Attacher::AttachEngine3D
  Height = 7
  Placement = pos=(39,-21,50) rot=(0,0,1;0rad)
  Radius = 3
FEATURE [Part::Compound] Compound697
  Links = -> [Cylinder1439,Cylinder1440]
  Placement = pos=(0,0,-25) rot=(0,0,1;0rad)
FEATURE [Part::Cut] Cut350
  Base = -> Cut346
  Tool = -> Compound697
FEATURE [Part::Cut] Cut351
  Base = -> Cut350
  Tool = -> Compound695
FEATURE [Part::Compound] Compound698  label="bazovina-part-C_loziskovina"
  Links = -> [Cut349,Cut351]
